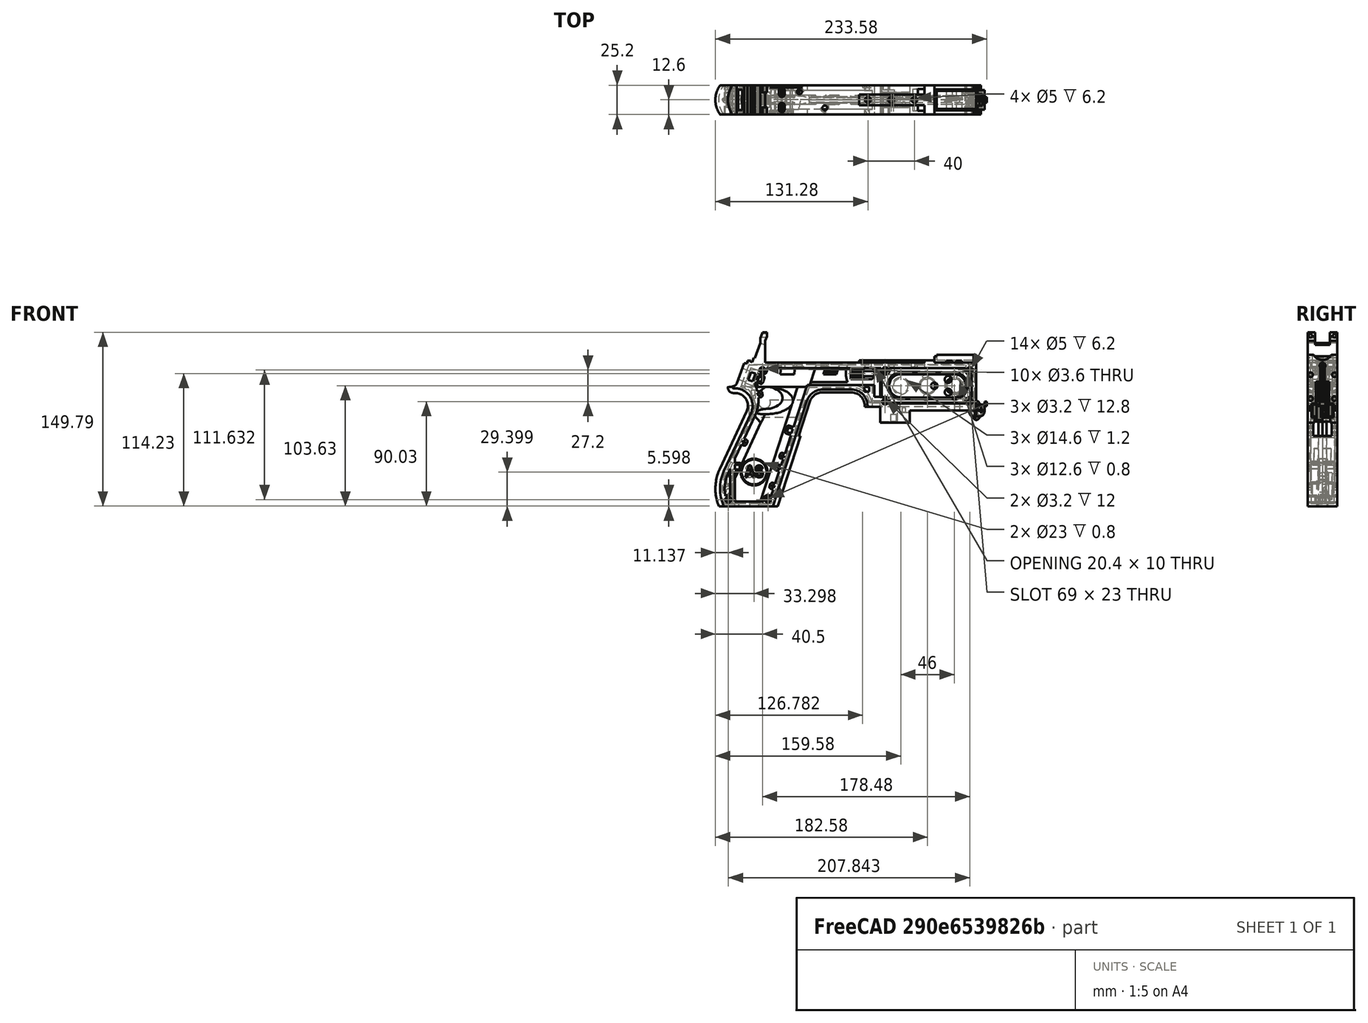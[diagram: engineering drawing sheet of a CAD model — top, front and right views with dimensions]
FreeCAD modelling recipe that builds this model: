
FCSTD DOCUMENT  (FreeCAD 1.0R39319 (Git))
Label: PICON-OF_ver_51
License: All rights reserved
LicenseURL: https://en.wikipedia.org/wiki/All_rights_reserved
objects: Sketcher::SketchObject×123, Part::Extrusion×63, Part::Cut×48, PartDesign::Pad×29, PartDesign::Pocket×20, PartDesign::Chamfer×15, PartDesign::Body×10, PartDesign::Fillet×6, Part::MultiFuse×5, Part::Part2DObjectPython×4, PartDesign::SubtractivePipe×4, PartDesign::SubtractiveLoft×4, PartDesign::Plane×3, PartDesign::SubShapeBinder×2, Part::Sweep×1, PartDesign::ShapeBinder×1, Mesh::Feature×1, PartDesign::Point×1, PartDesign::Groove×1
note: 621 computed .brp shape members not serialized (recipe doc carries the construction recipe); baked Part::Feature solids carry a one-line shape summary decoded from their .brp

FEATURE [Sketcher::SketchObject] Sketch  label="corpo principale"
  ArcFitTolerance = 1e-06
  AttacherType = Attacher::AttachEngine3D
  AttachmentSupport = -> [XZ_Plane]
  FullyConstrained = true
  MakeInternals = false
  MapMode = 5
  Placement = pos=(0,0,0) rot=(1,0,0;1.5708rad)
  sketch-geometry (65):
    g0: LineSegment StartX=0 StartY=0 StartZ=0 EndX=-57.2 EndY=0 EndZ=0
    g1: LineSegment StartX=-57.2 StartY=0 StartZ=0 EndX=-57.2 EndY=-10.4 EndZ=0
    g2: LineSegment StartX=-57.2 StartY=-10.4 StartZ=0 EndX=-82.8 EndY=-10.4 EndZ=0
    g3: LineSegment StartX=-82.8 StartY=-10.4 StartZ=0 EndX=-82.8 EndY=3.2 EndZ=0
    g4: LineSegment StartX=-82.8 StartY=3.2 StartZ=0 EndX=-93.6 EndY=3.2 EndZ=0
    g5: LineSegment StartX=-93.6 StartY=3.2 StartZ=0 EndX=-93.6 EndY=4 EndZ=0
    g6: LineSegment StartX=-107.6 StartY=18 StartZ=0 EndX=-132.428 EndY=18 EndZ=0
    g7: LineSegment StartX=-145.743 StartY=8.32624 StartZ=0 EndX=-175.232 EndY=-82.4316 EndZ=0
    g8: LineSegment StartX=-175.232 StartY=-82.4316 StartZ=0 EndX=-217.232 EndY=-82.4316 EndZ=0
    g9: LineSegment StartX=-217.232 StartY=-52.1862 StartZ=0 EndX=-193.988 EndY=-2.33927 EndZ=0
    g10: LineSegment StartX=-206.196 StartY=23.0857 StartZ=0 EndX=-199.861 EndY=40.4914 EndZ=0
    g11: LineSegment StartX=-199.861 StartY=40.4914 StartZ=0 EndX=-197.061 EndY=40.4914 EndZ=0
    g12: LineSegment StartX=-197.061 StartY=40.4914 StartZ=0 EndX=-197.061 EndY=42.8914 EndZ=0
    g13: LineSegment StartX=-197.061 StartY=42.8914 StartZ=0 EndX=-194.261 EndY=42.8914 EndZ=0
    g14: LineSegment StartX=-194.261 StartY=42.8914 StartZ=0 EndX=-194.535 EndY=42.1397 EndZ=0
    g15: LineSegment StartX=-194.535 StartY=42.1397 StartZ=0 EndX=-193.031 EndY=41.5924 EndZ=0
    g16: LineSegment StartX=-193.031 StartY=41.5924 StartZ=0 EndX=-191.663 EndY=45.3512 EndZ=0
    g17: LineSegment StartX=-191.663 StartY=45.3512 StartZ=0 EndX=-190.536 EndY=44.9408 EndZ=0
    g18: LineSegment StartX=-190.536 StartY=44.9408 StartZ=0 EndX=-185.747 EndY=58.0965 EndZ=0
    g19: LineSegment StartX=-185.747 StartY=58.0965 StartZ=0 EndX=-185.747 EndY=62.0965 EndZ=0
    g20: LineSegment StartX=-185.747 StartY=62.0965 StartZ=0 EndX=-183.832 EndY=67.3588 EndZ=0
    g21: LineSegment StartX=-183.832 StartY=67.3588 StartZ=0 EndX=-180.232 EndY=67.3588 EndZ=0
    g22: LineSegment StartX=-180.232 StartY=67.3588 StartZ=0 EndX=-180.232 EndY=63.7588 EndZ=0
    g23: LineSegment StartX=-180.232 StartY=63.7588 StartZ=0 EndX=-181.6 EndY=60 EndZ=0
    g24: LineSegment StartX=-181.6 StartY=60 StartZ=0 EndX=-181.6 EndY=41.2 EndZ=0
    g25: LineSegment StartX=-181.6 StartY=41.2 StartZ=0 EndX=-100.8 EndY=41.2 EndZ=0
    g26: LineSegment StartX=-36 StartY=43.2 StartZ=0 EndX=-36 EndY=41.2 EndZ=0
    g27: LineSegment StartX=0 StartY=48 StartZ=0 EndX=0 EndY=0 EndZ=0
    g28: LineSegment StartX=-209.901 StartY=19.85 StartZ=0 EndX=-209.901 EndY=20.1 EndZ=0
    g29: LineSegment StartX=-208.001 StartY=22 StartZ=0 EndX=-207.747 EndY=22 EndZ=0
    g30: LineSegment StartX=-207.583 StartY=19 StartZ=0 EndX=-209.051 EndY=19 EndZ=0
    g31: ArcOfCircle CenterX=-208.001 CenterY=20.1 CenterZ=0 NormalX=0 NormalY=0 NormalZ=1 AngleXU=0 Radius=1.9 StartAngle=1.5708 EndAngle=3.14159
    g32: GeomPoint [constr] X=-209.901 Y=22 Z=0
    g33: ArcOfCircle CenterX=-209.051 CenterY=19.85 CenterZ=0 NormalX=0 NormalY=0 NormalZ=1 AngleXU=0 Radius=0.85 StartAngle=3.14159 EndAngle=4.71239
    g34: GeomPoint [constr] X=-209.901 Y=19 Z=0
    g35: ArcOfCircle CenterX=-207.747 CenterY=23.65 CenterZ=0 NormalX=0 NormalY=0 NormalZ=1 AngleXU=0 Radius=1.65 StartAngle=4.71239 EndAngle=5.93412
    g36: GeomPoint [constr] X=-206.591 Y=22 Z=0
    g37: LineSegment StartX=-4 StartY=6 StartZ=0 EndX=-4 EndY=36.4 EndZ=0
    g38: LineSegment StartX=-4 StartY=36.4 StartZ=0 EndX=-185.2 EndY=36.4 EndZ=0
    g39: LineSegment StartX=-185.2 StartY=36.4 StartZ=0 EndX=-190.441 EndY=22 EndZ=0
    g40: LineSegment StartX=-214.575 StartY=-78.4316 StartZ=0 EndX=-178.142 EndY=-78.4316 EndZ=0
    g41: LineSegment StartX=-178.142 StartY=-78.4316 StartZ=0 EndX=-145.51 EndY=22 EndZ=0
    g42: LineSegment StartX=-145.51 StartY=22 StartZ=0 EndX=-87.91 EndY=22 EndZ=0
    g43: LineSegment StartX=-87.91 StartY=22 StartZ=0 EndX=-87.91 EndY=11.6 EndZ=0
    g44: LineSegment StartX=-87.91 StartY=11.6 StartZ=0 EndX=-80.11 EndY=11.6 EndZ=0
    g45: LineSegment StartX=-80.11 StartY=11.6 StartZ=0 EndX=-80.11 EndY=6 EndZ=0
    g46: LineSegment StartX=-80.11 StartY=6 StartZ=0 EndX=-4 EndY=6 EndZ=0
    g47: LineSegment StartX=-190.363 StartY=-4.02975 StartZ=0 EndX=-213.607 EndY=-53.8767 EndZ=0
    g48: ArcOfCircle CenterX=-132.428 CenterY=4 CenterZ=0 NormalX=0 NormalY=0 NormalZ=1 AngleXU=0 Radius=14 StartAngle=1.5708 EndAngle=2.82743
    g49: GeomPoint [constr] X=-142.6 Y=18 Z=0
    g50: ArcOfCircle CenterX=-107.6 CenterY=4 CenterZ=0 NormalX=0 NormalY=0 NormalZ=1 AngleXU=0 Radius=14 StartAngle=0 EndAngle=1.5708
    g51: GeomPoint [constr] X=-93.6 Y=18 Z=0
    g52: ArcOfCircle CenterX=-184.801 CenterY=-67.3089 CenterZ=0 NormalX=0 NormalY=0 NormalZ=1 AngleXU=0 Radius=35.7833 StartAngle=2.70526 EndAngle=3.57792
    g53: ArcOfCircle CenterX=-207.583 CenterY=4 CenterZ=0 NormalX=0 NormalY=0 NormalZ=1 AngleXU=0 Radius=15 StartAngle=5.84685 EndAngle=7.85398
    g54: LineSegment [constr] StartX=-213.607 StartY=-53.8767 StartZ=0 EndX=-217.232 EndY=-52.1862 EndZ=0
    g55: ArcOfCircle CenterX=-184.801 CenterY=-67.3089 CenterZ=0 NormalX=0 NormalY=0 NormalZ=1 AngleXU=0 Radius=31.7833 StartAngle=2.70526 EndAngle=3.49911
    g56: ArcOfCircle CenterX=-218.095 CenterY=8.90192 CenterZ=0 NormalX=0 NormalY=0 NormalZ=1 AngleXU=0 Radius=30.5989 StartAngle=5.84685 EndAngle=6.72553
    g57: LineSegment StartX=-44.6 StartY=43.2 StartZ=0 EndX=-36 EndY=43.2 EndZ=0
    g58: LineSegment StartX=-100.8 StartY=41.2 StartZ=0 EndX=-44.6 EndY=41.2 EndZ=0
    g59: LineSegment StartX=-44.6 StartY=41.2 StartZ=0 EndX=-44.6 EndY=43.2 EndZ=0
    g60: LineSegment StartX=-2.4 StartY=48 StartZ=0 EndX=0 EndY=48 EndZ=0
    g61: LineSegment StartX=-36 StartY=41.2 StartZ=0 EndX=-2.4 EndY=41.2 EndZ=0
    g62: LineSegment StartX=-2.4 StartY=41.2 StartZ=0 EndX=-2.4 EndY=48 EndZ=0
    g63: LineSegment [constr] StartX=-181.6 StartY=36.4 StartZ=0 EndX=-152.209 EndY=36.4 EndZ=0
    g64: LineSegment [constr] StartX=-181.6 StartY=36.4 StartZ=0 EndX=-130.41 EndY=36.4 EndZ=0
  constraints (183):
    c: Coincident(g-1,g0)
    c: PointOnObject(g0,g-1)
    c: Coincident(g0,g1)
    c: Vertical(g1)
    c: Coincident(g1,g2)
    c: Horizontal(g2)
    c: Coincident(g2,g3)
    c: Vertical(g3)
    c: Coincident(g3,g4)
    c: Coincident(g4,g5)
    c: Vertical(g5)
    c: Horizontal(g6)
    c: Coincident(g7,g8)
    c: Horizontal(g8)
    c: Coincident(g10,g11)
    c: Horizontal(g11)
    c: Coincident(g11,g12)
    c: Vertical(g12)
    c: Coincident(g12,g13)
    c: Horizontal(g13)
    c: Coincident(g13,g14)
    c: Coincident(g14,g15)
    c: Coincident(g15,g16)
    c: Coincident(g16,g17)
    c: Coincident(g17,g18)
    c: Coincident(g18,g19)
    c: Vertical(g19)
    c: Coincident(g19,g20)
    c: Coincident(g20,g21)
    c: Horizontal(g21)
    c: Coincident(g21,g22)
    c: Vertical(g22)
    c: Coincident(g22,g23)
    c: Coincident(g23,g24)
    c: Vertical(g24)
    c: Coincident(g24,g25)
    c: Horizontal(g25)
    c: Coincident(g57,g26)
    c: Vertical(g26)
    c: Coincident(g26,g61)
    c: PointOnObject(g60,g-2)
    c: Coincident(g60,g27)
    c: Coincident(g27,g0)
    c: DistanceY(g27,g27) = 48
    c: DistanceY(g1,g1) = 10.4
    c: DistanceX(g0,g0) = 57.2
    c: DistanceX(g2,g2) = 25.6
    c: Horizontal(g4)
    c: DistanceY(g3,g3) = 13.6
    c: DistanceX(g4,g4) = 10.8
    c: DistanceY(g5,g51) = 14.8
    c: DistanceX(g49,g51) = 49
    c: Distance(g7,g49) = 105.6
    c: DistanceX(g61,g60) = 36
    c: DistanceX(g25,g25) = 80.8
    c: DistanceY(g24,g24) = 18.8
    c: DistanceY(g22,g22) = 3.6
    c: Distance(g23) = 4
    c: Angle(g-1,g23) = 1.22173
    c: DistanceX(g21,g21) = 3.6
    c: Distance(g20) = 5.6
    c: Angle(g-1,g20) = 1.22173
    c: DistanceY(g19,g19) = 4
    c: Distance(g18) = 14
    c: Angle(g-1,g18) = 1.22173
    c: Distance(g17) = 1.2
    c: Distance(g16) = 4
    c: Angle(g16) = 1.22173
    c: Perpendicular(g18,g17)
    c: Distance(g15) = 1.6
    c: Perpendicular(g16,g15)
    c: Distance(g14) = 0.8
    c: DistanceX(g13,g13) = 2.8
    c: Perpendicular(g15,g14)
    c: DistanceY(g12,g12) = 2.4
    c: DistanceX(g11,g11) = 2.8
    c: Distance(g9) = 55
    c: Angle(g9,g-1) = 2.00713
    c: Horizontal(g29)
    c: Vertical(g28)
    c: Horizontal(g30)
    c: PointOnObject(g32,g29)
    c: PointOnObject(g32,g28)
    c: Tangent(g29,g31) = 1.5708
    c: Tangent(g28,g31) = 1.5708
    c: PointOnObject(g34,g28)
    c: PointOnObject(g34,g30)
    c: Tangent(g28,g33) = 1.5708
    c: Tangent(g30,g33) = 1.5708
    c: PointOnObject(g36,g29)
    c: PointOnObject(g36,g10)
    c: Tangent(g29,g35) = -1.5708
    c: Tangent(g10,g35) = -1.5708
    c: Angle(g-1,g10) = 1.22173
    c: Radius(g35) = 1.65
    c: Vertical(g37)
    c: Coincident(g37,g38)
    c: Horizontal(g38)
    c: Coincident(g38,g39)
    c: Horizontal(g40)
    c: Coincident(g40,g41)
    c: Coincident(g41,g42)
    c: Horizontal(g42)
    c: Coincident(g42,g43)
    c: Vertical(g43)
    c: Coincident(g43,g44)
    c: Horizontal(g44)
    c: Coincident(g44,g45)
    c: Vertical(g45)
    c: Coincident(g45,g46)
    c: Coincident(g46,g37)
    c: Horizontal(g46)
    c: DistanceY(g0,g37) = 6
    c: DistanceX(g37,g0) = 4
    c: DistanceY(g37,g25) = 4.8
    c: DistanceX(g38,g38) = 181.2
    c: DistanceX(g42,g42) = 57.6
    c: DistanceY(g49,g41) = 4
    c: DistanceX(g41,g49) = 2.91
    c: DistanceY(g43,g43) = 10.4
    c: DistanceX(g44,g44) = 7.8
    c: DistanceY(g7,g40) = 4
    c: Distance(g47) = 55
    c: Angle(g-1,g39) = 1.22173
    c: PointOnObject(g49,g7)
    c: PointOnObject(g49,g6)
    c: Tangent(g7,g48) = -1.5708
    c: Tangent(g6,g48) = -1.5708
    c: PointOnObject(g51,g5)
    c: PointOnObject(g51,g6)
    c: Tangent(g5,g50) = -1.5708
    c: Tangent(g6,g50) = -1.5708
    c: Radius(g50) = 14
    c: Radius(g48) = 14
    c: DistanceX(g8,g8) = 42
    c: Angle(g7,g-1) = 1.88496
    c: Parallel(g41,g7)
    c: Parallel(g47,g9)
    c: Coincident(g52,g8)
    c: Tangent(g52,g9) = 1.5708
    c: DistanceX(g9,g8) = 0
    c: Tangent(g53,g9) = -1.5708
    c: Tangent(g53,g30) = -1.5708
    c: Diameter(g53) = 30
    c: DistanceY(g53,g0) = -4
    c: Coincident(g54,g47)
    c: Distance(g54) = 4
    c: Coincident(g54,g9)
    c: Coincident(g55,g40)
    c: Tangent(g55,g47) = -1.5708
    c: Coincident(g52,g55)
    c: Coincident(g56,g39)
    c: Tangent(g56,g47) = 1.5708
    c: Horizontal(g57)
    c: DistanceX(g57,g57) = 8.6
    c: Coincident(g58,g25)
    c: Horizontal(g58)
    c: Coincident(g59,g58)
    c: Vertical(g59)
    c: DistanceY(g58,g57) = 2
    c: DistanceX(g58,g58) = 56.2
    c: Coincident(g59,g57)
    c: DistanceY(g41,g36) = 0
    c: DistanceY(g36,g39) = 0
    c: DistanceY(g28,g28) = 0.25
    c: DistanceX(g30,g36) = 2.46
    c: DistanceX(g28,g29) = 1.9
    c: Coincident(g62,g60)
    c: Horizontal(g60)
    c: DistanceX(g62,g27) = 2.4
    c: Coincident(g61,g62)
    c: DistanceY(g26,g26) = 2
    c: Vertical(g62)
    c: DistanceY(g61,g60) = 6.8
    c: Horizontal(g61)
    c: Distance(g63) = 29.391
    c: PointOnObject(g63,g38)
    c: PointOnObject(g63,g38)
    c: Distance(g64) = 51.19
    c: PointOnObject(g64,g38)
    c: PointOnObject(g64,g38)
    c: DistanceX(g24,g63) = 0
    c: DistanceX(g24,g64) = 0
FEATURE [Part::Extrusion] Extrude  label="Extrude corpo principale"
  Base = -> Sketch
  Dir = (0,-1,2e-16)
  DirMode = 2
  FaceMakerClass = Part::FaceMakerBullseye
  FaceMakerMode = 3
  LengthFwd = 25.2
  LengthRev = 12.6
  Solid = true
  Symmetric = true
FEATURE [Sketcher::SketchObject] Sketch002  label="scavo grilletto"
  ArcFitTolerance = 1e-06
  AttachmentSupport = -> [XZ_Plane]
  ExternalGeometry = -> [Sketch]
  FullyConstrained = true
  MakeInternals = false
  MapMode = 5
  Placement = pos=(0,0,0) rot=(1,0,0;1.5708rad)
  sketch-geometry (4):
    g0: LineSegment StartX=-89.51 StartY=22 StartZ=0 EndX=-152.71 EndY=22 EndZ=0
    g1: LineSegment StartX=-152.71 StartY=22 StartZ=0 EndX=-167.006 EndY=-22 EndZ=0
    g2: LineSegment StartX=-167.006 StartY=-22 StartZ=0 EndX=-89.51 EndY=-22 EndZ=0
    g3: LineSegment StartX=-89.51 StartY=-22 StartZ=0 EndX=-89.51 EndY=22 EndZ=0
  constraints (12):
    c: Horizontal(g0)
    c: Coincident(g0,g1)
    c: Coincident(g1,g2)
    c: Horizontal(g2)
    c: Coincident(g2,g3)
    c: Coincident(g3,g0)
    c: Vertical(g3)
    c: Angle(g1,g0) = 1.88496
    c: DistanceY(g3,g3) = 44
    c: DistanceX(g0,g0) = 63.2
    c: DistanceX(g0,g-3) = 1.6
    c: DistanceY(g-3,g0) = 0
FEATURE [Sketcher::SketchObject] Sketch004  label="traiettoria arrotondamento impugnatura anteriore"
  ArcFitTolerance = 1e-06
  AttachmentSupport = -> [XZ_Plane]
  ExternalGeometry = -> [Sketch]
  FullyConstrained = true
  MakeInternals = false
  MapMode = 5
  Placement = pos=(0,0,0) rot=(1,0,0;1.5708rad)
  sketch-geometry (13):
    g0: LineSegment StartX=-175.232 StartY=-82.4316 StartZ=0 EndX=-145.743 EndY=8.32624 EndZ=0
    g1: LineSegment StartX=-93.6 StartY=3.2 StartZ=0 EndX=-93.6 EndY=4 EndZ=0
    g2: LineSegment StartX=-132.428 StartY=18 StartZ=0 EndX=-107.6 EndY=18 EndZ=0
    g3: ArcOfCircle CenterX=-132.428 CenterY=4 CenterZ=0 NormalX=0 NormalY=0 NormalZ=1 AngleXU=0 Radius=14 StartAngle=1.5708 EndAngle=2.82743
    g4: ArcOfCircle CenterX=-107.6 CenterY=4 CenterZ=0 NormalX=0 NormalY=0 NormalZ=1 AngleXU=0 Radius=14 StartAngle=0 EndAngle=1.5708
    g5: LineSegment StartX=-175.232 StartY=-82.4316 StartZ=0 EndX=-217.232 EndY=-82.4316 EndZ=0
    g6: LineSegment StartX=-217.232 StartY=-52.1862 StartZ=0 EndX=-193.988 EndY=-2.33927 EndZ=0
    g7: LineSegment StartX=-209.051 StartY=19 StartZ=0 EndX=-207.583 EndY=19 EndZ=0
    g8: LineSegment StartX=-209.901 StartY=20.1 StartZ=0 EndX=-209.901 EndY=19.85 EndZ=0
    g9: ArcOfCircle CenterX=-184.801 CenterY=-67.3089 CenterZ=0 NormalX=0 NormalY=0 NormalZ=1 AngleXU=0 Radius=35.7833 StartAngle=2.70526 EndAngle=3.57792
    g10: ArcOfCircle CenterX=-207.583 CenterY=4 CenterZ=0 NormalX=0 NormalY=0 NormalZ=1 AngleXU=0 Radius=15 StartAngle=5.84685 EndAngle=7.85398
    g11: ArcOfCircle CenterX=-209.051 CenterY=19.85 CenterZ=0 NormalX=0 NormalY=0 NormalZ=1 AngleXU=0 Radius=0.85 StartAngle=3.14159 EndAngle=4.71239
    g12: ArcOfCircle CenterX=-208.001 CenterY=20.1 CenterZ=0 NormalX=0 NormalY=0 NormalZ=1 AngleXU=0 Radius=1.9 StartAngle=1.5708 EndAngle=3.14159
  constraints (26):
    c: Coincident(g0,g-3)
    c: Coincident(g0,g-6)
    c: Coincident(g1,g-8)
    c: Coincident(g1,g-7)
    c: Coincident(g2,g-5)
    c: Coincident(g2,g-4)
    c: Coincident(g3,g2)
    c: Tangent(g3,g0) = 1.5708
    c: Coincident(g4,g1)
    c: Tangent(g4,g2) = 1.5708
    c: Coincident(g5,g0)
    c: Coincident(g5,g-9)
    c: Coincident(g6,g-12)
    c: Coincident(g6,g-11)
    c: Coincident(g7,g-15)
    c: Coincident(g7,g-14)
    c: Coincident(g8,g-16)
    c: Coincident(g8,g-17)
    c: Tangent(g9,g6) = 1.5708
    c: Coincident(g9,g5)
    c: Coincident(g10,g7)
    c: Tangent(g10,g6) = -1.5708
    c: Tangent(g11,g7) = -1.5708
    c: Coincident(g11,g8)
    c: Tangent(g12,g8) = -1.5708
    c: Coincident(g12,g-17)
FEATURE [PartDesign::Plane] DatumPlane  label="Piano per disegno arrotondamento impugnatura"
  AttachmentSupport = -> [Sketch]
  Length = 73.6581
  MapMode = 7
  Placement = pos=(-145.743,1.8e-15,8.32624) rot=(0.154555,0.154555,0.97582;1.59527rad)
  ResizeMode = 0
  Width = 303.511
FEATURE [Sketcher::SketchObject] Sketch005  label="forma arrotondamento impugnatura anteriore"
  ArcFitTolerance = 1e-06
  AttachmentSupport = -> [DatumPlane]
  FullyConstrained = true
  MakeInternals = false
  MapMode = 5
  Placement = pos=(-145.743,1.8e-15,8.32624) rot=(0.154555,0.154555,0.97582;1.59527rad)
  sketch-geometry (5):
    g0: GeomPoint [constr] X=0 Y=-4 Z=0
    g1: GeomPoint [constr] X=-12.6 Y=7.1e-15 Z=0
    g2: GeomPoint [constr] X=12.6 Y=4.97e-14 Z=0
    g3: LineSegment StartX=-12.6 StartY=7.1e-15 StartZ=0 EndX=12.6 EndY=4.97e-14 EndZ=0
    g4: ArcOfCircle CenterX=-3.88e-14 CenterY=17.845 CenterZ=0 NormalX=0 NormalY=0 NormalZ=1 AngleXU=0 Radius=21.845 StartAngle=4.09759 EndAngle=5.32718
  constraints (11):
    c: DistanceY(g0,g-1) = 4
    c: DistanceX(g-1,g0) = 0
    c: DistanceX(g1,g-1) = 12.6
    c: DistanceX(g-1,g2) = 12.6
    c: DistanceY(g-1,g2) = 0
    c: DistanceY(g-1,g1) = 0
    c: Coincident(g3,g1)
    c: Coincident(g3,g2)
    c: Coincident(g4,g1)
    c: Coincident(g4,g2)
    c: PointOnObject(g0,g4)
FEATURE [Part::Sweep] Sweep  label="Sweep impugnatura"
  Frenet = true
  Sections = -> [Sketch005]
  Solid = true
  Spine = -> Sketch [Edge32,Edge33,Edge34,Edge35,Edge36,Edge37,Edge38,Edge39,Edge40,Edge41,Edge42,Edge43,Edge44]
  Transition = 1
FEATURE [Sketcher::SketchObject] Sketch008  label="buchi e pulizie varie"
  ArcFitTolerance = 1e-06
  AttachmentSupport = -> [XZ_Plane]
  ExternalGeometry = -> [Sketch]
  FullyConstrained = true
  MakeInternals = false
  MapMode = 5
  Placement = pos=(0,0,0) rot=(1,0,0;1.5708rad)
  sketch-geometry (26):
    g0: LineSegment StartX=-96.278 StartY=20.155 StartZ=0 EndX=-92.278 EndY=20.155 EndZ=0
    g1: LineSegment StartX=-92.278 StartY=20.155 StartZ=0 EndX=-92.278 EndY=16.155 EndZ=0
    g2: LineSegment StartX=-92.278 StartY=16.155 StartZ=0 EndX=-96.278 EndY=16.155 EndZ=0
    g3: LineSegment StartX=-96.278 StartY=16.155 StartZ=0 EndX=-96.278 EndY=20.155 EndZ=0
    g4: LineSegment StartX=-222.232 StartY=-82.4316 StartZ=0 EndX=-170.232 EndY=-82.4316 EndZ=0
    g5: LineSegment StartX=-170.232 StartY=-82.4316 StartZ=0 EndX=-170.232 EndY=-86.4316 EndZ=0
    g6: LineSegment StartX=-170.232 StartY=-86.4316 StartZ=0 EndX=-222.232 EndY=-86.4316 EndZ=0
    g7: LineSegment StartX=-222.232 StartY=-86.4316 StartZ=0 EndX=-222.232 EndY=-82.4316 EndZ=0
    g8: LineSegment StartX=-213.901 StartY=20.1 StartZ=0 EndX=-213.901 EndY=26 EndZ=0
    g9: LineSegment StartX=-213.901 StartY=26 StartZ=0 EndX=-206.196 EndY=26 EndZ=0
    g10: LineSegment StartX=-17.4 StartY=42.8 StartZ=0 EndX=-12.4 EndY=42.8 EndZ=0
    g11: LineSegment StartX=-12.4 StartY=42.8 StartZ=0 EndX=-12.4 EndY=41.2 EndZ=0
    g12: LineSegment StartX=-12.4 StartY=41.2 StartZ=0 EndX=-17.4 EndY=41.2 EndZ=0
    g13: LineSegment StartX=-17.4 StartY=41.2 StartZ=0 EndX=-17.4 EndY=42.8 EndZ=0
    g14: LineSegment StartX=-25.9 StartY=42.8 StartZ=0 EndX=-20.9 EndY=42.8 EndZ=0
    g15: LineSegment StartX=-20.9 StartY=42.8 StartZ=0 EndX=-20.9 EndY=41.2 EndZ=0
    g16: LineSegment StartX=-20.9 StartY=41.2 StartZ=0 EndX=-25.9 EndY=41.2 EndZ=0
    g17: LineSegment StartX=-25.9 StartY=41.2 StartZ=0 EndX=-25.9 EndY=42.8 EndZ=0
    g18: GeomPoint [constr] X=-206.196 Y=23.0857 Z=0
    g19: GeomPoint [constr] X=-213.901 Y=20.1 Z=0
    g20: BSplineCurve PolesCount=4 KnotsCount=2 Degree=3 IsPeriodic=0
    g21-g24: Circle [constr] x4 (B-spline internal-alignment scaffolding for g20; pole/knot coordinates omitted)
    g25: LineSegment StartX=-206.196 StartY=26 StartZ=0 EndX=-206.196 EndY=23.0857 EndZ=0
  constraints (73):
    c: Horizontal(g0)
    c: Coincident(g1,g0)
    c: Vertical(g1)
    c: Coincident(g2,g1)
    c: Horizontal(g2)
    c: Coincident(g3,g2)
    c: Coincident(g3,g0)
    c: Vertical(g3)
    c: DistanceX(g0,g-4) = 4.368
    c: DistanceY(g0,g-4) = 1.845
    c: DistanceY(g1,g1) = 4
    c: DistanceX(g2,g2) = 4
    c: Horizontal(g4)
    c: Coincident(g5,g4)
    c: Vertical(g5)
    c: Coincident(g6,g5)
    c: Horizontal(g6)
    c: Coincident(g7,g6)
    c: Coincident(g7,g4)
    c: Vertical(g7)
    c: DistanceY(g7,g7) = 4
    c: DistanceX(g4,g-5) = 5
    c: DistanceX(g-5,g4) = 5
    c: DistanceY(g4,g-5) = 0
    c: Coincident(g9,g8)
    c: Parallel(g9,g-6)
    c: DistanceX(g8,g-8) = 4
    c: Horizontal(g10)
    c: Coincident(g11,g10)
    c: Vertical(g11)
    c: Coincident(g12,g11)
    c: Horizontal(g12)
    c: Coincident(g13,g12)
    c: Coincident(g13,g10)
    c: Vertical(g13)
    c: Horizontal(g14)
    c: Coincident(g15,g14)
    c: Vertical(g15)
    c: Coincident(g16,g15)
    c: Horizontal(g16)
    c: Coincident(g17,g16)
    c: Coincident(g17,g14)
    c: Vertical(g17)
    c: DistanceY(g11,g10) = 1.6
    c: DistanceX(g10,g10) = 5
    c: DistanceY(g15,g14) = 1.6
    c: DistanceX(g14,g14) = 5
    c: DistanceX(g15,g12) = 3.5
    c: DistanceX(g11,g-9) = 10
    c: DistanceY(g-9,g11) = 0
    c: DistanceY(g-9,g15) = 0
    c: Perpendicular(g8,g9)
    c: DistanceY(g-7,g9) = 4
    c: DistanceY(g8,g-8) = 0
    c: InternalAlignment(g18,g20)
    c: InternalAlignment(g19,g20)
    c: InternalAlignment(g21,g20)
    c: Weight(g21) = 1
    c: InternalAlignment(g22,g20)
    c: Equal(g22,g21)
    c: InternalAlignment(g23,g20)
    c: Equal(g23,g21)
    c: InternalAlignment(g24,g20)
    c: Equal(g24,g21)
    c: Coincident(g18,g-12)
    c: Coincident(g19,g8)
    c: Coincident(g25,g9)
    c: Coincident(g25,g20)
    c: Vertical(g25)
    c: DistanceY(g20,g23) = 0
    c: DistanceY(g22,g18) = 2.26
    c: DistanceX(g22,g18) = 0.93
    c: DistanceX(g20,g23) = 2.9
FEATURE [Part::Extrusion] Extrude004  label="Extrude Buchi e pulizie varie"
  Base = -> Sketch008
  Dir = (0,-1,2e-16)
  DirMode = 2
  FaceMakerClass = Part::FaceMakerBullseye
  FaceMakerMode = 3
  LengthFwd = 25.2
  LengthRev = 0
  Solid = true
  Symmetric = true
FEATURE [Sketcher::SketchObject] Sketch009  label="rinforzi"
  ArcFitTolerance = 1e-06
  AttachmentSupport = -> [XZ_Plane]
  ExternalGeometry = -> [Sketch]
  FullyConstrained = true
  MakeInternals = false
  MapMode = 5
  Placement = pos=(0,0,0) rot=(1,0,0;1.5708rad)
  sketch-geometry (9):
    g0: LineSegment StartX=-87.91 StartY=22 StartZ=0 EndX=-87.91 EndY=36.4 EndZ=0
    g1: LineSegment StartX=-87.91 StartY=36.4 StartZ=0 EndX=-97.91 EndY=36.4 EndZ=0
    g2: LineSegment StartX=-97.91 StartY=36.4 StartZ=0 EndX=-97.91 EndY=22 EndZ=0
    g3: LineSegment StartX=-97.91 StartY=22 StartZ=0 EndX=-87.91 EndY=22 EndZ=0
    g4: LineSegment StartX=-149.713 StartY=9.06563 StartZ=0 EndX=-154.586 EndY=-5.93437 EndZ=0
    g5: LineSegment StartX=-154.586 StartY=-5.93437 StartZ=0 EndX=-191.863 EndY=-5.93437 EndZ=0
    g6: LineSegment StartX=-191.863 StartY=-5.93437 StartZ=0 EndX=-191.863 EndY=9.06563 EndZ=0
    g7: LineSegment StartX=-191.863 StartY=9.06563 StartZ=0 EndX=-149.713 EndY=9.06563 EndZ=0
    g8: LineSegment [constr] StartX=-145.51 StartY=22 StartZ=0 EndX=-149.713 EndY=9.06563 EndZ=0
  constraints (25):
    c: Vertical(g0)
    c: Coincident(g1,g0)
    c: Horizontal(g1)
    c: Coincident(g2,g1)
    c: Vertical(g2)
    c: Coincident(g3,g2)
    c: Coincident(g3,g0)
    c: Horizontal(g3)
    c: Coincident(g0,g-4)
    c: DistanceX(g3,g3) = 10
    c: DistanceY(g0,g-3) = 0
    c: Coincident(g5,g4)
    c: Horizontal(g5)
    c: Coincident(g6,g5)
    c: Vertical(g6)
    c: Coincident(g7,g6)
    c: Coincident(g7,g4)
    c: Horizontal(g7)
    c: Distance(g8) = 13.6
    c: Parallel(g-6,g8)
    c: Coincident(g-6,g8)
    c: Parallel(g4,g-6)
    c: DistanceY(g4,g4) = 15
    c: Coincident(g4,g8)
    c: DistanceX(g-5,g5) = -1.5
FEATURE [Part::Extrusion] Extrude001  label="Extrude scavo grilletto"
  Base = -> Sketch002
  Dir = (0,-1,2e-16)
  DirMode = 2
  FaceMakerClass = Part::FaceMakerBullseye
  FaceMakerMode = 3
  LengthFwd = 16
  LengthRev = 0
  Solid = true
  Symmetric = true
FEATURE [Part::Extrusion] Extrude005  label="Extrude Rinforzi"
  Base = -> Sketch009
  Dir = (0,-1,2e-16)
  DirMode = 2
  FaceMakerClass = Part::FaceMakerBullseye
  FaceMakerMode = 3
  LengthFwd = 2
  LengthRev = 0
  Placement = pos=(0,12.6,0) rot=(0,0,1;0rad)
  Solid = true
  Symmetric = false
FEATURE [PartDesign::ShapeBinder] CopyCut
  TraceSupport = false
FEATURE [PartDesign::Plane] DatumPlane001
  AttachmentSupport = -> [CopyCut]
  Length = 283.944
  MapMode = 5
  Placement = pos=(0,12.6,0) rot=(0,0.707107,0.707107;3.14159rad)
  ResizeMode = 0
  Width = 188.15
FEATURE [Sketcher::SketchObject] Sketch010  label="buco neopixel"
  ArcFitTolerance = 1e-06
  AttachmentSupport = -> [XZ_Plane]
  ExternalGeometry = -> [Sketch]
  FullyConstrained = true
  MakeInternals = false
  MapMode = 5
  Placement = pos=(0,0,0) rot=(1,0,0;1.5708rad)
  sketch-geometry (5):
    g0: LineSegment [constr] StartX=-199.861 StartY=40.4914 StartZ=0 EndX=-201.368 EndY=36.3521 EndZ=0
    g1: LineSegment StartX=-201.368 StartY=36.3521 StartZ=0 EndX=-204.932 EndY=26.5605 EndZ=0
    g2: LineSegment StartX=-201.368 StartY=36.3521 StartZ=0 EndX=-180.2 EndY=28.6477 EndZ=0
    g3: LineSegment StartX=-180.2 StartY=28.6477 StartZ=0 EndX=-183.764 EndY=18.8561 EndZ=0
    g4: LineSegment StartX=-183.764 StartY=18.8561 StartZ=0 EndX=-204.932 EndY=26.5605 EndZ=0
  constraints (14):
    c: Parallel(g0,g-3)
    c: Distance(g0) = 4.405
    c: Coincident(g0,g-3)
    c: Coincident(g2,g1)
    c: Coincident(g3,g2)
    c: Coincident(g4,g3)
    c: Coincident(g4,g1)
    c: Parallel(g1,g-3)
    c: Distance(g1) = 10.42
    c: Coincident(g1,g0)
    c: Parallel(g2,g4)
    c: Perpendicular(g1,g2)
    c: DistanceX(g-4,g2) = 5
    c: Parallel(g3,g1)
FEATURE [Part::Extrusion] Extrude006  label="Extrude buco neopixel"
  Base = -> Sketch010
  Dir = (0,-1,2e-16)
  DirMode = 2
  FaceMakerClass = Part::FaceMakerBullseye
  FaceMakerMode = 3
  LengthFwd = 17.2
  LengthRev = 0
  Solid = true
  Symmetric = true
FEATURE [Sketcher::SketchObject] Sketch011  label="fermo grilletto"
  ArcFitTolerance = 1e-06
  AttachmentSupport = -> [XZ_Plane]
  ExternalGeometry = -> [Sketch]
  FullyConstrained = true
  MakeInternals = false
  MapMode = 5
  Placement = pos=(0,0,0) rot=(1,0,0;1.5708rad)
  sketch-geometry (18):
    g0: LineSegment [constr] StartX=-145.51 StartY=22 StartZ=0 EndX=-157.347 EndY=-14.4293 EndZ=0
    g1: LineSegment [constr] StartX=-157.347 StartY=-14.4293 StartZ=0 EndX=-157.841 EndY=-15.951 EndZ=0
    g2: LineSegment StartX=-161.151 StartY=-13.1932 StartZ=0 EndX=-155.825 EndY=-14.9237 EndZ=0
    g3: LineSegment StartX=-163.167 StartY=-14.2205 StartZ=0 EndX=-164.403 EndY=-18.0247 EndZ=0
    g4: LineSegment StartX=-163.376 StartY=-20.0408 StartZ=0 EndX=-158.05 EndY=-21.7713 EndZ=0
    g5: LineSegment StartX=-158.05 StartY=-21.7713 StartZ=0 EndX=-155.825 EndY=-14.9237 EndZ=0
    g6: LineSegment StartX=-161.645 StartY=-14.7149 StartZ=0 EndX=-157.841 EndY=-15.951 EndZ=0
    g7: LineSegment StartX=-157.841 StartY=-15.951 StartZ=0 EndX=-159.077 EndY=-19.7552 EndZ=0
    g8: LineSegment StartX=-159.077 StartY=-19.7552 StartZ=0 EndX=-162.881 EndY=-18.5191 EndZ=0
    g9: LineSegment StartX=-162.881 StartY=-18.5191 StartZ=0 EndX=-161.645 EndY=-14.7149 EndZ=0
    g10: LineSegment [constr] StartX=-161.645 StartY=-14.7149 StartZ=0 EndX=-161.151 EndY=-13.1932 EndZ=0
    g11: LineSegment [constr] StartX=-159.077 StartY=-19.7552 StartZ=0 EndX=-157.555 EndY=-20.2496 EndZ=0
    g12: LineSegment [constr] StartX=-159.077 StartY=-19.7552 StartZ=0 EndX=-159.572 EndY=-21.2769 EndZ=0
    g13: LineSegment [constr] StartX=-161.645 StartY=-14.7149 StartZ=0 EndX=-163.167 EndY=-14.2205 EndZ=0
    g14: ArcOfCircle CenterX=-161.645 CenterY=-14.7149 CenterZ=0 NormalX=0 NormalY=0 NormalZ=1 AngleXU=0 Radius=1.6 StartAngle=1.25664 EndAngle=2.82743
    g15: GeomPoint [constr] X=-162.673 Y=-12.6988 Z=0
    g16: ArcOfCircle CenterX=-162.881 CenterY=-18.5191 CenterZ=0 NormalX=0 NormalY=0 NormalZ=1 AngleXU=0 Radius=1.6 StartAngle=2.82743 EndAngle=4.39823
    g17: GeomPoint [constr] X=-164.897 Y=-19.5464 Z=0
  constraints (48):
    c: Parallel(g0,g-3)
    c: Distance(g0) = 38.304
    c: Coincident(g0,g-3)
    c: Parallel(g1,g-3)
    c: Distance(g1) = 1.6
    c: Coincident(g1,g0)
    c: Coincident(g5,g4)
    c: Coincident(g5,g2)
    c: Coincident(g7,g6)
    c: Coincident(g8,g7)
    c: Coincident(g9,g8)
    c: Coincident(g9,g6)
    c: Parallel(g7,g-3)
    c: Parallel(g9,g7)
    c: Perpendicular(g6,g7)
    c: Parallel(g6,g8)
    c: Distance(g6) = 4
    c: Distance(g9) = 4
    c: Parallel(g5,g7)
    c: Parallel(g9,g3)
    c: Parallel(g2,g6)
    c: Parallel(g4,g8)
    c: Parallel(g13,g6)
    c: Parallel(g10,g9)
    c: Parallel(g11,g8)
    c: Parallel(g12,g7)
    c: Distance(g10) = 1.6
    c: Distance(g13) = 1.6
    c: Distance(g12) = 1.6
    c: Distance(g11) = 1.6
    c: Coincident(g10,g6)
    c: Coincident(g13,g6)
    c: Coincident(g12,g7)
    c: Coincident(g11,g7)
    c: Distance(g10,g15) = 1.6
    c: Distance(g15,g13) = 1.6
    c: Distance(g4,g12) = 1.6
    c: Distance(g4,g11) = 1.6
    c: PointOnObject(g15,g2)
    c: Tangent(g3,g14) = -1.5708
    c: Tangent(g2,g14) = 1.5708
    c: PointOnObject(g17,g4)
    c: PointOnObject(g17,g3)
    c: Tangent(g4,g16) = -1.5708
    c: Tangent(g3,g16) = -1.5708
    c: Equal(g16,g14)
    c: Coincident(g16,g8)
    c: Coincident(g6,g1)
FEATURE [Part::Extrusion] Extrude007  label="Extrude fermo grilletto"
  Base = -> Sketch011
  Dir = (0,-1,2e-16)
  DirMode = 2
  FaceMakerClass = Part::FaceMakerBullseye
  FaceMakerMode = 3
  LengthFwd = 25.2
  LengthRev = 0
  Solid = true
  Symmetric = true
FEATURE [Sketcher::SketchObject] Sketch012  label="buco oled"
  ArcFitTolerance = 1e-06
  AttachmentSupport = -> [XZ_Plane]
  ExternalGeometry = -> [Sketch]
  FullyConstrained = true
  MakeInternals = false
  MapMode = 5
  Placement = pos=(0,0,0) rot=(1,0,0;1.5708rad)
  sketch-geometry (4):
    g0: LineSegment StartX=-185.747 StartY=58.0965 StartZ=0 EndX=-180.232 EndY=56.0891 EndZ=0
    g1: LineSegment StartX=-185.747 StartY=58.0965 StartZ=0 EndX=-185.747 EndY=67.3588 EndZ=0
    g2: LineSegment StartX=-185.747 StartY=67.3588 StartZ=0 EndX=-180.232 EndY=67.3588 EndZ=0
    g3: LineSegment StartX=-180.232 StartY=67.3588 StartZ=0 EndX=-180.232 EndY=56.0891 EndZ=0
  constraints (10):
    c: Coincident(g1,g0)
    c: Coincident(g2,g1)
    c: Coincident(g3,g2)
    c: Coincident(g3,g0)
    c: Parallel(g1,g-5)
    c: Perpendicular(g-3,g0)
    c: Parallel(g2,g-6)
    c: Parallel(g3,g-4)
    c: Coincident(g0,g-5)
    c: Coincident(g2,g-6)
FEATURE [Part::Extrusion] Extrude008  label="Extrude buco oled"
  Base = -> Sketch012
  Dir = (0,-1,2e-16)
  DirMode = 2
  FaceMakerClass = Part::FaceMakerBullseye
  FaceMakerMode = 3
  LengthFwd = 12.8
  LengthRev = 0
  Solid = true
  Symmetric = true
FEATURE [Sketcher::SketchObject] Sketch013  label="buco pompa"
  ArcFitTolerance = 1e-06
  AttachmentSupport = -> [XZ_Plane]
  ExternalGeometry = -> [Sketch]
  FullyConstrained = true
  MakeInternals = false
  MapMode = 5
  Placement = pos=(0,0,0) rot=(1,0,0;1.5708rad)
  sketch-geometry (8):
    g0: LineSegment StartX=-82.8 StartY=-10.4 StartZ=0 EndX=-82.8 EndY=-9.6 EndZ=0
    g1: LineSegment StartX=-82.8 StartY=-9.6 StartZ=0 EndX=-67.9 EndY=-9.6 EndZ=0
    g2: LineSegment StartX=-67.9 StartY=-9.6 StartZ=0 EndX=-67.9 EndY=6 EndZ=0
    g3: LineSegment StartX=-67.9 StartY=6 StartZ=0 EndX=-65.9 EndY=6 EndZ=0
    g4: LineSegment StartX=-65.9 StartY=6 StartZ=0 EndX=-65.9 EndY=-1.7 EndZ=0
    g5: LineSegment StartX=-65.9 StartY=-1.7 StartZ=0 EndX=-57.2 EndY=-1.7 EndZ=0
    g6: LineSegment StartX=-57.2 StartY=-1.7 StartZ=0 EndX=-57.2 EndY=-10.4 EndZ=0
    g7: LineSegment StartX=-57.2 StartY=-10.4 StartZ=0 EndX=-82.8 EndY=-10.4 EndZ=0
  constraints (22):
    c: Vertical(g0)
    c: Coincident(g1,g0)
    c: Horizontal(g1)
    c: Coincident(g2,g1)
    c: Vertical(g2)
    c: Coincident(g3,g2)
    c: Horizontal(g3)
    c: Coincident(g4,g3)
    c: Vertical(g4)
    c: Coincident(g5,g4)
    c: Horizontal(g5)
    c: Coincident(g6,g5)
    c: Vertical(g6)
    c: Coincident(g7,g6)
    c: Coincident(g7,g0)
    c: DistanceY(g0,g0) = 0.8
    c: DistanceY(g6,g6) = 8.7
    c: DistanceX(g1,g1) = 14.9
    c: DistanceX(g3,g3) = 2
    c: Coincident(g0,g-4)
    c: DistanceY(g2,g-6) = 0
    c: Coincident(g6,g-5)
FEATURE [Part::Extrusion] Extrude009  label="Extrude buco pompa"
  Base = -> Sketch013
  Dir = (0,-1,2e-16)
  DirMode = 2
  FaceMakerClass = Part::FaceMakerBullseye
  FaceMakerMode = 3
  LengthFwd = 13.2
  LengthRev = 0
  Solid = true
  Symmetric = true
FEATURE [Sketcher::SketchObject] Sketch014  label="buco frontale"
  ArcFitTolerance = 1e-06
  AttachmentSupport = -> [XZ_Plane]
  ExternalGeometry = -> [Sketch]
  FullyConstrained = true
  MakeInternals = false
  MapMode = 5
  Placement = pos=(0,0,0) rot=(1,0,0;1.5708rad)
  sketch-geometry (10):
    g0: LineSegment StartX=0 StartY=0 StartZ=0 EndX=0 EndY=24.671 EndZ=0
    g1: LineSegment StartX=0 StartY=24.671 StartZ=0 EndX=-4 EndY=24.671 EndZ=0
    g2: LineSegment StartX=-4 StartY=24.671 StartZ=0 EndX=-4 EndY=16 EndZ=0
    g3: LineSegment StartX=-4 StartY=16 StartZ=0 EndX=-2.4 EndY=16 EndZ=0
    g4: LineSegment StartX=-2.4 StartY=16 StartZ=0 EndX=-2.4 EndY=10 EndZ=0
    g5: LineSegment StartX=-2.4 StartY=10 StartZ=0 EndX=-12 EndY=10 EndZ=0
    g6: LineSegment StartX=-12 StartY=10 StartZ=0 EndX=-12 EndY=6 EndZ=0
    g7: LineSegment StartX=-12 StartY=6 StartZ=0 EndX=-2.4 EndY=6 EndZ=0
    g8: LineSegment StartX=-2.4 StartY=6 StartZ=0 EndX=-2.4 EndY=0 EndZ=0
    g9: LineSegment StartX=-2.4 StartY=0 StartZ=0 EndX=0 EndY=0 EndZ=0
  constraints (29):
    c: Vertical(g0)
    c: Coincident(g1,g0)
    c: Horizontal(g1)
    c: Coincident(g2,g1)
    c: Vertical(g2)
    c: Coincident(g3,g2)
    c: Horizontal(g3)
    c: Coincident(g4,g3)
    c: Vertical(g4)
    c: Coincident(g5,g4)
    c: Horizontal(g5)
    c: Coincident(g6,g5)
    c: Vertical(g6)
    c: Coincident(g7,g6)
    c: Coincident(g8,g7)
    c: Vertical(g8)
    c: Coincident(g9,g8)
    c: Coincident(g9,g0)
    c: Horizontal(g9)
    c: DistanceY(g0,g0) = 24.671
    c: Horizontal(g7)
    c: DistanceY(g6,g6) = 4
    c: DistanceY(g4,g4) = 6
    c: DistanceX(g9,g9) = 2.4
    c: Coincident(g0,g-1)
    c: DistanceY(g-3,g7) = 0
    c: DistanceX(g8,g4) = 0
    c: DistanceX(g-3,g1) = 0
    c: DistanceX(g6,g-3) = 8
FEATURE [Part::Extrusion] Extrude010  label="Extrude buco frontale"
  Base = -> Sketch014
  Dir = (0,-1,2e-16)
  DirMode = 2
  FaceMakerClass = Part::FaceMakerBullseye
  FaceMakerMode = 3
  LengthFwd = 11.2
  LengthRev = 0
  Solid = true
  Symmetric = true
FEATURE [Sketcher::SketchObject] Sketch015  label="guida rail"
  ArcFitTolerance = 1e-06
  AttachmentSupport = -> [XZ_Plane]
  ExternalGeometry = -> [Sketch]
  FullyConstrained = true
  MakeInternals = false
  MapMode = 5
  Placement = pos=(0,0,0) rot=(1,0,0;1.5708rad)
  sketch-geometry (4):
    g0: LineSegment StartX=-100.8 StartY=43.2 StartZ=0 EndX=-44.6 EndY=43.2 EndZ=0
    g1: LineSegment StartX=-44.6 StartY=43.2 StartZ=0 EndX=-44.6 EndY=41.2 EndZ=0
    g2: LineSegment StartX=-44.6 StartY=41.2 StartZ=0 EndX=-100.8 EndY=41.2 EndZ=0
    g3: LineSegment StartX=-100.8 StartY=41.2 StartZ=0 EndX=-100.8 EndY=43.2 EndZ=0
  constraints (9):
    c: Horizontal(g0)
    c: Coincident(g1,g0)
    c: Coincident(g2,g1)
    c: Coincident(g3,g2)
    c: Coincident(g3,g0)
    c: Vertical(g3)
    c: Coincident(g2,g-3)
    c: Coincident(g1,g-3)
    c: Coincident(g0,g-4)
FEATURE [Part::Extrusion] Extrude011  label="Extrude guida rail"
  Base = -> Sketch015
  Dir = (0,-1,2e-16)
  DirMode = 2
  FaceMakerClass = Part::FaceMakerBullseye
  FaceMakerMode = 3
  LengthFwd = 9
  LengthRev = 0
  Solid = true
  Symmetric = true
FEATURE [Sketcher::SketchObject] Sketch016  label="guide per coperture laterali"
  ArcFitTolerance = 1e-06
  AttachmentSupport = -> [XZ_Plane]
  ExternalGeometry = -> [Sketch]
  FullyConstrained = true
  MakeInternals = false
  MapMode = 5
  Placement = pos=(0,0,0) rot=(1,0,0;1.5708rad)
  sketch-geometry (14):
    g0: Circle CenterX=-5.6 CenterY=7.6 CenterZ=0 NormalX=0 NormalY=0 NormalZ=1 AngleXU=0 Radius=1.6
    g1: Circle CenterX=-5.6 CenterY=7.6 CenterZ=0 NormalX=0 NormalY=0 NormalZ=1 AngleXU=0 Radius=4
    g2: Circle CenterX=-5.6 CenterY=34.8 CenterZ=0 NormalX=0 NormalY=0 NormalZ=1 AngleXU=0 Radius=1.6
    g3: Circle CenterX=-5.6 CenterY=34.8 CenterZ=0 NormalX=0 NormalY=0 NormalZ=1 AngleXU=0 Radius=4
    g4: Circle CenterX=-184.08 CenterY=34.8 CenterZ=0 NormalX=0 NormalY=0 NormalZ=1 AngleXU=0 Radius=1.6
    g5: Circle CenterX=-184.08 CenterY=34.8 CenterZ=0 NormalX=0 NormalY=0 NormalZ=1 AngleXU=0 Radius=4
    g6: Circle CenterX=-179.305 CenterY=-76.8316 CenterZ=0 NormalX=0 NormalY=0 NormalZ=1 AngleXU=0 Radius=1.6
    g7: Circle CenterX=-179.305 CenterY=-76.8316 CenterZ=0 NormalX=0 NormalY=0 NormalZ=1 AngleXU=0 Radius=4
    g8: Circle CenterX=-213.443 CenterY=-76.8316 CenterZ=0 NormalX=0 NormalY=0 NormalZ=1 AngleXU=0 Radius=1.6
    g9: Circle CenterX=-213.443 CenterY=-76.8316 CenterZ=0 NormalX=0 NormalY=0 NormalZ=1 AngleXU=0 Radius=4
    g10: Circle CenterX=-78.51 CenterY=7.6 CenterZ=0 NormalX=0 NormalY=0 NormalZ=1 AngleXU=0 Radius=1.6
    g11: Circle CenterX=-78.51 CenterY=7.6 CenterZ=0 NormalX=0 NormalY=0 NormalZ=1 AngleXU=0 Radius=4
    g12: Circle CenterX=-78.51 CenterY=34.8 CenterZ=0 NormalX=0 NormalY=0 NormalZ=1 AngleXU=0 Radius=1.6
    g13: Circle CenterX=-78.51 CenterY=34.8 CenterZ=0 NormalX=0 NormalY=0 NormalZ=1 AngleXU=0 Radius=4
  constraints (35):
    c: Diameter(g0) = 3.2
    c: Diameter(g1) = 8
    c: Coincident(g0,g1)
    c: Diameter(g2) = 3.2
    c: Diameter(g3) = 8
    c: Coincident(g3,g2)
    c: Tangent(g2,g-7)
    c: Diameter(g4) = 3.2
    c: Diameter(g5) = 8
    c: Coincident(g5,g4)
    c: Tangent(g4,g-7)
    c: Tangent(g4,g-8)
    c: Diameter(g6) = 3.2
    c: Diameter(g7) = 8
    c: Coincident(g7,g6)
    c: Tangent(g6,g-9)
    c: Tangent(g6,g-10)
    c: Diameter(g8) = 3.2
    c: Diameter(g9) = 8
    c: Coincident(g9,g8)
    c: Tangent(g8,g-10)
    c: Tangent(g8,g-11)
    c: Diameter(g10) = 3.2
    c: Diameter(g11) = 8
    c: Diameter(g12) = 3.2
    c: Diameter(g13) = 8
    c: Coincident(g12,g13)
    c: Coincident(g10,g11)
    c: Tangent(g12,g-7)
    c: DistanceX(g12,g10) = 0
    c: Tangent(g2,g-6)
    c: Tangent(g0,g-6)
    c: Tangent(g0,g-3)
    c: Tangent(g10,g-3)
    c: Tangent(g10,g-4)
FEATURE [Part::Extrusion] Extrude012  label="extrude guide per coperture laterali"
  Base = -> Sketch016
  Dir = (0,-1,2e-16)
  DirMode = 2
  FaceMakerClass = Part::FaceMakerBullseye
  FaceMakerMode = 3
  LengthFwd = 25.2
  LengthRev = 0
  Solid = true
  Symmetric = true
FEATURE [Sketcher::SketchObject] Sketch017  label="supporto CAM"
  ArcFitTolerance = 1e-06
  AttachmentSupport = -> [XZ_Plane]
  ExternalGeometry = -> [Sketch]
  FullyConstrained = true
  MakeInternals = false
  MapMode = 5
  Placement = pos=(0,0,0) rot=(1,0,0;1.5708rad)
  sketch-geometry (6):
    g0: LineSegment StartX=-2.4 StartY=48 StartZ=0 EndX=-2.4 EndY=41.2 EndZ=0
    g1: LineSegment StartX=-2.4 StartY=48 StartZ=0 EndX=-34 EndY=48 EndZ=0
    g2: LineSegment StartX=-34 StartY=48 StartZ=0 EndX=-34 EndY=46.72 EndZ=0
    g3: LineSegment StartX=-34 StartY=46.72 StartZ=0 EndX=-36 EndY=46.72 EndZ=0
    g4: LineSegment StartX=-36 StartY=46.72 StartZ=0 EndX=-36 EndY=41.2 EndZ=0
    g5: LineSegment StartX=-36 StartY=41.2 StartZ=0 EndX=-2.4 EndY=41.2 EndZ=0
  constraints (15):
    c: Coincident(g1,g0)
    c: Horizontal(g1)
    c: Coincident(g2,g1)
    c: Vertical(g2)
    c: Coincident(g3,g2)
    c: Horizontal(g3)
    c: Coincident(g4,g3)
    c: Coincident(g5,g4)
    c: DistanceX(g1,g0) = 31.6
    c: Coincident(g5,g0)
    c: Vertical(g4)
    c: DistanceY(g2,g1) = 1.28
    c: Coincident(g0,g-3)
    c: Coincident(g0,g-3)
    c: Coincident(g4,g-4)
FEATURE [Part::Extrusion] Extrude013  label="Extrude supporto CAM"
  Base = -> Sketch017
  Dir = (0,-1,2e-16)
  DirMode = 2
  FaceMakerClass = Part::FaceMakerBullseye
  FaceMakerMode = 3
  LengthFwd = 17.8
  LengthRev = 0
  Solid = true
  Symmetric = true
FEATURE [Sketcher::SketchObject] Sketch018  label="Scavo CAM"
  ArcFitTolerance = 1e-06
  AttachmentSupport = -> [YZ_Plane]
  ExternalGeometry = -> [Sketch]
  FullyConstrained = true
  MakeInternals = false
  MapMode = 5
  Placement = pos=(0,0,0) rot=(0.57735,0.57735,0.57735;2.0944rad)
  sketch-geometry (4):
    g0: LineSegment StartX=-7.73 StartY=48 StartZ=0 EndX=7.73 EndY=48 EndZ=0
    g1: LineSegment [constr] StartX=1.07e-14 StartY=48 StartZ=0 EndX=0 EndY=43.5155 EndZ=0
    g2: ArcOfCircle CenterX=9e-15 CenterY=52.42 CenterZ=0 NormalX=0 NormalY=0 NormalZ=1 AngleXU=0 Radius=8.90445 StartAngle=3.66102 EndAngle=5.76376
    g3: Circle [constr] CenterX=9e-15 CenterY=52.42 CenterZ=0 NormalX=0 NormalY=0 NormalZ=1 AngleXU=0 Radius=8.9
  constraints (13):
    c: Horizontal(g0)
    c: DistanceY(g-3,g0) = 0
    c: DistanceX(g0,g0) = 15.46
    c: DistanceX(g0,g-3) = 7.73
    c: DistanceX(g-3) = 0
    c: Coincident(g1,g-3)
    c: PointOnObject(g1,g-2)
    c: Coincident(g2,g0)
    c: Coincident(g2,g0)
    c: PointOnObject(g1,g2)
    c: Diameter(g3) = 17.8
    c: DistanceY(g1,g3) = 4.42
    c: Coincident(g2,g3)
FEATURE [Part::Extrusion] Extrude014  label="Extrude Scavo CAM"
  Base = -> Sketch018
  Dir = (1,0,0)
  DirMode = 2
  FaceMakerClass = Part::FaceMakerBullseye
  FaceMakerMode = 3
  LengthFwd = -34
  LengthRev = 0
  Solid = true
  Symmetric = false
FEATURE [Sketcher::SketchObject] Sketch019  label="scavo rumble"
  ArcFitTolerance = 1e-06
  AttachmentSupport = -> [XZ_Plane]
  ExternalGeometry = -> [Sketch]
  FullyConstrained = true
  MakeInternals = false
  MapMode = 5
  Placement = pos=(0,0,0) rot=(1,0,0;1.5708rad)
  sketch-geometry (6):
    g0: LineSegment StartX=-163.771 StartY=-21.9058 StartZ=0 EndX=-158.636 EndY=-23.5745 EndZ=0
    g1: LineSegment StartX=-158.636 StartY=-23.5745 StartZ=0 EndX=-165.743 EndY=-45.4488 EndZ=0
    g2: LineSegment StartX=-165.743 StartY=-45.4488 StartZ=0 EndX=-170.879 EndY=-43.7801 EndZ=0
    g3: LineSegment StartX=-170.879 StartY=-43.7801 StartZ=0 EndX=-163.771 EndY=-21.9058 EndZ=0
    g4: LineSegment [constr] StartX=-145.51 StartY=22 StartZ=0 EndX=-160.157 EndY=-23.0801 EndZ=0
    g5: LineSegment [constr] StartX=-158.636 StartY=-23.5745 StartZ=0 EndX=-160.157 EndY=-23.0801 EndZ=0
  constraints (17):
    c: Coincident(g1,g0)
    c: Coincident(g2,g1)
    c: Coincident(g3,g2)
    c: Coincident(g3,g0)
    c: Parallel(g3,g-3)
    c: Parallel(g3,g1)
    c: Perpendicular(g3,g0)
    c: Perpendicular(g2,g3)
    c: Distance(g2,g0) = 23
    c: Parallel(g4,g-3)
    c: Distance(g4) = 47.4
    c: Coincident(g4,g-3)
    c: Parallel(g5,g0)
    c: Distance(g5) = 1.6
    c: Coincident(g5,g0)
    c: Distance(g5,g0) = 3.8
    c: Coincident(g5,g4)
FEATURE [Part::Extrusion] Extrude015  label="scavo rumble001"
  Base = -> Sketch019
  Dir = (0,-1,2e-16)
  DirMode = 2
  FaceMakerClass = Part::FaceMakerBullseye
  FaceMakerMode = 3
  LengthFwd = 21
  LengthRev = 0
  Solid = true
  Symmetric = true
FEATURE [Sketcher::SketchObject] Sketch020  label="fermo rumble"
  ArcFitTolerance = 1e-06
  AttachmentSupport = -> [XZ_Plane]
  ExternalGeometry = -> [Sketch019,Sketch]
  FullyConstrained = true
  MakeInternals = false
  MapMode = 5
  Placement = pos=(0,0,0) rot=(1,0,0;1.5708rad)
  sketch-geometry (16):
    g0: LineSegment [constr] StartX=-165.905 StartY=-40.7697 StartZ=0 EndX=-167.265 EndY=-44.9544 EndZ=0
    g1: LineSegment [constr] StartX=-167.265 StartY=-44.9544 StartZ=0 EndX=-165.743 EndY=-45.4488 EndZ=0
    g2: LineSegment StartX=-167.318 StartY=-37.9976 StartZ=0 EndX=-165.225 EndY=-38.6774 EndZ=0
    g3: LineSegment StartX=-165.225 StartY=-38.6774 StartZ=0 EndX=-165.905 EndY=-40.7697 EndZ=0
    g4: LineSegment StartX=-165.905 StartY=-40.7697 StartZ=0 EndX=-167.997 EndY=-40.0899 EndZ=0
    g5: LineSegment StartX=-167.997 StartY=-40.0899 StartZ=0 EndX=-167.318 EndY=-37.9976 EndZ=0
    g6: LineSegment StartX=-166.823 StartY=-36.4759 StartZ=0 EndX=-163.399 EndY=-37.5883 EndZ=0
    g7: LineSegment StartX=-163.399 StartY=-37.5883 StartZ=0 EndX=-165.006 EndY=-42.5338 EndZ=0
    g8: LineSegment StartX=-165.006 StartY=-42.5338 StartZ=0 EndX=-168.43 EndY=-41.4214 EndZ=0
    g9: LineSegment StartX=-169.457 StartY=-39.4053 StartZ=0 EndX=-168.839 EndY=-37.5031 EndZ=0
    g10: LineSegment [constr] StartX=-168.839 StartY=-37.5031 StartZ=0 EndX=-168.345 EndY=-35.9815 EndZ=0
    g11: LineSegment [constr] StartX=-168.345 StartY=-35.9815 StartZ=0 EndX=-166.823 EndY=-36.4759 EndZ=0
    g12: ArcOfCircle CenterX=-167.936 CenterY=-39.8997 CenterZ=0 NormalX=0 NormalY=0 NormalZ=1 AngleXU=0 Radius=1.6 StartAngle=2.82743 EndAngle=4.39823
    g13: GeomPoint [constr] X=-169.952 Y=-40.9269 Z=0
    g14: ArcOfCircle CenterX=-167.318 CenterY=-37.9976 CenterZ=0 NormalX=0 NormalY=0 NormalZ=1 AngleXU=0 Radius=1.6 StartAngle=1.25664 EndAngle=2.82743
    g15: GeomPoint [constr] X=-168.345 Y=-35.9815 Z=0
  constraints (42):
    c: Parallel(g0,g-4)
    c: Distance(g0) = 4.4
    c: Coincident(g1,g0)
    c: Perpendicular(g0,g1)
    c: Distance(g1) = 1.6
    c: Coincident(g1,g-5)
    c: Coincident(g3,g2)
    c: Coincident(g4,g3)
    c: Coincident(g5,g4)
    c: Coincident(g5,g2)
    c: Parallel(g3,g-4)
    c: Parallel(g3,g5)
    c: Perpendicular(g2,g3)
    c: Parallel(g4,g2)
    c: Distance(g2) = 2.2
    c: Distance(g3) = 2.2
    c: Coincident(g7,g6)
    c: Coincident(g8,g7)
    c: Parallel(g7,g-4)
    c: Parallel(g7,g9)
    c: Perpendicular(g6,g7)
    c: Parallel(g6,g8)
    c: Distance(g6,g15) = 5.2
    c: Distance(g7) = 5.2
    c: Coincident(g11,g10)
    c: Parallel(g10,g9)
    c: Parallel(g11,g6)
    c: Distance(g10) = 1.6
    c: Distance(g11) = 1.6
    c: Coincident(g10,g15)
    c: Distance(g11,g2) = 1.6
    c: Distance(g2,g10) = 1.6
    c: PointOnObject(g13,g8)
    c: PointOnObject(g13,g9)
    c: Tangent(g8,g12) = 1.5708
    c: Tangent(g9,g12) = 1.5708
    c: PointOnObject(g15,g9)
    c: Tangent(g6,g14) = 1.5708
    c: Tangent(g9,g14) = 1.5708
    c: Equal(g12,g14)
    c: Coincident(g6,g11)
    c: Coincident(g3,g0)
FEATURE [Part::Extrusion] Extrude016  label="Extrude fermo rumble"
  Base = -> Sketch020
  Dir = (0,-1,2e-16)
  DirMode = 2
  FaceMakerClass = Part::FaceMakerBullseye
  FaceMakerMode = 3
  LengthFwd = 25.2
  LengthRev = 0
  Solid = true
  Symmetric = true
FEATURE [Sketcher::SketchObject] Sketch021  label="perno fermo rumble001"
  ArcFitTolerance = 1e-06
  AttachmentSupport = -> [XZ_Plane001]
  FullyConstrained = true
  MakeInternals = false
  MapMode = 5
  Placement = pos=(0,0,0) rot=(1,0,0;1.5708rad)
  sketch-geometry (16):
    g0: LineSegment StartX=0 StartY=0.45 StartZ=0 EndX=0 EndY=1.55 EndZ=0
    g1: LineSegment StartX=0.45 StartY=2 StartZ=0 EndX=1.55 EndY=2 EndZ=0
    g2: LineSegment StartX=2 StartY=1.55 StartZ=0 EndX=2 EndY=0.45 EndZ=0
    g3: LineSegment StartX=1.55 StartY=0 StartZ=0 EndX=0.45 EndY=0 EndZ=0
    g4: ArcOfCircle [constr] CenterX=0.45 CenterY=1.55 CenterZ=0 NormalX=0 NormalY=0 NormalZ=1 AngleXU=0 Radius=0.45 StartAngle=1.5708 EndAngle=3.14159
    g5: GeomPoint [constr] X=0 Y=2 Z=0
    g6: LineSegment StartX=0.45 StartY=2 StartZ=0 EndX=0 EndY=1.55 EndZ=0
    g7: ArcOfCircle [constr] CenterX=1.55 CenterY=1.55 CenterZ=0 NormalX=0 NormalY=0 NormalZ=1 AngleXU=0 Radius=0.45 StartAngle=0 EndAngle=1.5708
    g8: GeomPoint [constr] X=2 Y=2 Z=0
    g9: LineSegment StartX=2 StartY=1.55 StartZ=0 EndX=1.55 EndY=2 EndZ=0
    g10: ArcOfCircle [constr] CenterX=1.55 CenterY=0.45 CenterZ=0 NormalX=0 NormalY=0 NormalZ=1 AngleXU=0 Radius=0.45 StartAngle=4.71239 EndAngle=6.28319
    g11: GeomPoint [constr] X=2 Y=0 Z=0
    g12: LineSegment StartX=1.55 StartY=0 StartZ=0 EndX=2 EndY=0.45 EndZ=0
    g13: ArcOfCircle [constr] CenterX=0.45 CenterY=0.45 CenterZ=0 NormalX=0 NormalY=0 NormalZ=1 AngleXU=0 Radius=0.45 StartAngle=3.14159 EndAngle=4.71239
    g14: GeomPoint [constr] X=0 Y=0 Z=0
    g15: LineSegment StartX=0 StartY=0.45 StartZ=0 EndX=0.45 EndY=0 EndZ=0
  constraints (35):
    c: Coincident(g14,g-1)
    c: PointOnObject(g5,g-2)
    c: Horizontal(g1)
    c: Vertical(g2)
    c: Horizontal(g3)
    c: DistanceX(g5,g8) = 2
    c: DistanceY(g11,g8) = 2
    c: PointOnObject(g5,g0)
    c: PointOnObject(g5,g1)
    c: Tangent(g0,g4) = 1.5708
    c: Tangent(g1,g4) = 1.5708
    c: Coincident(g6,g0)
    c: Coincident(g6,g1)
    c: PointOnObject(g8,g2)
    c: PointOnObject(g8,g1)
    c: Tangent(g2,g7) = 1.5708
    c: Tangent(g1,g7) = 1.5708
    c: Coincident(g9,g2)
    c: Coincident(g9,g1)
    c: PointOnObject(g11,g2)
    c: PointOnObject(g11,g3)
    c: Tangent(g2,g10) = 1.5708
    c: Tangent(g3,g10) = 1.5708
    c: Coincident(g12,g2)
    c: Coincident(g12,g3)
    c: PointOnObject(g14,g0)
    c: PointOnObject(g14,g3)
    c: Tangent(g0,g13) = 1.5708
    c: Tangent(g3,g13) = 1.5708
    c: Coincident(g15,g0)
    c: Coincident(g15,g3)
    c: Equal(g6,g9)
    c: Equal(g9,g12)
    c: Equal(g12,g15)
    c: DistanceX(g14,g3) = 0.45
FEATURE [Sketcher::SketchObject] Sketch022  label="fori per M3x5(OD)x6(L)"
  ArcFitTolerance = 1e-06
  AttachmentSupport = -> [XZ_Plane]
  ExternalGeometry = -> [Sketch016]
  FullyConstrained = true
  MakeInternals = false
  MapMode = 5
  Placement = pos=(0,0,0) rot=(1,0,0;1.5708rad)
  sketch-geometry (7):
    g0: Circle CenterX=-5.6 CenterY=34.8 CenterZ=0 NormalX=0 NormalY=0 NormalZ=1 AngleXU=0 Radius=2.5
    g1: Circle CenterX=-5.6 CenterY=7.6 CenterZ=0 NormalX=0 NormalY=0 NormalZ=1 AngleXU=0 Radius=2.5
    g2: Circle CenterX=-78.51 CenterY=34.8 CenterZ=0 NormalX=0 NormalY=0 NormalZ=1 AngleXU=0 Radius=2.5
    g3: Circle CenterX=-78.51 CenterY=7.6 CenterZ=0 NormalX=0 NormalY=0 NormalZ=1 AngleXU=0 Radius=2.5
    g4: Circle CenterX=-184.08 CenterY=34.8 CenterZ=0 NormalX=0 NormalY=0 NormalZ=1 AngleXU=0 Radius=2.5
    g5: Circle CenterX=-179.305 CenterY=-76.8316 CenterZ=0 NormalX=0 NormalY=0 NormalZ=1 AngleXU=0 Radius=2.5
    g6: Circle CenterX=-213.443 CenterY=-76.8316 CenterZ=0 NormalX=0 NormalY=0 NormalZ=1 AngleXU=0 Radius=2.5
  constraints (14):
    c: Diameter(g0) = 5
    c: Diameter(g1) = 5
    c: Diameter(g2) = 5
    c: Diameter(g3) = 5
    c: Diameter(g4) = 5
    c: Diameter(g5) = 5
    c: Diameter(g6) = 5
    c: Coincident(g0,g-8)
    c: Coincident(g1,g-9)
    c: Coincident(g2,g-6)
    c: Coincident(g3,g-7)
    c: Coincident(g4,g-5)
    c: Coincident(g5,g-4)
    c: Coincident(g6,g-3)
FEATURE [Part::Extrusion] Extrude018  label="Extrude fori M3x5x6 - dx"
  Base = -> Sketch022
  Dir = (0,-1,2e-16)
  DirMode = 2
  FaceMakerClass = Part::FaceMakerBullseye
  FaceMakerMode = 3
  LengthFwd = 6.2
  LengthRev = 0
  Placement = pos=(0,-9.5,0) rot=(0,0,1;0rad)
  Solid = true
  Symmetric = true
FEATURE [Part::Extrusion] Extrude019  label="Extrude fori M3x5x6 - sx"
  Base = -> Sketch022
  Dir = (0,-1,2e-16)
  DirMode = 2
  FaceMakerClass = Part::FaceMakerBullseye
  FaceMakerMode = 3
  LengthFwd = 6.2
  LengthRev = 0
  Placement = pos=(0,9.5,0) rot=(0,0,1;0rad)
  Solid = true
  Symmetric = true
FEATURE [Sketcher::SketchObject] Sketch023  label="foro anteriore M3x5x6"
  ArcFitTolerance = 1e-06
  AttachmentSupport = -> [YZ_Plane]
  FullyConstrained = true
  MakeInternals = false
  MapMode = 5
  Placement = pos=(0,0,0) rot=(0.57735,0.57735,0.57735;2.0944rad)
  sketch-geometry (2):
    g0: LineSegment [constr] StartX=0 StartY=0 StartZ=0 EndX=0 EndY=38.6 EndZ=0
    g1: Circle CenterX=0 CenterY=38.6 CenterZ=0 NormalX=0 NormalY=0 NormalZ=1 AngleXU=0 Radius=2.5
  constraints (5):
    c: Coincident(g0,g-1)
    c: PointOnObject(g0,g-2)
    c: DistanceY(g0,g0) = 38.6
    c: Diameter(g1) = 5
    c: Coincident(g1,g0)
FEATURE [Part::Extrusion] Extrude020  label="Extrude foro anteriore M3x5x6"
  Base = -> Sketch023
  Dir = (1,0,0)
  DirMode = 2
  FaceMakerClass = Part::FaceMakerBullseye
  FaceMakerMode = 3
  LengthFwd = -6.2
  LengthRev = 0
  Solid = true
  Symmetric = false
FEATURE [Sketcher::SketchObject] Sketch024  label="fori per viti frontale"
  ArcFitTolerance = 1e-06
  AttachmentSupport = -> [YZ_Plane]
  FullyConstrained = true
  MakeInternals = false
  MapMode = 5
  Placement = pos=(0,0,0) rot=(0.57735,0.57735,0.57735;2.0944rad)
  sketch-geometry (9):
    g0: LineSegment [constr] StartX=-10.3 StartY=30.721 StartZ=0 EndX=10.3 EndY=30.721 EndZ=0
    g1: LineSegment [constr] StartX=10.3 StartY=30.721 StartZ=0 EndX=10.3 EndY=10.121 EndZ=0
    g2: LineSegment [constr] StartX=10.3 StartY=10.121 StartZ=0 EndX=-10.3 EndY=10.121 EndZ=0
    g3: LineSegment [constr] StartX=-10.3 StartY=10.121 StartZ=0 EndX=-10.3 EndY=30.721 EndZ=0
    g4: LineSegment [constr] StartX=0 StartY=0 StartZ=0 EndX=0 EndY=10.121 EndZ=0
    g5: Circle CenterX=-10.3 CenterY=30.721 CenterZ=0 NormalX=0 NormalY=0 NormalZ=1 AngleXU=0 Radius=2
    g6: Circle CenterX=10.3 CenterY=30.721 CenterZ=0 NormalX=0 NormalY=0 NormalZ=1 AngleXU=0 Radius=2
    g7: Circle CenterX=-10.3 CenterY=10.121 CenterZ=0 NormalX=0 NormalY=0 NormalZ=1 AngleXU=0 Radius=2
    g8: Circle CenterX=10.3 CenterY=10.121 CenterZ=0 NormalX=0 NormalY=0 NormalZ=1 AngleXU=0 Radius=2
  constraints (22):
    c: Horizontal(g0)
    c: Coincident(g1,g0)
    c: Vertical(g1)
    c: Coincident(g2,g1)
    c: Horizontal(g2)
    c: Coincident(g3,g2)
    c: Coincident(g3,g0)
    c: Vertical(g3)
    c: DistanceX(g0,g0) = 20.6
    c: DistanceY(g3,g3) = 20.6
    c: Coincident(g4,g-1)
    c: PointOnObject(g4,g-2)
    c: DistanceY(g4,g4) = 10.121
    c: Symmetric(g2,g2,g4)
    c: Diameter(g5) = 4
    c: Diameter(g6) = 4
    c: Diameter(g7) = 4
    c: Diameter(g8) = 4
    c: Coincident(g5,g0)
    c: Coincident(g6,g0)
    c: Coincident(g7,g2)
    c: Coincident(g8,g1)
FEATURE [Part::Extrusion] Extrude021  label="Extrude fori per viti frontale"
  Base = -> Sketch024
  Dir = (1,0,0)
  DirMode = 2
  FaceMakerClass = Part::FaceMakerBullseye
  FaceMakerMode = 3
  LengthFwd = -2.4
  LengthRev = 0
  Solid = true
  Symmetric = false
FEATURE [Sketcher::SketchObject] Sketch025  label="foro per filo CAM"
  ArcFitTolerance = 1e-06
  AttachmentSupport = -> [XZ_Plane]
  ExternalGeometry = -> [Sketch]
  FullyConstrained = true
  MakeInternals = false
  MapMode = 5
  Placement = pos=(0,0,0) rot=(1,0,0;1.5708rad)
  sketch-geometry (4):
    g0: LineSegment StartX=-44.6 StartY=41.2 StartZ=0 EndX=-44.6 EndY=36.4 EndZ=0
    g1: LineSegment StartX=-44.6 StartY=36.4 StartZ=0 EndX=-54.6 EndY=36.4 EndZ=0
    g2: LineSegment StartX=-54.6 StartY=36.4 StartZ=0 EndX=-50.4 EndY=41.2 EndZ=0
    g3: LineSegment StartX=-50.4 StartY=41.2 StartZ=0 EndX=-44.6 EndY=41.2 EndZ=0
  constraints (11):
    c: Vertical(g0)
    c: Coincident(g1,g0)
    c: Horizontal(g1)
    c: Coincident(g2,g1)
    c: Coincident(g3,g2)
    c: Coincident(g3,g0)
    c: Horizontal(g3)
    c: Coincident(g0,g-3)
    c: DistanceY(g0,g-4) = 0
    c: DistanceX(g3,g3) = 5.8
    c: DistanceX(g1,g1) = 10
FEATURE [Part::Extrusion] Extrude022  label="Extrude foro per filo CAM dx"
  Base = -> Sketch025
  Dir = (0,-1,2e-16)
  DirMode = 2
  FaceMakerClass = Part::FaceMakerBullseye
  FaceMakerMode = 3
  LengthFwd = 4.9
  LengthRev = 0
  Placement = pos=(0,6.95,0) rot=(0,0,1;0rad)
  Solid = true
  Symmetric = true
FEATURE [Part::Extrusion] Extrude023  label="Extrude foro per filo CAM sx"
  Base = -> Sketch025
  Dir = (0,-1,2e-16)
  DirMode = 2
  FaceMakerClass = Part::FaceMakerBullseye
  FaceMakerMode = 3
  LengthFwd = 4.9
  LengthRev = 0
  Placement = pos=(0,-6.95,0) rot=(0,0,1;0rad)
  Solid = true
  Symmetric = true
FEATURE [Sketcher::SketchObject] Sketch026  label="foro sotto anteriore M3x5x6"
  ArcFitTolerance = 1e-06
  AttachmentSupport = -> [XY_Plane]
  FullyConstrained = true
  MakeInternals = false
  MapMode = 5
  sketch-geometry (2):
    g0: LineSegment [constr] StartX=0 StartY=0 StartZ=0 EndX=-16.5 EndY=0 EndZ=0
    g1: Circle CenterX=-16.5 CenterY=0 CenterZ=0 NormalX=0 NormalY=0 NormalZ=1 AngleXU=0 Radius=2.5
  constraints (5):
    c: Distance(g0) = 16.5
    c: Coincident(g0,g-1)
    c: PointOnObject(g0,g-1)
    c: Diameter(g1) = 5
    c: Coincident(g0,g1)
FEATURE [Sketcher::SketchObject] Sketch027  label="foro sotto posteriore M3x5x6"
  ArcFitTolerance = 1e-06
  AttachmentSupport = -> [XY_Plane]
  ExternalGeometry = -> [Sketch]
  FullyConstrained = true
  MakeInternals = false
  MapMode = 5
  sketch-geometry (2):
    g0: LineSegment [constr] StartX=-82.8 StartY=2e-16 StartZ=0 EndX=-71.3 EndY=2e-16 EndZ=0
    g1: Circle CenterX=-71.3 CenterY=2e-16 CenterZ=0 NormalX=0 NormalY=0 NormalZ=1 AngleXU=0 Radius=2.5
  constraints (5):
    c: Distance(g0) = 11.5
    c: Coincident(g0,g-3)
    c: PointOnObject(g0,g-3)
    c: Diameter(g1) = 5
    c: Coincident(g1,g0)
FEATURE [Sketcher::SketchObject] Sketch029  label="fori sotto impugnatura"
  ArcFitTolerance = 1e-06
  AttachmentSupport = -> [XY_Plane]
  ExternalGeometry = -> [Sketch]
  FullyConstrained = true
  MakeInternals = false
  MapMode = 5
  sketch-geometry (15):
    g0: LineSegment [constr] StartX=-175.232 StartY=-1.83e-14 StartZ=0 EndX=-191.232 EndY=0 EndZ=0
    g1: Circle CenterX=-191.232 CenterY=0 CenterZ=0 NormalX=0 NormalY=0 NormalZ=1 AngleXU=0 Radius=3.95
    g2: LineSegment [constr] StartX=-175.232 StartY=-1.83e-14 StartZ=0 EndX=-204.275 EndY=0 EndZ=0
    g3: LineSegment StartX=-204.275 StartY=3.525 StartZ=0 EndX=-204.275 EndY=-3.525 EndZ=0
    g4: LineSegment StartX=-205.4 StartY=-4.65 StartZ=0 EndX=-206.65 EndY=-4.65 EndZ=0
    g5: LineSegment StartX=-207.775 StartY=-3.525 StartZ=0 EndX=-207.775 EndY=3.525 EndZ=0
    g6: LineSegment StartX=-206.65 StartY=4.65 StartZ=0 EndX=-205.4 EndY=4.65 EndZ=0
    g7: ArcOfCircle CenterX=-206.65 CenterY=3.525 CenterZ=0 NormalX=0 NormalY=0 NormalZ=1 AngleXU=0 Radius=1.125 StartAngle=1.5708 EndAngle=3.14159
    g8: GeomPoint [constr] X=-207.775 Y=4.65 Z=0
    g9: ArcOfCircle CenterX=-205.4 CenterY=3.525 CenterZ=0 NormalX=0 NormalY=0 NormalZ=1 AngleXU=0 Radius=1.125 StartAngle=0 EndAngle=1.5708
    g10: GeomPoint [constr] X=-204.275 Y=4.65 Z=0
    g11: ArcOfCircle CenterX=-205.4 CenterY=-3.525 CenterZ=0 NormalX=0 NormalY=0 NormalZ=1 AngleXU=0 Radius=1.125 StartAngle=4.71239 EndAngle=6.28319
    g12: GeomPoint [constr] X=-204.275 Y=-4.65 Z=0
    g13: ArcOfCircle CenterX=-206.65 CenterY=-3.525 CenterZ=0 NormalX=0 NormalY=0 NormalZ=1 AngleXU=0 Radius=1.125 StartAngle=3.14159 EndAngle=4.71239
    g14: GeomPoint [constr] X=-207.775 Y=-4.65 Z=0
  constraints (35):
    c: Distance(g0) = 16
    c: Coincident(g0,g-3)
    c: PointOnObject(g0,g-1)
    c: Diameter(g1) = 7.9
    c: Coincident(g1,g0)
    c: Coincident(g2,g0)
    c: PointOnObject(g2,g-1)
    c: Vertical(g3)
    c: Horizontal(g4)
    c: Vertical(g5)
    c: Horizontal(g6)
    c: DistanceY(g12,g10) = 9.3
    c: DistanceX(g8,g10) = 3.5
    c: Symmetric(g10,g12,g2)
    c: PointOnObject(g8,g5)
    c: PointOnObject(g8,g6)
    c: Tangent(g5,g7) = 1.5708
    c: Tangent(g6,g7) = 1.5708
    c: PointOnObject(g10,g3)
    c: PointOnObject(g10,g6)
    c: Tangent(g3,g9) = 1.5708
    c: Tangent(g6,g9) = 1.5708
    c: PointOnObject(g12,g3)
    c: PointOnObject(g12,g4)
    c: Tangent(g3,g11) = 1.5708
    c: Tangent(g4,g11) = 1.5708
    c: PointOnObject(g14,g4)
    c: PointOnObject(g14,g5)
    c: Tangent(g4,g13) = 1.5708
    c: Tangent(g5,g13) = 1.5708
    c: Equal(g7,g9)
    c: Equal(g9,g11)
    c: Equal(g11,g13)
    c: DistanceX(g6,g6) = 1.25
    c: DistanceX(g-5,g5) = 6.8
FEATURE [Sketcher::SketchObject] Sketch030  label="fori superiori per solenoide e oled"
  ArcFitTolerance = 1e-06
  AttachmentSupport = -> [XY_Plane]
  ExternalGeometry = -> [Sketch]
  FullyConstrained = true
  MakeInternals = false
  MapMode = 5
  sketch-geometry (33):
    g0: LineSegment [constr] StartX=-181.6 StartY=1.12e-14 StartZ=0 EndX=-169.91 EndY=0 EndZ=0
    g1: LineSegment [constr] StartX=-169.91 StartY=0 StartZ=0 EndX=-169.91 EndY=-2.6 EndZ=0
    g2: LineSegment [constr] StartX=-169.91 StartY=0 StartZ=0 EndX=-169.91 EndY=2.6 EndZ=0
    g3: LineSegment StartX=-169.91 StartY=4.975 StartZ=0 EndX=-169.91 EndY=8.225 EndZ=0
    g4: LineSegment StartX=-167.535 StartY=10.6 StartZ=0 EndX=-167.285 EndY=10.6 EndZ=0
    g5: LineSegment StartX=-164.91 StartY=8.225 StartZ=0 EndX=-164.91 EndY=4.975 EndZ=0
    g6: LineSegment StartX=-167.285 StartY=2.6 StartZ=0 EndX=-167.535 EndY=2.6 EndZ=0
    g7: LineSegment StartX=-169.91 StartY=-4.975 StartZ=0 EndX=-169.91 EndY=-8.225 EndZ=0
    g8: LineSegment StartX=-167.535 StartY=-10.6 StartZ=0 EndX=-167.285 EndY=-10.6 EndZ=0
    g9: LineSegment StartX=-164.91 StartY=-8.225 StartZ=0 EndX=-164.91 EndY=-4.975 EndZ=0
    g10: LineSegment StartX=-167.285 StartY=-2.6 StartZ=0 EndX=-167.535 EndY=-2.6 EndZ=0
    g11: ArcOfCircle CenterX=-167.535 CenterY=8.225 CenterZ=0 NormalX=0 NormalY=0 NormalZ=1 AngleXU=0 Radius=2.375 StartAngle=1.5708 EndAngle=3.14159
    g12: GeomPoint [constr] X=-169.91 Y=10.6 Z=0
    g13: ArcOfCircle CenterX=-167.285 CenterY=8.225 CenterZ=0 NormalX=0 NormalY=0 NormalZ=1 AngleXU=0 Radius=2.375 StartAngle=0 EndAngle=1.5708
    g14: GeomPoint [constr] X=-164.91 Y=10.6 Z=0
    g15: ArcOfCircle CenterX=-167.285 CenterY=4.975 CenterZ=0 NormalX=0 NormalY=0 NormalZ=1 AngleXU=0 Radius=2.375 StartAngle=4.71239 EndAngle=6.28319
    g16: GeomPoint [constr] X=-164.91 Y=2.6 Z=0
    g17: ArcOfCircle CenterX=-167.535 CenterY=4.975 CenterZ=0 NormalX=0 NormalY=0 NormalZ=1 AngleXU=0 Radius=2.375 StartAngle=3.14159 EndAngle=4.71239
    g18: GeomPoint [constr] X=-169.91 Y=2.6 Z=0
    g19: ArcOfCircle CenterX=-167.535 CenterY=-4.975 CenterZ=0 NormalX=0 NormalY=0 NormalZ=1 AngleXU=0 Radius=2.375 StartAngle=1.5708 EndAngle=3.14159
    g20: GeomPoint [constr] X=-169.91 Y=-2.6 Z=0
    g21: ArcOfCircle CenterX=-167.285 CenterY=-4.975 CenterZ=0 NormalX=0 NormalY=0 NormalZ=1 AngleXU=0 Radius=2.375 StartAngle=0 EndAngle=1.5708
    g22: GeomPoint [constr] X=-164.91 Y=-2.6 Z=0
    g23: ArcOfCircle CenterX=-167.285 CenterY=-8.225 CenterZ=0 NormalX=0 NormalY=0 NormalZ=1 AngleXU=0 Radius=2.375 StartAngle=4.71239 EndAngle=6.28319
    g24: GeomPoint [constr] X=-164.91 Y=-10.6 Z=0
    g25: ArcOfCircle CenterX=-167.535 CenterY=-8.225 CenterZ=0 NormalX=0 NormalY=0 NormalZ=1 AngleXU=0 Radius=2.375 StartAngle=3.14159 EndAngle=4.71239
    g26: GeomPoint [constr] X=-169.91 Y=-10.6 Z=0
    g27: LineSegment [constr] StartX=-181.6 StartY=1.12e-14 StartZ=0 EndX=-152.209 EndY=0 EndZ=0
    g28: LineSegment [constr] StartX=-181.6 StartY=1.12e-14 StartZ=0 EndX=-130.41 EndY=0 EndZ=0
    g29: LineSegment [constr] StartX=-152.209 StartY=0 StartZ=0 EndX=-152.209 EndY=6.95 EndZ=0
    g30: LineSegment [constr] StartX=-130.41 StartY=0 StartZ=0 EndX=-130.41 EndY=-6.95 EndZ=0
    g31: Circle CenterX=-152.209 CenterY=6.95 CenterZ=0 NormalX=0 NormalY=0 NormalZ=1 AngleXU=0 Radius=2.1
    g32: Circle CenterX=-130.41 CenterY=-6.95 CenterZ=0 NormalX=0 NormalY=0 NormalZ=1 AngleXU=0 Radius=2.1
  constraints (79):
    c: Distance(g0) = 11.69
    c: PointOnObject(g0,g-1)
    c: Coincident(g-4,g0)
    c: Distance(g1) = 2.6
    c: Coincident(g1,g0)
    c: Vertical(g1)
    c: Distance(g2) = 2.6
    c: Coincident(g2,g0)
    c: Vertical(g2)
    c: Distance(g18,g12) = 8
    c: Coincident(g18,g2)
    c: Vertical(g3)
    c: Distance(g14,g12) = 5
    c: Horizontal(g4)
    c: Distance(g16,g14) = 8
    c: Vertical(g5)
    c: Distance(g26,g20) = 8
    c: Coincident(g20,g1)
    c: Vertical(g7)
    c: Distance(g26,g24) = 5
    c: Horizontal(g8)
    c: Distance(g24,g22) = 8
    c: Vertical(g9)
    c: PointOnObject(g12,g3)
    c: PointOnObject(g12,g4)
    c: Tangent(g3,g11) = 1.5708
    c: Tangent(g4,g11) = 1.5708
    c: PointOnObject(g14,g5)
    c: PointOnObject(g14,g4)
    c: Tangent(g5,g13) = 1.5708
    c: Tangent(g4,g13) = 1.5708
    c: PointOnObject(g16,g5)
    c: PointOnObject(g16,g6)
    c: Tangent(g5,g15) = 1.5708
    c: Tangent(g6,g15) = 1.5708
    c: PointOnObject(g18,g3)
    c: PointOnObject(g18,g6)
    c: Tangent(g3,g17) = 1.5708
    c: Tangent(g6,g17) = 1.5708
    c: Equal(g11,g13)
    c: Equal(g13,g15)
    c: Equal(g15,g17)
    c: DistanceX(g4,g4) = 0.25
    c: PointOnObject(g20,g7)
    c: PointOnObject(g20,g10)
    c: Tangent(g7,g19) = -1.5708
    c: Tangent(g10,g19) = -1.5708
    c: PointOnObject(g22,g9)
    c: PointOnObject(g22,g10)
    c: Tangent(g9,g21) = -1.5708
    c: Tangent(g10,g21) = -1.5708
    c: PointOnObject(g24,g9)
    c: PointOnObject(g24,g8)
    c: Tangent(g9,g23) = -1.5708
    c: Tangent(g8,g23) = -1.5708
    c: PointOnObject(g26,g8)
    c: PointOnObject(g26,g7)
    c: Tangent(g8,g25) = -1.5708
    c: Tangent(g7,g25) = -1.5708
    c: Equal(g19,g21)
    c: Equal(g21,g23)
    c: Equal(g23,g25)
    c: DistanceX(g10,g10) = 0.25
    c: Distance(g27) = 29.391
    c: Coincident(g27,g0)
    c: PointOnObject(g27,g-1)
    c: Distance(g28) = 51.19
    c: Coincident(g28,g0)
    c: PointOnObject(g28,g-1)
    c: Distance(g29) = 6.95
    c: Coincident(g29,g27)
    c: Vertical(g29)
    c: Distance(g30) = 6.95
    c: Coincident(g30,g28)
    c: Vertical(g30)
    c: Diameter(g31) = 4.2
    c: Diameter(g32) = 4.2
    c: Coincident(g32,g30)
    c: Coincident(g31,g29)
FEATURE [Sketcher::SketchObject] Sketch031  label="fori inferiori switch pompa"
  ArcFitTolerance = 1e-06
  AttachmentSupport = -> [XY_Plane]
  ExternalGeometry = -> [Sketch]
  FullyConstrained = true
  MakeInternals = false
  MapMode = 5
  sketch-geometry (4):
    g0: LineSegment [constr] StartX=-57.2 StartY=1.9e-15 StartZ=0 EndX=-62.45 EndY=1.9e-15 EndZ=0
    g1: LineSegment [constr] StartX=-62.45 StartY=3.25 StartZ=0 EndX=-62.45 EndY=-3.25 EndZ=0
    g2: Circle CenterX=-62.45 CenterY=3.25 CenterZ=0 NormalX=0 NormalY=0 NormalZ=1 AngleXU=0 Radius=1.6
    g3: Circle CenterX=-62.45 CenterY=-3.25 CenterZ=0 NormalX=0 NormalY=0 NormalZ=1 AngleXU=0 Radius=1.6
  constraints (10):
    c: Distance(g0) = 5.25
    c: Coincident(g0,g-3)
    c: PointOnObject(g0,g-3)
    c: Vertical(g1)
    c: DistanceY(g1,g1) = 6.5
    c: Symmetric(g1,g1,g0)
    c: Diameter(g2) = 3.2
    c: Diameter(g3) = 3.2
    c: Coincident(g2,g1)
    c: Coincident(g3,g1)
FEATURE [Sketcher::SketchObject] Sketch032  label="spazio per PILA 18650"
  ArcFitTolerance = 1e-06
  AttachmentSupport = -> [XY_Plane]
  ExternalGeometry = -> [Sketch]
  FullyConstrained = true
  MakeInternals = false
  MapMode = 5
  sketch-geometry (2):
    g0: LineSegment [constr] StartX=-178.142 StartY=-1.74e-14 StartZ=0 EndX=-191.142 EndY=-1.83e-14 EndZ=0
    g1: Circle CenterX=-191.142 CenterY=-1.83e-14 CenterZ=0 NormalX=0 NormalY=0 NormalZ=1 AngleXU=0 Radius=10.5
  constraints (5):
    c: Distance(g0) = 13
    c: Coincident(g0,g-3)
    c: PointOnObject(g0,g-4)
    c: Diameter(g1) = 21
    c: Coincident(g1,g0)
FEATURE [Part::Extrusion] Extrude030  label="Extrude spazio per PILA 18650"
  Base = -> Sketch032
  Dir = (0,0,1)
  DirLink = -> Sketch [Edge45]
  DirMode = 2
  FaceMakerClass = Part::FaceMakerBullseye
  FaceMakerMode = 3
  LengthFwd = 76
  LengthRev = 0
  Placement = pos=(6,0,-72) rot=(0,0,1;0rad)
  Solid = true
  Symmetric = false
FEATURE [Sketcher::SketchObject] Sketch033  label="fermo per scheda micro"
  ArcFitTolerance = 1e-06
  AttachmentSupport = -> [XZ_Plane]
  ExternalGeometry = -> [Sketch]
  FullyConstrained = true
  MakeInternals = false
  MapMode = 5
  Placement = pos=(0,0,0) rot=(1,0,0;1.5708rad)
  sketch-geometry (12):
    g0: LineSegment StartX=-11.6 StartY=6 StartZ=0 EndX=-4 EndY=6 EndZ=0
    g1: LineSegment StartX=-4 StartY=6 StartZ=0 EndX=-4 EndY=36.4 EndZ=0
    g2: LineSegment StartX=-4 StartY=36.4 StartZ=0 EndX=-11.6 EndY=36.4 EndZ=0
    g3: LineSegment StartX=-11.6 StartY=36.4 StartZ=0 EndX=-11.6 EndY=6 EndZ=0
    g4: LineSegment StartX=-80.11 StartY=11.6 StartZ=0 EndX=-70.51 EndY=11.6 EndZ=0
    g5: LineSegment StartX=-70.51 StartY=11.6 StartZ=0 EndX=-70.51 EndY=6 EndZ=0
    g6: LineSegment StartX=-70.51 StartY=6 StartZ=0 EndX=-80.11 EndY=6 EndZ=0
    g7: LineSegment StartX=-80.11 StartY=6 StartZ=0 EndX=-80.11 EndY=11.6 EndZ=0
    g8: LineSegment StartX=-78.51 StartY=36.4 StartZ=0 EndX=-70.51 EndY=36.4 EndZ=0
    g9: LineSegment StartX=-70.51 StartY=36.4 StartZ=0 EndX=-70.51 EndY=30.8 EndZ=0
    g10: LineSegment StartX=-70.51 StartY=30.8 StartZ=0 EndX=-78.51 EndY=30.8 EndZ=0
    g11: LineSegment StartX=-78.51 StartY=30.8 StartZ=0 EndX=-78.51 EndY=36.4 EndZ=0
  constraints (33):
    c: Horizontal(g0)
    c: Coincident(g1,g0)
    c: Coincident(g2,g1)
    c: Horizontal(g2)
    c: Coincident(g3,g2)
    c: Coincident(g3,g0)
    c: Vertical(g3)
    c: DistanceX(g2,g2) = 7.6
    c: Coincident(g1,g-3)
    c: Coincident(g0,g-3)
    c: Horizontal(g4)
    c: Coincident(g5,g4)
    c: Vertical(g5)
    c: Coincident(g6,g5)
    c: Horizontal(g6)
    c: Coincident(g7,g6)
    c: Coincident(g7,g4)
    c: Vertical(g7)
    c: DistanceY(g5,g5) = 5.6
    c: DistanceX(g4,g4) = 9.6
    c: Coincident(g9,g8)
    c: Vertical(g9)
    c: Coincident(g10,g9)
    c: Horizontal(g10)
    c: Coincident(g11,g10)
    c: Coincident(g11,g8)
    c: Vertical(g11)
    c: DistanceY(g9,g9) = 5.6
    c: DistanceX(g10,g10) = 8
    c: Coincident(g4,g-4)
    c: DistanceX(g4,g10) = 1.6
    c: Horizontal(g8)
    c: DistanceY(g8,g1) = 0
FEATURE [Sketcher::SketchObject] Sketch034  label="buchi guida rail"
  ArcFitTolerance = 1e-06
  AttachmentSupport = -> [XY_Plane]
  ExternalGeometry = -> [Sketch]
  FullyConstrained = true
  MakeInternals = false
  MapMode = 5
  sketch-geometry (6):
    g0: LineSegment [constr] StartX=-100.8 StartY=9.1e-15 StartZ=0 EndX=-93.3 EndY=0 EndZ=0
    g1: LineSegment [constr] StartX=-93.3 StartY=0 StartZ=0 EndX=-73.3 EndY=0 EndZ=0
    g2: LineSegment [constr] StartX=-73.3 StartY=0 StartZ=0 EndX=-53.3 EndY=0 EndZ=0
    g3: Circle CenterX=-93.3 CenterY=0 CenterZ=0 NormalX=0 NormalY=0 NormalZ=1 AngleXU=0 Radius=2.5
    g4: Circle CenterX=-73.3 CenterY=0 CenterZ=0 NormalX=0 NormalY=0 NormalZ=1 AngleXU=0 Radius=2.5
    g5: Circle CenterX=-53.3 CenterY=0 CenterZ=0 NormalX=0 NormalY=0 NormalZ=1 AngleXU=0 Radius=2.5
  constraints (15):
    c: Distance(g0) = 7.5
    c: Coincident(g0,g-3)
    c: PointOnObject(g0,g-1)
    c: Distance(g1) = 20
    c: Coincident(g1,g0)
    c: PointOnObject(g1,g-1)
    c: Distance(g2) = 20
    c: Coincident(g2,g1)
    c: PointOnObject(g2,g-1)
    c: Diameter(g3) = 5
    c: Diameter(g4) = 5
    c: Diameter(g5) = 5
    c: Coincident(g3,g0)
    c: Coincident(g4,g1)
    c: Coincident(g5,g2)
FEATURE [Part::Extrusion] Extrude032  label="Extrude buchi guida rail"
  Base = -> Sketch034
  Dir = (0,0,1)
  DirMode = 2
  FaceMakerClass = Part::FaceMakerBullseye
  FaceMakerMode = 3
  LengthFwd = -6.2
  LengthRev = 0
  Placement = pos=(0,0,43.2) rot=(0,0,1;0rad)
  Solid = true
  Symmetric = false
FEATURE [Part::Extrusion] Extrude033  label="Extrude fori superiori per solenoide e oled001"
  Base = -> Sketch030
  Dir = (0,0,1)
  DirMode = 2
  FaceMakerClass = Part::FaceMakerBullseye
  FaceMakerMode = 3
  LengthFwd = -4.8
  LengthRev = 0
  Placement = pos=(0,0,41.2) rot=(0,0,1;0rad)
  Solid = true
  Symmetric = false
FEATURE [Part::Extrusion] Extrude034  label="Extrude fori sotto impugnatura001"
  Base = -> Sketch029
  Dir = (0,0,1)
  DirMode = 2
  FaceMakerClass = Part::FaceMakerBullseye
  FaceMakerMode = 3
  LengthFwd = 5
  LengthRev = 0
  Placement = pos=(0,0,-83) rot=(0,0,1;0rad)
  Solid = true
  Symmetric = false
FEATURE [Part::Extrusion] Extrude035  label="Extrude fori inferiori switch pompa001"
  Base = -> Sketch031
  Dir = (0,0,1)
  DirMode = 2
  FaceMakerClass = Part::FaceMakerBullseye
  FaceMakerMode = 3
  LengthFwd = 4
  LengthRev = 0
  Placement = pos=(0,0,-1.7) rot=(0,0,1;0rad)
  Solid = true
  Symmetric = false
FEATURE [Part::Extrusion] Extrude036  label="Extrude foro sotto posteriore M3x5x007"
  Base = -> Sketch027
  Dir = (0,0,1)
  DirMode = 2
  FaceMakerClass = Part::FaceMakerBullseye
  FaceMakerMode = 3
  LengthFwd = 6.2
  LengthRev = 0
  Placement = pos=(0,0,-9.6) rot=(0,0,1;0rad)
  Solid = true
  Symmetric = false
FEATURE [Part::Extrusion] Extrude037  label="Extrude foro sotto anteriore M3x5x007"
  Base = -> Sketch026
  Dir = (0,0,1)
  DirMode = 2
  FaceMakerClass = Part::FaceMakerBullseye
  FaceMakerMode = 3
  LengthFwd = 6.2
  LengthRev = 0
  Solid = true
  Symmetric = false
FEATURE [Sketcher::SketchObject] Sketch035  label="foro per fissaggio micro"
  ArcFitTolerance = 1e-06
  AttachmentSupport = -> [XZ_Plane]
  ExternalGeometry = -> [Sketch,Sketch033]
  FullyConstrained = true
  MakeInternals = false
  MapMode = 5
  Placement = pos=(0,0,0) rot=(1,0,0;1.5708rad)
  sketch-geometry (3):
    g0: Circle CenterX=-7.8 CenterY=21.2 CenterZ=0 NormalX=0 NormalY=0 NormalZ=1 AngleXU=0 Radius=1.6
    g1: GeomPoint [constr] X=-4 Y=21.2 Z=0
    g2: LineSegment [constr] StartX=-4 StartY=21.2 StartZ=0 EndX=-11.6 EndY=21.2 EndZ=0
  constraints (6):
    c: Diameter(g0) = 3.2
    c: Symmetric(g-3,g-3,g1)
    c: Coincident(g2,g1)
    c: Horizontal(g2)
    c: DistanceX(g-4,g2) = 0
    c: Symmetric(g2,g1,g0)
FEATURE [Part::Extrusion] Extrude038  label="Extrude foro per fissaggio micro"
  Base = -> Sketch035
  Dir = (0,-1,2e-16)
  DirMode = 2
  FaceMakerClass = Part::FaceMakerBullseye
  FaceMakerMode = 3
  LengthFwd = 3
  LengthRev = 0
  Placement = pos=(0,8.6,0) rot=(0,0,1;0rad)
  Solid = true
  Symmetric = false
FEATURE [Sketcher::SketchObject] Sketch036  label="supporto per alimentatore"
  ArcFitTolerance = 1e-06
  AttachmentSupport = -> [XZ_Plane]
  ExternalGeometry = -> [Sketch,Sketch016,Sketch022]
  FullyConstrained = true
  MakeInternals = false
  MapMode = 5
  Placement = pos=(0,0,0) rot=(1,0,0;1.5708rad)
  sketch-geometry (5):
    g0: LineSegment StartX=-211.843 StartY=-50.0944 StartZ=0 EndX=-211.843 EndY=-80.4316 EndZ=0
    g1: LineSegment StartX=-211.843 StartY=-50.0944 StartZ=0 EndX=-207.775 EndY=-41.3701 EndZ=0
    g2: LineSegment [constr] StartX=-209.443 StartY=-50.0944 StartZ=0 EndX=-209.443 EndY=-80.4316 EndZ=0
    g3: LineSegment StartX=-207.775 StartY=-41.3701 StartZ=0 EndX=-207.775 EndY=-80.4316 EndZ=0
    g4: LineSegment StartX=-211.843 StartY=-80.4316 StartZ=0 EndX=-207.775 EndY=-80.4316 EndZ=0
  constraints (15):
    c: Vertical(g0)
    c: Coincident(g1,g0)
    c: Vertical(g2)
    c: Tangent(g2,g-5)
    c: Coincident(g3,g1)
    c: Vertical(g3)
    c: DistanceY(g-3,g3) = -2
    c: Tangent(g1,g-8)
    c: DistanceY(g-3,g0) = -2
    c: Coincident(g4,g0)
    c: Coincident(g4,g3)
    c: Tangent(g0,g-6)
    c: DistanceY(g-3,g2) = -2
    c: DistanceY(g2,g0) = 0
    c: DistanceX(g-3,g3) = 6.8
FEATURE [Part::Extrusion] Extrude039  label="Extrude039 supporto alimentatore"
  Base = -> Sketch036
  Dir = (0,-1,2e-16)
  DirMode = 2
  FaceMakerClass = Part::FaceMakerBullseye
  FaceMakerMode = 3
  LengthFwd = 25.2
  LengthRev = 0
  Solid = true
  Symmetric = true
FEATURE [Sketcher::SketchObject] Sketch037  label="scavo per alimentatore"
  ArcFitTolerance = 1e-06
  AttachmentSupport = -> [XZ_Plane]
  ExternalGeometry = -> [Sketch036]
  FullyConstrained = true
  MakeInternals = false
  MapMode = 5
  Placement = pos=(0,0,0) rot=(1,0,0;1.5708rad)
  sketch-geometry (4):
    g0: LineSegment StartX=-209.575 StartY=-50.4316 StartZ=0 EndX=-209.575 EndY=-80.4316 EndZ=0
    g1: LineSegment StartX=-209.575 StartY=-50.4316 StartZ=0 EndX=-207.775 EndY=-50.4316 EndZ=0
    g2: LineSegment StartX=-207.775 StartY=-50.4316 StartZ=0 EndX=-207.775 EndY=-80.4316 EndZ=0
    g3: LineSegment StartX=-207.775 StartY=-80.4316 StartZ=0 EndX=-209.575 EndY=-80.4316 EndZ=0
  constraints (11):
    c: Vertical(g0)
    c: Coincident(g1,g0)
    c: Horizontal(g1)
    c: Coincident(g2,g1)
    c: Vertical(g2)
    c: Coincident(g3,g2)
    c: Coincident(g3,g0)
    c: Horizontal(g3)
    c: DistanceX(g1,g1) = 1.8
    c: Coincident(g2,g-3)
    c: DistanceY(g2,g2) = 30
FEATURE [Part::Extrusion] Extrude040  label="Extrude040 scavo alimentatore"
  Base = -> Sketch037
  Dir = (0,-1,2e-16)
  DirMode = 2
  FaceMakerClass = Part::FaceMakerBullseye
  FaceMakerMode = 3
  LengthFwd = 19.5
  LengthRev = 0
  Solid = true
  Symmetric = true
FEATURE [Part::Extrusion] Extrude031  label="Extrude fermo per scheda micro"
  Base = -> Sketch033
  Dir = (0,-1,2e-16)
  DirMode = 2
  FaceMakerClass = Part::FaceMakerBullseye
  FaceMakerMode = 3
  LengthFwd = 3
  LengthRev = 0
  Placement = pos=(0,8.6,0) rot=(0,0,1;0rad)
  Solid = true
  Symmetric = false
FEATURE [Sketcher::SketchObject] Sketch038  label="scavo driver solenoide"
  ArcFitTolerance = 1e-06
  AttachmentSupport = -> [XZ_Plane]
  ExternalGeometry = -> [Sketch,Sketch036]
  FullyConstrained = true
  MakeInternals = false
  MapMode = 5
  Placement = pos=(0,0,0) rot=(1,0,0;1.5708rad)
  sketch-geometry (7):
    g0: LineSegment StartX=-192.222 StartY=-8.0175 StartZ=0 EndX=-194.941 EndY=-6.74965 EndZ=0
    g1: LineSegment StartX=-194.941 StartY=-6.74965 StartZ=0 EndX=-212.269 EndY=-43.9083 EndZ=0
    g2: LineSegment StartX=-192.222 StartY=-8.0175 StartZ=0 EndX=-188.779 EndY=-9.62345 EndZ=0
    g3: LineSegment StartX=-188.779 StartY=-9.62345 StartZ=0 EndX=-205.357 EndY=-45.1761 EndZ=0
    g4: LineSegment StartX=-205.357 StartY=-45.1761 StartZ=0 EndX=-209.55 EndY=-45.1761 EndZ=0
    g5: LineSegment [constr] StartX=-212.269 StartY=-43.9083 StartZ=0 EndX=-209.55 EndY=-45.1761 EndZ=0
    g6: LineSegment StartX=-212.269 StartY=-43.9083 StartZ=0 EndX=-209.55 EndY=-45.1761 EndZ=0
  constraints (20):
    c: Coincident(g1,g0)
    c: Coincident(g3,g2)
    c: Coincident(g4,g3)
    c: Distance(g2) = 3.8
    c: Distance(g1) = 41
    c: Coincident(g5,g1)
    c: Distance(g5) = 3
    c: Perpendicular(g5,g-3)
    c: Parallel(g1,g-3)
    c: Perpendicular(g1,g0)
    c: Distance(g0) = 3
    c: Coincident(g6,g1)
    c: Parallel(g3,g-3)
    c: Perpendicular(g2,g3)
    c: Coincident(g2,g0)
    c: Perpendicular(g-4,g4)
    c: PointOnObject(g5,g-3)
    c: Distance(g-3,g5) = 9.6
    c: Coincident(g4,g5)
    c: Coincident(g6,g4)
FEATURE [Part::Extrusion] Extrude041  label="Extrude scavo driver solenoide"
  Base = -> Sketch038
  Dir = (0,-1,2e-16)
  DirMode = 2
  FaceMakerClass = Part::FaceMakerBullseye
  FaceMakerMode = 3
  LengthFwd = 20.6
  LengthRev = 0
  Solid = true
  Symmetric = true
FEATURE [Sketcher::SketchObject] Sketch039  label="scavo per cavo usb per micro"
  ArcFitTolerance = 1e-06
  AttachmentSupport = -> [XZ_Plane]
  ExternalGeometry = -> [Sketch,Sketch016]
  FullyConstrained = true
  MakeInternals = false
  MapMode = 5
  Placement = pos=(0,0,0) rot=(1,0,0;1.5708rad)
  sketch-geometry (4):
    g0: LineSegment StartX=-82.51 StartY=36.4 StartZ=0 EndX=-74.51 EndY=36.4 EndZ=0
    g1: LineSegment StartX=-74.51 StartY=36.4 StartZ=0 EndX=-74.51 EndY=30.8 EndZ=0
    g2: LineSegment StartX=-74.51 StartY=30.8 StartZ=0 EndX=-82.51 EndY=30.8 EndZ=0
    g3: LineSegment StartX=-82.51 StartY=30.8 StartZ=0 EndX=-82.51 EndY=36.4 EndZ=0
  constraints (11):
    c: Coincident(g1,g0)
    c: Vertical(g1)
    c: Coincident(g2,g1)
    c: Horizontal(g2)
    c: Coincident(g3,g2)
    c: Coincident(g3,g0)
    c: Vertical(g3)
    c: Tangent(g0,g-3)
    c: Tangent(g2,g-4)
    c: Tangent(g3,g-4)
    c: Tangent(g1,g-4)
FEATURE [Part::Extrusion] Extrude042  label="Extrude scavo per cavo usb per micro"
  Base = -> Sketch039
  Dir = (0,-1,2e-16)
  DirMode = 2
  FaceMakerClass = Part::FaceMakerBullseye
  FaceMakerMode = 3
  LengthFwd = 11.2
  LengthRev = 0
  Solid = true
  Symmetric = true
FEATURE [Sketcher::SketchObject] Sketch040  label="scavo saldature alimentatore connettore 5v"
  ArcFitTolerance = 1e-06
  AttachmentSupport = -> [XZ_Plane]
  ExternalGeometry = -> [Sketch037]
  FullyConstrained = true
  MakeInternals = false
  MapMode = 5
  Placement = pos=(0,0,0) rot=(1,0,0;1.5708rad)
  sketch-geometry (4):
    g0: LineSegment StartX=-211.175 StartY=-52.4316 StartZ=0 EndX=-211.175 EndY=-56.4316 EndZ=0
    g1: LineSegment StartX=-211.175 StartY=-52.4316 StartZ=0 EndX=-209.575 EndY=-52.4316 EndZ=0
    g2: LineSegment StartX=-209.575 StartY=-52.4316 StartZ=0 EndX=-209.575 EndY=-56.4316 EndZ=0
    g3: LineSegment StartX=-209.575 StartY=-56.4316 StartZ=0 EndX=-211.175 EndY=-56.4316 EndZ=0
  constraints (11):
    c: Vertical(g0)
    c: Coincident(g1,g0)
    c: Horizontal(g1)
    c: Coincident(g2,g1)
    c: Coincident(g3,g2)
    c: Coincident(g3,g0)
    c: Horizontal(g3)
    c: DistanceX(g1,g1) = 1.6
    c: DistanceY(g2,g2) = 4
    c: Tangent(g2,g-3)
    c: DistanceY(g1,g-3) = 2
FEATURE [Part::Extrusion] Extrude043  label="Extrude scavo saldature alimentatore connettore 5v"
  Base = -> Sketch040
  Dir = (0,-1,2e-16)
  DirMode = 2
  FaceMakerClass = Part::FaceMakerBullseye
  FaceMakerMode = 3
  LengthFwd = 8
  LengthRev = 0
  Solid = true
  Symmetric = true
FEATURE [Sketcher::SketchObject] Sketch041  label="scavo saldature alimentatore connettore 5v verticali"
  ArcFitTolerance = 1e-06
  AttachmentSupport = -> [XZ_Plane]
  ExternalGeometry = -> [Sketch037]
  FullyConstrained = true
  MakeInternals = false
  MapMode = 5
  Placement = pos=(0,0,0) rot=(1,0,0;1.5708rad)
  sketch-geometry (4):
    g0: LineSegment StartX=-211.175 StartY=-53.6316 StartZ=0 EndX=-209.575 EndY=-53.6316 EndZ=0
    g1: LineSegment StartX=-209.575 StartY=-53.6316 StartZ=0 EndX=-209.575 EndY=-76.6316 EndZ=0
    g2: LineSegment StartX=-209.575 StartY=-76.6316 StartZ=0 EndX=-211.175 EndY=-76.6316 EndZ=0
    g3: LineSegment StartX=-211.175 StartY=-76.6316 StartZ=0 EndX=-211.175 EndY=-53.6316 EndZ=0
  constraints (11):
    c: Horizontal(g0)
    c: Coincident(g1,g0)
    c: Coincident(g2,g1)
    c: Horizontal(g2)
    c: Coincident(g3,g2)
    c: Coincident(g3,g0)
    c: Vertical(g3)
    c: DistanceY(g3,g3) = 23
    c: DistanceX(g0,g0) = 1.6
    c: Tangent(g1,g-3)
    c: DistanceY(g0,g-3) = 3.2
FEATURE [Part::Extrusion] Extrude044  label="Extrude scavo saldature alimentatore connettore 5v verticali"
  Base = -> Sketch041
  Dir = (0,-1,2e-16)
  DirMode = 2
  FaceMakerClass = Part::FaceMakerBullseye
  FaceMakerMode = 3
  LengthFwd = 3.2
  LengthRev = 0
  Placement = pos=(0,8.3,0) rot=(0,0,1;0rad)
  Solid = true
  Symmetric = false
FEATURE [Sketcher::SketchObject] Sketch042  label="fermi per driver solenoide e alimentatore"
  ArcFitTolerance = 1e-06
  AttachmentSupport = -> [XZ_Plane]
  ExternalGeometry = -> [Sketch036,Sketch037,Sketch,Sketch038]
  FullyConstrained = true
  MakeInternals = false
  MapMode = 5
  Placement = pos=(0,0,0) rot=(1,0,0;1.5708rad)
  sketch-geometry (27):
    g0: LineSegment StartX=-200.506 StartY=-25.7811 StartZ=0 EndX=-201.436 EndY=-27.775 EndZ=0
    g1: LineSegment StartX=-201.436 StartY=-27.775 StartZ=0 EndX=-199.442 EndY=-28.7048 EndZ=0
    g2: LineSegment StartX=-199.442 StartY=-28.7048 StartZ=0 EndX=-198.512 EndY=-26.7109 EndZ=0
    g3: LineSegment StartX=-198.512 StartY=-26.7109 StartZ=0 EndX=-200.506 EndY=-25.7811 EndZ=0
    g4: LineSegment StartX=-201.28 StartY=-23.6549 StartZ=0 EndX=-203.562 EndY=-28.5489 EndZ=0
    g5: LineSegment StartX=-203.562 StartY=-28.5489 StartZ=0 EndX=-200.118 EndY=-30.1549 EndZ=0
    g6: LineSegment StartX=-197.992 StartY=-29.381 StartZ=0 EndX=-197.062 EndY=-27.3871 EndZ=0
    g7: LineSegment StartX=-197.836 StartY=-25.2608 StartZ=0 EndX=-201.28 EndY=-23.6549 EndZ=0
    g8: LineSegment [constr] StartX=-198.668 StartY=-30.8311 StartZ=0 EndX=-197.992 EndY=-29.381 EndZ=0
    g9: LineSegment [constr] StartX=-198.668 StartY=-30.8311 StartZ=0 EndX=-200.118 EndY=-30.1549 EndZ=0
    g10: ArcOfCircle CenterX=-198.512 CenterY=-26.7109 CenterZ=0 NormalX=0 NormalY=0 NormalZ=1 AngleXU=0 Radius=1.6 StartAngle=5.84685 EndAngle=7.41765
    g11: GeomPoint [constr] X=-196.386 Y=-25.937 Z=0
    g12: ArcOfCircle CenterX=-199.442 CenterY=-28.7048 CenterZ=0 NormalX=0 NormalY=0 NormalZ=1 AngleXU=0 Radius=1.6 StartAngle=4.27606 EndAngle=5.84685
    g13: GeomPoint [constr] X=-198.668 Y=-30.8311 Z=0
    g14: LineSegment StartX=-207.775 StartY=-46.8316 StartZ=0 EndX=-207.775 EndY=-50.8316 EndZ=0
    g15: LineSegment StartX=-207.775 StartY=-46.8316 StartZ=0 EndX=-203.775 EndY=-46.8316 EndZ=0
    g16: LineSegment StartX=-203.775 StartY=-46.8316 StartZ=0 EndX=-203.775 EndY=-50.8316 EndZ=0
    g17: LineSegment StartX=-207.775 StartY=-50.8316 StartZ=0 EndX=-203.775 EndY=-50.8316 EndZ=0
    g18: LineSegment StartX=-209.375 StartY=-52.4316 StartZ=0 EndX=-203.775 EndY=-52.4316 EndZ=0
    g19: LineSegment StartX=-202.175 StartY=-50.8316 StartZ=0 EndX=-202.175 EndY=-46.8316 EndZ=0
    g20: LineSegment StartX=-203.775 StartY=-45.2316 StartZ=0 EndX=-209.375 EndY=-45.2316 EndZ=0
    g21: LineSegment StartX=-209.375 StartY=-45.2316 StartZ=0 EndX=-209.375 EndY=-52.4316 EndZ=0
    g22: ArcOfCircle CenterX=-203.775 CenterY=-46.8316 CenterZ=0 NormalX=0 NormalY=0 NormalZ=1 AngleXU=0 Radius=1.6 StartAngle=1.8e-15 EndAngle=1.5708
    g23: GeomPoint [constr] X=-202.175 Y=-45.2316 Z=0
    g24: ArcOfCircle CenterX=-203.775 CenterY=-50.8316 CenterZ=0 NormalX=0 NormalY=0 NormalZ=1 AngleXU=0 Radius=1.6 StartAngle=4.71239 EndAngle=6.28319
    g25: GeomPoint [constr] X=-202.175 Y=-52.4316 Z=0
    g26: LineSegment [constr] StartX=-207.775 StartY=-50.4316 StartZ=0 EndX=-207.775 EndY=-50.8316 EndZ=0
  constraints (69):
    c: Coincident(g1,g0)
    c: Coincident(g2,g1)
    c: Coincident(g3,g2)
    c: Coincident(g3,g0)
    c: Parallel(g0,g2)
    c: Perpendicular(g3,g0)
    c: Perpendicular(g1,g0)
    c: Coincident(g5,g4)
    c: Coincident(g7,g4)
    c: Distance(g3) = 2.2
    c: Distance(g2) = 2.2
    c: Parallel(g6,g2)
    c: Parallel(g6,g4)
    c: Perpendicular(g5,g6)
    c: Perpendicular(g7,g6)
    c: Distance(g13,g11) = 5.4
    c: Distance(g5,g13) = 5.4
    c: Coincident(g9,g8)
    c: Distance(g8) = 1.6
    c: Distance(g9) = 1.6
    c: Perpendicular(g9,g8)
    c: Parallel(g8,g6)
    c: Coincident(g8,g13)
    c: Distance(g8,g1) = 1.6
    c: Distance(g9,g1) = 1.6
    c: Tangent(g0,g-5)
    c: Distance(g0,g-6) = 19.2
    c: PointOnObject(g11,g7)
    c: PointOnObject(g11,g6)
    c: Tangent(g7,g10) = -1.5708
    c: Tangent(g6,g10) = -1.5708
    c: PointOnObject(g13,g5)
    c: Tangent(g5,g12) = -1.5708
    c: Tangent(g6,g12) = -1.5708
    c: Equal(g10,g12)
    c: Coincident(g10,g2)
    c: Vertical(g14)
    c: Coincident(g15,g14)
    c: Horizontal(g15)
    c: Coincident(g16,g15)
    c: Vertical(g16)
    c: Coincident(g17,g14)
    c: Coincident(g17,g16)
    c: Horizontal(g17)
    c: Distance(g16) = 4
    c: Distance(g15) = 4
    c: Horizontal(g18)
    c: Vertical(g19)
    c: Horizontal(g20)
    c: Coincident(g21,g20)
    c: Coincident(g21,g18)
    c: Vertical(g21)
    c: Distance(g20,g23) = 7.2
    c: Distance(g25,g23) = 7.2
    c: DistanceY(g18,g14) = 1.6
    c: DistanceX(g18,g14) = 1.6
    c: PointOnObject(g23,g20)
    c: PointOnObject(g23,g19)
    c: Tangent(g20,g22) = -1.5708
    c: Tangent(g19,g22) = -1.5708
    c: PointOnObject(g25,g19)
    c: Tangent(g18,g24) = -1.5708
    c: Tangent(g19,g24) = -1.5708
    c: Equal(g22,g24)
    c: Coincident(g22,g15)
    c: Vertical(g26)
    c: Distance(g26) = 0.4
    c: Coincident(g26,g-4)
    c: Coincident(g14,g26)
FEATURE [Part::Extrusion] Extrude045  label="Extrude fermi per driver solenoide e alimentatore"
  Base = -> Sketch042
  Dir = (0,-1,2e-16)
  DirMode = 2
  FaceMakerClass = Part::FaceMakerBullseye
  FaceMakerMode = 3
  LengthFwd = 25.2
  LengthRev = 0
  Solid = true
  Symmetric = true
FEATURE [Sketcher::SketchObject] Sketch043  label="scavo pulizia fermo alimentatore"
  ArcFitTolerance = 1e-06
  AttachmentSupport = -> [XZ_Plane]
  ExternalGeometry = -> [Sketch042,Sketch036,Sketch037]
  FullyConstrained = true
  MakeInternals = false
  MapMode = 5
  Placement = pos=(0,0,0) rot=(1,0,0;1.5708rad)
  sketch-geometry (6):
    g0: LineSegment StartX=-209.375 StartY=-52.4316 StartZ=0 EndX=-209.375 EndY=-50.4316 EndZ=0
    g1: LineSegment StartX=-209.375 StartY=-50.4316 StartZ=0 EndX=-207.775 EndY=-50.4316 EndZ=0
    g2: LineSegment StartX=-207.775 StartY=-50.4316 StartZ=0 EndX=-207.775 EndY=-45.2316 EndZ=0
    g3: LineSegment StartX=-207.775 StartY=-45.2316 StartZ=0 EndX=-202.175 EndY=-45.2316 EndZ=0
    g4: LineSegment StartX=-202.175 StartY=-45.2316 StartZ=0 EndX=-202.175 EndY=-52.4316 EndZ=0
    g5: LineSegment StartX=-202.175 StartY=-52.4316 StartZ=0 EndX=-209.375 EndY=-52.4316 EndZ=0
  constraints (13):
    c: Vertical(g0)
    c: Coincident(g1,g0)
    c: Coincident(g2,g1)
    c: Coincident(g3,g2)
    c: Coincident(g4,g3)
    c: Coincident(g5,g4)
    c: Coincident(g5,g0)
    c: Horizontal(g5)
    c: Coincident(g0,g-6)
    c: Tangent(g1,g-8)
    c: Tangent(g2,g-4)
    c: Tangent(g3,g-7)
    c: Tangent(g4,g-3)
FEATURE [Part::Extrusion] Extrude046  label="Extrude scavo pulizia fermo alimentatore"
  Base = -> Sketch043
  Dir = (0,-1,2e-16)
  DirMode = 2
  FaceMakerClass = Part::FaceMakerBullseye
  FaceMakerMode = 3
  LengthFwd = 19.5
  LengthRev = 0
  Solid = true
  Symmetric = true
FEATURE [Sketcher::SketchObject] Sketch044  label="buchini per fissaggio oled"
  ArcFitTolerance = 1e-06
  AttachmentSupport = -> [YZ_Plane]
  ExternalGeometry = -> [Sketch]
  FullyConstrained = true
  MakeInternals = false
  MapMode = 5
  Placement = pos=(0,0,0) rot=(0.57735,0.57735,0.57735;2.0944rad)
  sketch-geometry (5):
    g0: LineSegment [constr] StartX=1.5e-14 StartY=67.3588 StartZ=0 EndX=0 EndY=64.3588 EndZ=0
    g1: LineSegment [constr] StartX=0 StartY=64.3588 StartZ=0 EndX=10.4 EndY=64.3588 EndZ=0
    g2: LineSegment [constr] StartX=0 StartY=64.3588 StartZ=0 EndX=-10.4 EndY=64.3588 EndZ=0
    g3: Circle CenterX=10.4 CenterY=64.3588 CenterZ=0 NormalX=0 NormalY=0 NormalZ=1 AngleXU=0 Radius=1.5
    g4: Circle CenterX=-10.4 CenterY=64.3588 CenterZ=0 NormalX=0 NormalY=0 NormalZ=1 AngleXU=0 Radius=1.5
  constraints (13):
    c: Distance(g0) = 3
    c: PointOnObject(g0,g-2)
    c: Coincident(g1,g0)
    c: Horizontal(g1)
    c: Coincident(g2,g0)
    c: Horizontal(g2)
    c: DistanceX(g1,g1) = 10.4
    c: Coincident(g3,g1)
    c: Diameter(g4) = 3
    c: Coincident(g4,g2)
    c: Coincident(g0,g-7)
    c: Equal(g1,g2)
    c: Equal(g4,g3)
FEATURE [Part::Extrusion] Extrude047  label="Extrude buchini per fissaggio oled"
  Base = -> Sketch044
  Dir = (1,0,0)
  DirMode = 2
  FaceMakerClass = Part::FaceMakerBullseye
  FaceMakerMode = 3
  LengthFwd = 10
  LengthRev = 0
  Placement = pos=(-186,0,0) rot=(0,0,1;0rad)
  Solid = true
  Symmetric = false
FEATURE [Sketcher::SketchObject] Sketch046  label="scavo 5x5 neopixel"
  ArcFitTolerance = 1e-06
  AttachmentSupport = -> [YZ_Plane002]
  FullyConstrained = true
  MakeInternals = false
  MapMode = 5
  Placement = pos=(0,0,0) rot=(0.57735,0.57735,0.57735;2.0944rad)
  sketch-geometry (4):
    g0: LineSegment StartX=-2.7 StartY=2.7 StartZ=0 EndX=2.7 EndY=2.7 EndZ=0
    g1: LineSegment StartX=2.7 StartY=2.7 StartZ=0 EndX=2.7 EndY=-2.7 EndZ=0
    g2: LineSegment StartX=2.7 StartY=-2.7 StartZ=0 EndX=-2.7 EndY=-2.7 EndZ=0
    g3: LineSegment StartX=-2.7 StartY=-2.7 StartZ=0 EndX=-2.7 EndY=2.7 EndZ=0
  constraints (11):
    c: Horizontal(g0)
    c: Coincident(g1,g0)
    c: Vertical(g1)
    c: Coincident(g2,g1)
    c: Horizontal(g2)
    c: Coincident(g3,g2)
    c: Coincident(g3,g0)
    c: Vertical(g3)
    c: DistanceX(g0,g0) = 5.4
    c: DistanceY(g1,g1) = 5.4
    c: Symmetric(g0,g1,g-1)
FEATURE [Sketcher::SketchObject] Sketch047  label="scavo 10x10 neopixel corpo"
  ArcFitTolerance = 1e-06
  AttachmentOffset = pos=(0,0,1) rot=(0,0,1;0rad)
  AttachmentSupport = -> [YZ_Plane002]
  FullyConstrained = true
  MakeInternals = false
  MapMode = 5
  Placement = pos=(1,0,0) rot=(0.57735,0.57735,0.57735;2.0944rad)
  sketch-geometry (4):
    g0: LineSegment StartX=-5 StartY=5.1 StartZ=0 EndX=5 EndY=5.1 EndZ=0
    g1: LineSegment StartX=5 StartY=5.1 StartZ=0 EndX=5 EndY=-5.1 EndZ=0
    g2: LineSegment StartX=5 StartY=-5.1 StartZ=0 EndX=-5 EndY=-5.1 EndZ=0
    g3: LineSegment StartX=-5 StartY=-5.1 StartZ=0 EndX=-5 EndY=5.1 EndZ=0
  constraints (11):
    c: Horizontal(g0)
    c: Coincident(g1,g0)
    c: Vertical(g1)
    c: Coincident(g2,g1)
    c: Horizontal(g2)
    c: Coincident(g3,g2)
    c: Coincident(g3,g0)
    c: Vertical(g3)
    c: DistanceX(g0,g0) = 10
    c: DistanceY(g1,g1) = 10.2
    c: Symmetric(g0,g2,g-1)
FEATURE [Sketcher::SketchObject] Sketch048  label="buco per perno blocco neopixel"
  ArcFitTolerance = 1e-06
  AttachmentSupport = -> [XZ_Plane002]
  FullyConstrained = true
  MakeInternals = false
  MapMode = 5
  Placement = pos=(0,0,0) rot=(1,0,0;1.5708rad)
  sketch-geometry (4):
    g0: LineSegment StartX=3 StartY=1.2 StartZ=0 EndX=3 EndY=-1.2 EndZ=0
    g1: LineSegment StartX=3 StartY=-1.2 StartZ=0 EndX=5.4 EndY=-1.2 EndZ=0
    g2: LineSegment StartX=5.4 StartY=-1.2 StartZ=0 EndX=5.4 EndY=1.2 EndZ=0
    g3: LineSegment StartX=5.4 StartY=1.2 StartZ=0 EndX=3 EndY=1.2 EndZ=0
  constraints (11):
    c: Coincident(g1,g0)
    c: Horizontal(g1)
    c: Coincident(g2,g1)
    c: Vertical(g2)
    c: Coincident(g3,g2)
    c: Coincident(g3,g0)
    c: Horizontal(g3)
    c: DistanceX(g1,g1) = 2.4
    c: DistanceY(g2,g2) = 2.4
    c: Symmetric(g0,g0,g-1)
    c: DistanceX(g-1,g0) = 3
FEATURE [Sketcher::SketchObject] Sketch045  label="blocco principale per neopixel"
  ArcFitTolerance = 1e-06
  AttachmentSupport = -> [XZ_Plane002]
  ExternalGeometry = -> [Sketch048]
  FullyConstrained = true
  MakeInternals = false
  MapMode = 5
  Placement = pos=(0,0,0) rot=(1,0,0;1.5708rad)
  sketch-geometry (6):
    g0: LineSegment StartX=0 StartY=5.1 StartZ=0 EndX=0 EndY=-5.1 EndZ=0
    g1: LineSegment StartX=0 StartY=-5.1 StartZ=0 EndX=3 EndY=-5.1 EndZ=0
    g2: LineSegment StartX=7 StartY=-1.1 StartZ=0 EndX=7 EndY=5.1 EndZ=0
    g3: LineSegment StartX=7 StartY=5.1 StartZ=0 EndX=0 EndY=5.1 EndZ=0
    g4: ArcOfCircle CenterX=3 CenterY=-1.1 CenterZ=0 NormalX=0 NormalY=0 NormalZ=1 AngleXU=0 Radius=4 StartAngle=4.71239 EndAngle=6.28319
    g5: GeomPoint [constr] X=7 Y=-5.1 Z=0
  constraints (15):
    c: Vertical(g0)
    c: Coincident(g1,g0)
    c: Horizontal(g1)
    c: Vertical(g2)
    c: Coincident(g3,g2)
    c: Coincident(g3,g0)
    c: Horizontal(g3)
    c: DistanceY(g0,g0) = 10.2
    c: Symmetric(g0,g0,g-1)
    c: DistanceX(g3,g3) = 7
    c: PointOnObject(g5,g2)
    c: PointOnObject(g5,g1)
    c: Tangent(g2,g4) = -1.5708
    c: Tangent(g1,g4) = -1.5708
    c: DistanceX(g-3,g1) = 0
FEATURE [Sketcher::SketchObject] Sketch049  label="rinforzi esterni per corpo neopoixel"
  ArcFitTolerance = 1e-06
  AttachmentSupport = -> [XZ_Plane002]
  ExternalGeometry = -> [Sketch045]
  FullyConstrained = true
  MakeInternals = false
  MapMode = 5
  Placement = pos=(0,0,0) rot=(1,0,0;1.5708rad)
  sketch-geometry (8):
    g0: LineSegment StartX=1 StartY=-4.1 StartZ=0 EndX=2 EndY=-4.1 EndZ=0
    g1: LineSegment StartX=2 StartY=-4.1 StartZ=0 EndX=2 EndY=-5.1 EndZ=0
    g2: LineSegment StartX=2 StartY=-5.1 StartZ=0 EndX=1 EndY=-5.1 EndZ=0
    g3: LineSegment StartX=1 StartY=-5.1 StartZ=0 EndX=1 EndY=-4.1 EndZ=0
    g4: LineSegment StartX=1 StartY=5.1 StartZ=0 EndX=2 EndY=5.1 EndZ=0
    g5: LineSegment StartX=2 StartY=5.1 StartZ=0 EndX=2 EndY=4.1 EndZ=0
    g6: LineSegment StartX=2 StartY=4.1 StartZ=0 EndX=1 EndY=4.1 EndZ=0
    g7: LineSegment StartX=1 StartY=4.1 StartZ=0 EndX=1 EndY=5.1 EndZ=0
  constraints (24):
    c: Horizontal(g0)
    c: Coincident(g1,g0)
    c: Vertical(g1)
    c: Coincident(g2,g1)
    c: Horizontal(g2)
    c: Coincident(g3,g2)
    c: Coincident(g3,g0)
    c: Vertical(g3)
    c: Horizontal(g4)
    c: Coincident(g5,g4)
    c: Vertical(g5)
    c: Coincident(g6,g5)
    c: Horizontal(g6)
    c: Coincident(g7,g6)
    c: Coincident(g7,g4)
    c: Vertical(g7)
    c: DistanceX(g4,g4) = 1
    c: DistanceY(g5,g5) = 1
    c: DistanceX(g0,g0) = 1
    c: DistanceY(g1,g1) = 1
    c: DistanceX(g-3,g4) = 1
    c: DistanceY(g-3,g4) = 0
    c: DistanceX(g-4,g2) = 1
    c: DistanceY(g2,g-4) = 0
FEATURE [Sketcher::SketchObject] Sketch052  label="scavo saldature driver solenoide"
  ArcFitTolerance = 1e-06
  AttachmentSupport = -> [XZ_Plane]
  ExternalGeometry = -> [Sketch038]
  FullyConstrained = true
  MakeInternals = false
  MapMode = 5
  Placement = pos=(0,0,0) rot=(1,0,0;1.5708rad)
  sketch-geometry (4):
    g0: LineSegment StartX=-195.304 StartY=-6.5806 StartZ=0 EndX=-196.994 EndY=-10.2058 EndZ=0
    g1: LineSegment StartX=-196.994 StartY=-10.2058 StartZ=0 EndX=-196.632 EndY=-10.3749 EndZ=0
    g2: LineSegment StartX=-196.632 StartY=-10.3749 StartZ=0 EndX=-194.941 EndY=-6.74965 EndZ=0
    g3: LineSegment StartX=-194.941 StartY=-6.74965 StartZ=0 EndX=-195.304 EndY=-6.5806 EndZ=0
  constraints (11):
    c: Coincident(g1,g0)
    c: Coincident(g2,g1)
    c: Coincident(g3,g2)
    c: Coincident(g3,g0)
    c: Parallel(g2,g0)
    c: Perpendicular(g2,g3)
    c: Perpendicular(g1,g2,g1) = 1.5708
    c: Parallel(g2,g-3)
    c: Distance(g2) = 4
    c: Distance(g3) = 0.4
    c: Coincident(g2,g-3)
FEATURE [Part::Extrusion] Extrude055  label="Extrude scavo saldature driver solenoide"
  Base = -> Sketch052
  Dir = (0,-1,2e-16)
  DirMode = 2
  FaceMakerClass = Part::FaceMakerBullseye
  FaceMakerMode = 3
  LengthFwd = 6
  LengthRev = 0
  Solid = true
  Symmetric = true
FEATURE [Sketcher::SketchObject] Sketch053  label="scavo saldature rumble"
  ArcFitTolerance = 1e-06
  AttachmentSupport = -> [XZ_Plane]
  ExternalGeometry = -> [Sketch019]
  FullyConstrained = true
  MakeInternals = false
  MapMode = 5
  Placement = pos=(0,0,0) rot=(1,0,0;1.5708rad)
  sketch-geometry (4):
    g0: LineSegment StartX=-164.507 StartY=-41.6446 StartZ=0 EndX=-165.743 EndY=-45.4488 EndZ=0
    g1: LineSegment StartX=-165.743 StartY=-45.4488 StartZ=0 EndX=-164.602 EndY=-45.8196 EndZ=0
    g2: LineSegment StartX=-164.602 StartY=-45.8196 StartZ=0 EndX=-163.366 EndY=-42.0154 EndZ=0
    g3: LineSegment StartX=-163.366 StartY=-42.0154 StartZ=0 EndX=-164.507 EndY=-41.6446 EndZ=0
  constraints (11):
    c: Coincident(g1,g0)
    c: Coincident(g2,g1)
    c: Coincident(g3,g2)
    c: Coincident(g3,g0)
    c: Parallel(g0,g2)
    c: Perpendicular(g3,g0)
    c: Perpendicular(g1,g0)
    c: Parallel(g0,g-3)
    c: Distance(g0) = 4
    c: Distance(g1) = 1.2
    c: Coincident(g0,g-3)
FEATURE [Part::Extrusion] Extrude056  label="Extrude scavo saldature rumble"
  Base = -> Sketch053
  Dir = (0,-1,2e-16)
  DirMode = 2
  FaceMakerClass = Part::FaceMakerBullseye
  FaceMakerMode = 3
  LengthFwd = 8.4
  LengthRev = 0
  Solid = true
  Symmetric = true
FEATURE [Sketcher::SketchObject] Sketch054  label="scavo saldature alimentatore connettore USB"
  ArcFitTolerance = 1e-06
  AttachmentSupport = -> [XZ_Plane]
  ExternalGeometry = -> [Sketch037]
  FullyConstrained = true
  MakeInternals = false
  MapMode = 5
  Placement = pos=(0,0,0) rot=(1,0,0;1.5708rad)
  sketch-geometry (4):
    g0: LineSegment StartX=-209.575 StartY=-80.4316 StartZ=0 EndX=-210.375 EndY=-80.4316 EndZ=0
    g1: LineSegment StartX=-210.375 StartY=-80.4316 StartZ=0 EndX=-210.375 EndY=-72.4316 EndZ=0
    g2: LineSegment StartX=-210.375 StartY=-72.4316 StartZ=0 EndX=-209.575 EndY=-72.4316 EndZ=0
    g3: LineSegment StartX=-209.575 StartY=-72.4316 StartZ=0 EndX=-209.575 EndY=-80.4316 EndZ=0
  constraints (11):
    c: Horizontal(g0)
    c: Coincident(g1,g0)
    c: Vertical(g1)
    c: Coincident(g2,g1)
    c: Horizontal(g2)
    c: Coincident(g3,g2)
    c: Coincident(g3,g0)
    c: Vertical(g3)
    c: DistanceX(g0,g0) = 0.8
    c: DistanceY(g3,g3) = 8
    c: Coincident(g0,g-4)
FEATURE [Part::Extrusion] Extrude057  label="Extrude scavo saldature alimentatore connettore USB"
  Base = -> Sketch054
  Dir = (0,-1,2e-16)
  DirMode = 2
  FaceMakerClass = Part::FaceMakerBullseye
  FaceMakerMode = 3
  LengthFwd = 11
  LengthRev = 0
  Solid = true
  Symmetric = true
FEATURE [Sketcher::SketchObject] Sketch055  label="buco interno per micro switch"
  ArcFitTolerance = 1e-06
  AttachmentSupport = -> [XZ_Plane]
  ExternalGeometry = -> [Sketch]
  FullyConstrained = true
  MakeInternals = false
  MapMode = 5
  Placement = pos=(0,0,0) rot=(1,0,0;1.5708rad)
  sketch-geometry (11):
    g0: LineSegment [constr] StartX=-194.483 StartY=34.2854 StartZ=0 EndX=-196.022 EndY=30.0568 EndZ=0
    g1: LineSegment [constr] StartX=-196.022 StartY=30.0568 StartZ=0 EndX=-197.561 EndY=25.8282 EndZ=0
    g2: LineSegment [constr] StartX=-196.022 StartY=30.0568 StartZ=0 EndX=-194.143 EndY=29.3727 EndZ=0
    g3: LineSegment [constr] StartX=-196.022 StartY=30.0568 StartZ=0 EndX=-197.902 EndY=30.7408 EndZ=0
    g4: LineSegment StartX=-196.362 StartY=34.9694 StartZ=0 EndX=-192.604 EndY=33.6014 EndZ=0
    g5: LineSegment StartX=-199.441 StartY=26.5122 StartZ=0 EndX=-195.682 EndY=25.1441 EndZ=0
    g6: LineSegment StartX=-192.604 StartY=33.6014 StartZ=0 EndX=-195.682 EndY=25.1441 EndZ=0
    g7: LineSegment StartX=-196.362 StartY=34.9694 StartZ=0 EndX=-199.441 EndY=26.5122 EndZ=0
    g8: GeomPoint [constr] X=-187.821 Y=29.2 Z=0
    g9: LineSegment [constr] StartX=-188.505 StartY=27.3206 StartZ=0 EndX=-196.022 EndY=30.0568 EndZ=0
    g10: LineSegment [constr] StartX=-187.821 StartY=29.2 StartZ=0 EndX=-188.505 EndY=27.3206 EndZ=0
  constraints (27):
    c: Coincident(g2,g0)
    c: Parallel(g0,g-3)
    c: Tangent(g1,g0) = -1.5708
    c: Perpendicular(g0,g2)
    c: Tangent(g2,g3)
    c: Distance(g0,g1) = 9
    c: Equal(g0,g1)
    c: Distance(g3,g2) = 4
    c: Equal(g2,g3)
    c: Parallel(g3,g4)
    c: Symmetric(g4,g4,g0)
    c: Parallel(g6,g1)
    c: Parallel(g7,g1)
    c: Symmetric(g6,g6,g2)
    c: Symmetric(g5,g5,g1)
    c: Symmetric(g7,g7,g3)
    c: Coincident(g7,g4)
    c: Coincident(g6,g4)
    c: Coincident(g5,g6)
    c: Symmetric(g-3,g-3,g8)
    c: Perpendicular(g-3,g9)
    c: Distance(g9) = 8
    c: Coincident(g3,g9)
    c: Coincident(g10,g8)
    c: Parallel(g10,g-3)
    c: Distance(g10) = 2
    c: Coincident(g10,g9)
FEATURE [Sketcher::SketchObject] Sketch056  label="buco esterno per micro switch"
  ArcFitTolerance = 1e-06
  AttachmentSupport = -> [XZ_Plane]
  ExternalGeometry = -> [Sketch055]
  FullyConstrained = true
  MakeInternals = false
  MapMode = 5
  Placement = pos=(0,0,0) rot=(1,0,0;1.5708rad)
  sketch-geometry (17):
    g0: GeomPoint [constr] X=-194.143 Y=29.3727 Z=0
    g1: GeomPoint [constr] X=-194.483 Y=34.2854 Z=0
    g2: GeomPoint [constr] X=-197.902 Y=30.7408 Z=0
    g3: GeomPoint [constr] X=-197.561 Y=25.8282 Z=0
    g4: GeomPoint [constr] X=-196.022 Y=30.0568 Z=0
    g5: LineSegment [constr] StartX=-194.483 StartY=34.2854 StartZ=0 EndX=-196.022 EndY=30.0568 EndZ=0
    g6: LineSegment [constr] StartX=-196.022 StartY=30.0568 StartZ=0 EndX=-197.561 EndY=25.8282 EndZ=0
    g7: LineSegment [constr] StartX=-197.902 StartY=30.7408 StartZ=0 EndX=-196.022 EndY=30.0568 EndZ=0
    g8: LineSegment [constr] StartX=-196.022 StartY=30.0568 StartZ=0 EndX=-194.143 EndY=29.3727 EndZ=0
    g9: LineSegment [constr] StartX=-195.338 StartY=31.9362 StartZ=0 EndX=-196.022 EndY=30.0568 EndZ=0
    g10: LineSegment [constr] StartX=-196.022 StartY=30.0568 StartZ=0 EndX=-196.706 EndY=28.1774 EndZ=0
    g11: LineSegment [constr] StartX=-196.022 StartY=30.0568 StartZ=0 EndX=-196.821 EndY=30.3475 EndZ=0
    g12: LineSegment [constr] StartX=-196.022 StartY=30.0568 StartZ=0 EndX=-195.223 EndY=29.7661 EndZ=0
    g13: LineSegment StartX=-194.539 StartY=31.6454 StartZ=0 EndX=-195.907 EndY=27.8867 EndZ=0
    g14: LineSegment StartX=-196.137 StartY=32.2269 StartZ=0 EndX=-197.505 EndY=28.4681 EndZ=0
    g15: LineSegment StartX=-196.137 StartY=32.2269 StartZ=0 EndX=-194.539 EndY=31.6454 EndZ=0
    g16: LineSegment StartX=-197.505 StartY=28.4681 StartZ=0 EndX=-195.907 EndY=27.8867 EndZ=0
  constraints (34):
    c: Symmetric(g-5,g-5,g1)
    c: Symmetric(g-5,g-6,g0)
    c: Symmetric(g-6,g-6,g3)
    c: Symmetric(g-5,g-6,g2)
    c: Coincident(g5,g1)
    c: Coincident(g5,g4)
    c: Coincident(g6,g4)
    c: Coincident(g6,g3)
    c: Equal(g5,g6)
    c: Coincident(g7,g2)
    c: Coincident(g7,g4)
    c: Coincident(g8,g4)
    c: Coincident(g8,g0)
    c: Equal(g7,g8)
    c: Coincident(g11,g9)
    c: Coincident(g12,g9)
    c: Tangent(g10,g9) = -1.5708
    c: Perpendicular(g11,g9)
    c: Parallel(g9,g-4)
    c: Equal(g9,g10)
    c: Parallel(g12,g11)
    c: Equal(g11,g12)
    c: Distance(g11,g12) = 1.7
    c: Distance(g9,g10) = 4
    c: Symmetric(g13,g13,g12)
    c: Parallel(g13,g9)
    c: Symmetric(g14,g14,g11)
    c: Symmetric(g15,g15,g9)
    c: Parallel(g15,g11)
    c: Symmetric(g16,g16,g10)
    c: Coincident(g16,g14)
    c: Coincident(g15,g14)
    c: Coincident(g13,g15)
    c: Coincident(g9,g4)
FEATURE [Sketcher::SketchObject] Sketch057  label="buco interno per SWITCH"
  ArcFitTolerance = 1e-06
  AttachmentSupport = -> [XZ_Plane]
  ExternalGeometry = -> [Sketch]
  FullyConstrained = true
  MakeInternals = false
  MapMode = 5
  Placement = pos=(0,0,0) rot=(1,0,0;1.5708rad)
  sketch-geometry (10):
    g0: GeomPoint [constr] X=-187.821 Y=29.2 Z=0
    g1: LineSegment [constr] StartX=-188.505 StartY=27.3206 StartZ=0 EndX=-193.203 EndY=29.0307 EndZ=0
    g2: LineSegment [constr] StartX=-190.809 StartY=35.6086 StartZ=0 EndX=-195.597 EndY=22.4529 EndZ=0
    g3: GeomPoint [constr] X=-193.203 Y=29.0307 Z=0
    g4: LineSegment [constr] StartX=-196.492 StartY=30.2278 StartZ=0 EndX=-189.914 EndY=27.8336 EndZ=0
    g5: LineSegment StartX=-194.098 StartY=36.8056 StartZ=0 EndX=-187.52 EndY=34.4115 EndZ=0
    g6: LineSegment StartX=-194.098 StartY=36.8056 StartZ=0 EndX=-198.886 EndY=23.6499 EndZ=0
    g7: LineSegment StartX=-187.52 StartY=34.4115 StartZ=0 EndX=-192.308 EndY=21.2558 EndZ=0
    g8: LineSegment StartX=-198.886 StartY=23.6499 StartZ=0 EndX=-192.308 EndY=21.2558 EndZ=0
    g9: LineSegment [constr] StartX=-187.821 StartY=29.2 StartZ=0 EndX=-188.505 EndY=27.3206 EndZ=0
  constraints (23):
    c: Symmetric(g-3,g-3,g0)
    c: Perpendicular(g1,g-3)
    c: Parallel(g2,g-3)
    c: Symmetric(g2,g2,g3)
    c: Perpendicular(g2,g4)
    c: Symmetric(g4,g4,g3)
    c: Distance(g2) = 14
    c: Distance(g4) = 7
    c: Distance(g1) = 5
    c: Parallel(g5,g4)
    c: Parallel(g7,g2)
    c: Symmetric(g5,g5,g2)
    c: Symmetric(g6,g6,g4)
    c: Symmetric(g7,g7,g4)
    c: Symmetric(g8,g8,g2)
    c: Coincident(g6,g5)
    c: Coincident(g7,g5)
    c: Coincident(g8,g7)
    c: Coincident(g3,g1)
    c: Coincident(g9,g0)
    c: Parallel(g9,g-3)
    c: Distance(g9) = 2
    c: Coincident(g1,g9)
FEATURE [Sketcher::SketchObject] Sketch058  label="buco esterno per SWITCH"
  ArcFitTolerance = 1e-06
  AttachmentSupport = -> [XZ_Plane]
  ExternalGeometry = -> [Sketch057]
  FullyConstrained = true
  MakeInternals = false
  MapMode = 5
  Placement = pos=(0,0,0) rot=(1,0,0;1.5708rad)
  sketch-geometry (12):
    g0: GeomPoint [constr] X=-190.809 Y=35.6086 Z=0
    g1: GeomPoint [constr] X=-196.492 Y=30.2278 Z=0
    g2: GeomPoint [constr] X=-189.914 Y=27.8336 Z=0
    g3: GeomPoint [constr] X=-195.597 Y=22.4529 Z=0
    g4: GeomPoint [constr] X=-193.203 Y=29.0307 Z=0
    g5: LineSegment [constr] StartX=-192.006 StartY=32.3196 StartZ=0 EndX=-194.4 EndY=25.7418 EndZ=0
    g6: GeomPoint [constr] X=-193.203 Y=29.0307 Z=0
    g7: LineSegment [constr] StartX=-195.082 StartY=29.7148 StartZ=0 EndX=-191.324 EndY=28.3467 EndZ=0
    g8: LineSegment StartX=-193.885 StartY=33.0037 StartZ=0 EndX=-190.127 EndY=31.6356 EndZ=0
    g9: LineSegment StartX=-190.127 StartY=31.6356 StartZ=0 EndX=-192.521 EndY=25.0578 EndZ=0
    g10: LineSegment StartX=-196.28 StartY=26.4258 StartZ=0 EndX=-192.521 EndY=25.0578 EndZ=0
    g11: LineSegment StartX=-193.885 StartY=33.0037 StartZ=0 EndX=-196.28 EndY=26.4258 EndZ=0
  constraints (21):
    c: Symmetric(g-6,g-6,g3)
    c: Symmetric(g-4,g-6,g2)
    c: Symmetric(g-5,g-4,g0)
    c: Symmetric(g-5,g-6,g1)
    c: Symmetric(g1,g2,g4)
    c: Parallel(g5,g-4)
    c: Symmetric(g5,g5,g6)
    c: Perpendicular(g7,g5)
    c: Symmetric(g7,g7,g6)
    c: Distance(g5) = 7
    c: Distance(g7) = 4
    c: Parallel(g8,g7)
    c: Parallel(g11,g5)
    c: Symmetric(g8,g8,g5)
    c: Symmetric(g9,g9,g7)
    c: Symmetric(g10,g10,g5)
    c: Symmetric(g11,g11,g7)
    c: Coincident(g11,g8)
    c: Coincident(g9,g8)
    c: Coincident(g9,g10)
    c: Coincident(g6,g4)
FEATURE [Part::Extrusion] Extrude060  label="Extrude buco interno per SWITCH destro"
  Base = -> Sketch057
  Dir = (0,-1,2e-16)
  DirMode = 2
  FaceMakerClass = Part::FaceMakerBullseye
  FaceMakerMode = 3
  LengthFwd = 13.2
  LengthRev = 0
  Placement = pos=(0,2.6,0) rot=(0,0,1;0rad)
  Solid = true
  Symmetric = false
FEATURE [Part::Extrusion] Extrude061  label="Extrude buco esterno per SWITCH destro"
  Base = -> Sketch058
  Dir = (0,-1,2e-16)
  DirMode = 2
  FaceMakerClass = Part::FaceMakerBullseye
  FaceMakerMode = 3
  LengthFwd = 2
  LengthRev = 0
  Placement = pos=(0,-10.6,0) rot=(0,0,1;0rad)
  Solid = true
  Symmetric = false
FEATURE [Sketcher::SketchObject] Sketch059  label="buco per spazio introduzione SWITCH"
  ArcFitTolerance = 1e-06
  AttachmentSupport = -> [XZ_Plane]
  ExternalGeometry = -> [Sketch057,Sketch010]
  FullyConstrained = true
  MakeInternals = false
  MapMode = 5
  Placement = pos=(0,0,0) rot=(1,0,0;1.5708rad)
  sketch-geometry (8):
    g0: LineSegment [constr] StartX=-201.368 StartY=36.3521 StartZ=0 EndX=-195.094 EndY=34.0687 EndZ=0
    g1: LineSegment [constr] StartX=-194.098 StartY=36.8056 StartZ=0 EndX=-195.094 EndY=34.0687 EndZ=0
    g2: LineSegment StartX=-198.658 StartY=24.2771 StartZ=0 EndX=-199.654 EndY=21.5401 EndZ=0
    g3: LineSegment StartX=-199.654 StartY=21.5401 StartZ=0 EndX=-181.196 EndY=14.822 EndZ=0
    g4: LineSegment StartX=-181.196 StartY=14.822 StartZ=0 EndX=-180.2 EndY=17.559 EndZ=0
    g5: LineSegment StartX=-180.2 StartY=17.559 StartZ=0 EndX=-198.658 EndY=24.2771 EndZ=0
    g6: LineSegment [constr] StartX=-204.932 StartY=26.5605 StartZ=0 EndX=-198.658 EndY=24.2771 EndZ=0
    g7: LineSegment [constr] StartX=-198.658 StartY=24.2771 StartZ=0 EndX=-199.654 EndY=21.5401 EndZ=0
  constraints (20):
    c: Parallel(g1,g-3)
    c: Parallel(g0,g-4)
    c: Coincident(g0,g-4)
    c: Coincident(g1,g-3)
    c: Coincident(g0,g1)
    c: Coincident(g3,g2)
    c: Coincident(g4,g3)
    c: Coincident(g5,g4)
    c: Coincident(g5,g2)
    c: Parallel(g5,g-5)
    c: Parallel(g3,g-5)
    c: Parallel(g4,g-6)
    c: DistanceX(g-6,g4) = 0
    c: Coincident(g6,g-5)
    c: Equal(g6,g0)
    c: Coincident(g7,g6)
    c: Equal(g7,g1)
    c: Tangent(g7,g-3)
    c: Coincident(g2,g6)
    c: Coincident(g2,g7)
FEATURE [Part::Extrusion] Extrude062  label="Extrude buco per spazio introduzione SWITCH"
  Base = -> Sketch059
  Dir = (0,-1,2e-16)
  DirMode = 2
  FaceMakerClass = Part::FaceMakerBullseye
  FaceMakerMode = 3
  LengthFwd = 13.2
  LengthRev = 0
  Solid = true
  Symmetric = true
FEATURE [Part::Extrusion] Extrude063  label="Extrude buco interno per SWITCH sinistro"
  Base = -> Sketch057
  Dir = (0,-1,2e-16)
  DirMode = 2
  FaceMakerClass = Part::FaceMakerBullseye
  FaceMakerMode = 3
  LengthFwd = 13.2
  LengthRev = 0
  Placement = pos=(0,10.6,0) rot=(0,0,1;0rad)
  Solid = true
  Symmetric = false
FEATURE [Part::Extrusion] Extrude064  label="Extrude buco esterno per SWITCH sinistro"
  Base = -> Sketch058
  Dir = (0,-1,2e-16)
  DirMode = 2
  FaceMakerClass = Part::FaceMakerBullseye
  FaceMakerMode = 3
  LengthFwd = 2
  LengthRev = 0
  Placement = pos=(0,12.6,0) rot=(0,0,1;0rad)
  Solid = true
  Symmetric = false
FEATURE [Sketcher::SketchObject] Sketch061  label="struttura esterna blocco switch"
  ArcFitTolerance = 1e-06
  AttachmentSupport = -> [XZ_Plane003]
  FullyConstrained = true
  MakeInternals = false
  MapMode = 5
  Placement = pos=(0,0,0) rot=(1,0,0;1.5708rad)
  sketch-geometry (5):
    g0: LineSegment StartX=-1 StartY=-5.1 StartZ=0 EndX=1 EndY=-5.1 EndZ=0
    g1: LineSegment StartX=1 StartY=-5.1 StartZ=0 EndX=1 EndY=5.1 EndZ=0
    g2: LineSegment StartX=1 StartY=5.1 StartZ=0 EndX=-1 EndY=5.1 EndZ=0
    g3: LineSegment StartX=-1 StartY=5.1 StartZ=0 EndX=-1 EndY=-5.1 EndZ=0
    g4: GeomPoint [constr] X=0 Y=0 Z=0
  constraints (12):
    c: Coincident(g0,g1)
    c: Coincident(g1,g2)
    c: Coincident(g2,g3)
    c: Coincident(g3,g0)
    c: Horizontal(g0)
    c: Horizontal(g2)
    c: Vertical(g1)
    c: Vertical(g3)
    c: Symmetric(g2,g0,g4)
    c: Distance(g1,g3) = 2
    c: Distance(g0,g2) = 10.2
    c: Coincident(g4,g-1)
FEATURE [Sketcher::SketchObject] Sketch062  label="struttura interna blocco switch"
  ArcFitTolerance = 1e-06
  AttachmentSupport = -> [XZ_Plane003]
  ExternalGeometry = -> [Sketch061]
  FullyConstrained = true
  MakeInternals = false
  MapMode = 5
  Placement = pos=(0,0,0) rot=(1,0,0;1.5708rad)
  sketch-geometry (5):
    g0: LineSegment StartX=-1 StartY=3.1 StartZ=0 EndX=-1 EndY=-3.1 EndZ=0
    g1: LineSegment StartX=-1 StartY=-3.1 StartZ=0 EndX=1 EndY=-3.1 EndZ=0
    g2: LineSegment StartX=1 StartY=-3.1 StartZ=0 EndX=1 EndY=3.1 EndZ=0
    g3: LineSegment StartX=1 StartY=3.1 StartZ=0 EndX=-1 EndY=3.1 EndZ=0
    g4: GeomPoint [constr] X=0 Y=0 Z=0
  constraints (12):
    c: Coincident(g0,g1)
    c: Coincident(g1,g2)
    c: Coincident(g2,g3)
    c: Coincident(g3,g0)
    c: Vertical(g0)
    c: Vertical(g2)
    c: Horizontal(g1)
    c: Horizontal(g3)
    c: Symmetric(g2,g0,g4)
    c: Coincident(g4,g-1)
    c: Distance(g0) = 6.2
    c: Equal(g3,g-3)
FEATURE [Sketcher::SketchObject] Sketch063  label="blocchi tra switch"
  ArcFitTolerance = 1e-06
  AttachmentSupport = -> [XZ_Plane003]
  ExternalGeometry = -> [Sketch061,Sketch062]
  FullyConstrained = true
  MakeInternals = false
  MapMode = 5
  Placement = pos=(0,0,0) rot=(1,0,0;1.5708rad)
  sketch-geometry (8):
    g0: LineSegment StartX=-3 StartY=5.1 StartZ=0 EndX=-1 EndY=5.1 EndZ=0
    g1: LineSegment StartX=-1 StartY=5.1 StartZ=0 EndX=-1 EndY=3.1 EndZ=0
    g2: LineSegment StartX=-1 StartY=3.1 StartZ=0 EndX=-3 EndY=3.1 EndZ=0
    g3: LineSegment StartX=-3 StartY=3.1 StartZ=0 EndX=-3 EndY=5.1 EndZ=0
    g4: LineSegment StartX=-3 StartY=-3.1 StartZ=0 EndX=-1 EndY=-3.1 EndZ=0
    g5: LineSegment StartX=-1 StartY=-3.1 StartZ=0 EndX=-1 EndY=-5.1 EndZ=0
    g6: LineSegment StartX=-1 StartY=-5.1 StartZ=0 EndX=-3 EndY=-5.1 EndZ=0
    g7: LineSegment StartX=-3 StartY=-5.1 StartZ=0 EndX=-3 EndY=-3.1 EndZ=0
  constraints (20):
    c: Horizontal(g0)
    c: Coincident(g1,g0)
    c: Coincident(g2,g1)
    c: Horizontal(g2)
    c: Coincident(g3,g2)
    c: Coincident(g3,g0)
    c: Vertical(g3)
    c: Horizontal(g4)
    c: Coincident(g5,g4)
    c: Coincident(g6,g5)
    c: Horizontal(g6)
    c: Coincident(g7,g6)
    c: Coincident(g7,g4)
    c: Vertical(g7)
    c: Coincident(g0,g-4)
    c: Coincident(g1,g-5)
    c: Coincident(g4,g-6)
    c: Coincident(g5,g-7)
    c: Distance(g0) = 2
    c: Distance(g4) = 2
FEATURE [Sketcher::SketchObject] Sketch066  label="piano per rampino"
  ArcFitTolerance = 1e-06
  AttachmentSupport = -> [XZ_Plane002]
  ExternalGeometry = -> [Sketch045]
  FullyConstrained = true
  MakeInternals = false
  MapMode = 5
  Placement = pos=(0,0,0) rot=(1,0,0;1.5708rad)
  sketch-geometry (4):
    g0: LineSegment StartX=5.4 StartY=5.1 StartZ=0 EndX=5.4 EndY=3.9 EndZ=0
    g1: LineSegment StartX=5.4 StartY=3.9 StartZ=0 EndX=7 EndY=3.9 EndZ=0
    g2: LineSegment StartX=7 StartY=3.9 StartZ=0 EndX=7 EndY=5.1 EndZ=0
    g3: LineSegment StartX=7 StartY=5.1 StartZ=0 EndX=5.4 EndY=5.1 EndZ=0
  constraints (11):
    c: Coincident(g0,g1)
    c: Coincident(g1,g2)
    c: Coincident(g2,g3)
    c: Coincident(g3,g0)
    c: Vertical(g0)
    c: Vertical(g2)
    c: Horizontal(g1)
    c: Horizontal(g3)
    c: Distance(g0,g2) = 1.6
    c: Distance(g1,g3) = 1.2
    c: Coincident(g2,g-3)
FEATURE [Sketcher::SketchObject] Sketch064  label="rampini_per_serraggio_struttura"
  ArcFitTolerance = 1e-06
  AttachmentSupport = -> [XZ_Plane002]
  ExternalGeometry = -> [Sketch066,Sketch045]
  FullyConstrained = true
  MakeInternals = false
  MapMode = 5
  Placement = pos=(0,0,0) rot=(1,0,0;1.5708rad)
  sketch-geometry (7):
    g0: LineSegment StartX=7 StartY=5.1 StartZ=0 EndX=7 EndY=3.9 EndZ=0
    g1: LineSegment StartX=7 StartY=3.9 StartZ=0 EndX=9 EndY=3.9 EndZ=0
    g2: LineSegment StartX=7 StartY=5.1 StartZ=0 EndX=7 EndY=5.1 EndZ=0
    g3: LineSegment StartX=7 StartY=5.1 StartZ=0 EndX=7 EndY=7.5 EndZ=0
    g4: LineSegment StartX=9 StartY=5.1 StartZ=0 EndX=9 EndY=3.9 EndZ=0
    g5: LineSegment StartX=7 StartY=7.5 StartZ=0 EndX=9 EndY=7.5 EndZ=0
    g6: LineSegment StartX=9 StartY=7.5 StartZ=0 EndX=9 EndY=5.1 EndZ=0
  constraints (20):
    c: Vertical(g0)
    c: Coincident(g1,g0)
    c: Horizontal(g1)
    c: Coincident(g2,g0)
    c: Horizontal(g2)
    c: Coincident(g3,g2)
    c: Vertical(g3)
    c: Coincident(g5,g3)
    c: Coincident(g4,g6)
    c: Coincident(g4,g1)
    c: Vertical(g4)
    c: Coincident(g0,g-3)
    c: DistanceY(g-4,g3) = 2.4
    c: DistanceX(g1,g1) = 2
    c: DistanceY(g2,g6) = 0
    c: DistanceX(g2,g2) = 0
    c: DistanceY(g0,g0) = 1.2
    c: Coincident(g5,g6)
    c: Horizontal(g5)
    c: Vertical(g6)
FEATURE [Sketcher::SketchObject] Sketch067  label="perno per blocco switch"
  ArcFitTolerance = 1e-06
  AttachmentSupport = -> [XZ_Plane]
  ExternalGeometry = -> [Sketch,Sketch010]
  FullyConstrained = true
  MakeInternals = false
  MapMode = 5
  Placement = pos=(0,0,0) rot=(1,0,0;1.5708rad)
  sketch-geometry (14):
    g0: LineSegment StartX=-191.073 StartY=24.9429 StartZ=0 EndX=-185.81 EndY=23.0276 EndZ=0
    g1: LineSegment StartX=-183.76 StartY=23.9839 StartZ=0 EndX=-182.392 EndY=27.7427 EndZ=0
    g2: LineSegment StartX=-183.348 StartY=29.7934 StartZ=0 EndX=-188.61 EndY=31.7087 EndZ=0
    g3: LineSegment StartX=-188.61 StartY=31.7087 StartZ=0 EndX=-191.073 EndY=24.9429 EndZ=0
    g4: GeomPoint [constr] X=-186.459 Y=27.0946 Z=0
    g5: LineSegment StartX=-189.022 StartY=25.8992 StartZ=0 EndX=-185.263 EndY=24.5311 EndZ=0
    g6: LineSegment StartX=-185.263 StartY=24.5311 StartZ=0 EndX=-183.895 EndY=28.2899 EndZ=0
    g7: LineSegment StartX=-183.895 StartY=28.2899 StartZ=0 EndX=-187.654 EndY=29.658 EndZ=0
    g8: LineSegment StartX=-187.654 StartY=29.658 StartZ=0 EndX=-189.022 EndY=25.8992 EndZ=0
    g9: GeomPoint [constr] X=-186.459 Y=27.0946 Z=0
    g10: ArcOfCircle CenterX=-185.263 CenterY=24.5311 CenterZ=0 NormalX=0 NormalY=0 NormalZ=1 AngleXU=0 Radius=1.6 StartAngle=4.36332 EndAngle=5.93412
    g11: GeomPoint [constr] X=-184.307 Y=22.4804 Z=0
    g12: ArcOfCircle CenterX=-183.895 CenterY=28.2899 CenterZ=0 NormalX=0 NormalY=0 NormalZ=1 AngleXU=0 Radius=1.6 StartAngle=5.93412 EndAngle=7.50492
    g13: GeomPoint [constr] X=-181.844 Y=29.2462 Z=0
  constraints (30):
    c: Coincident(g2,g3)
    c: Coincident(g3,g0)
    c: Symmetric(g13,g0,g4)
    c: Distance(g11,g3) = 7.2
    c: Distance(g0,g2) = 7.2
    c: Parallel(g3,g1)
    c: Parallel(g2,g0)
    c: Perpendicular(g2,g3)
    c: Coincident(g5,g6)
    c: Coincident(g6,g7)
    c: Coincident(g7,g8)
    c: Coincident(g8,g5)
    c: Symmetric(g7,g5,g9)
    c: Distance(g6,g8) = 4
    c: Distance(g5,g7) = 4
    c: Coincident(g9,g4)
    c: Parallel(g8,g6)
    c: Parallel(g7,g5)
    c: Perpendicular(g7,g8)
    c: Tangent(g8,g-3)
    c: Tangent(g2,g-4)
    c: PointOnObject(g11,g1)
    c: PointOnObject(g11,g0)
    c: Tangent(g1,g10) = -1.5708
    c: Tangent(g0,g10) = -1.5708
    c: PointOnObject(g13,g1)
    c: Tangent(g1,g12) = -1.5708
    c: Tangent(g2,g12) = -1.5708
    c: Equal(g10,g12)
    c: Coincident(g10,g5)
FEATURE [Part::Extrusion] Extrude072  label="Extrude perno per blocco switch"
  Base = -> Sketch067
  Dir = (0,-1,2e-16)
  DirMode = 2
  FaceMakerClass = Part::FaceMakerBullseye
  FaceMakerMode = 3
  LengthFwd = 25.2
  LengthRev = 0
  Solid = true
  Symmetric = true
FEATURE [Part::MultiFuse] Fusion
  Refine = true
  Shapes = -> [Extrude,Sweep,Extrude007,Extrude011,Extrude005,Extrude012,Extrude013,Extrude016,Extrude031,Extrude039,Extrude045,Extrude072]
FEATURE [Part::Cut] Cut
  Base = -> Fusion
  Refine = true
  Tool = -> Extrude001
FEATURE [Part::Cut] Cut001
  Base = -> Cut
  Refine = true
  Tool = -> Extrude004
FEATURE [Part::Cut] Cut002
  Base = -> Cut001
  Refine = true
  Tool = -> Extrude006
FEATURE [Part::Cut] Cut003
  Base = -> Cut002
  Refine = true
  Tool = -> Extrude008
FEATURE [Part::Cut] Cut004
  Base = -> Cut003
  Refine = true
  Tool = -> Extrude009
FEATURE [Part::Cut] Cut005
  Base = -> Cut004
  Refine = true
  Tool = -> Extrude010
FEATURE [Part::Cut] Cut006
  Base = -> Cut005
  Refine = true
  Tool = -> Extrude014
FEATURE [Part::Cut] Cut007
  Base = -> Cut006
  Refine = true
  Tool = -> Extrude015
FEATURE [Part::Cut] Cut008
  Base = -> Cut007
  Refine = true
  Tool = -> Extrude018
FEATURE [Part::Cut] Cut009
  Base = -> Cut008
  Refine = true
  Tool = -> Extrude019
FEATURE [Part::Cut] Cut010
  Base = -> Cut009
  Refine = true
  Tool = -> Extrude020
FEATURE [Part::Cut] Cut011
  Base = -> Cut010
  Refine = true
  Tool = -> Extrude021
FEATURE [Part::Cut] Cut012
  Base = -> Cut011
  Refine = true
  Tool = -> Extrude022
FEATURE [Part::Cut] Cut013
  Base = -> Cut012
  Refine = true
  Tool = -> Extrude023
FEATURE [Part::Cut] Cut014
  Base = -> Cut013
  Refine = true
  Tool = -> Extrude032
FEATURE [Part::Cut] Cut015
  Base = -> Cut014
  Refine = true
  Tool = -> Extrude033
FEATURE [Part::Cut] Cut016
  Base = -> Cut015
  Refine = true
  Tool = -> Extrude034
FEATURE [Part::Cut] Cut017
  Base = -> Cut016
  Refine = true
  Tool = -> Extrude035
FEATURE [Part::Cut] Cut018
  Base = -> Cut017
  Refine = true
  Tool = -> Extrude036
FEATURE [Part::Cut] Cut019
  Base = -> Cut018
  Refine = true
  Tool = -> Extrude037
FEATURE [Part::Cut] Cut020
  Base = -> Cut019
  Refine = true
  Tool = -> Extrude030
FEATURE [Part::Cut] Cut022
  Base = -> Cut020
  Refine = true
  Tool = -> Extrude038
FEATURE [Part::Cut] Cut023
  Base = -> Cut022
  Refine = true
  Tool = -> Extrude041
FEATURE [Part::Cut] Cut024
  Base = -> Cut023
  Refine = true
  Tool = -> Extrude040
FEATURE [Part::Cut] Cut025
  Base = -> Cut024
  Refine = true
  Tool = -> Extrude042
FEATURE [Part::Cut] Cut026
  Base = -> Cut025
  Refine = true
  Tool = -> Extrude043
FEATURE [Part::Cut] Cut027
  Base = -> Cut026
  Refine = true
  Tool = -> Extrude044
FEATURE [Part::Cut] Cut028
  Base = -> Cut027
  Refine = true
  Tool = -> Extrude046
FEATURE [Part::Cut] Cut029
  Base = -> Cut028
  Refine = true
  Tool = -> Extrude047
FEATURE [Part::Cut] Cut033
  Base = -> Cut029
  Refine = true
  Tool = -> Extrude055
FEATURE [Part::Cut] Cut034
  Base = -> Cut033
  Refine = true
  Tool = -> Extrude056
FEATURE [Part::Cut] Cut035
  Base = -> Cut034
  Refine = true
  Tool = -> Extrude057
FEATURE [Part::Cut] Cut037
  Base = -> Cut035
  Refine = true
  Tool = -> Extrude060
FEATURE [Part::Cut] Cut038
  Base = -> Cut037
  Refine = true
  Tool = -> Extrude061
FEATURE [Part::Cut] Cut039
  Base = -> Cut038
  Refine = true
  Tool = -> Extrude063
FEATURE [Part::Cut] Cut040
  Base = -> Cut039
  Refine = true
  Tool = -> Extrude064
FEATURE [Part::Cut] Cut041
  Base = -> Cut040
  Refine = true
  Tool = -> Extrude062
FEATURE [Sketcher::SketchObject] Sketch068  label="base con smusso sopra neopixel"
  ArcFitTolerance = 1e-06
  AttachmentSupport = -> [YZ_Plane002]
  FullyConstrained = true
  MakeInternals = false
  MapMode = 5
  Placement = pos=(0,0,0) rot=(0.57735,0.57735,0.57735;2.0944rad)
  sketch-geometry (5):
    g0: LineSegment StartX=-9.5 StartY=-6.1 StartZ=0 EndX=9.5 EndY=-6.1 EndZ=0
    g1: LineSegment StartX=9.5 StartY=-6.1 StartZ=0 EndX=9.5 EndY=6.1 EndZ=0
    g2: LineSegment StartX=9.5 StartY=6.1 StartZ=0 EndX=-9.5 EndY=6.1 EndZ=0
    g3: LineSegment StartX=-9.5 StartY=6.1 StartZ=0 EndX=-9.5 EndY=-6.1 EndZ=0
    g4: GeomPoint [constr] X=0 Y=0 Z=0
  constraints (12):
    c: Coincident(g0,g1)
    c: Coincident(g1,g2)
    c: Coincident(g2,g3)
    c: Coincident(g3,g0)
    c: Horizontal(g0)
    c: Horizontal(g2)
    c: Vertical(g1)
    c: Vertical(g3)
    c: Symmetric(g2,g0,g4)
    c: Distance(g1,g3) = 19
    c: Distance(g0,g2) = 12.2
    c: Coincident(g4,g-1)
FEATURE [Sketcher::SketchObject] Sketch069  label="cilindro minore"
  ArcFitTolerance = 1e-06
  AttachmentSupport = -> [XZ_Plane004]
  FullyConstrained = true
  MakeInternals = false
  MapMode = 5
  Placement = pos=(0,0,0) rot=(1,0,0;1.5708rad)
  sketch-geometry (1):
    g0: Circle CenterX=0 CenterY=0 CenterZ=0 NormalX=0 NormalY=0 NormalZ=1 AngleXU=0 Radius=5.8
  constraints (2):
    c: Diameter(g0) = 11.6
    c: Coincident(g0,g-1)
FEATURE [Sketcher::SketchObject] Sketch070  label="cilindro maggiore"
  ArcFitTolerance = 1e-06
  AttachmentSupport = -> [XZ_Plane004]
  ExternalGeometry = -> [Sketch069]
  FullyConstrained = true
  MakeInternals = false
  MapMode = 5
  Placement = pos=(0,0,0) rot=(1,0,0;1.5708rad)
  sketch-geometry (1):
    g0: Circle CenterX=0 CenterY=0 CenterZ=0 NormalX=0 NormalY=0 NormalZ=1 AngleXU=0 Radius=6.5
  constraints (2):
    c: Coincident(g0,g-1)
    c: Diameter(g0) = 13
FEATURE [Sketcher::SketchObject] Sketch071  label="buco interno"
  ArcFitTolerance = 1e-06
  AttachmentSupport = -> [XZ_Plane004]
  ExternalGeometry = -> [Sketch069]
  FullyConstrained = true
  MakeInternals = false
  MapMode = 5
  Placement = pos=(0,0,0) rot=(1,0,0;1.5708rad)
  sketch-geometry (1):
    g0: Circle CenterX=0 CenterY=0 CenterZ=0 NormalX=0 NormalY=0 NormalZ=1 AngleXU=0 Radius=5
  constraints (2):
    c: Coincident(g0,g-1)
    c: Diameter(g0) = 10
FEATURE [PartDesign::Pad] Pad
  Direction = (0,-1,2e-16)
  Length = 1.2
  Length2 = 10
  Placement = pos=(0,0,0) rot=(1,0,0;1.5708rad)
  Profile = -> Sketch070
  ReferenceAxis = -> Sketch070 [N_Axis]
  Refine = true
  Suppressed = false
  Type = 0
FEATURE [PartDesign::Pad] Pad001
  BaseFeature = -> Pad
  Direction = (0,-1,2e-16)
  Length = 5.6
  Length2 = 10
  Placement = pos=(0,0,0) rot=(1,0,0;1.5708rad)
  Profile = -> Sketch069
  ReferenceAxis = -> Sketch069 [N_Axis]
  Refine = true
  Suppressed = false
  Type = 0
FEATURE [PartDesign::Pocket] Pocket
  BaseFeature = -> Pad001
  Direction = (0,1,-2e-16)
  Length = 7
  Length2 = 5
  Midplane = true
  Placement = pos=(0,0,0) rot=(1,0,0;1.5708rad)
  Profile = -> Sketch071
  ReferenceAxis = -> Sketch071 [N_Axis]
  Refine = true
  Suppressed = false
  Type = 0
FEATURE [PartDesign::Fillet] Fillet
  Base = -> Pocket [Face7]
  BaseFeature = -> Pocket
  Placement = pos=(0,0,0) rot=(1,0,0;1.5708rad)
  Radius = 1
  Refine = true
  SupportTransform = false
  Suppressed = false
  UseAllEdges = false
FEATURE [PartDesign::Body] Body004  label="pulsanti lato sinistro"
  AllowCompound = false
  Group = -> [Sketch069,Sketch070,Sketch071,Pad,Pad001,Pocket,Fillet]
  Origin = -> Origin004
  Tip = -> Fillet
FEATURE [Sketcher::SketchObject] Sketch072  label="buco per saldature e diodo driver solenoide"
  ArcFitTolerance = 1e-06
  AttachmentSupport = -> [XZ_Plane]
  ExternalGeometry = -> [Sketch038]
  FullyConstrained = true
  MakeInternals = false
  MapMode = 5
  Placement = pos=(0,0,0) rot=(1,0,0;1.5708rad)
  sketch-geometry (4):
    g0: LineSegment StartX=-212.269 StartY=-43.9083 StartZ=0 EndX=-207.197 EndY=-33.0326 EndZ=0
    g1: LineSegment StartX=-207.197 StartY=-33.0326 StartZ=0 EndX=-207.56 EndY=-32.8635 EndZ=0
    g2: LineSegment StartX=-207.56 StartY=-32.8635 StartZ=0 EndX=-212.631 EndY=-43.7392 EndZ=0
    g3: LineSegment StartX=-212.631 StartY=-43.7392 StartZ=0 EndX=-212.269 EndY=-43.9083 EndZ=0
  constraints (11):
    c: Coincident(g1,g0)
    c: Coincident(g2,g1)
    c: Coincident(g3,g2)
    c: Coincident(g3,g0)
    c: Parallel(g-3,g0)
    c: Parallel(g0,g2)
    c: Perpendicular(g0,g3)
    c: Perpendicular(g1,g0)
    c: Distance(g3) = 0.4
    c: Distance(g2) = 12
    c: Coincident(g0,g-3)
FEATURE [Part::Extrusion] Extrude074  label="Extrude buco per saldature e diodo driver solenoide"
  Base = -> Sketch072
  Dir = (0,-1,2e-16)
  DirMode = 2
  FaceMakerClass = Part::FaceMakerBullseye
  FaceMakerMode = 3
  LengthFwd = 14.6
  LengthRev = 0
  Solid = true
  Symmetric = true
FEATURE [Part::Cut] Cut042
  Base = -> Cut041
  Refine = true
  Tool = -> Extrude074
FEATURE [Sketcher::SketchObject] Sketch073  label="fori slargati blocco solenoide"
  ArcFitTolerance = 1e-06
  AttachmentSupport = -> [XY_Plane]
  ExternalGeometry = -> [Sketch030]
  FullyConstrained = true
  MakeInternals = false
  MapMode = 5
  sketch-geometry (2):
    g0: Circle CenterX=-152.209 CenterY=6.95 CenterZ=0 NormalX=0 NormalY=0 NormalZ=1 AngleXU=0 Radius=3.7
    g1: Circle CenterX=-130.41 CenterY=-6.95 CenterZ=0 NormalX=0 NormalY=0 NormalZ=1 AngleXU=0 Radius=3.7
  constraints (4):
    c: Diameter(g0) = 7.4
    c: Coincident(g0,g-3)
    c: Diameter(g1) = 7.4
    c: Coincident(g1,g-4)
FEATURE [Part::Extrusion] Extrude075  label="Extrude fori slargati blocco solenoide"
  Base = -> Sketch073
  Dir = (0,0,1)
  DirMode = 2
  FaceMakerClass = Part::FaceMakerBullseye
  FaceMakerMode = 3
  LengthFwd = 1.5
  LengthRev = 0
  Placement = pos=(0,0,36.4) rot=(0,0,1;0rad)
  Solid = true
  Symmetric = false
FEATURE [Part::Cut] Cut043
  Base = -> Cut042
  Refine = true
  Tool = -> Extrude075
FEATURE [Sketcher::SketchObject] Sketch074  label="lato sx pistola"
  ArcFitTolerance = 1e-06
  AttachmentSupport = -> [XZ_Plane]
  ExternalGeometry = -> [Sketch016,Sketch,Sketch058]
  FullyConstrained = true
  MakeInternals = false
  MapMode = 5
  Placement = pos=(0,0,0) rot=(1,0,0;1.5708rad)
  sketch-geometry (37):
    g0: LineSegment StartX=-82.8 StartY=3.2 StartZ=0 EndX=0 EndY=3.2 EndZ=0
    g1: LineSegment StartX=-82.8 StartY=3.2 StartZ=0 EndX=-82.8 EndY=6.2 EndZ=0
    g2: LineSegment [constr] StartX=-107.6 StartY=18 StartZ=0 EndX=-107.6 EndY=20 EndZ=0
    g3: LineSegment [constr] StartX=-132.428 StartY=18 StartZ=0 EndX=-132.428 EndY=20 EndZ=0
    g4: LineSegment StartX=-132.428 StartY=20 StartZ=0 EndX=-107.6 EndY=20 EndZ=0
    g5: ArcOfCircle CenterX=-107.6 CenterY=4 CenterZ=0 NormalX=0 NormalY=0 NormalZ=1 AngleXU=0 Radius=16 StartAngle=0.137937 EndAngle=1.5708
    g6: LineSegment StartX=-82.8 StartY=6.2 StartZ=0 EndX=-91.752 EndY=6.2 EndZ=0
    g7: LineSegment [constr] StartX=-145.743 StartY=8.32624 StartZ=0 EndX=-147.645 EndY=8.94427 EndZ=0
    g8: ArcOfCircle CenterX=-132.428 CenterY=4 CenterZ=0 NormalX=0 NormalY=0 NormalZ=1 AngleXU=0 Radius=16 StartAngle=1.5708 EndAngle=2.82743
    g9: LineSegment StartX=-215.932 StartY=-80.4316 StartZ=0 EndX=-176.685 EndY=-80.4316 EndZ=0
    g10: LineSegment StartX=-147.645 StartY=8.94427 StartZ=0 EndX=-176.685 EndY=-80.4316 EndZ=0
    g11: LineSegment [constr] StartX=-193.988 StartY=-2.33927 StartZ=0 EndX=-192.176 EndY=-3.18451 EndZ=0
    g12: LineSegment [constr] StartX=-217.232 StartY=-52.1862 StartZ=0 EndX=-215.42 EndY=-53.0314 EndZ=0
    g13: LineSegment StartX=-192.176 StartY=-3.18451 StartZ=0 EndX=-215.42 EndY=-53.0314 EndZ=0
    g14: ArcOfCircle CenterX=-184.801 CenterY=-67.3089 CenterZ=0 NormalX=0 NormalY=0 NormalZ=1 AngleXU=0 Radius=33.7833 StartAngle=2.70526 EndAngle=3.54053
    g15: ArcOfCircle CenterX=-207.583 CenterY=4 CenterZ=0 NormalX=0 NormalY=0 NormalZ=1 AngleXU=0 Radius=17 StartAngle=5.84685 EndAngle=7.56663
    g16: LineSegment StartX=-202.765 StartY=20.303 StartZ=0 EndX=-195.887 EndY=39.2 EndZ=0
    g17: LineSegment [constr] StartX=-193.885 StartY=33.0037 StartZ=0 EndX=-197.644 EndY=34.3718 EndZ=0
    g18: LineSegment StartX=-195.887 StartY=39.2 StartZ=0 EndX=0 EndY=39.2 EndZ=0
    g19: LineSegment StartX=0 StartY=3.2 StartZ=0 EndX=0 EndY=39.2 EndZ=0
    g20: LineSegment StartX=-189.939 StartY=31.5672 StartZ=0 EndX=-192.333 EndY=24.9893 EndZ=0
    g21: LineSegment StartX=-196.467 StartY=26.4942 StartZ=0 EndX=-194.073 EndY=33.0721 EndZ=0
    g22: Circle CenterX=-213.443 CenterY=-76.8316 CenterZ=0 NormalX=0 NormalY=0 NormalZ=1 AngleXU=0 Radius=1.8
    g23: Circle CenterX=-179.305 CenterY=-76.8316 CenterZ=0 NormalX=0 NormalY=0 NormalZ=1 AngleXU=0 Radius=1.8
    g24: Circle CenterX=-184.08 CenterY=34.8 CenterZ=0 NormalX=0 NormalY=0 NormalZ=1 AngleXU=0 Radius=1.8
    g25: Circle CenterX=-78.51 CenterY=34.8 CenterZ=0 NormalX=0 NormalY=0 NormalZ=1 AngleXU=0 Radius=1.8
    g26: Circle CenterX=-78.51 CenterY=7.6 CenterZ=0 NormalX=0 NormalY=0 NormalZ=1 AngleXU=0 Radius=1.8
    g27: Circle CenterX=-5.6 CenterY=34.8 CenterZ=0 NormalX=0 NormalY=0 NormalZ=1 AngleXU=0 Radius=1.8
    g28: Circle CenterX=-5.6 CenterY=7.6 CenterZ=0 NormalX=0 NormalY=0 NormalZ=1 AngleXU=0 Radius=1.8
    g29: LineSegment StartX=-190.127 StartY=31.6356 StartZ=0 EndX=-189.939 EndY=31.5672 EndZ=0
    g30: LineSegment StartX=-194.073 StartY=33.0721 StartZ=0 EndX=-193.885 EndY=33.0037 EndZ=0
    g31: LineSegment StartX=-193.885 StartY=33.0037 StartZ=0 EndX=-190.127 EndY=31.6356 EndZ=0
    g32: LineSegment StartX=-196.467 StartY=26.4942 StartZ=0 EndX=-192.333 EndY=24.9893 EndZ=0
    g33: Circle CenterX=-19 CenterY=21.2 CenterZ=0 NormalX=0 NormalY=0 NormalZ=1 AngleXU=0 Radius=6.3
    g34: Circle CenterX=-42 CenterY=21.2 CenterZ=0 NormalX=0 NormalY=0 NormalZ=1 AngleXU=0 Radius=6.3
    g35: Circle CenterX=-65 CenterY=21.2 CenterZ=0 NormalX=0 NormalY=0 NormalZ=1 AngleXU=0 Radius=6.3
    g36: LineSegment [constr] StartX=-4 StartY=21.2 StartZ=0 EndX=-65 EndY=21.2 EndZ=0
  constraints (96):
    c: Coincident(g0,g-41)
    c: Horizontal(g0)
    c: PointOnObject(g0,g-39)
    c: Coincident(g1,g0)
    c: Vertical(g1)
    c: DistanceY(g1,g1) = 3
    c: Coincident(g2,g-17)
    c: Vertical(g2)
    c: Coincident(g3,g-16)
    c: Vertical(g3)
    c: DistanceY(g2,g2) = 2
    c: DistanceY(g3,g3) = 2
    c: Coincident(g4,g3)
    c: Coincident(g4,g2)
    c: Coincident(g5,g-17)
    c: Coincident(g5,g2)
    c: Coincident(g6,g1)
    c: Horizontal(g6)
    c: Coincident(g6,g5)
    c: Coincident(g7,g-15)
    c: Coincident(g8,g7)
    c: Coincident(g8,g3)
    c: Coincident(g8,g-15)
    c: Horizontal(g9)
    c: DistanceY(g-13,g9) = 2
    c: Coincident(g10,g7)
    c: Parallel(g10,g-14)
    c: Coincident(g9,g10)
    c: Distance(g11) = 2
    c: Coincident(g11,g-11)
    c: Perpendicular(g-11,g11)
    c: Distance(g12) = 2
    c: Coincident(g12,g-12)
    c: Perpendicular(g-11,g12)
    c: Coincident(g13,g11)
    c: Coincident(g13,g12)
    c: Coincident(g14,g-32)
    c: Coincident(g14,g12)
    c: Coincident(g14,g9)
    c: Coincident(g15,g-10)
    c: Coincident(g15,g11)
    c: Parallel(g16,g-22)
    c: Distance(g17) = 4
    c: PointOnObject(g17,g16)
    c: Coincident(g15,g16)
    c: Horizontal(g18)
    c: Coincident(g18,g16)
    c: Coincident(g19,g0)
    c: PointOnObject(g19,g-39)
    c: DistanceY(g19,g-36) = 2
    c: Coincident(g18,g19)
    c: Diameter(g22) = 3.6
    c: Coincident(g22,g-9)
    c: Diameter(g23) = 3.6
    c: Coincident(g23,g-8)
    c: Diameter(g24) = 3.6
    c: Diameter(g25) = 3.6
    c: Diameter(g26) = 3.6
    c: Diameter(g27) = 3.6
    c: Diameter(g28) = 3.6
    c: Coincident(g27,g-4)
    c: Coincident(g28,g-3)
    c: Coincident(g25,g-6)
    c: Coincident(g26,g-5)
    c: Coincident(g24,g-7)
    c: Parallel(g20,g-21)
    c: Equal(g20,g-21)
    c: Parallel(g21,g-19)
    c: Equal(g21,g-19)
    c: Distance(g29) = 0.2
    c: Distance(g30) = 0.2
    c: Parallel(g29,g-20)
    c: Parallel(g31,g-20)
    c: Equal(g31,g-20)
    c: Coincident(g30,g31)
    c: Coincident(g31,g29)
    c: Coincident(g29,g-21)
    c: Parallel(g30,g31)
    c: Coincident(g17,g30)
    c: Coincident(g20,g29)
    c: Coincident(g21,g30)
    c: Perpendicular(g16,g17)
    c: Coincident(g32,g21)
    c: Coincident(g32,g20)
    c: Perpendicular(g10,g7)
    c: Diameter(g33) = 12.6
    c: Diameter(g34) = 12.6
    c: Diameter(g35) = 12.6
    c: Horizontal(g36)
    c: PointOnObject(g33,g36)
    c: PointOnObject(g34,g36)
    c: DistanceX(g34,g33) = 23
    c: DistanceX(g35,g34) = 23
    c: DistanceX(g33,g36) = 15
    c: Symmetric(g-24,g-24,g36)
    c: Coincident(g36,g35)
FEATURE [Sketcher::SketchObject] Sketch075  label="lato dx pistola"
  ArcFitTolerance = 1e-06
  AttachmentSupport = -> [XZ_Plane]
  ExternalGeometry = -> [Sketch016,Sketch,Sketch058,Sketch074]
  FullyConstrained = true
  MakeInternals = false
  MapMode = 5
  Placement = pos=(0,0,0) rot=(1,0,0;1.5708rad)
  sketch-geometry (61):
    g0: LineSegment StartX=-82.8 StartY=3.2 StartZ=0 EndX=0 EndY=3.2 EndZ=0
    g1: LineSegment StartX=-82.8 StartY=3.2 StartZ=0 EndX=-82.8 EndY=6.2 EndZ=0
    g2: LineSegment [constr] StartX=-107.6 StartY=18 StartZ=0 EndX=-107.6 EndY=20 EndZ=0
    g3: LineSegment [constr] StartX=-132.428 StartY=18 StartZ=0 EndX=-132.428 EndY=20 EndZ=0
    g4: LineSegment StartX=-132.428 StartY=20 StartZ=0 EndX=-107.6 EndY=20 EndZ=0
    g5: ArcOfCircle CenterX=-107.6 CenterY=4 CenterZ=0 NormalX=0 NormalY=0 NormalZ=1 AngleXU=0 Radius=16 StartAngle=0.137937 EndAngle=1.5708
    g6: LineSegment StartX=-82.8 StartY=6.2 StartZ=0 EndX=-91.752 EndY=6.2 EndZ=0
    g7: LineSegment [constr] StartX=-145.743 StartY=8.32624 StartZ=0 EndX=-147.645 EndY=8.94427 EndZ=0
    g8: ArcOfCircle CenterX=-132.428 CenterY=4 CenterZ=0 NormalX=0 NormalY=0 NormalZ=1 AngleXU=0 Radius=16 StartAngle=1.5708 EndAngle=2.82743
    g9: LineSegment StartX=-215.932 StartY=-80.4316 StartZ=0 EndX=-176.685 EndY=-80.4316 EndZ=0
    g10: LineSegment StartX=-147.645 StartY=8.94427 StartZ=0 EndX=-176.685 EndY=-80.4316 EndZ=0
    g11: LineSegment [constr] StartX=-193.988 StartY=-2.33927 StartZ=0 EndX=-192.176 EndY=-3.18451 EndZ=0
    g12: LineSegment [constr] StartX=-217.232 StartY=-52.1862 StartZ=0 EndX=-215.42 EndY=-53.0314 EndZ=0
    g13: LineSegment StartX=-192.176 StartY=-3.18451 StartZ=0 EndX=-215.42 EndY=-53.0314 EndZ=0
    g14: ArcOfCircle CenterX=-184.801 CenterY=-67.3089 CenterZ=0 NormalX=0 NormalY=0 NormalZ=1 AngleXU=0 Radius=33.7833 StartAngle=2.70526 EndAngle=3.54053
    g15: ArcOfCircle CenterX=-207.583 CenterY=4 CenterZ=0 NormalX=0 NormalY=0 NormalZ=1 AngleXU=0 Radius=17 StartAngle=5.84685 EndAngle=7.56663
    g16: LineSegment StartX=-202.765 StartY=20.303 StartZ=0 EndX=-195.887 EndY=39.2 EndZ=0
    g17: LineSegment [constr] StartX=-193.885 StartY=33.0037 StartZ=0 EndX=-197.644 EndY=34.3718 EndZ=0
    g18: LineSegment StartX=-195.887 StartY=39.2 StartZ=0 EndX=0 EndY=39.2 EndZ=0
    g19: LineSegment StartX=0 StartY=3.2 StartZ=0 EndX=0 EndY=39.2 EndZ=0
    g20: LineSegment StartX=-189.939 StartY=31.5672 StartZ=0 EndX=-192.333 EndY=24.9893 EndZ=0
    g21: LineSegment StartX=-196.467 StartY=26.4942 StartZ=0 EndX=-194.073 EndY=33.0721 EndZ=0
    g22: Circle CenterX=-213.443 CenterY=-76.8316 CenterZ=0 NormalX=0 NormalY=0 NormalZ=1 AngleXU=0 Radius=1.8
    g23: Circle CenterX=-179.305 CenterY=-76.8316 CenterZ=0 NormalX=0 NormalY=0 NormalZ=1 AngleXU=0 Radius=1.8
    g24: Circle CenterX=-184.08 CenterY=34.8 CenterZ=0 NormalX=0 NormalY=0 NormalZ=1 AngleXU=0 Radius=1.8
    g25: Circle CenterX=-78.51 CenterY=34.8 CenterZ=0 NormalX=0 NormalY=0 NormalZ=1 AngleXU=0 Radius=1.8
    g26: Circle CenterX=-78.51 CenterY=7.6 CenterZ=0 NormalX=0 NormalY=0 NormalZ=1 AngleXU=0 Radius=1.8
    g27: Circle CenterX=-5.6 CenterY=34.8 CenterZ=0 NormalX=0 NormalY=0 NormalZ=1 AngleXU=0 Radius=1.8
    g28: Circle CenterX=-5.6 CenterY=7.6 CenterZ=0 NormalX=0 NormalY=0 NormalZ=1 AngleXU=0 Radius=1.8
    g29: LineSegment StartX=-190.127 StartY=31.6356 StartZ=0 EndX=-189.939 EndY=31.5672 EndZ=0
    g30: LineSegment StartX=-194.073 StartY=33.0721 StartZ=0 EndX=-193.885 EndY=33.0037 EndZ=0
    g31: LineSegment StartX=-193.885 StartY=33.0037 StartZ=0 EndX=-190.127 EndY=31.6356 EndZ=0
    g32: LineSegment StartX=-196.467 StartY=26.4942 StartZ=0 EndX=-192.333 EndY=24.9893 EndZ=0
    g33: LineSegment [constr] StartX=-4 StartY=21.2 StartZ=0 EndX=-87.91 EndY=21.2 EndZ=0
    g34: GeomPoint [constr] X=-4 Y=21.2 Z=0
    g35: LineSegment [constr] StartX=-15.2 StartY=33.7 StartZ=0 EndX=-15.2 EndY=8.7 EndZ=0
    g36: LineSegment [constr] StartX=-15.2 StartY=33.7 StartZ=0 EndX=-56.2 EndY=33.7 EndZ=0
    g37: LineSegment [constr] StartX=-15.2 StartY=8.7 StartZ=0 EndX=-56.2 EndY=8.7 EndZ=0
    g38: LineSegment [constr] StartX=-56.2 StartY=33.7 StartZ=0 EndX=-56.2 EndY=8.7 EndZ=0
    g39: Circle CenterX=-18.6 CenterY=30.3 CenterZ=0 NormalX=0 NormalY=0 NormalZ=1 AngleXU=0 Radius=3.4
    g40: Circle CenterX=-18.6 CenterY=12.1 CenterZ=0 NormalX=0 NormalY=0 NormalZ=1 AngleXU=0 Radius=3.4
    g41: Circle CenterX=-43.2 CenterY=30.3 CenterZ=0 NormalX=0 NormalY=0 NormalZ=1 AngleXU=0 Radius=3.4
    g42: Circle CenterX=-43.2 CenterY=12.1 CenterZ=0 NormalX=0 NormalY=0 NormalZ=1 AngleXU=0 Radius=3.4
    g43: LineSegment [constr] StartX=-4 StartY=21.2 StartZ=0 EndX=-15.2 EndY=21.2 EndZ=0
    g44: LineSegment [constr] StartX=-15.2 StartY=21.2 StartZ=0 EndX=-36.2 EndY=21.2 EndZ=0
    g45: LineSegment [constr] StartX=-41.5 StartY=16.2 StartZ=0 EndX=-30.9 EndY=16.2 EndZ=0
    g46: LineSegment [constr] StartX=-30.9 StartY=16.2 StartZ=0 EndX=-30.9 EndY=26.2 EndZ=0
    g47: LineSegment [constr] StartX=-30.9 StartY=26.2 StartZ=0 EndX=-41.5 EndY=26.2 EndZ=0
    g48: LineSegment [constr] StartX=-41.5 StartY=26.2 StartZ=0 EndX=-41.5 EndY=16.2 EndZ=0
    g49: GeomPoint [constr] X=-36.2 Y=21.2 Z=0
    g50: Circle CenterX=-36.2 CenterY=21.2 CenterZ=0 NormalX=0 NormalY=0 NormalZ=1 AngleXU=0 Radius=2.8
    g51: LineSegment [constr] StartX=-24.2 StartY=26.7 StartZ=0 EndX=-24.2 EndY=15.7 EndZ=0
    g52: Circle CenterX=-24.2 CenterY=26.7 CenterZ=0 NormalX=0 NormalY=0 NormalZ=1 AngleXU=0 Radius=3
    g53: Circle CenterX=-24.2 CenterY=15.7 CenterZ=0 NormalX=0 NormalY=0 NormalZ=1 AngleXU=0 Radius=3
    g54: GeomPoint X=-18.6 Y=30.3 Z=0
    g55: GeomPoint X=-18.6 Y=12.1 Z=0
    g56: GeomPoint X=-43.2 Y=12.1 Z=0
    g57: GeomPoint X=-43.2 Y=30.3 Z=0
    g58: Circle CenterX=-65 CenterY=21.2 CenterZ=0 NormalX=0 NormalY=0 NormalZ=1 AngleXU=0 Radius=1.5
    g59: Circle CenterX=-42 CenterY=21.2 CenterZ=0 NormalX=0 NormalY=0 NormalZ=1 AngleXU=0 Radius=1.5
    g60: Circle CenterX=-19 CenterY=21.2 CenterZ=0 NormalX=0 NormalY=0 NormalZ=1 AngleXU=0 Radius=1.5
  constraints (149):
    c: Coincident(g0,g-41)
    c: Horizontal(g0)
    c: PointOnObject(g0,g-39)
    c: Coincident(g1,g0)
    c: Vertical(g1)
    c: DistanceY(g1,g1) = 3
    c: Coincident(g2,g-17)
    c: Vertical(g2)
    c: Coincident(g3,g-16)
    c: Vertical(g3)
    c: DistanceY(g2,g2) = 2
    c: DistanceY(g3,g3) = 2
    c: Coincident(g4,g3)
    c: Coincident(g4,g2)
    c: Coincident(g5,g-17)
    c: Coincident(g5,g2)
    c: Coincident(g6,g1)
    c: Horizontal(g6)
    c: Coincident(g6,g5)
    c: Coincident(g7,g-15)
    c: Coincident(g8,g7)
    c: Coincident(g8,g3)
    c: Coincident(g8,g-15)
    c: Horizontal(g9)
    c: DistanceY(g-13,g9) = 2
    c: Coincident(g10,g7)
    c: Parallel(g10,g-14)
    c: Coincident(g9,g10)
    c: Distance(g11) = 2
    c: Coincident(g11,g-11)
    c: Perpendicular(g-11,g11)
    c: Distance(g12) = 2
    c: Coincident(g12,g-12)
    c: Perpendicular(g-11,g12)
    c: Coincident(g13,g11)
    c: Coincident(g13,g12)
    c: Coincident(g14,g-32)
    c: Coincident(g14,g12)
    c: Coincident(g14,g9)
    c: Coincident(g15,g-10)
    c: Coincident(g15,g11)
    c: Parallel(g16,g-22)
    c: Distance(g17) = 4
    c: PointOnObject(g17,g16)
    c: Coincident(g15,g16)
    c: Horizontal(g18)
    c: Coincident(g18,g16)
    c: Coincident(g19,g0)
    c: PointOnObject(g19,g-39)
    c: DistanceY(g19,g-36) = 2
    c: Coincident(g18,g19)
    c: Diameter(g22) = 3.6
    c: Coincident(g22,g-9)
    c: Diameter(g23) = 3.6
    c: Coincident(g23,g-8)
    c: Diameter(g24) = 3.6
    c: Diameter(g25) = 3.6
    c: Diameter(g26) = 3.6
    c: Diameter(g27) = 3.6
    c: Diameter(g28) = 3.6
    c: Coincident(g27,g-4)
    c: Coincident(g28,g-3)
    c: Coincident(g25,g-6)
    c: Coincident(g26,g-5)
    c: Coincident(g24,g-7)
    c: Parallel(g20,g-21)
    c: Equal(g20,g-21)
    c: Parallel(g21,g-19)
    c: Equal(g21,g-19)
    c: Distance(g29) = 0.2
    c: Distance(g30) = 0.2
    c: Parallel(g29,g-20)
    c: Parallel(g31,g-20)
    c: Equal(g31,g-20)
    c: Coincident(g30,g31)
    c: Coincident(g31,g29)
    c: Coincident(g29,g-21)
    c: Parallel(g30,g31)
    c: Coincident(g17,g30)
    c: Coincident(g20,g29)
    c: Coincident(g21,g30)
    c: Perpendicular(g16,g17)
    c: Coincident(g32,g21)
    c: Coincident(g32,g20)
    c: Perpendicular(g10,g7)
    c: Horizontal(g33)
    c: Symmetric(g-24,g-24,g33)
    c: PointOnObject(g33,g-28)
    c: Symmetric(g-24,g-24,g34)
    c: DistanceY(g35,g35) = 25
    c: Symmetric(g35,g35,g33)
    c: Distance(g36) = 41
    c: Coincident(g36,g35)
    c: Horizontal(g36)
    c: Coincident(g37,g35)
    c: Horizontal(g37)
    c: Coincident(g38,g36)
    c: Vertical(g38)
    c: Coincident(g37,g38)
    c: Diameter(g39) = 6.8
    c: Diameter(g40) = 6.8
    c: Tangent(g39,g36)
    c: Tangent(g40,g37)
    c: Tangent(g39,g35)
    c: Tangent(g40,g35)
    c: Diameter(g41) = 6.8
    c: Diameter(g42) = 6.8
    c: Tangent(g41,g36)
    c: Tangent(g42,g37)
    c: DistanceX(g41,g39) = 24.6
    c: DistanceX(g42,g40) = 24.6
    c: Distance(g43) = 11.2
    c: Coincident(g43,g33)
    c: PointOnObject(g43,g33)
    c: PointOnObject(g43,g35)
    c: Distance(g44) = 21
    c: Coincident(g44,g43)
    c: PointOnObject(g44,g33)
    c: Coincident(g45,g46)
    c: Coincident(g46,g47)
    c: Coincident(g47,g48)
    c: Coincident(g48,g45)
    c: Horizontal(g45)
    c: Horizontal(g47)
    c: Vertical(g46)
    c: Vertical(g48)
    c: Symmetric(g47,g45,g49)
    c: Distance(g46,g48) = 10.6
    c: Distance(g45,g47) = 10
    c: Coincident(g49,g44)
    c: Diameter(g50) = 5.6
    c: Coincident(g50,g44)
    c: Distance(g51) = 11
    c: Symmetric(g51,g51,g33)
    c: DistanceX(g51,g43) = 9
    c: Diameter(g52) = 6
    c: Coincident(g52,g51)
    c: Diameter(g53) = 6
    c: Coincident(g53,g51)
    c: Coincident(g40,g55)
    c: Coincident(g39,g54)
    c: Coincident(g41,g57)
    c: Coincident(g42,g56)
    c: Diameter(g58) = 3
    c: Diameter(g59) = 3
    c: Diameter(g60) = 3
    c: Coincident(g58,g-44)
    c: Coincident(g59,g-46)
    c: Coincident(g60,g-45)
FEATURE [Sketcher::SketchObject] Sketch078
  ArcFitTolerance = 1e-06
  AttachmentSupport = -> [XZ_Plane005]
  FullyConstrained = true
  MakeInternals = false
  MapMode = 5
  Placement = pos=(0,0,0) rot=(1,0,0;1.5708rad)
  sketch-geometry (5):
    g0: LineSegment [constr] StartX=0 StartY=5.5 StartZ=0 EndX=0 EndY=-5.5 EndZ=0
    g1: ArcOfCircle CenterX=0 CenterY=5.5 CenterZ=0 NormalX=0 NormalY=0 NormalZ=1 AngleXU=0 Radius=2.7 StartAngle=0 EndAngle=3.14159
    g2: ArcOfCircle CenterX=0 CenterY=-5.5 CenterZ=0 NormalX=0 NormalY=0 NormalZ=1 AngleXU=0 Radius=2.7 StartAngle=3.1416 EndAngle=6.28318
    g3: LineSegment StartX=-2.7 StartY=5.5 StartZ=0 EndX=-2.7 EndY=-5.50001 EndZ=0
    g4: LineSegment StartX=2.7 StartY=5.5 StartZ=0 EndX=2.7 EndY=-5.50001 EndZ=0
  constraints (13):
    c: Distance(g0) = 11
    c: Vertical(g0)
    c: Symmetric(g0,g0,g-1)
    c: Radius(g1) = 2.7
    c: Coincident(g1,g0)
    c: Radius(g2) = 2.7
    c: Coincident(g2,g0)
    c: Vertical(g3)
    c: Vertical(g4)
    c: Coincident(g2,g4)
    c: Coincident(g2,g3)
    c: Tangent(g3,g1) = -1.5708
    c: Tangent(g4,g1) = 1.5708
FEATURE [PartDesign::Pad] Pad002
  Direction = (0,-1,2e-16)
  Length = 0.8
  Length2 = 10
  Placement = pos=(0,0,0) rot=(1,0,0;1.5708rad)
  Profile = -> Sketch078
  ReferenceAxis = -> Sketch078 [N_Axis]
  Refine = true
  Suppressed = false
  Type = 0
FEATURE [Sketcher::SketchObject] Sketch079
  ArcFitTolerance = 1e-06
  AttachmentSupport = -> [XZ_Plane005]
  ExternalGeometry = -> [Sketch078]
  FullyConstrained = true
  MakeInternals = false
  MapMode = 5
  Placement = pos=(0,0,0) rot=(1,0,0;1.5708rad)
  sketch-geometry (2):
    g0: Circle CenterX=-1e-16 CenterY=5.5 CenterZ=0 NormalX=0 NormalY=0 NormalZ=1 AngleXU=0 Radius=2.7
    g1: Circle CenterX=0 CenterY=-5.5 CenterZ=0 NormalX=0 NormalY=0 NormalZ=1 AngleXU=0 Radius=2.7
  constraints (4):
    c: Coincident(g0,g-3)
    c: PointOnObject(g-3,g0)
    c: Coincident(g1,g-4)
    c: Equal(g1,g-4)
FEATURE [PartDesign::Pad] Pad003
  BaseFeature = -> Pad002
  Direction = (0,-1,2e-16)
  Length = 5
  Length2 = 10
  Placement = pos=(0,0,0) rot=(1,0,0;1.5708rad)
  Profile = -> Sketch079
  ReferenceAxis = -> Sketch079 [N_Axis]
  Refine = true
  Suppressed = false
  Type = 0
FEATURE [PartDesign::Fillet] Fillet001
  Base = -> Pad003 [Edge16,Edge14]
  BaseFeature = -> Pad003
  Placement = pos=(0,0,0) rot=(1,0,0;1.5708rad)
  Radius = 0.4
  Refine = true
  SupportTransform = false
  Suppressed = false
  UseAllEdges = false
FEATURE [PartDesign::Body] Body005  label="pulsanti lato destro"
  AllowCompound = false
  Group = -> [Sketch078,Pad002,Sketch079,Pad003,Fillet001]
  Origin = -> Origin005
  Tip = -> Fillet001
FEATURE [PartDesign::SubShapeBinder] Binder
  BindCopyOnChange = 0
  BindMode = 0
  ClaimChildren = false
  Context = -> Body006 [Binder.]
  Fuse = false
  MakeFace = true
  OffsetFill = false
  OffsetIntersection = false
  OffsetJoinType = 0
  OffsetOpenResult = false
  PartialLoad = false
  Refine = true
  Relative = true
  Support = -> [Body[Sketch074.]]
  _Version = 2
FEATURE [PartDesign::SubShapeBinder] Binder001
  BindCopyOnChange = 0
  BindMode = 0
  ClaimChildren = false
  Context = -> Body007 [Binder001.]
  Fuse = false
  MakeFace = true
  OffsetFill = false
  OffsetIntersection = false
  OffsetJoinType = 0
  OffsetOpenResult = false
  PartialLoad = false
  Refine = true
  Relative = true
  Support = -> [Body[Sketch075.]]
  _Version = 2
FEATURE [Mesh::Feature] logo_per_PCB_definitivo_positivo
  Placement = pos=(-191,17,-66) rot=(0,1,1;0rad)
FEATURE [Sketcher::SketchObject] Sketch114  label="Sketch114 - base lato DX"
  ArcFitTolerance = 1e-06
  AttachmentSupport = -> [Binder001]
  ExternalGeometry = -> [Binder001]
  FullyConstrained = true
  MakeInternals = false
  MapMode = 5
  Placement = pos=(0,1e-15,0) rot=(0,0.707107,0.707107;3.14159rad)
  sketch-geometry (30):
    g0: Circle CenterX=5.6 CenterY=34.8 CenterZ=0 NormalX=0 NormalY=0 NormalZ=1 AngleXU=0 Radius=1.8
    g1: Circle CenterX=5.6 CenterY=7.6 CenterZ=0 NormalX=0 NormalY=0 NormalZ=1 AngleXU=0 Radius=1.8
    g2: Circle CenterX=24.2 CenterY=26.7 CenterZ=0 NormalX=0 NormalY=0 NormalZ=1 AngleXU=0 Radius=3
    g3: Circle CenterX=24.2 CenterY=15.7 CenterZ=0 NormalX=0 NormalY=0 NormalZ=1 AngleXU=0 Radius=3
    g4: Circle CenterX=36.2 CenterY=21.2 CenterZ=0 NormalX=0 NormalY=0 NormalZ=1 AngleXU=0 Radius=2.8
    g5: Circle CenterX=78.51 CenterY=34.8 CenterZ=0 NormalX=0 NormalY=0 NormalZ=1 AngleXU=0 Radius=1.8
    g6: Circle CenterX=78.51 CenterY=7.6 CenterZ=0 NormalX=0 NormalY=0 NormalZ=1 AngleXU=0 Radius=1.8
    g7: Circle CenterX=184.08 CenterY=34.8 CenterZ=0 NormalX=0 NormalY=0 NormalZ=1 AngleXU=0 Radius=1.8
    g8: Circle CenterX=213.443 CenterY=-76.8316 CenterZ=0 NormalX=0 NormalY=0 NormalZ=1 AngleXU=0 Radius=1.8
    g9: Circle CenterX=179.305 CenterY=-76.8316 CenterZ=0 NormalX=0 NormalY=0 NormalZ=1 AngleXU=0 Radius=1.8
    g10: ArcOfCircle [constr] CenterX=132.428 CenterY=4 CenterZ=0 NormalX=0 NormalY=0 NormalZ=1 AngleXU=0 Radius=16 StartAngle=0.314159 EndAngle=1.5708
    g11: ArcOfCircle CenterX=107.6 CenterY=4 CenterZ=0 NormalX=0 NormalY=0 NormalZ=1 AngleXU=0 Radius=16 StartAngle=1.5708 EndAngle=3.00366
    g12: ArcOfCircle CenterX=207.583 CenterY=4 CenterZ=0 NormalX=0 NormalY=0 NormalZ=1 AngleXU=0 Radius=17 StartAngle=1.85815 EndAngle=3.57792
    g13: ArcOfCircle CenterX=184.801 CenterY=-67.3089 CenterZ=0 NormalX=0 NormalY=0 NormalZ=1 AngleXU=0 Radius=33.7833 StartAngle=5.88425 EndAngle=6.71952
    g14: LineSegment StartX=0 StartY=39.2 StartZ=0 EndX=0 EndY=3.2 EndZ=0
    g15: LineSegment StartX=0 StartY=3.2 StartZ=0 EndX=82.8 EndY=3.2 EndZ=0
    g16: LineSegment StartX=82.8 StartY=3.2 StartZ=0 EndX=82.8 EndY=6.2 EndZ=0
    g17: LineSegment StartX=82.8 StartY=6.2 StartZ=0 EndX=91.752 EndY=6.2 EndZ=0
    g18: LineSegment StartX=107.6 StartY=20 StartZ=0 EndX=132.428 EndY=20 EndZ=0
    g19: LineSegment StartX=147.645 StartY=8.94427 StartZ=0 EndX=176.685 EndY=-80.4316 EndZ=0
    g20: LineSegment StartX=176.685 StartY=-80.4316 StartZ=0 EndX=215.932 EndY=-80.4316 EndZ=0
    g21: LineSegment StartX=215.42 StartY=-53.0314 StartZ=0 EndX=192.176 EndY=-3.18451 EndZ=0
    g22: LineSegment StartX=202.765 StartY=20.303 StartZ=0 EndX=195.887 EndY=39.2 EndZ=0
    g23: LineSegment StartX=195.887 StartY=39.2 StartZ=0 EndX=0 EndY=39.2 EndZ=0
    g24: LineSegment StartX=196.467 StartY=26.4942 StartZ=0 EndX=194.073 EndY=33.0721 EndZ=0
    g25: LineSegment StartX=194.073 StartY=33.0721 StartZ=0 EndX=189.939 EndY=31.5672 EndZ=0
    g26: LineSegment StartX=189.939 StartY=31.5672 StartZ=0 EndX=192.333 EndY=24.9893 EndZ=0
    g27: LineSegment StartX=192.333 StartY=24.9893 StartZ=0 EndX=196.467 EndY=26.4942 EndZ=0
    g28: LineSegment StartX=132.428 StartY=20 StartZ=0 EndX=144.053 EndY=20 EndZ=0
    g29: LineSegment StartX=144.053 StartY=20 StartZ=0 EndX=147.645 EndY=8.94427 EndZ=0
  constraints (65):
    c: Equal(g0,g-25)
    c: Equal(g2,g-29)
    c: Equal(g3,g-30)
    c: Equal(g4,g-28)
    c: Equal(g1,g-26)
    c: Coincident(g0,g-25)
    c: Coincident(g1,g-26)
    c: Coincident(g2,g-29)
    c: Coincident(g3,g-30)
    c: Coincident(g4,g-28)
    c: Equal(g5,g-23)
    c: Equal(g6,g-24)
    c: Coincident(g5,g-23)
    c: Coincident(g6,g-24)
    c: Equal(g7,g-20)
    c: Coincident(g7,g-20)
    c: Equal(g9,g-22)
    c: Coincident(g9,g-22)
    c: Equal(g8,g-21)
    c: Coincident(g8,g-21)
    c: Equal(g13,g-12)
    c: Equal(g12,g-14)
    c: Equal(g10,g-9)
    c: Equal(g11,g-7)
    c: Coincident(g14,g-27)
    c: Coincident(g14,g-27)
    c: Coincident(g15,g14)
    c: Coincident(g15,g-5)
    c: Coincident(g16,g15)
    c: Coincident(g16,g-6)
    c: Coincident(g17,g16)
    c: Coincident(g17,g-7)
    c: Coincident(g11,g17)
    c: Coincident(g11,g-8)
    c: Coincident(g18,g11)
    c: Coincident(g18,g-9)
    c: Coincident(g10,g18)
    c: Coincident(g10,g-10)
    c: Coincident(g19,g10)
    c: Coincident(g19,g-11)
    c: Coincident(g20,g19)
    c: Coincident(g20,g-12)
    c: Coincident(g13,g20)
    c: Coincident(g13,g-13)
    c: Coincident(g21,g13)
    c: Coincident(g21,g-14)
    c: Coincident(g12,g21)
    c: Coincident(g12,g-15)
    c: Coincident(g22,g12)
    c: Coincident(g22,g-15)
    c: Coincident(g23,g22)
    c: Coincident(g23,g14)
    c: Coincident(g24,g-18)
    c: Coincident(g24,g-16)
    c: Coincident(g25,g24)
    c: Coincident(g25,g-19)
    c: Coincident(g26,g25)
    c: Coincident(g26,g-19)
    c: Coincident(g27,g26)
    c: Coincident(g27,g24)
    c: Coincident(g29,g10)
    c: Coincident(g28,g10)
    c: Coincident(g29,g28)
    c: Parallel(g28,g18)
    c: Parallel(g29,g19)
FEATURE [PartDesign::Pad] Pad011
  Direction = (0,1,-2e-16)
  Length = 2
  Length2 = 10
  Profile = -> Sketch114
  ReferenceAxis = -> Sketch114 [N_Axis]
  Refine = true
  Reversed = true
  Suppressed = false
  Type = 0
FEATURE [Sketcher::SketchObject] Sketch115
  ArcFitTolerance = 1e-06
  AttachmentSupport = -> [Pad011]
  ExternalGeometry = -> [Binder001]
  FullyConstrained = true
  MakeInternals = false
  MapMode = 5
  Placement = pos=(0,1.7e-15,0) rot=(0,0.707107,0.707107;3.14159rad)
  sketch-geometry (4):
    g0: ArcOfCircle CenterX=24.2 CenterY=26.7 CenterZ=0 NormalX=0 NormalY=0 NormalZ=1 AngleXU=0 Radius=3 StartAngle=4.48384e-08 EndAngle=3.14159
    g1: ArcOfCircle CenterX=24.2 CenterY=15.7 CenterZ=0 NormalX=0 NormalY=0 NormalZ=1 AngleXU=0 Radius=3 StartAngle=3.14159 EndAngle=6.28318
    g2: LineSegment StartX=21.2 StartY=26.7 StartZ=0 EndX=21.2 EndY=15.7 EndZ=0
    g3: LineSegment StartX=27.2 StartY=26.7 StartZ=0 EndX=27.2 EndY=15.7 EndZ=0
  constraints (12):
    c: Equal(g1,g-4)
    c: Equal(g0,g-3)
    c: Coincident(g0,g-3)
    c: Coincident(g1,g-4)
    c: Vertical(g2)
    c: Vertical(g3)
    c: Tangent(g3,g-3)
    c: Tangent(g2,g-3)
    c: Coincident(g0,g2)
    c: Coincident(g0,g3)
    c: Coincident(g1,g2)
    c: Coincident(g3,g1)
FEATURE [Sketcher::SketchObject] Sketch117  label="Sketch117 - fori per inserto M3 x 3 x 4.5"
  ArcFitTolerance = 1e-06
  AttachmentSupport = -> [Pad011]
  ExternalGeometry = -> [Binder001]
  FullyConstrained = true
  MakeInternals = false
  MapMode = 5
  Placement = pos=(0,1.7e-15,0) rot=(0,0.707107,0.707107;3.14159rad)
  sketch-geometry (4):
    g0: Circle CenterX=43.2 CenterY=30.3 CenterZ=0 NormalX=0 NormalY=0 NormalZ=1 AngleXU=0 Radius=2.25
    g1: Circle CenterX=43.2 CenterY=12.1 CenterZ=0 NormalX=0 NormalY=0 NormalZ=1 AngleXU=0 Radius=2.25
    g2: Circle CenterX=18.6 CenterY=30.3 CenterZ=0 NormalX=0 NormalY=0 NormalZ=1 AngleXU=0 Radius=2.25
    g3: Circle CenterX=18.6 CenterY=12.1 CenterZ=0 NormalX=0 NormalY=0 NormalZ=1 AngleXU=0 Radius=2.25
  constraints (8):
    c: Diameter(g0) = 4.5
    c: Diameter(g1) = 4.5
    c: Diameter(g2) = 4.5
    c: Diameter(g3) = 4.5
    c: Coincident(g2,g-3)
    c: Coincident(g3,g-6)
    c: Coincident(g0,g-4)
    c: Coincident(g1,g-5)
FEATURE [Sketcher::SketchObject] Sketch118
  ArcFitTolerance = 1e-06
  AttachmentSupport = -> [Pad011]
  ExternalGeometry = -> [Binder001]
  FullyConstrained = true
  MakeInternals = false
  MapMode = 5
  Placement = pos=(0,-2,0) rot=(1,0,0;1.5708rad)
  sketch-geometry (12):
    g0: Circle CenterX=-78.51 CenterY=34.8 CenterZ=0 NormalX=0 NormalY=0 NormalZ=1 AngleXU=0 Radius=1.8
    g1: Circle CenterX=-78.51 CenterY=7.6 CenterZ=0 NormalX=0 NormalY=0 NormalZ=1 AngleXU=0 Radius=1.8
    g2: Circle CenterX=-5.6 CenterY=34.8 CenterZ=0 NormalX=0 NormalY=0 NormalZ=1 AngleXU=0 Radius=1.8
    g3: Circle CenterX=-5.6 CenterY=7.6 CenterZ=0 NormalX=0 NormalY=0 NormalZ=1 AngleXU=0 Radius=1.8
    g4: LineSegment StartX=0 StartY=39.2 StartZ=0 EndX=0 EndY=3.2 EndZ=0
    g5: LineSegment StartX=0 StartY=3.2 StartZ=0 EndX=-82.8 EndY=3.2 EndZ=0
    g6: LineSegment StartX=-82.8 StartY=3.2 StartZ=0 EndX=-82.8 EndY=39.2 EndZ=0
    g7: LineSegment StartX=-82.8 StartY=39.2 StartZ=0 EndX=0 EndY=39.2 EndZ=0
    g8: ArcOfCircle CenterX=-65 CenterY=21.2 CenterZ=0 NormalX=0 NormalY=0 NormalZ=1 AngleXU=0 Radius=10 StartAngle=1.5708 EndAngle=4.71239
    g9: ArcOfCircle CenterX=-19 CenterY=21.2 CenterZ=0 NormalX=0 NormalY=0 NormalZ=1 AngleXU=0 Radius=10 StartAngle=4.71239 EndAngle=7.85398
    g10: LineSegment StartX=-65 StartY=31.2 StartZ=0 EndX=-19 EndY=31.2 EndZ=0
    g11: LineSegment StartX=-65 StartY=11.2 StartZ=0 EndX=-19 EndY=11.2 EndZ=0
  constraints (25):
    c: Equal(g2,g-5)
    c: Equal(g3,g-7)
    c: Equal(g1,g-6)
    c: Equal(g0,g-4)
    c: Coincident(g0,g-4)
    c: Coincident(g1,g-6)
    c: Coincident(g3,g-7)
    c: Coincident(g2,g-5)
    c: Coincident(g4,g-8)
    c: Coincident(g4,g-9)
    c: Coincident(g5,g4)
    c: Coincident(g5,g-10)
    c: Coincident(g6,g5)
    c: PointOnObject(g6,g-3)
    c: Vertical(g6)
    c: Coincident(g7,g6)
    c: Coincident(g7,g4)
    c: Tangent(g8,g10) = 1.5708
    c: Tangent(g8,g11) = -1.5708
    c: Tangent(g9,g10) = 1.5708
    c: Tangent(g9,g11) = -1.5708
    c: Equal(g8,g9)
    c: Radius(g8) = 10
    c: Coincident(g8,g-11)
    c: Coincident(g9,g-12)
FEATURE [Sketcher::SketchObject] Sketch120
  ArcFitTolerance = 1e-06
  AttachmentSupport = -> [Pad011]
  ExternalGeometry = -> [Binder001]
  FullyConstrained = true
  MakeInternals = false
  MapMode = 5
  Placement = pos=(0,-2,0) rot=(1,0,0;1.5708rad)
  sketch-geometry (4):
    g0: LineSegment StartX=-137.815 StartY=39.2 StartZ=0 EndX=-142.655 EndY=24.303 EndZ=0
    g1: LineSegment StartX=-137.815 StartY=39.2 StartZ=0 EndX=-110.815 EndY=39.2 EndZ=0
    g2: LineSegment StartX=-142.655 StartY=24.303 StartZ=0 EndX=-110.815 EndY=24.303 EndZ=0
    g3: ArcOfCircle CenterX=-92.2534 CenterY=31.7515 CenterZ=0 NormalX=0 NormalY=0 NormalZ=1 AngleXU=0 Radius=20 StartAngle=2.75997 EndAngle=3.52321
  constraints (12):
    c: PointOnObject(g0,g-3)
    c: Coincident(g1,g0)
    c: PointOnObject(g1,g-3)
    c: Coincident(g2,g0)
    c: Horizontal(g2)
    c: Tangent(g0,g-4)
    c: Vertical(g2,g1)
    c: DistanceX(g1,g1) = 27
    c: DistanceY(g-6,g0) = 4
    c: Radius(g3) = 20
    c: Coincident(g3,g1)
    c: Coincident(g3,g2)
FEATURE [Sketcher::SketchObject] Sketch121
  ArcFitTolerance = 1e-06
  AttachmentSupport = -> [Pad011]
  ExternalGeometry = -> [Binder001]
  FullyConstrained = true
  MakeInternals = false
  MapMode = 5
  Placement = pos=(0,-2,0) rot=(1,0,0;1.5708rad)
  sketch-geometry (15):
    g0: LineSegment StartX=-137.815 StartY=39.2 StartZ=0 EndX=-143.955 EndY=20.303 EndZ=0
    g1: LineSegment StartX=-143.955 StartY=20.303 StartZ=0 EndX=-190.141 EndY=20.303 EndZ=0
    g2: LineSegment StartX=-190.141 StartY=20.303 StartZ=0 EndX=-186.139 EndY=31.3 EndZ=0
    g3: LineSegment StartX=-178.754 StartY=39.2 StartZ=0 EndX=-180.791 EndY=33.6029 EndZ=0
    g4: ArcOfCircle CenterX=-184.08 CenterY=34.8 CenterZ=0 NormalX=0 NormalY=0 NormalZ=1 AngleXU=0 Radius=3.5 StartAngle=4.71239 EndAngle=5.93412
    g5: LineSegment StartX=-184.08 StartY=31.3 StartZ=0 EndX=-186.139 EndY=31.3 EndZ=0
    g6: LineSegment StartX=-137.815 StartY=39.2 StartZ=0 EndX=-156.815 EndY=39.2 EndZ=0
    g7: LineSegment StartX=-168.815 StartY=39.2 StartZ=0 EndX=-178.754 EndY=39.2 EndZ=0
    g8: LineSegment StartX=-157.815 StartY=39.2 StartZ=0 EndX=-167.815 EndY=39.2 EndZ=0
    g9: LineSegment StartX=-168.815 StartY=31.2 StartZ=0 EndX=-156.815 EndY=31.2 EndZ=0
    g10: LineSegment StartX=-167.436 StartY=36.2 StartZ=0 EndX=-157.436 EndY=36.2 EndZ=0
    g11: ArcOfCircle CenterX=-176.411 CenterY=35.2 CenterZ=0 NormalX=0 NormalY=0 NormalZ=1 AngleXU=0 Radius=20 StartAngle=6.08183 EndAngle=6.48454
    g12: ArcOfCircle CenterX=-188.411 CenterY=35.2 CenterZ=0 NormalX=0 NormalY=0 NormalZ=1 AngleXU=0 Radius=20 StartAngle=6.08183 EndAngle=6.48454
    g13: ArcOfCircle CenterX=-177.411 CenterY=35.2 CenterZ=0 NormalX=0 NormalY=0 NormalZ=1 AngleXU=0 Radius=20 StartAngle=0.0500209 EndAngle=0.201358
    g14: ArcOfCircle CenterX=-187.411 CenterY=35.2 CenterZ=0 NormalX=0 NormalY=0 NormalZ=1 AngleXU=0 Radius=20 StartAngle=0.0500209 EndAngle=0.201358
  constraints (46):
    c: PointOnObject(g0,g-3)
    c: Tangent(g0,g-5)
    c: Coincident(g1,g0)
    c: Horizontal(g1)
    c: Coincident(g2,g1)
    c: PointOnObject(g3,g-3)
    c: Parallel(g3,g-6)
    c: Parallel(g2,g-6)
    c: Radius(g4) = 3.5
    c: Coincident(g4,g-7)
    c: Tangent(g3,g4) = 1.5708
    c: Horizontal(g5)
    c: Tangent(g5,g4) = 1.5708
    c: DistanceX(g-8,g5) = 3.8
    c: Coincident(g2,g5)
    c: Coincident(g6,g0)
    c: PointOnObject(g6,g-3)
    c: DistanceX(g6,g6) = 19
    c: PointOnObject(g7,g-3)
    c: DistanceX(g7,g6) = 12
    c: Coincident(g7,g3)
    c: PointOnObject(g8,g-3)
    c: PointOnObject(g8,g-3)
    c: DistanceX(g8,g8) = 10
    c: DistanceX(g8,g6) = 1
    c: Horizontal(g9)
    c: Vertical(g7,g9)
    c: Vertical(g6,g9)
    c: DistanceY(g9,g7) = 8
    c: Horizontal(g10)
    c: Equal(g8,g10)
    c: DistanceY(g10,g8) = 3
    c: Radius(g11) = 20
    c: Coincident(g11,g6)
    c: Coincident(g11,g9)
    c: Radius(g12) = 20
    c: Coincident(g12,g7)
    c: Coincident(g12,g9)
    c: Equal(g13,g11)
    c: Coincident(g13,g8)
    c: Coincident(g13,g10)
    c: Horizontal(g13,g11)
    c: Equal(g14,g12)
    c: Coincident(g14,g8)
    c: Coincident(g14,g10)
    c: Horizontal(g1,g-6)
FEATURE [Sketcher::SketchObject] Sketch122
  ArcFitTolerance = 1e-06
  AttachmentSupport = -> [Pad011]
  ExternalGeometry = -> [Binder001]
  FullyConstrained = true
  MakeInternals = false
  MapMode = 5
  Placement = pos=(0,-2,0) rot=(1,0,0;1.5708rad)
  sketch-geometry (8):
    g0: LineSegment StartX=-202.765 StartY=20.303 StartZ=0 EndX=-143.955 EndY=20.303 EndZ=0
    g1: ArcOfCircle CenterX=-184.801 CenterY=-67.3089 CenterZ=0 NormalX=0 NormalY=0 NormalZ=1 AngleXU=0 Radius=33.7833 StartAngle=2.70526 EndAngle=3.54053
    g2: LineSegment StartX=-176.685 StartY=-80.4316 StartZ=0 EndX=-215.932 EndY=-80.4316 EndZ=0
    g3: LineSegment StartX=-215.42 StartY=-53.0315 StartZ=0 EndX=-192.176 EndY=-3.18454 EndZ=0
    g4: ArcOfCircle CenterX=-207.583 CenterY=4 CenterZ=0 NormalX=0 NormalY=0 NormalZ=1 AngleXU=0 Radius=17 StartAngle=5.84685 EndAngle=7.56663
    g5: Circle CenterX=-213.443 CenterY=-76.8316 CenterZ=0 NormalX=0 NormalY=0 NormalZ=1 AngleXU=0 Radius=3
    g6: Circle CenterX=-179.305 CenterY=-76.8316 CenterZ=0 NormalX=0 NormalY=0 NormalZ=1 AngleXU=0 Radius=3
    g7: LineSegment StartX=-143.955 StartY=20.303 StartZ=0 EndX=-176.685 EndY=-80.4316 EndZ=0
  constraints (18):
    c: Coincident(g0,g-6)
    c: Coincident(g1,g-7)
    c: Coincident(g1,g-8)
    c: Coincident(g2,g1)
    c: Tangent(g3,g-5)
    c: Coincident(g4,g-6)
    c: Coincident(g4,g0)
    c: Coincident(g3,g4)
    c: Coincident(g1,g3)
    c: Diameter(g5) = 6
    c: Diameter(g6) = 6
    c: Coincident(g5,g-9)
    c: Coincident(g6,g-10)
    c: Horizontal(g0)
    c: Horizontal(g2)
    c: Coincident(g7,g0)
    c: Coincident(g7,g2)
    c: Tangent(g7,g-4)
FEATURE [Sketcher::SketchObject] Sketch123
  ArcFitTolerance = 1e-06
  AttachmentSupport = -> [Pad011]
  ExternalGeometry = -> [Binder001]
  FullyConstrained = true
  MakeInternals = false
  MapMode = 5
  Placement = pos=(0,-2,0) rot=(1,0,0;1.5708rad)
  sketch-geometry (4):
    g0: LineSegment StartX=-108 StartY=36.8 StartZ=0 EndX=-90 EndY=36.8 EndZ=0
    g1: LineSegment StartX=-108 StartY=36.8 StartZ=0 EndX=-108 EndY=26.8 EndZ=0
    g2: LineSegment StartX=-108 StartY=26.8 StartZ=0 EndX=-90 EndY=26.8 EndZ=0
    g3: ArcOfCircle CenterX=-94 CenterY=31.8 CenterZ=0 NormalX=0 NormalY=0 NormalZ=1 AngleXU=0 Radius=6.40312 StartAngle=5.38713 EndAngle=7.17924
  constraints (13):
    c: Horizontal(g0)
    c: Coincident(g1,g0)
    c: Vertical(g1)
    c: Coincident(g2,g1)
    c: Horizontal(g2)
    c: DistanceX(g0,g0) = 18
    c: DistanceY(g1,g1) = 10
    c: Equal(g0,g2)
    c: DistanceX(g0,g-3) = 90
    c: DistanceY(g0,g-3) = 2.4
    c: Coincident(g3,g0)
    c: Coincident(g3,g2)
    c: DistanceX(g3,g0) = 4
FEATURE [PartDesign::Chamfer] Chamfer014
  Angle = 45
  Base = -> Pad011 [Edge80,Edge4,Edge7]
  BaseFeature = -> Pad011
  ChamferType = 0
  FlipDirection = false
  Refine = true
  Size = 1.9
  Size2 = 1
  SupportTransform = false
  Suppressed = false
  UseAllEdges = false
FEATURE [PartDesign::Pocket] Pocket006
  BaseFeature = -> Chamfer014
  Direction = (0,-1,2e-16)
  Length = 1.2
  Length2 = 5
  Profile = -> Sketch115
  ReferenceAxis = -> Sketch115 [N_Axis]
  Refine = true
  Suppressed = false
  Type = 0
FEATURE [Sketcher::SketchObject] Sketch116  label="Sketch116 - pieno per inserto M3 x 3 x 4,5"
  ArcFitTolerance = 1e-06
  AttachmentSupport = -> [Pocket006]
  ExternalGeometry = -> [Binder001]
  FullyConstrained = true
  MakeInternals = false
  MapMode = 5
  Placement = pos=(0,1.7e-15,0) rot=(0,0.707107,0.707107;3.14159rad)
  sketch-geometry (4):
    g0: Circle CenterX=43.2 CenterY=30.3 CenterZ=0 NormalX=0 NormalY=0 NormalZ=1 AngleXU=0 Radius=3.4
    g1: Circle CenterX=43.2 CenterY=12.1 CenterZ=0 NormalX=0 NormalY=0 NormalZ=1 AngleXU=0 Radius=3.4
    g2: Circle CenterX=18.6 CenterY=30.3 CenterZ=0 NormalX=0 NormalY=0 NormalZ=1 AngleXU=0 Radius=3.4
    g3: Circle CenterX=18.6 CenterY=12.1 CenterZ=0 NormalX=0 NormalY=0 NormalZ=1 AngleXU=0 Radius=3.4
  constraints (8):
    c: Diameter(g0) = 6.8
    c: Diameter(g1) = 6.8
    c: Diameter(g2) = 6.8
    c: Diameter(g3) = 6.8
    c: Coincident(g2,g-3)
    c: Coincident(g0,g-4)
    c: Coincident(g3,g-6)
    c: Coincident(g1,g-5)
FEATURE [PartDesign::Pad] Pad012
  BaseFeature = -> Pocket006
  Direction = (0,1,-2e-16)
  Length = 2.4
  Length2 = 10
  Profile = -> Sketch116
  ReferenceAxis = -> Sketch116 [N_Axis]
  Refine = true
  Suppressed = false
  Type = 0
FEATURE [PartDesign::Pocket] Pocket007
  BaseFeature = -> Pad012
  Direction = (0,-1,2e-16)
  Length = 0.6
  Length2 = 2.4
  Profile = -> Sketch117
  ReferenceAxis = -> Sketch117 [N_Axis]
  Refine = true
  Suppressed = false
  Type = 4
FEATURE [PartDesign::Pad] Pad013
  BaseFeature = -> Pocket007
  Direction = (0,-1,2e-16)
  Length = 1.6
  Length2 = 10
  Profile = -> Sketch118
  ReferenceAxis = -> Sketch118 [N_Axis]
  Refine = true
  Suppressed = false
  Type = 0
FEATURE [Sketcher::SketchObject] Sketch119
  ArcFitTolerance = 1e-06
  AttachmentSupport = -> [Pad013]
  ExternalGeometry = -> [Binder001]
  FullyConstrained = true
  MakeInternals = false
  MapMode = 5
  Placement = pos=(0,-3.6,0) rot=(1,0,0;1.5708rad)
  sketch-geometry (21):
    g0: LineSegment [constr] StartX=-82.8 StartY=3.2 StartZ=0 EndX=-82.8 EndY=39.2 EndZ=0
    g1: ArcOfCircle CenterX=-78.51 CenterY=34.8 CenterZ=0 NormalX=0 NormalY=0 NormalZ=1 AngleXU=0 Radius=3.5 StartAngle=4.71239 EndAngle=6.28319
    g2: ArcOfCircle CenterX=-78.51 CenterY=7.6 CenterZ=0 NormalX=0 NormalY=0 NormalZ=1 AngleXU=0 Radius=3.5 StartAngle=0 EndAngle=1.5708
    g3: ArcOfCircle CenterX=-5.6 CenterY=34.8 CenterZ=0 NormalX=0 NormalY=0 NormalZ=1 AngleXU=0 Radius=3.5 StartAngle=3.14159 EndAngle=4.71239
    g4: ArcOfCircle CenterX=-5.6 CenterY=7.6 CenterZ=0 NormalX=0 NormalY=0 NormalZ=1 AngleXU=0 Radius=3.5 StartAngle=1.5708 EndAngle=3.14159
    g5: LineSegment StartX=0 StartY=39.2 StartZ=0 EndX=0 EndY=31.3 EndZ=0
    g6: LineSegment StartX=0 StartY=39.2 StartZ=0 EndX=-9.1 EndY=39.2 EndZ=0
    g7: LineSegment StartX=0 StartY=3.2 StartZ=0 EndX=0 EndY=11.1 EndZ=0
    g8: LineSegment StartX=0 StartY=3.2 StartZ=0 EndX=-9.1 EndY=3.2 EndZ=0
    g9: LineSegment StartX=-82.8 StartY=3.2 StartZ=0 EndX=-75.01 EndY=3.2 EndZ=0
    g10: LineSegment StartX=-82.8 StartY=3.2 StartZ=0 EndX=-82.8 EndY=11.1 EndZ=0
    g11: LineSegment StartX=-82.8 StartY=39.2 StartZ=0 EndX=-82.8 EndY=31.3 EndZ=0
    g12: LineSegment StartX=-82.8 StartY=39.2 StartZ=0 EndX=-75.01 EndY=39.2 EndZ=0
    g13: LineSegment StartX=-82.8 StartY=31.3 StartZ=0 EndX=-78.51 EndY=31.3 EndZ=0
    g14: LineSegment StartX=-75.01 StartY=39.2 StartZ=0 EndX=-75.01 EndY=34.8 EndZ=0
    g15: LineSegment StartX=-82.8 StartY=11.1 StartZ=0 EndX=-78.51 EndY=11.1 EndZ=0
    g16: LineSegment StartX=-75.01 StartY=3.2 StartZ=0 EndX=-75.01 EndY=7.6 EndZ=0
    g17: LineSegment StartX=-9.1 StartY=39.2 StartZ=0 EndX=-9.1 EndY=34.8 EndZ=0
    g18: LineSegment StartX=0 StartY=31.3 StartZ=0 EndX=-5.6 EndY=31.3 EndZ=0
    g19: LineSegment StartX=0 StartY=11.1 StartZ=0 EndX=-5.6 EndY=11.1 EndZ=0
    g20: LineSegment StartX=-9.1 StartY=3.2 StartZ=0 EndX=-9.1 EndY=7.6 EndZ=0
  constraints (51):
    c: Coincident(g0,g-10)
    c: PointOnObject(g0,g-8)
    c: Vertical(g0)
    c: Coincident(g1,g-3)
    c: Coincident(g2,g-4)
    c: Coincident(g3,g-5)
    c: Coincident(g4,g-6)
    c: Radius(g4) = 3.5
    c: Radius(g3) = 3.5
    c: Radius(g1) = 3.5
    c: Radius(g2) = 3.5
    c: Coincident(g5,g-9)
    c: PointOnObject(g5,g-9)
    c: Coincident(g6,g5)
    c: PointOnObject(g6,g-8)
    c: Coincident(g7,g-9)
    c: PointOnObject(g7,g-9)
    c: Coincident(g8,g7)
    c: PointOnObject(g8,g-7)
    c: Coincident(g9,g0)
    c: PointOnObject(g9,g-7)
    c: Coincident(g10,g0)
    c: PointOnObject(g10,g0)
    c: Coincident(g11,g0)
    c: PointOnObject(g11,g0)
    c: Coincident(g12,g0)
    c: PointOnObject(g12,g-8)
    c: Coincident(g13,g11)
    c: Horizontal(g13)
    c: Coincident(g14,g12)
    c: Vertical(g14)
    c: Coincident(g15,g10)
    c: Horizontal(g15)
    c: Coincident(g16,g9)
    c: Vertical(g16)
    c: Coincident(g17,g6)
    c: Vertical(g17)
    c: Coincident(g18,g5)
    c: Horizontal(g18)
    c: Coincident(g19,g7)
    c: Horizontal(g19)
    c: Coincident(g20,g8)
    c: Vertical(g20)
    c: Tangent(g20,g4) = 1.5708
    c: Tangent(g4,g19) = -1.5708
    c: Tangent(g18,g3) = 1.5708
    c: Tangent(g3,g17) = -1.5708
    c: Tangent(g13,g1) = -1.5708
    c: Tangent(g1,g14) = 1.5708
    c: Tangent(g16,g2) = -1.5708
    c: Tangent(g2,g15) = 1.5708
FEATURE [PartDesign::Pocket] Pocket008
  BaseFeature = -> Pad013
  Direction = (0,1,-2e-16)
  Length = 1.6
  Length2 = 5
  Profile = -> Sketch119
  ReferenceAxis = -> Sketch119 [N_Axis]
  Refine = true
  Suppressed = false
  Type = 0
FEATURE [PartDesign::Pad] Pad017
  BaseFeature = -> Pocket008
  Direction = (0,-1,2e-16)
  Length = 1.6
  Length2 = 10
  Profile = -> Sketch123
  ReferenceAxis = -> Sketch123 [N_Axis]
  Refine = true
  Suppressed = false
  Type = 0
FEATURE [Sketcher::SketchObject] Sketch125
  ArcFitTolerance = 1e-06
  AttachmentSupport = -> [Pad017]
  ExternalGeometry = -> [Pad017]
  FullyConstrained = true
  MakeInternals = false
  MapMode = 5
  Placement = pos=(0,-3.6,8e-16) rot=(1,0,0;1.5708rad)
  sketch-geometry (20):
    g0: LineSegment StartX=-108 StartY=35.8 StartZ=0 EndX=-108 EndY=35 EndZ=0
    g1: LineSegment StartX=-108 StartY=35 StartZ=0 EndX=-97 EndY=35 EndZ=0
    g2: LineSegment StartX=-97 StartY=35 StartZ=0 EndX=-97 EndY=35.8 EndZ=0
    g3: LineSegment StartX=-97 StartY=35.8 StartZ=0 EndX=-108 EndY=35.8 EndZ=0
    g4: LineSegment StartX=-108 StartY=28.6 StartZ=0 EndX=-108 EndY=27.8 EndZ=0
    g5: LineSegment StartX=-108 StartY=27.8 StartZ=0 EndX=-97 EndY=27.8 EndZ=0
    g6: LineSegment StartX=-97 StartY=27.8 StartZ=0 EndX=-97 EndY=28.6 EndZ=0
    g7: LineSegment StartX=-97 StartY=28.6 StartZ=0 EndX=-108 EndY=28.6 EndZ=0
    g8: LineSegment StartX=-108 StartY=30.4 StartZ=0 EndX=-108 EndY=29.6 EndZ=0
    g9: LineSegment StartX=-108 StartY=29.6 StartZ=0 EndX=-97 EndY=29.6 EndZ=0
    g10: LineSegment StartX=-97 StartY=29.6 StartZ=0 EndX=-97 EndY=30.4 EndZ=0
    g11: LineSegment StartX=-97 StartY=30.4 StartZ=0 EndX=-108 EndY=30.4 EndZ=0
    g12: LineSegment StartX=-108 StartY=32.2 StartZ=0 EndX=-108 EndY=31.4 EndZ=0
    g13: LineSegment StartX=-108 StartY=31.4 StartZ=0 EndX=-97 EndY=31.4 EndZ=0
    g14: LineSegment StartX=-97 StartY=31.4 StartZ=0 EndX=-97 EndY=32.2 EndZ=0
    g15: LineSegment StartX=-97 StartY=32.2 StartZ=0 EndX=-108 EndY=32.2 EndZ=0
    g16: LineSegment StartX=-108 StartY=34 StartZ=0 EndX=-108 EndY=33.2 EndZ=0
    g17: LineSegment StartX=-108 StartY=33.2 StartZ=0 EndX=-97 EndY=33.2 EndZ=0
    g18: LineSegment StartX=-97 StartY=33.2 StartZ=0 EndX=-97 EndY=34 EndZ=0
    g19: LineSegment StartX=-97 StartY=34 StartZ=0 EndX=-108 EndY=34 EndZ=0
  constraints (55):
    c: Coincident(g1,g0)
    c: Horizontal(g1)
    c: Coincident(g2,g1)
    c: Vertical(g2)
    c: Coincident(g3,g2)
    c: Horizontal(g3)
    c: Coincident(g3,g0)
    c: DistanceX(g1,g1) = 11
    c: DistanceY(g2,g2) = 0.8
    c: Coincident(g5,g4)
    c: Horizontal(g5)
    c: Coincident(g6,g5)
    c: Vertical(g6)
    c: Coincident(g7,g6)
    c: Horizontal(g7)
    c: Coincident(g7,g4)
    c: Coincident(g9,g8)
    c: Horizontal(g9)
    c: Coincident(g10,g9)
    c: Vertical(g10)
    c: Coincident(g11,g10)
    c: Horizontal(g11)
    c: Coincident(g11,g8)
    c: Coincident(g13,g12)
    c: Horizontal(g13)
    c: Coincident(g14,g13)
    c: Vertical(g14)
    c: Coincident(g15,g14)
    c: Horizontal(g15)
    c: Coincident(g15,g12)
    c: Coincident(g17,g16)
    c: Horizontal(g17)
    c: Coincident(g18,g17)
    c: Vertical(g18)
    c: Coincident(g19,g18)
    c: Horizontal(g19)
    c: Coincident(g19,g16)
    c: Equal(g3,g19)
    c: Equal(g3,g15)
    c: Equal(g3,g11)
    c: Equal(g3,g7)
    c: Equal(g2,g18)
    c: Equal(g2,g14)
    c: Equal(g2,g10)
    c: Equal(g2,g6)
    c: DistanceY(g-4,g4) = 1
    c: DistanceY(g4,g8) = 1
    c: DistanceY(g8,g12) = 1
    c: DistanceY(g12,g16) = 1
    c: DistanceY(g16,g0) = 1
    c: Tangent(g0,g-5)
    c: Tangent(g16,g-5)
    c: Tangent(g12,g-5)
    c: Tangent(g8,g-5)
    c: Tangent(g4,g-5)
FEATURE [PartDesign::Chamfer] Chamfer009
  Angle = 45
  Base = -> Pad017 [Edge151,Edge154]
  BaseFeature = -> Pad017
  ChamferType = 1
  FlipDirection = false
  Refine = true
  Size = 1.5
  Size2 = 2.8
  SupportTransform = false
  Suppressed = false
  UseAllEdges = false
FEATURE [PartDesign::Pocket] Pocket009
  BaseFeature = -> Chamfer009
  Direction = (0,1,-2e-16)
  Length = 1
  Length2 = 5
  Profile = -> Sketch125
  ReferenceAxis = -> Sketch125 [N_Axis]
  Refine = true
  Suppressed = false
  Type = 0
FEATURE [PartDesign::Pad] Pad014
  BaseFeature = -> Pocket009
  Direction = (0,-1,2e-16)
  Length = 0.8
  Length2 = 10
  Profile = -> Sketch120
  ReferenceAxis = -> Sketch120 [N_Axis]
  Refine = true
  Suppressed = false
  Type = 0
FEATURE [Sketcher::SketchObject] Sketch124
  ArcFitTolerance = 1e-06
  AttachmentSupport = -> [Pad014]
  ExternalGeometry = -> [Binder001]
  FullyConstrained = true
  MakeInternals = false
  MapMode = 5
  Placement = pos=(0,-2.8,6e-16) rot=(1,0,0;1.5708rad)
  sketch-geometry (4):
    g0: LineSegment StartX=-129 StartY=39.2 StartZ=0 EndX=-131.599 EndY=31.2 EndZ=0
    g1: LineSegment StartX=-118 StartY=39.2 StartZ=0 EndX=-120.599 EndY=31.2 EndZ=0
    g2: LineSegment StartX=-129 StartY=39.2 StartZ=0 EndX=-118 EndY=39.2 EndZ=0
    g3: LineSegment StartX=-120.599 StartY=31.2 StartZ=0 EndX=-131.599 EndY=31.2 EndZ=0
  constraints (12):
    c: PointOnObject(g0,g-3)
    c: PointOnObject(g1,g-3)
    c: Parallel(g-4,g0)
    c: Parallel(g-4,g1)
    c: Coincident(g2,g0)
    c: Coincident(g2,g1)
    c: DistanceX(g2,g2) = 11
    c: DistanceY(g1,g1) = 8
    c: Coincident(g3,g1)
    c: Horizontal(g3)
    c: Coincident(g3,g0)
    c: DistanceX(g1,g-3) = 118
FEATURE [PartDesign::Pad] Pad018
  BaseFeature = -> Pad014
  Direction = (0,-1,2e-16)
  Length = 1.2
  Length2 = 10
  Profile = -> Sketch124
  ReferenceAxis = -> Sketch124 [N_Axis]
  Refine = true
  Suppressed = false
  Type = 0
FEATURE [Sketcher::SketchObject] Sketch126
  ArcFitTolerance = 1e-06
  AttachmentSupport = -> [Pad018]
  ExternalGeometry = -> [Pad018]
  FullyConstrained = true
  MakeInternals = false
  MapMode = 5
  Placement = pos=(0,-4,0) rot=(1,0,0;1.5708rad)
  sketch-geometry (8):
    g0: LineSegment StartX=-129.877 StartY=36.5 StartZ=0 EndX=-130.137 EndY=35.7 EndZ=0
    g1: LineSegment StartX=-130.69 StartY=34 StartZ=0 EndX=-130.95 EndY=33.2 EndZ=0
    g2: LineSegment StartX=-129.877 StartY=36.5 StartZ=0 EndX=-118.877 EndY=36.5 EndZ=0
    g3: LineSegment StartX=-130.137 StartY=35.7 StartZ=0 EndX=-119.137 EndY=35.7 EndZ=0
    g4: LineSegment StartX=-130.69 StartY=34 StartZ=0 EndX=-119.69 EndY=34 EndZ=0
    g5: LineSegment StartX=-130.95 StartY=33.2 StartZ=0 EndX=-119.95 EndY=33.2 EndZ=0
    g6: LineSegment StartX=-118.877 StartY=36.5 StartZ=0 EndX=-119.137 EndY=35.7 EndZ=0
    g7: LineSegment StartX=-119.69 StartY=34 StartZ=0 EndX=-119.95 EndY=33.2 EndZ=0
  constraints (20):
    c: Coincident(g2,g0)
    c: Horizontal(g2)
    c: Coincident(g3,g0)
    c: Horizontal(g3)
    c: Coincident(g4,g1)
    c: Horizontal(g4)
    c: Coincident(g5,g1)
    c: Horizontal(g5)
    c: Coincident(g6,g2)
    c: Coincident(g6,g3)
    c: Coincident(g7,g4)
    c: Coincident(g7,g5)
    c: Tangent(g0,g-4)
    c: Tangent(g6,g-5)
    c: Tangent(g1,g-4)
    c: Tangent(g7,g-5)
    c: DistanceY(g3,g2) = 0.8
    c: DistanceY(g5,g4) = 0.8
    c: DistanceY(g-6,g1) = 2
    c: DistanceY(g-6,g0) = 4.5
FEATURE [PartDesign::Chamfer] Chamfer008
  Angle = 45
  Base = -> Pad018 [Edge257]
  BaseFeature = -> Pad018
  ChamferType = 1
  FlipDirection = false
  Refine = true
  Size = 1
  Size2 = 6
  SupportTransform = false
  Suppressed = false
  UseAllEdges = false
FEATURE [PartDesign::Pocket] Pocket010
  BaseFeature = -> Chamfer008
  Direction = (0,1,-2e-16)
  Length = 1
  Length2 = 5
  Profile = -> Sketch126
  ReferenceAxis = -> Sketch126 [N_Axis]
  Refine = true
  Suppressed = false
  Type = 0
FEATURE [PartDesign::Pad] Pad015
  BaseFeature = -> Pocket010
  Direction = (0,-1,2e-16)
  Length = 2
  Length2 = 10
  Profile = -> Sketch121
  ReferenceAxis = -> Sketch121 [N_Axis]
  Refine = true
  Suppressed = false
  Type = 0
FEATURE [PartDesign::Pad] Pad016
  BaseFeature = -> Pad015
  Direction = (0,-1,2e-16)
  Length = 1.6
  Length2 = 10
  Profile = -> Sketch122
  ReferenceAxis = -> Sketch122 [N_Axis]
  Refine = true
  Suppressed = false
  Type = 0
FEATURE [Sketcher::SketchObject] Sketch129
  ArcFitTolerance = 1e-06
  AttachmentSupport = -> [Pad016]
  ExternalGeometry = -> [Binder001]
  FullyConstrained = true
  MakeInternals = false
  MapMode = 5
  Placement = pos=(0,-3.6,0) rot=(1,0,0;1.5708rad)
  sketch-geometry (12):
    g0: LineSegment [constr] StartX=-192.176 StartY=-3.18451 StartZ=0 EndX=-181.223 EndY=20.303 EndZ=0
    g1: LineSegment [constr] StartX=-202.765 StartY=20.303 StartZ=0 EndX=-181.223 EndY=20.303 EndZ=0
    g2: LineSegment StartX=-202.765 StartY=20.303 StartZ=0 EndX=-181.223 EndY=20.303 EndZ=0
    g3: LineSegment StartX=-192.176 StartY=-3.18451 StartZ=0 EndX=-196.804 EndY=-13.1107 EndZ=0
    g4: ArcOfCircle CenterX=-207.583 CenterY=4 CenterZ=0 NormalX=0 NormalY=0 NormalZ=1 AngleXU=0 Radius=17 StartAngle=5.84685 EndAngle=7.56663
    g5: ArcOfEllipse CenterX=-181.223 CenterY=8.55923 CenterZ=0 NormalX=0 NormalY=0 NormalZ=1 MajorRadius=23.4779 MinorRadius=11.7437 AngleXU=2e-16 StartAngle=4.71239 EndAngle=7.85398
    g6: LineSegment [constr] StartX=-157.745 StartY=8.55923 StartZ=0 EndX=-204.701 EndY=8.55923 EndZ=0
    g7: LineSegment [constr] StartX=-181.223 StartY=20.303 StartZ=0 EndX=-181.223 EndY=-3.18451 EndZ=0
    g8: GeomPoint [constr] X=-160.894 Y=8.55923 Z=0
    g9: GeomPoint [constr] X=-201.553 Y=8.55923 Z=0
    g10: ArcOfCircle CenterX=-181.223 CenterY=-20.3763 CenterZ=0 NormalX=0 NormalY=0 NormalZ=1 AngleXU=0 Radius=17.1918 StartAngle=1.57079 EndAngle=2.70526
    g11: GeomPoint [constr] X=-181.223 Y=-3.18451 Z=0
  constraints (23):
    c: Coincident(g0,g-5)
    c: Coincident(g1,g-6)
    c: Horizontal(g1)
    c: Coincident(g1,g0)
    c: Parallel(g0,g-4)
    c: Coincident(g2,g1)
    c: Coincident(g2,g0)
    c: Coincident(g3,g0)
    c: Equal(g4,g-5)
    c: Coincident(g4,g1)
    c: Coincident(g4,g0)
    c: InternalAlignment(g6-g9 -> g5) x4
    c: Vertical(g5,g0)
    c: Horizontal(g6)
    c: Coincident(g5,g0)
    c: DistanceX(g6,g-3) = 10.1
    c: Tangent(g10,g3) = -1.5708
    c: PointOnObject(g11,g10)
    c: Tangent(g5,g10,g11) = 1.5708
    c: Coincident(g10,g5)
    c: Coincident(g11,g7)
    c: Parallel(g3,g-4)
    c: Horizontal(g5,g0)
FEATURE [Sketcher::SketchObject] Sketch130
  ArcFitTolerance = 1e-06
  AttachmentOffset = pos=(0,0,-1.6) rot=(0,0,1;0rad)
  AttachmentSupport = -> [Pad016]
  ExternalGeometry = -> [Binder001]
  FullyConstrained = true
  MakeInternals = false
  MapMode = 5
  Placement = pos=(0,-2,-4e-16) rot=(1,0,0;1.5708rad)
  sketch-geometry (12):
    g0: LineSegment [constr] StartX=-192.176 StartY=-3.18451 StartZ=0 EndX=-181.223 EndY=20.303 EndZ=0
    g1: LineSegment [constr] StartX=-202.765 StartY=20.303 StartZ=0 EndX=-181.223 EndY=20.303 EndZ=0
    g2: LineSegment StartX=-202.765 StartY=20.303 StartZ=0 EndX=-181.223 EndY=20.303 EndZ=0
    g3: LineSegment StartX=-192.176 StartY=-3.18451 StartZ=0 EndX=-193.827 EndY=-6.72678 EndZ=0
    g4: ArcOfCircle CenterX=-207.583 CenterY=4 CenterZ=0 NormalX=0 NormalY=0 NormalZ=1 AngleXU=0 Radius=17 StartAngle=5.84685 EndAngle=7.56663
    g5: ArcOfEllipse CenterX=-181.223 CenterY=10.803 CenterZ=0 NormalX=0 NormalY=0 NormalZ=1 MajorRadius=14.4779 MinorRadius=9.5 AngleXU=0 StartAngle=4.71239 EndAngle=7.85398
    g6: LineSegment [constr] StartX=-166.745 StartY=10.803 StartZ=0 EndX=-195.701 EndY=10.803 EndZ=0
    g7: LineSegment [constr] StartX=-181.223 StartY=20.303 StartZ=0 EndX=-181.223 EndY=1.30297 EndZ=0
    g8: GeomPoint [constr] X=-170.298 Y=10.803 Z=0
    g9: GeomPoint [constr] X=-192.148 Y=10.803 Z=0
    g10: ArcOfCircle CenterX=-181.223 CenterY=-12.6042 CenterZ=0 NormalX=0 NormalY=0 NormalZ=1 AngleXU=0 Radius=13.9072 StartAngle=1.5708 EndAngle=2.70526
    g11: GeomPoint [constr] X=-181.223 Y=1.30297 Z=0
  constraints (23):
    c: Coincident(g0,g-5)
    c: Coincident(g1,g-6)
    c: Horizontal(g1)
    c: Coincident(g1,g0)
    c: Parallel(g0,g-4)
    c: Coincident(g2,g1)
    c: Coincident(g2,g0)
    c: Coincident(g3,g0)
    c: Equal(g4,g-5)
    c: Coincident(g4,g1)
    c: Coincident(g4,g0)
    c: InternalAlignment(g6-g9 -> g5) x4
    c: Vertical(g5,g0)
    c: Horizontal(g6)
    c: Coincident(g5,g0)
    c: DistanceX(g6,g-3) = 19.1
    c: Tangent(g10,g3) = -1.5708
    c: PointOnObject(g11,g10)
    c: Tangent(g5,g10,g11) = 1.5708
    c: Coincident(g10,g5)
    c: Coincident(g11,g7)
    c: Parallel(g3,g-4)
    c: DistanceY(g5,g0) = 19
FEATURE [Part::Part2DObjectPython] Clone2D001  label="Sketch130 (2D)"  # Draft 2D object (typed FeaturePython)
  Fuse = false
  Objects = -> [Sketch130]
  Placement = pos=(0,-2,-4e-16) rot=(1,0,0;1.5708rad)
  Scale = (1,1,1)
FEATURE [Sketcher::SketchObject] Sketch131
  ArcFitTolerance = 1e-06
  AttachmentOffset = pos=(0,0,-3.5) rot=(0,0,1;0rad)
  AttachmentSupport = -> [Pad016]
  ExternalGeometry = -> [Binder001]
  FullyConstrained = true
  MakeInternals = false
  MapMode = 5
  Placement = pos=(0,-0.1,-8e-16) rot=(1,0,0;1.5708rad)
  sketch-geometry (1):
    g0: GeomPoint X=-197.47 Y=8.55923 Z=0
  constraints (1):
    c: Symmetric(g-6,g-4,g0)
FEATURE [Sketcher::SketchObject] Sketch132
  ArcFitTolerance = 1e-06
  AttachmentSupport = -> [Pad016]
  ExternalGeometry = -> [Binder001]
  FullyConstrained = true
  MakeInternals = false
  MapMode = 5
  Placement = pos=(0,-3.6,0) rot=(1,0,0;1.5708rad)
  sketch-geometry (3):
    g0: LineSegment [constr] StartX=-215.42 StartY=-53.0314 StartZ=0 EndX=-167.782 EndY=-53.0314 EndZ=0
    g1: Circle CenterX=-191.282 CenterY=-53.0314 CenterZ=0 NormalX=0 NormalY=0 NormalZ=1 AngleXU=0 Radius=11.5
    g2: Circle CenterX=-191.282 CenterY=-53.0314 CenterZ=0 NormalX=0 NormalY=0 NormalZ=1 AngleXU=0 Radius=10.7
  constraints (8):
    c: Coincident(g0,g-3)
    c: PointOnObject(g0,g-4)
    c: Horizontal(g0)
    c: Diameter(g1) = 23
    c: PointOnObject(g1,g0)
    c: DistanceX(g1,g0) = 23.5
    c: Diameter(g2) = 21.4
    c: Coincident(g2,g1)
FEATURE [Part::Part2DObjectPython] ShapeString  # Draft 2D object (typed FeaturePython)
  FontFile = <path>
  Fuse = false
  Justification = 6
  JustificationReference = 0
  KeepLeftMargin = false
  MakeFace = true
  ObliqueAngle = 0
  Placement = pos=(-199,-3.6,-57.5) rot=(1,0,0;1.5708rad)
  ScaleToSize = true
  Size = 10
  String = AS
  Tracking = 0
FEATURE [Sketcher::SketchObject] Sketch133
  ArcFitTolerance = 1e-06
  AttachmentSupport = -> [Binder]
  ExternalGeometry = -> [Binder]
  FullyConstrained = true
  MakeInternals = false
  MapMode = 5
  Placement = pos=(0,9e-16,0) rot=(0,0.707107,0.707107;3.14159rad)
  sketch-geometry (30):
    g0: LineSegment StartX=0 StartY=39.2 StartZ=0 EndX=0 EndY=3.2 EndZ=0
    g1: LineSegment StartX=0 StartY=3.2 StartZ=0 EndX=82.8 EndY=3.2 EndZ=0
    g2: LineSegment StartX=82.8 StartY=3.2 StartZ=0 EndX=82.8 EndY=6.2 EndZ=0
    g3: LineSegment StartX=82.8 StartY=6.2 StartZ=0 EndX=91.752 EndY=6.2 EndZ=0
    g4: LineSegment StartX=0 StartY=39.2 StartZ=0 EndX=195.887 EndY=39.2 EndZ=0
    g5: LineSegment StartX=195.887 StartY=39.2 StartZ=0 EndX=202.765 EndY=20.303 EndZ=0
    g6: LineSegment StartX=192.333 StartY=24.9893 StartZ=0 EndX=196.467 EndY=26.4942 EndZ=0
    g7: LineSegment StartX=196.467 StartY=26.4942 StartZ=0 EndX=194.073 EndY=33.0721 EndZ=0
    g8: LineSegment StartX=194.073 StartY=33.0721 StartZ=0 EndX=189.939 EndY=31.5672 EndZ=0
    g9: LineSegment StartX=189.939 StartY=31.5672 StartZ=0 EndX=192.333 EndY=24.9893 EndZ=0
    g10: ArcOfCircle CenterX=107.6 CenterY=4 CenterZ=0 NormalX=0 NormalY=0 NormalZ=1 AngleXU=0 Radius=16 StartAngle=1.5708 EndAngle=3.00366
    g11: LineSegment StartX=107.6 StartY=20 StartZ=0 EndX=132.428 EndY=20 EndZ=0
    g12: ArcOfCircle [constr] CenterX=132.428 CenterY=4 CenterZ=0 NormalX=0 NormalY=0 NormalZ=1 AngleXU=0 Radius=16 StartAngle=0.314159 EndAngle=1.5708
    g13: LineSegment StartX=147.645 StartY=8.94427 StartZ=0 EndX=176.685 EndY=-80.4316 EndZ=0
    g14: LineSegment StartX=176.685 StartY=-80.4316 StartZ=0 EndX=215.932 EndY=-80.4316 EndZ=0
    g15: ArcOfCircle CenterX=207.583 CenterY=4 CenterZ=0 NormalX=0 NormalY=0 NormalZ=1 AngleXU=0 Radius=17 StartAngle=1.85815 EndAngle=3.57792
    g16: ArcOfCircle CenterX=184.801 CenterY=-67.3089 CenterZ=0 NormalX=0 NormalY=0 NormalZ=1 AngleXU=0 Radius=33.7833 StartAngle=5.88425 EndAngle=6.71952
    g17: LineSegment StartX=192.176 StartY=-3.18451 StartZ=0 EndX=215.42 EndY=-53.0314 EndZ=0
    g18: Circle CenterX=5.6 CenterY=34.8 CenterZ=0 NormalX=0 NormalY=0 NormalZ=1 AngleXU=0 Radius=1.8
    g19: Circle CenterX=5.6 CenterY=7.6 CenterZ=0 NormalX=0 NormalY=0 NormalZ=1 AngleXU=0 Radius=1.8
    g20: Circle CenterX=78.51 CenterY=34.8 CenterZ=0 NormalX=0 NormalY=0 NormalZ=1 AngleXU=0 Radius=1.8
    g21: Circle CenterX=78.51 CenterY=7.6 CenterZ=0 NormalX=0 NormalY=0 NormalZ=1 AngleXU=0 Radius=1.8
    g22: Circle CenterX=184.08 CenterY=34.8 CenterZ=0 NormalX=0 NormalY=0 NormalZ=1 AngleXU=0 Radius=1.8
    g23: Circle CenterX=179.305 CenterY=-76.8316 CenterZ=0 NormalX=0 NormalY=0 NormalZ=1 AngleXU=0 Radius=1.8
    g24: Circle CenterX=213.443 CenterY=-76.8316 CenterZ=0 NormalX=0 NormalY=0 NormalZ=1 AngleXU=0 Radius=1.8
    g25: Circle CenterX=19 CenterY=21.2 CenterZ=0 NormalX=0 NormalY=0 NormalZ=1 AngleXU=0 Radius=6.3
    g26: Circle CenterX=42 CenterY=21.2 CenterZ=0 NormalX=0 NormalY=0 NormalZ=1 AngleXU=0 Radius=6.3
    g27: Circle CenterX=65 CenterY=21.2 CenterZ=0 NormalX=0 NormalY=0 NormalZ=1 AngleXU=0 Radius=6.3
    g28: LineSegment StartX=132.428 StartY=20 StartZ=0 EndX=144.053 EndY=20 EndZ=0
    g29: LineSegment StartX=147.645 StartY=8.94427 StartZ=0 EndX=144.053 EndY=20 EndZ=0
  constraints (65):
    c: Coincident(g0,g-4)
    c: Coincident(g0,g-5)
    c: Coincident(g1,g0)
    c: Coincident(g1,g-6)
    c: Coincident(g2,g1)
    c: Coincident(g2,g-7)
    c: Coincident(g3,g2)
    c: Coincident(g3,g-8)
    c: Coincident(g4,g0)
    c: Coincident(g4,g-16)
    c: Coincident(g5,g4)
    c: Coincident(g5,g-16)
    c: Coincident(g6,g-20)
    c: Coincident(g6,g-21)
    c: Coincident(g7,g6)
    c: Coincident(g7,g-23)
    c: Coincident(g8,g7)
    c: Coincident(g8,g-22)
    c: Coincident(g9,g8)
    c: Coincident(g9,g6)
    c: Equal(g10,g-8)
    c: Coincident(g10,g3)
    c: Coincident(g10,g-9)
    c: Coincident(g11,g10)
    c: Coincident(g11,g-10)
    c: Equal(g12,g-10)
    c: Coincident(g12,g11)
    c: Coincident(g12,g-11)
    c: Coincident(g13,g12)
    c: Coincident(g13,g-12)
    c: Coincident(g14,g13)
    c: Coincident(g14,g-13)
    c: Equal(g15,g-15)
    c: Coincident(g15,g5)
    c: Coincident(g15,g-15)
    c: Equal(g16,g-13)
    c: Coincident(g16,g14)
    c: Coincident(g16,g-14)
    c: Coincident(g17,g15)
    c: Coincident(g17,g16)
    c: Equal(g18,g-28)
    c: Equal(g19,g-29)
    c: Equal(g20,g-26)
    c: Equal(g21,g-27)
    c: Equal(g22,g-17)
    c: Equal(g24,g-25)
    c: Equal(g23,g-24)
    c: Coincident(g23,g-24)
    c: Coincident(g24,g-25)
    c: Coincident(g22,g-17)
    c: Coincident(g20,g-26)
    c: Coincident(g21,g-27)
    c: Coincident(g18,g-28)
    c: Coincident(g19,g-29)
    c: Equal(g25,g-30)
    c: Equal(g26,g-31)
    c: Equal(g27,g-32)
    c: Coincident(g25,g-30)
    c: Coincident(g26,g-31)
    c: Coincident(g27,g-32)
    c: Parallel(g28,g11)
    c: Parallel(g29,g13)
    c: Coincident(g28,g11)
    c: Coincident(g29,g12)
    c: Coincident(g29,g28)
FEATURE [PartDesign::Pad] Pad019
  Direction = (0,1,-2e-16)
  Length = 2
  Length2 = 10
  Profile = -> Sketch133
  ReferenceAxis = -> Sketch133 [N_Axis]
  Refine = true
  Suppressed = false
  Type = 0
FEATURE [Sketcher::SketchObject] Sketch091  label="Sketch091 - forma anteriore"
  ArcFitTolerance = 1e-06
  AttachmentSupport = -> [Pad019]
  ExternalGeometry = -> [Binder]
  FullyConstrained = true
  MakeInternals = false
  MapMode = 5
  Placement = pos=(0,2,0) rot=(0,0.707107,0.707107;3.14159rad)
  sketch-geometry (12):
    g0: Circle CenterX=5.6 CenterY=34.8 CenterZ=0 NormalX=0 NormalY=0 NormalZ=1 AngleXU=0 Radius=1.8
    g1: Circle CenterX=5.6 CenterY=7.6 CenterZ=0 NormalX=0 NormalY=0 NormalZ=1 AngleXU=0 Radius=1.8
    g2: Circle CenterX=78.51 CenterY=34.8 CenterZ=0 NormalX=0 NormalY=0 NormalZ=1 AngleXU=0 Radius=1.8
    g3: Circle CenterX=78.51 CenterY=7.6 CenterZ=0 NormalX=0 NormalY=0 NormalZ=1 AngleXU=0 Radius=1.8
    g4: LineSegment StartX=0 StartY=39.2 StartZ=0 EndX=0 EndY=3.2 EndZ=0
    g5: LineSegment StartX=0 StartY=3.2 StartZ=0 EndX=82.8 EndY=3.2 EndZ=0
    g6: LineSegment StartX=82.8 StartY=3.2 StartZ=0 EndX=82.8 EndY=39.2 EndZ=0
    g7: LineSegment StartX=82.8 StartY=39.2 StartZ=0 EndX=0 EndY=39.2 EndZ=0
    g8: ArcOfCircle CenterX=19 CenterY=21.2 CenterZ=0 NormalX=0 NormalY=0 NormalZ=1 AngleXU=0 Radius=10 StartAngle=1.5708 EndAngle=4.71239
    g9: ArcOfCircle CenterX=65 CenterY=21.2 CenterZ=0 NormalX=0 NormalY=0 NormalZ=1 AngleXU=0 Radius=10 StartAngle=4.71239 EndAngle=7.85398
    g10: LineSegment StartX=19 StartY=31.2 StartZ=0 EndX=65 EndY=31.2 EndZ=0
    g11: LineSegment StartX=19 StartY=11.2 StartZ=0 EndX=65 EndY=11.2 EndZ=0
  constraints (25):
    c: Equal(g2,g-7)
    c: Equal(g3,g-8)
    c: Equal(g1,g-13)
    c: Equal(g0,g-12)
    c: Coincident(g0,g-12)
    c: Coincident(g1,g-13)
    c: Coincident(g3,g-8)
    c: Coincident(g2,g-7)
    c: Coincident(g4,g-4)
    c: Coincident(g4,g-5)
    c: Coincident(g5,g4)
    c: Coincident(g5,g-6)
    c: Coincident(g6,g5)
    c: PointOnObject(g6,g-3)
    c: Vertical(g6)
    c: Coincident(g7,g6)
    c: Coincident(g7,g4)
    c: Tangent(g8,g10) = 1.5708
    c: Tangent(g8,g11) = -1.5708
    c: Tangent(g9,g10) = 1.5708
    c: Tangent(g9,g11) = -1.5708
    c: Equal(g8,g9)
    c: Radius(g8) = 10
    c: Coincident(g8,g-11)
    c: Coincident(g9,g-9)
FEATURE [Sketcher::SketchObject] Sketch093  label="Sketch093 - scavi interni pulsanti"
  ArcFitTolerance = 1e-06
  AttachmentSupport = -> [Pad019]
  ExternalGeometry = -> [Binder]
  FullyConstrained = true
  MakeInternals = false
  MapMode = 5
  Placement = pos=(0,1.8e-15,0) rot=(1,0,0;1.5708rad)
  sketch-geometry (3):
    g0: Circle CenterX=-65 CenterY=21.2 CenterZ=0 NormalX=0 NormalY=0 NormalZ=1 AngleXU=0 Radius=7.3
    g1: Circle CenterX=-42 CenterY=21.2 CenterZ=0 NormalX=0 NormalY=0 NormalZ=1 AngleXU=0 Radius=7.3
    g2: Circle CenterX=-19 CenterY=21.2 CenterZ=0 NormalX=0 NormalY=0 NormalZ=1 AngleXU=0 Radius=7.3
  constraints (6):
    c: Coincident(g0,g-3)
    c: Coincident(g1,g-4)
    c: Coincident(g2,g-5)
    c: Diameter(g0) = 14.6
    c: Diameter(g1) = 14.6
    c: Diameter(g2) = 14.6
FEATURE [Sketcher::SketchObject] Sketch094  label="Sketch094 - forma centrale"
  ArcFitTolerance = 1e-06
  AttachmentSupport = -> [Pad019]
  ExternalGeometry = -> [Binder]
  FullyConstrained = true
  MakeInternals = false
  MapMode = 5
  Placement = pos=(0,2,0) rot=(0,0.707107,0.707107;3.14159rad)
  sketch-geometry (4):
    g0: LineSegment StartX=137.815 StartY=39.2 StartZ=0 EndX=142.655 EndY=24.303 EndZ=0
    g1: LineSegment StartX=110.815 StartY=24.303 StartZ=0 EndX=142.655 EndY=24.303 EndZ=0
    g2: LineSegment StartX=137.815 StartY=39.2 StartZ=0 EndX=110.815 EndY=39.2 EndZ=0
    g3: ArcOfCircle CenterX=92.2534 CenterY=31.7515 CenterZ=0 NormalX=0 NormalY=0 NormalZ=1 AngleXU=0 Radius=20 StartAngle=5.90156 EndAngle=6.66481
  constraints (12):
    c: PointOnObject(g0,g-3)
    c: Tangent(g0,g-5)
    c: Horizontal(g1)
    c: Coincident(g1,g0)
    c: Coincident(g2,g0)
    c: PointOnObject(g2,g-3)
    c: DistanceX(g2,g2) = 27
    c: Vertical(g1,g2)
    c: Coincident(g3,g2)
    c: Radius(g3) = 20
    c: Coincident(g3,g1)
    c: DistanceY(g-6,g0) = 4
FEATURE [Sketcher::SketchObject] Sketch095  label="Sketch095 - forma posteriore"
  ArcFitTolerance = 1e-06
  AttachmentSupport = -> [Pad019]
  ExternalGeometry = -> [Binder]
  FullyConstrained = true
  MakeInternals = false
  MapMode = 5
  Placement = pos=(0,2,0) rot=(0,0.707107,0.707107;3.14159rad)
  sketch-geometry (15):
    g0: LineSegment StartX=137.815 StartY=39.2 StartZ=0 EndX=143.955 EndY=20.303 EndZ=0
    g1: LineSegment StartX=143.955 StartY=20.303 StartZ=0 EndX=190.141 EndY=20.303 EndZ=0
    g2: ArcOfCircle CenterX=184.08 CenterY=34.8 CenterZ=0 NormalX=0 NormalY=0 NormalZ=1 AngleXU=0 Radius=3.5 StartAngle=3.49066 EndAngle=4.71239
    g3: LineSegment StartX=180.791 StartY=33.6029 StartZ=0 EndX=178.754 EndY=39.2 EndZ=0
    g4: LineSegment StartX=184.08 StartY=31.3 StartZ=0 EndX=186.139 EndY=31.3 EndZ=0
    g5: LineSegment StartX=190.141 StartY=20.303 StartZ=0 EndX=186.139 EndY=31.3 EndZ=0
    g6: LineSegment StartX=137.815 StartY=39.2 StartZ=0 EndX=156.815 EndY=39.2 EndZ=0
    g7: LineSegment StartX=178.754 StartY=39.2 StartZ=0 EndX=168.815 EndY=39.2 EndZ=0
    g8: LineSegment StartX=156.815 StartY=31.2 StartZ=0 EndX=168.815 EndY=31.2 EndZ=0
    g9: ArcOfCircle CenterX=176.411 CenterY=35.2 CenterZ=0 NormalX=0 NormalY=0 NormalZ=1 AngleXU=0 Radius=20 StartAngle=2.94023 EndAngle=3.34295
    g10: ArcOfCircle CenterX=188.411 CenterY=35.2 CenterZ=0 NormalX=0 NormalY=0 NormalZ=1 AngleXU=0 Radius=20 StartAngle=2.94023 EndAngle=3.34295
    g11: LineSegment StartX=157.815 StartY=39.2 StartZ=0 EndX=167.815 EndY=39.2 EndZ=0
    g12: LineSegment StartX=157.436 StartY=36.2 StartZ=0 EndX=167.436 EndY=36.2 EndZ=0
    g13: ArcOfCircle CenterX=177.411 CenterY=35.2 CenterZ=0 NormalX=0 NormalY=0 NormalZ=1 AngleXU=0 Radius=20 StartAngle=2.94023 EndAngle=3.09157
    g14: ArcOfCircle CenterX=187.411 CenterY=35.2 CenterZ=0 NormalX=0 NormalY=0 NormalZ=1 AngleXU=0 Radius=20 StartAngle=2.94023 EndAngle=3.09157
  constraints (46):
    c: PointOnObject(g0,g-3)
    c: Tangent(g0,g-6)
    c: Coincident(g1,g0)
    c: Horizontal(g1)
    c: Radius(g2) = 3.5
    c: Coincident(g2,g-5)
    c: PointOnObject(g3,g-3)
    c: Parallel(g3,g-4)
    c: Tangent(g3,g2) = 1.5708
    c: Horizontal(g4)
    c: Tangent(g4,g2) = -1.5708
    c: Coincident(g5,g1)
    c: Parallel(g5,g-4)
    c: Coincident(g5,g4)
    c: DistanceX(g4,g-8) = 3.8
    c: Coincident(g6,g0)
    c: PointOnObject(g6,g-3)
    c: Coincident(g7,g3)
    c: PointOnObject(g7,g-3)
    c: Horizontal(g8)
    c: DistanceX(g6,g7) = 12
    c: Vertical(g8,g6)
    c: Vertical(g7,g8)
    c: DistanceY(g8,g6) = 8
    c: Coincident(g9,g8)
    c: Coincident(g9,g6)
    c: Coincident(g10,g7)
    c: Coincident(g10,g8)
    c: Radius(g9) = 20
    c: Radius(g10) = 20
    c: PointOnObject(g11,g-3)
    c: PointOnObject(g11,g-3)
    c: DistanceX(g11,g11) = 10
    c: DistanceX(g6,g11) = 1
    c: Horizontal(g12)
    c: Equal(g12,g11)
    c: DistanceY(g12,g11) = 3
    c: Coincident(g13,g11)
    c: Coincident(g13,g12)
    c: Radius(g13) = 20
    c: Coincident(g14,g11)
    c: Coincident(g14,g12)
    c: Radius(g14) = 20
    c: DistanceX(g0,g6) = 19
    c: Horizontal(g9,g13)
    c: Horizontal(g0,g-4)
FEATURE [Sketcher::SketchObject] Sketch096  label="Sketch096 - forma impugnatura"
  ArcFitTolerance = 1e-06
  AttachmentSupport = -> [Pad019]
  ExternalGeometry = -> [Binder]
  FullyConstrained = true
  MakeInternals = false
  MapMode = 5
  Placement = pos=(0,2,0) rot=(0,0.707107,0.707107;3.14159rad)
  sketch-geometry (8):
    g0: LineSegment StartX=176.685 StartY=-80.4316 StartZ=0 EndX=143.955 EndY=20.303 EndZ=0
    g1: LineSegment StartX=176.685 StartY=-80.4316 StartZ=0 EndX=215.932 EndY=-80.4316 EndZ=0
    g2: Circle CenterX=179.305 CenterY=-76.8316 CenterZ=0 NormalX=0 NormalY=0 NormalZ=1 AngleXU=0 Radius=3
    g3: Circle CenterX=213.443 CenterY=-76.8316 CenterZ=0 NormalX=0 NormalY=0 NormalZ=1 AngleXU=0 Radius=3
    g4: LineSegment StartX=143.955 StartY=20.303 StartZ=0 EndX=202.765 EndY=20.303 EndZ=0
    g5: LineSegment StartX=215.42 StartY=-53.0314 StartZ=0 EndX=192.176 EndY=-3.18451 EndZ=0
    g6: ArcOfCircle CenterX=184.801 CenterY=-67.3089 CenterZ=0 NormalX=0 NormalY=0 NormalZ=1 AngleXU=0 Radius=33.7833 StartAngle=5.88425 EndAngle=6.71952
    g7: ArcOfCircle CenterX=207.583 CenterY=4 CenterZ=0 NormalX=0 NormalY=0 NormalZ=1 AngleXU=0 Radius=17 StartAngle=1.85815 EndAngle=3.57792
  constraints (19):
    c: Coincident(g0,g-4)
    c: PointOnObject(g0,g-3)
    c: Horizontal(g0,g-7)
    c: Coincident(g1,g0)
    c: Coincident(g1,g-5)
    c: Diameter(g2) = 6
    c: Diameter(g3) = 6
    c: Coincident(g2,g-9)
    c: Coincident(g3,g-10)
    c: Coincident(g4,g0)
    c: Coincident(g5,g-6)
    c: Coincident(g6,g1)
    c: Coincident(g6,g5)
    c: Equal(g-5,g6)
    c: Coincident(g5,g-7)
    c: Coincident(g4,g-7)
    c: Tangent(g7,g-7)
    c: Coincident(g7,g4)
    c: Coincident(g7,g5)
FEATURE [Sketcher::SketchObject] Sketch097
  ArcFitTolerance = 1e-06
  AttachmentSupport = -> [Pad019]
  ExternalGeometry = -> [Binder]
  FullyConstrained = true
  MakeInternals = false
  MapMode = 5
  Placement = pos=(0,2,0) rot=(0,0.707107,0.707107;3.14159rad)
  sketch-geometry (4):
    g0: LineSegment StartX=90 StartY=36.8 StartZ=0 EndX=108 EndY=36.8 EndZ=0
    g1: LineSegment StartX=108 StartY=36.8 StartZ=0 EndX=108 EndY=26.8 EndZ=0
    g2: LineSegment StartX=108 StartY=26.8 StartZ=0 EndX=90 EndY=26.8 EndZ=0
    g3: ArcOfCircle CenterX=94 CenterY=31.8 CenterZ=0 NormalX=0 NormalY=0 NormalZ=1 AngleXU=0 Radius=6.40312 StartAngle=2.24554 EndAngle=4.03765
  constraints (13):
    c: Horizontal(g0)
    c: Coincident(g1,g0)
    c: Vertical(g1)
    c: DistanceX(g0,g0) = 18
    c: DistanceY(g1,g1) = 10
    c: Coincident(g2,g1)
    c: Horizontal(g2)
    c: Equal(g2,g0)
    c: DistanceY(g0,g-3) = 2.4
    c: Coincident(g3,g0)
    c: Coincident(g3,g2)
    c: DistanceX(g2,g3) = 4
    c: DistanceX(g-3,g0) = 90
FEATURE [PartDesign::Chamfer] Chamfer015
  Angle = 45
  Base = -> Pad019 [Edge19,Edge22,Edge79]
  BaseFeature = -> Pad019
  ChamferType = 0
  FlipDirection = false
  Refine = true
  Size = 1.9
  Size2 = 1
  SupportTransform = false
  Suppressed = false
  UseAllEdges = false
FEATURE [PartDesign::Pocket] Pocket002
  BaseFeature = -> Chamfer015
  Direction = (0,1,-2e-16)
  Length = 1.2
  Length2 = 5
  Profile = -> Sketch093
  ReferenceAxis = -> Sketch093 [N_Axis]
  Refine = true
  Suppressed = false
  Type = 0
FEATURE [PartDesign::Pad] Pad005
  BaseFeature = -> Pocket002
  Direction = (0,1,-2e-16)
  Length = 1.6
  Length2 = 10
  Profile = -> Sketch091
  ReferenceAxis = -> Sketch091 [N_Axis]
  Refine = true
  Suppressed = false
  Type = 0
FEATURE [Sketcher::SketchObject] Sketch092  label="Sketch092 - scavi per viti anteriori"
  ArcFitTolerance = 1e-06
  AttachmentSupport = -> [Pad005]
  ExternalGeometry = -> [Binder]
  FullyConstrained = true
  MakeInternals = false
  MapMode = 5
  Placement = pos=(0,3.6,0) rot=(0,0.707107,0.707107;3.14159rad)
  sketch-geometry (20):
    g0: ArcOfCircle CenterX=5.6 CenterY=7.6 CenterZ=0 NormalX=0 NormalY=0 NormalZ=1 AngleXU=0 Radius=3.5 StartAngle=0 EndAngle=1.5708
    g1: ArcOfCircle CenterX=5.6 CenterY=34.8 CenterZ=0 NormalX=0 NormalY=0 NormalZ=1 AngleXU=0 Radius=3.5 StartAngle=4.71239 EndAngle=6.28319
    g2: ArcOfCircle CenterX=78.51 CenterY=34.8 CenterZ=0 NormalX=0 NormalY=0 NormalZ=1 AngleXU=0 Radius=3.5 StartAngle=3.14159 EndAngle=4.71239
    g3: ArcOfCircle CenterX=78.51 CenterY=7.6 CenterZ=0 NormalX=0 NormalY=0 NormalZ=1 AngleXU=0 Radius=3.5 StartAngle=1.5708 EndAngle=3.14159
    g4: LineSegment StartX=0 StartY=3.2 StartZ=0 EndX=0 EndY=11.1 EndZ=0
    g5: LineSegment StartX=0 StartY=11.1 StartZ=0 EndX=5.6 EndY=11.1 EndZ=0
    g6: LineSegment StartX=0 StartY=3.2 StartZ=0 EndX=9.1 EndY=3.2 EndZ=0
    g7: LineSegment StartX=9.1 StartY=3.2 StartZ=0 EndX=9.1 EndY=7.6 EndZ=0
    g8: LineSegment StartX=0 StartY=39.2 StartZ=0 EndX=0 EndY=31.3 EndZ=0
    g9: LineSegment StartX=0 StartY=31.3 StartZ=0 EndX=5.6 EndY=31.3 EndZ=0
    g10: LineSegment StartX=0 StartY=39.2 StartZ=0 EndX=9.1 EndY=39.2 EndZ=0
    g11: LineSegment StartX=9.1 StartY=39.2 StartZ=0 EndX=9.1 EndY=34.8 EndZ=0
    g12: LineSegment StartX=82.8 StartY=39.2 StartZ=0 EndX=75.01 EndY=39.2 EndZ=0
    g13: LineSegment StartX=82.8 StartY=39.2 StartZ=0 EndX=82.8 EndY=31.3 EndZ=0
    g14: LineSegment StartX=82.8 StartY=31.3 StartZ=0 EndX=78.51 EndY=31.3 EndZ=0
    g15: LineSegment StartX=82.8 StartY=3.2 StartZ=0 EndX=75.01 EndY=3.2 EndZ=0
    g16: LineSegment StartX=75.01 StartY=3.2 StartZ=0 EndX=75.01 EndY=7.6 EndZ=0
    g17: LineSegment StartX=82.8 StartY=3.2 StartZ=0 EndX=82.8 EndY=11.1 EndZ=0
    g18: LineSegment StartX=82.8 StartY=11.1 StartZ=0 EndX=78.51 EndY=11.1 EndZ=0
    g19: LineSegment StartX=75.01 StartY=39.2 StartZ=0 EndX=75.01 EndY=34.8 EndZ=0
  constraints (48):
    c: Radius(g0) = 3.5
    c: Coincident(g0,g-10)
    c: Radius(g1) = 3.5
    c: Coincident(g1,g-9)
    c: Radius(g2) = 3.5
    c: Coincident(g2,g-8)
    c: Radius(g3) = 3.5
    c: Coincident(g3,g-7)
    c: Coincident(g4,g-5)
    c: PointOnObject(g4,g-4)
    c: Coincident(g5,g4)
    c: Horizontal(g5)
    c: Coincident(g6,g4)
    c: PointOnObject(g6,g-5)
    c: Coincident(g7,g6)
    c: Vertical(g7)
    c: Coincident(g8,g-4)
    c: PointOnObject(g8,g-4)
    c: Coincident(g9,g8)
    c: Horizontal(g9)
    c: Coincident(g10,g8)
    c: PointOnObject(g10,g-3)
    c: Coincident(g11,g10)
    c: Vertical(g11)
    c: PointOnObject(g12,g-3)
    c: PointOnObject(g12,g-3)
    c: Coincident(g13,g12)
    c: Vertical(g13)
    c: Coincident(g14,g13)
    c: Horizontal(g14)
    c: Coincident(g15,g-6)
    c: PointOnObject(g15,g-5)
    c: Coincident(g16,g15)
    c: Vertical(g16)
    c: Coincident(g17,g15)
    c: Coincident(g18,g17)
    c: Horizontal(g18)
    c: Tangent(g3,g18) = -1.5708
    c: Tangent(g16,g3) = 1.5708
    c: Coincident(g19,g12)
    c: Vertical(g19)
    c: Tangent(g2,g19) = -1.5708
    c: Tangent(g2,g14) = 1.5708
    c: Tangent(g0,g7) = -1.5708
    c: Tangent(g0,g5) = 1.5708
    c: Tangent(g9,g1) = -1.5708
    c: Tangent(g1,g11) = 1.5708
    c: Tangent(g17,g13)
FEATURE [PartDesign::Pocket] Pocket001
  BaseFeature = -> Pad005
  Direction = (0,-1,2e-16)
  Length = 1.6
  Length2 = 5
  Profile = -> Sketch092
  ReferenceAxis = -> Sketch092 [N_Axis]
  Refine = true
  Suppressed = false
  Type = 0
FEATURE [PartDesign::Pad] Pad006
  BaseFeature = -> Pocket001
  Direction = (0,1,-2e-16)
  Length = 0.8
  Length2 = 10
  Profile = -> Sketch094
  ReferenceAxis = -> Sketch094 [N_Axis]
  Refine = true
  Suppressed = false
  Type = 0
FEATURE [PartDesign::Pad] Pad007
  BaseFeature = -> Pad006
  Direction = (0,1,-2e-16)
  Length = 2
  Length2 = 10
  Profile = -> Sketch095
  ReferenceAxis = -> Sketch095 [N_Axis]
  Refine = true
  Suppressed = false
  Type = 0
FEATURE [PartDesign::Pad] Pad008  label="Pad008 - forma impugnatura"
  BaseFeature = -> Pad007
  Direction = (0,1,-2e-16)
  Length = 1.6
  Length2 = 10
  Profile = -> Sketch096
  ReferenceAxis = -> Sketch096 [N_Axis]
  Refine = true
  Suppressed = false
  Type = 0
FEATURE [PartDesign::Pad] Pad009
  BaseFeature = -> Pad008
  Direction = (0,1,-2e-16)
  Length = 1.6
  Length2 = 10
  Profile = -> Sketch097
  ReferenceAxis = -> Sketch097 [N_Axis]
  Refine = true
  Suppressed = false
  Type = 0
FEATURE [Sketcher::SketchObject] Sketch098
  ArcFitTolerance = 1e-06
  AttachmentSupport = -> [Pad006]
  ExternalGeometry = -> [Binder]
  FullyConstrained = true
  MakeInternals = false
  MapMode = 5
  Placement = pos=(0,2.8,-7e-16) rot=(0,0.707107,0.707107;3.14159rad)
  sketch-geometry (4):
    g0: LineSegment StartX=118 StartY=39.2 StartZ=0 EndX=129 EndY=39.2 EndZ=0
    g1: LineSegment StartX=120.599 StartY=31.2 StartZ=0 EndX=131.599 EndY=31.2 EndZ=0
    g2: LineSegment StartX=129 StartY=39.2 StartZ=0 EndX=131.599 EndY=31.2 EndZ=0
    g3: LineSegment StartX=118 StartY=39.2 StartZ=0 EndX=120.599 EndY=31.2 EndZ=0
  constraints (12):
    c: PointOnObject(g0,g-3)
    c: PointOnObject(g0,g-3)
    c: DistanceX(g0,g0) = 11
    c: Horizontal(g1)
    c: Equal(g1,g0)
    c: Coincident(g2,g0)
    c: Coincident(g3,g0)
    c: Parallel(g-4,g2)
    c: Coincident(g1,g2)
    c: Coincident(g1,g3)
    c: DistanceY(g1,g0) = 8
    c: DistanceX(g-3,g0) = 118
FEATURE [Sketcher::SketchObject] Sketch099
  ArcFitTolerance = 1e-06
  AttachmentSupport = -> [Pad008]
  ExternalGeometry = -> [Binder]
  FullyConstrained = true
  MakeInternals = false
  MapMode = 5
  Placement = pos=(0,3.6,0) rot=(0,0.707107,0.707107;3.14159rad)
  sketch-geometry (13):
    g0: LineSegment StartX=192.176 StartY=-3.18451 StartZ=0 EndX=196.804 EndY=-13.1108 EndZ=0
    g1: LineSegment [constr] StartX=202.765 StartY=20.303 StartZ=0 EndX=181.223 EndY=20.303 EndZ=0
    g2: LineSegment [constr] StartX=181.223 StartY=20.303 StartZ=0 EndX=181.223 EndY=-3.18451 EndZ=0
    g3: ArcOfCircle CenterX=181.223 CenterY=-20.3764 CenterZ=0 NormalX=0 NormalY=0 NormalZ=1 AngleXU=0 Radius=17.1918 StartAngle=0.436332 EndAngle=1.57079
    g4: ArcOfEllipse CenterX=181.223 CenterY=8.55923 CenterZ=0 NormalX=0 NormalY=0 NormalZ=1 MajorRadius=23.4779 MinorRadius=11.7437 AngleXU=0 StartAngle=1.5708 EndAngle=4.71239
    g5: LineSegment [constr] StartX=204.701 StartY=8.55923 StartZ=0 EndX=157.745 EndY=8.55923 EndZ=0
    g6: LineSegment [constr] StartX=181.223 StartY=20.303 StartZ=0 EndX=181.223 EndY=-3.18451 EndZ=0
    g7: GeomPoint [constr] X=201.553 Y=8.55923 Z=0
    g8: GeomPoint [constr] X=160.894 Y=8.55923 Z=0
    g9: GeomPoint [constr] X=181.223 Y=-3.18451 Z=0
    g10: LineSegment StartX=181.223 StartY=20.303 StartZ=0 EndX=202.765 EndY=20.303 EndZ=0
    g11: ArcOfCircle CenterX=207.583 CenterY=4 CenterZ=0 NormalX=0 NormalY=0 NormalZ=1 AngleXU=0 Radius=17 StartAngle=1.85815 EndAngle=3.57792
    g12: LineSegment [constr] StartX=172.411 StartY=39.2 StartZ=0 EndX=192.176 EndY=-3.18451 EndZ=0
  constraints (27):
    c: Coincident(g1,g-7)
    c: Horizontal(g1)
    c: Coincident(g2,g1)
    c: Vertical(g2)
    c: Horizontal(g2,g0)
    c: Coincident(g3,g0)
    c: Coincident(g3,g2)
    c: InternalAlignment(g5-g8 -> g4) x4
    c: Horizontal(g5)
    c: PointOnObject(g4,g2)
    c: Coincident(g4,g1)
    c: DistanceX(g-3,g5) = 10.1
    c: Coincident(g4,g2)
    c: Tangent(g3,g-5)
    c: PointOnObject(g9,g4)
    c: PointOnObject(g9,g3)
    c: Tangent(g4,g3,g9) = 1.5708
    c: Coincident(g10,g1)
    c: Coincident(g10,g1)
    c: Equal(g11,g-4)
    c: Coincident(g11,g1)
    c: Coincident(g11,g0)
    c: PointOnObject(g12,g-6)
    c: PointOnObject(g1,g12)
    c: Tangent(g12,g-5) = -1.5708
    c: Tangent(g0,g-5) = -1.5708
    c: Horizontal(g9,g12)
FEATURE [Sketcher::SketchObject] Sketch106  label="Sketch106 - smusso impuniatura interno"
  ArcFitTolerance = 1e-06
  AttachmentSupport = -> [Pad008]
  ExternalGeometry = -> [Pad008]
  FullyConstrained = true
  MakeInternals = false
  MapMode = 5
  Placement = pos=(0,-1.586e-13,-80.4316) rot=(1,0,0;3.14159rad)
  sketch-geometry (9):
    g0: LineSegment StartX=-176.685 StartY=-3.6 StartZ=0 EndX=-176.685 EndY=3.277e-13 EndZ=0
    g1: LineSegment [constr] StartX=-176.685 StartY=-7.37e-14 StartZ=0 EndX=-176.685 EndY=3.279e-13 EndZ=0
    g2: LineSegment [constr] StartX=-186.685 StartY=-3.6 StartZ=0 EndX=-186.685 EndY=3.277e-13 EndZ=0
    g3: ArcOfEllipse CenterX=-186.685 CenterY=3.279e-13 CenterZ=0 NormalX=0 NormalY=0 NormalZ=1 MajorRadius=10 MinorRadius=3.6 AngleXU=-3.14159 StartAngle=1.5708 EndAngle=3.14159
    g4: LineSegment [constr] StartX=-196.685 StartY=-5.9e-15 StartZ=0 EndX=-176.685 EndY=-5.9e-15 EndZ=0
    g5: LineSegment [constr] StartX=-186.685 StartY=-3.6 StartZ=0 EndX=-186.685 EndY=3.6 EndZ=0
    g6: GeomPoint [constr] X=-196.015 Y=-1.19e-14 Z=0
    g7: GeomPoint [constr] X=-177.356 Y=-4.9e-15 Z=0
    g8: LineSegment StartX=-176.685 StartY=-3.6 StartZ=0 EndX=-186.685 EndY=-3.6 EndZ=0
  constraints (15):
    c: PointOnObject(g2,g-3)
    c: Coincident(g1,g-5)
    c: DistanceY(g1,g1) = 0
    c: Coincident(g0,g1)
    c: DistanceX(g2,g-5) = 10
    c: Vertical(g2)
    c: Horizontal(g2,g0)
    c: InternalAlignment(g4-g7 -> g3) x4
    c: Coincident(g3,g2)
    c: Horizontal(g4)
    c: Coincident(g3,g0)
    c: Tangent(g0,g-5) = 1.5708
    c: Coincident(g3,g2)
    c: Coincident(g8,g0)
    c: Coincident(g8,g2)
FEATURE [Sketcher::SketchObject] Sketch107  label="Sketch107 - smusso impugnatura esterno"
  ArcFitTolerance = 1e-06
  AttachmentSupport = -> [Pad008]
  ExternalGeometry = -> [Pad008]
  FullyConstrained = true
  MakeInternals = false
  MapMode = 5
  Placement = pos=(0,-1.586e-13,-80.4316) rot=(1,0,0;3.14159rad)
  sketch-geometry (9):
    g0: LineSegment [constr] StartX=-215.932 StartY=-1.416e-13 StartZ=0 EndX=-215.932 EndY=-4.13e-14 EndZ=0
    g1: LineSegment StartX=-215.932 StartY=-3.6 StartZ=0 EndX=-215.932 EndY=-4.13e-14 EndZ=0
    g2: LineSegment StartX=-215.932 StartY=-3.6 StartZ=0 EndX=-205.932 EndY=-3.6 EndZ=0
    g3: LineSegment [constr] StartX=-205.932 StartY=-3.6 StartZ=0 EndX=-205.932 EndY=-4.13e-14 EndZ=0
    g4: ArcOfEllipse CenterX=-205.932 CenterY=-4.13e-14 CenterZ=0 NormalX=0 NormalY=0 NormalZ=1 MajorRadius=10 MinorRadius=3.6 AngleXU=-3.14159 StartAngle=-2.66e-14 EndAngle=1.5708
    g5: LineSegment [constr] StartX=-215.932 StartY=-1.416e-13 StartZ=0 EndX=-195.932 EndY=-1.416e-13 EndZ=0
    g6: LineSegment [constr] StartX=-205.932 StartY=-3.6 StartZ=0 EndX=-205.932 EndY=3.6 EndZ=0
    g7: GeomPoint [constr] X=-215.262 Y=-1.309e-13 Z=0
    g8: GeomPoint [constr] X=-196.602 Y=-1.551e-13 Z=0
  constraints (16):
    c: Coincident(g0,g-6)
    c: PointOnObject(g0,g-6)
    c: DistanceY(g0,g0) = 0
    c: Coincident(g1,g-6)
    c: Coincident(g1,g0)
    c: Tangent(g2,g-3)
    c: DistanceX(g2,g2) = 10
    c: Coincident(g3,g2)
    c: Vertical(g3)
    c: Horizontal(g3,g0)
    c: InternalAlignment(g5-g8 -> g4) x4
    c: Coincident(g4,g3)
    c: Horizontal(g5)
    c: Coincident(g4,g0)
    c: Coincident(g4,g2)
    c: PointOnObject(g2,g1)
FEATURE [Sketcher::SketchObject] Sketch108
  ArcFitTolerance = 1e-06
  AttachmentOffset = pos=(0,0,-1.6) rot=(0,0,1;0rad)
  AttachmentSupport = -> [Pad008]
  ExternalGeometry = -> [Binder]
  FullyConstrained = true
  MakeInternals = false
  MapMode = 5
  Placement = pos=(0,2,4e-16) rot=(0,0.707107,0.707107;3.14159rad)
  sketch-geometry (14):
    g0: LineSegment StartX=192.176 StartY=-3.18451 StartZ=0 EndX=193.827 EndY=-6.72678 EndZ=0
    g1: LineSegment [constr] StartX=202.765 StartY=20.303 StartZ=0 EndX=181.223 EndY=20.303 EndZ=0
    g2: LineSegment [constr] StartX=181.223 StartY=20.303 StartZ=0 EndX=181.223 EndY=1.30297 EndZ=0
    g3: ArcOfCircle CenterX=181.223 CenterY=-12.6042 CenterZ=0 NormalX=0 NormalY=0 NormalZ=1 AngleXU=0 Radius=13.9072 StartAngle=0.436332 EndAngle=1.5708
    g4: ArcOfEllipse CenterX=181.223 CenterY=10.803 CenterZ=0 NormalX=0 NormalY=0 NormalZ=1 MajorRadius=14.4779 MinorRadius=9.5 AngleXU=0 StartAngle=1.5708 EndAngle=4.71239
    g5: LineSegment [constr] StartX=195.701 StartY=10.803 StartZ=0 EndX=166.745 EndY=10.803 EndZ=0
    g6: LineSegment [constr] StartX=181.223 StartY=20.303 StartZ=0 EndX=181.223 EndY=1.30297 EndZ=0
    g7: GeomPoint [constr] X=192.148 Y=10.803 Z=0
    g8: GeomPoint [constr] X=170.298 Y=10.803 Z=0
    g9: LineSegment StartX=181.223 StartY=20.303 StartZ=0 EndX=202.765 EndY=20.303 EndZ=0
    g10: ArcOfCircle CenterX=207.583 CenterY=4 CenterZ=0 NormalX=0 NormalY=0 NormalZ=1 AngleXU=0 Radius=17 StartAngle=1.85815 EndAngle=3.57792
    g11: LineSegment [constr] StartX=172.411 StartY=39.2 StartZ=0 EndX=192.176 EndY=-3.18451 EndZ=0
    g12: GeomPoint [constr] X=181.223 Y=1.30297 Z=0
    g13: GeomPoint [constr] X=181.223 Y=1.30297 Z=0
  constraints (28):
    c: Coincident(g1,g-7)
    c: Horizontal(g1)
    c: Coincident(g2,g1)
    c: Vertical(g2)
    c: Coincident(g3,g2)
    c: InternalAlignment(g5-g8 -> g4) x4
    c: Horizontal(g5)
    c: PointOnObject(g4,g2)
    c: Coincident(g4,g1)
    c: DistanceX(g-3,g5) = 19.1
    c: Coincident(g4,g2)
    c: Coincident(g9,g1)
    c: Coincident(g9,g1)
    c: Coincident(g10,g1)
    c: Coincident(g10,g0)
    c: PointOnObject(g11,g-6)
    c: PointOnObject(g1,g11)
    c: DistanceY(g2,g1) = 19
    c: Coincident(g10,g-4)
    c: PointOnObject(g12,g4)
    c: PointOnObject(g12,g3)
    c: Tangent(g11,g-5) = -1.5708
    c: Tangent(g0,g-5) = -1.5708
    c: Tangent(g3,g0) = 1.5708
    c: PointOnObject(g13,g4)
    c: PointOnObject(g13,g3)
    c: Tangent(g4,g3,g13) = 1.5708
    c: Horizontal(g11,g0)
FEATURE [Part::Part2DObjectPython] Clone2D  label="Sketch108 (2D)"  # Draft 2D object (typed FeaturePython)
  Fuse = false
  Objects = -> [Sketch108]
  Placement = pos=(0,2,4e-16) rot=(0,0.707107,0.707107;3.14159rad)
  Scale = (1,1,1)
FEATURE [Sketcher::SketchObject] Sketch109
  ArcFitTolerance = 1e-06
  AttachmentOffset = pos=(0,0,-3.5) rot=(0,0,1;0rad)
  AttachmentSupport = -> [Pad008]
  ExternalGeometry = -> [Binder]
  FullyConstrained = true
  MakeInternals = false
  MapMode = 5
  Placement = pos=(0,0.1,8e-16) rot=(0,0.707107,0.707107;3.14159rad)
  sketch-geometry (1):
    g0: GeomPoint X=197.47 Y=8.55923 Z=0
  constraints (1):
    c: Symmetric(g-7,g-5,g0)
FEATURE [PartDesign::Chamfer] Chamfer005
  Angle = 45
  Base = -> Pad009 [Edge215,Edge212]
  BaseFeature = -> Pad009
  ChamferType = 1
  FlipDirection = false
  Refine = true
  Size = 1.5
  Size2 = 2.8
  SupportTransform = false
  Suppressed = false
  UseAllEdges = false
FEATURE [Sketcher::SketchObject] Sketch111
  ArcFitTolerance = 1e-06
  AttachmentSupport = -> [Pad009]
  ExternalGeometry = -> [Pad009]
  FullyConstrained = true
  MakeInternals = false
  MapMode = 5
  Placement = pos=(0,3.6,-8e-16) rot=(0,0.707107,0.707107;3.14159rad)
  sketch-geometry (21):
    g0: LineSegment [constr] StartX=97 StartY=36.8 StartZ=0 EndX=97 EndY=26.8 EndZ=0
    g1: LineSegment StartX=97 StartY=28.6 StartZ=0 EndX=97 EndY=27.8 EndZ=0
    g2: LineSegment StartX=97 StartY=27.8 StartZ=0 EndX=108 EndY=27.8 EndZ=0
    g3: LineSegment StartX=108 StartY=27.8 StartZ=0 EndX=108 EndY=28.6 EndZ=0
    g4: LineSegment StartX=108 StartY=28.6 StartZ=0 EndX=97 EndY=28.6 EndZ=0
    g5: LineSegment StartX=97 StartY=35.8 StartZ=0 EndX=97 EndY=35 EndZ=0
    g6: LineSegment StartX=97 StartY=35 StartZ=0 EndX=108 EndY=35 EndZ=0
    g7: LineSegment StartX=108 StartY=35 StartZ=0 EndX=108 EndY=35.8 EndZ=0
    g8: LineSegment StartX=108 StartY=35.8 StartZ=0 EndX=97 EndY=35.8 EndZ=0
    g9: LineSegment StartX=97 StartY=30.4 StartZ=0 EndX=97 EndY=29.6 EndZ=0
    g10: LineSegment StartX=97 StartY=29.6 StartZ=0 EndX=108 EndY=29.6 EndZ=0
    g11: LineSegment StartX=108 StartY=29.6 StartZ=0 EndX=108 EndY=30.4 EndZ=0
    g12: LineSegment StartX=108 StartY=30.4 StartZ=0 EndX=97 EndY=30.4 EndZ=0
    g13: LineSegment StartX=97 StartY=34 StartZ=0 EndX=97 EndY=33.2 EndZ=0
    g14: LineSegment StartX=97 StartY=33.2 StartZ=0 EndX=108 EndY=33.2 EndZ=0
    g15: LineSegment StartX=108 StartY=33.2 StartZ=0 EndX=108 EndY=34 EndZ=0
    g16: LineSegment StartX=108 StartY=34 StartZ=0 EndX=97 EndY=34 EndZ=0
    g17: LineSegment StartX=97 StartY=32.2 StartZ=0 EndX=97 EndY=31.4 EndZ=0
    g18: LineSegment StartX=97 StartY=31.4 StartZ=0 EndX=108 EndY=31.4 EndZ=0
    g19: LineSegment StartX=108 StartY=31.4 StartZ=0 EndX=108 EndY=32.2 EndZ=0
    g20: LineSegment StartX=108 StartY=32.2 StartZ=0 EndX=97 EndY=32.2 EndZ=0
  constraints (54):
    c: Vertical(g0)
    c: PointOnObject(g0,g-3)
    c: PointOnObject(g0,g-4)
    c: DistanceX(g0,g-5) = 11
    c: Coincident(g1,g2)
    c: Coincident(g2,g3)
    c: Coincident(g3,g4)
    c: Coincident(g4,g1)
    c: Horizontal(g2)
    c: Horizontal(g4)
    c: Tangent(g1,g0)
    c: Tangent(g3,g-5)
    c: DistanceY(g2,g3) = 0.8
    c: Coincident(g5,g6)
    c: Coincident(g6,g7)
    c: Coincident(g7,g8)
    c: Coincident(g8,g5)
    c: Horizontal(g6)
    c: Horizontal(g8)
    c: DistanceY(g6,g7) = 0.8
    c: Coincident(g9,g10)
    c: Coincident(g10,g11)
    c: Coincident(g11,g12)
    c: Coincident(g12,g9)
    c: Horizontal(g10)
    c: Horizontal(g12)
    c: DistanceY(g10,g11) = 0.8
    c: Tangent(g5,g0)
    c: Tangent(g7,g-5)
    c: Tangent(g9,g0)
    c: Tangent(g11,g-5)
    c: Coincident(g13,g14)
    c: Coincident(g14,g15)
    c: Coincident(g15,g16)
    c: Coincident(g16,g13)
    c: Horizontal(g14)
    c: Horizontal(g16)
    c: DistanceY(g14,g15) = 0.8
    c: Tangent(g13,g0)
    c: Tangent(g15,g-5)
    c: Coincident(g17,g18)
    c: Coincident(g18,g19)
    c: Coincident(g19,g20)
    c: Coincident(g20,g17)
    c: Horizontal(g18)
    c: Horizontal(g20)
    c: DistanceY(g18,g19) = 0.8
    c: Tangent(g17,g0)
    c: Tangent(g19,g-5)
    c: DistanceY(g1,g9) = 1
    c: DistanceY(g9,g17) = 1
    c: DistanceY(g17,g13) = 1
    c: DistanceY(g13,g5) = 1
    c: DistanceY(g0,g1) = 1
FEATURE [PartDesign::Pocket] Pocket004
  BaseFeature = -> Chamfer005
  Direction = (0,-1,2e-16)
  Length = 1
  Length2 = 5
  Profile = -> Sketch111
  ReferenceAxis = -> Sketch111 [N_Axis]
  Refine = true
  Suppressed = false
  Type = 0
FEATURE [PartDesign::Pad] Pad010
  BaseFeature = -> Pocket004
  Direction = (0,1,-2e-16)
  Length = 1.2
  Length2 = 10
  Profile = -> Sketch098
  ReferenceAxis = -> Sketch098 [N_Axis]
  Refine = true
  Suppressed = false
  Type = 0
FEATURE [PartDesign::Chamfer] Chamfer006
  Angle = 45
  Base = -> Pad010 [Edge291]
  BaseFeature = -> Pad010
  ChamferType = 1
  FlipDirection = false
  Refine = true
  Size = 1
  Size2 = 6
  SupportTransform = false
  Suppressed = false
  UseAllEdges = false
FEATURE [Sketcher::SketchObject] Sketch110
  ArcFitTolerance = 1e-06
  AttachmentSupport = -> [Pad010]
  ExternalGeometry = -> [Sketch098]
  FullyConstrained = true
  MakeInternals = false
  MapMode = 5
  Placement = pos=(0,4,-9e-16) rot=(0,0.707107,0.707107;3.14159rad)
  sketch-geometry (8):
    g0: LineSegment StartX=119.69 StartY=34 StartZ=0 EndX=130.69 EndY=34 EndZ=0
    g1: LineSegment StartX=119.95 StartY=33.2 StartZ=0 EndX=130.95 EndY=33.2 EndZ=0
    g2: LineSegment StartX=119.137 StartY=35.7 StartZ=0 EndX=130.137 EndY=35.7 EndZ=0
    g3: LineSegment StartX=118.877 StartY=36.5 StartZ=0 EndX=129.877 EndY=36.5 EndZ=0
    g4: LineSegment StartX=118.877 StartY=36.5 StartZ=0 EndX=119.137 EndY=35.7 EndZ=0
    g5: LineSegment StartX=129.877 StartY=36.5 StartZ=0 EndX=130.137 EndY=35.7 EndZ=0
    g6: LineSegment StartX=119.69 StartY=34 StartZ=0 EndX=119.95 EndY=33.2 EndZ=0
    g7: LineSegment StartX=130.69 StartY=34 StartZ=0 EndX=130.95 EndY=33.2 EndZ=0
  constraints (24):
    c: Horizontal(g0)
    c: Horizontal(g1)
    c: Horizontal(g2)
    c: Horizontal(g3)
    c: Equal(g1,g-5)
    c: Equal(g0,g-5)
    c: Equal(g2,g-5)
    c: Equal(g3,g-5)
    c: PointOnObject(g0,g-3)
    c: PointOnObject(g1,g-3)
    c: PointOnObject(g2,g-3)
    c: PointOnObject(g3,g-3)
    c: Coincident(g4,g3)
    c: Coincident(g4,g2)
    c: Coincident(g5,g3)
    c: Coincident(g5,g2)
    c: Coincident(g6,g0)
    c: Coincident(g6,g1)
    c: Coincident(g7,g0)
    c: Coincident(g7,g1)
    c: DistanceY(g1,g0) = 0.8
    c: DistanceY(g2,g3) = 0.8
    c: DistanceY(g-5,g1) = 2
    c: DistanceY(g-5,g2) = 4.5
FEATURE [PartDesign::Pocket] Pocket003
  BaseFeature = -> Chamfer006
  Direction = (0,-1,2e-16)
  Length = 1
  Length2 = 5
  Profile = -> Sketch110
  ReferenceAxis = -> Sketch110 [N_Axis]
  Refine = true
  Suppressed = false
  Type = 0
FEATURE [PartDesign::SubtractivePipe] SubtractivePipe
  AuxilleryCurvelinear = true
  AuxillerySpineTangent = false
  BaseFeature = -> Pocket003
  Binormal = (0,0,0)
  Mode = 0
  Profile = -> Sketch106
  Refine = true
  Spine = -> Pad008 [Edge215]
  SpineTangent = false
  Suppressed = false
  Transformation = 0
  Transition = 0
FEATURE [PartDesign::SubtractivePipe] SubtractivePipe001
  AuxilleryCurvelinear = true
  AuxillerySpineTangent = false
  BaseFeature = -> SubtractivePipe
  Binormal = (0,0,0)
  Mode = 0
  Profile = -> Sketch107
  Refine = true
  Spine = -> Pad008 [Edge213,Edge216,Edge210]
  SpineTangent = false
  Suppressed = false
  Transformation = 0
  Transition = 0
FEATURE [PartDesign::SubtractiveLoft] SubtractiveLoft
  BaseFeature = -> SubtractivePipe001
  Closed = false
  Profile = -> Sketch099
  Refine = true
  Ruled = false
  Sections = -> [Sketch108]
  Suppressed = false
FEATURE [PartDesign::SubtractiveLoft] SubtractiveLoft001
  BaseFeature = -> SubtractiveLoft
  Closed = false
  Profile = -> Clone2D
  Refine = true
  Ruled = false
  Sections = -> [Sketch109]
  Suppressed = false
FEATURE [Sketcher::SketchObject] Sketch112
  ArcFitTolerance = 1e-06
  AttachmentSupport = -> [Pad008]
  ExternalGeometry = -> [Binder]
  FullyConstrained = true
  MakeInternals = false
  MapMode = 5
  Placement = pos=(0,3.6,0) rot=(0,0.707107,0.707107;3.14159rad)
  sketch-geometry (4):
    g0: LineSegment [constr] StartX=167.782 StartY=-53.0314 StartZ=0 EndX=215.42 EndY=-53.0314 EndZ=0
    g1: GeomPoint [constr] X=191.282 Y=-53.0314 Z=0
    g2: Circle CenterX=191.282 CenterY=-53.0314 CenterZ=0 NormalX=0 NormalY=0 NormalZ=1 AngleXU=0 Radius=11.5
    g3: Circle CenterX=191.282 CenterY=-53.0314 CenterZ=0 NormalX=0 NormalY=0 NormalZ=1 AngleXU=0 Radius=10.7
  constraints (9):
    c: Horizontal(g0)
    c: PointOnObject(g0,g-3)
    c: Diameter(g2) = 23
    c: Coincident(g2,g1)
    c: Diameter(g3) = 21.4
    c: Coincident(g3,g1)
    c: DistanceX(g0,g1) = 23.5
    c: PointOnObject(g1,g0)
    c: Coincident(g0,g-4)
FEATURE [PartDesign::Chamfer] Chamfer016
  Angle = 45
  Base = -> SubtractiveLoft001 [Edge118,Edge117,Edge119,Edge120,Edge109]
  BaseFeature = -> SubtractiveLoft001
  ChamferType = 0
  FlipDirection = false
  Refine = true
  Size = 1.5
  Size2 = 1
  SupportTransform = false
  Suppressed = false
  UseAllEdges = false
FEATURE [PartDesign::Chamfer] Chamfer017
  Angle = 45
  Base = -> Chamfer016 [Edge15]
  BaseFeature = -> Chamfer016
  ChamferType = 0
  FlipDirection = false
  Refine = true
  Size = 1.6
  Size2 = 1
  SupportTransform = false
  Suppressed = false
  UseAllEdges = false
FEATURE [PartDesign::Chamfer] Chamfer018
  Angle = 45
  Base = -> Chamfer017 [Edge10]
  BaseFeature = -> Chamfer017
  ChamferType = 0
  FlipDirection = false
  Refine = true
  Size = 3.5
  Size2 = 1
  SupportTransform = false
  Suppressed = false
  UseAllEdges = false
FEATURE [PartDesign::Chamfer] Chamfer019
  Angle = 45
  Base = -> Chamfer018 [Edge94]
  BaseFeature = -> Chamfer018
  ChamferType = 0
  FlipDirection = false
  Refine = true
  Size = 1.9
  Size2 = 1
  SupportTransform = false
  Suppressed = false
  UseAllEdges = false
FEATURE [PartDesign::Fillet] Fillet009
  Base = -> Chamfer019 [Edge83]
  BaseFeature = -> Chamfer019
  Radius = 1.1
  Refine = true
  SupportTransform = false
  Suppressed = false
  UseAllEdges = false
FEATURE [PartDesign::Fillet] Fillet010
  Base = -> Fillet009 [Edge76]
  BaseFeature = -> Fillet009
  Radius = 1.9
  Refine = true
  SupportTransform = false
  Suppressed = false
  UseAllEdges = false
FEATURE [PartDesign::Pocket] Pocket005
  BaseFeature = -> Fillet010
  Direction = (0,-1,2e-16)
  Length = 0.8
  Length2 = 5
  Profile = -> Sketch112
  ReferenceAxis = -> Sketch112 [N_Axis]
  Refine = true
  Suppressed = false
  Type = 0
FEATURE [Part::Part2DObjectPython] ShapeString001  # Draft 2D object (typed FeaturePython)
  FontFile = <path>
  Fuse = false
  Justification = 6
  JustificationReference = 0
  KeepLeftMargin = false
  MakeFace = true
  ObliqueAngle = 0
  Placement = pos=(-183.5,3.6,-57.5) rot=(0,0.707107,0.707107;3.14159rad)
  ScaleToSize = true
  Size = 10
  String = AS
  Tracking = 0
FEATURE [PartDesign::Pocket] Pocket013
  BaseFeature = -> Pocket005
  Direction = (-1e-16,-1,2e-16)
  Length = 1
  Length2 = 5
  Profile = -> ShapeString001
  ReferenceAxis = -> ShapeString001 [N_Axis]
  Refine = true
  Suppressed = false
  Type = 0
FEATURE [PartDesign::Pad] Pad020
  Direction = (0,-1,2e-16)
  Length = 25.2
  Length2 = 10
  Midplane = true
  Placement = pos=(0,0,0) rot=(1,0,0;1.5708rad)
  Profile = -> Sketch021
  ReferenceAxis = -> Sketch021 [N_Axis]
  Refine = true
  Suppressed = false
  Type = 0
FEATURE [PartDesign::Body] Body001  label="perno fermo rumble e driver solenoide"
  AllowCompound = false
  Group = -> [Sketch021,Pad020]
  Origin = -> Origin001
  Tip = -> Pad020
FEATURE [PartDesign::Pad] Pad021
  Direction = (0,-1,2e-16)
  Length = 16.8
  Length2 = 10
  Midplane = true
  Placement = pos=(0,0,0) rot=(1,0,0;1.5708rad)
  Profile = -> Sketch061
  ReferenceAxis = -> Sketch061 [N_Axis]
  Refine = true
  Suppressed = false
  Type = 0
FEATURE [PartDesign::Pocket] Pocket014
  BaseFeature = -> Pad021
  Direction = (0,1,-2e-16)
  Length = 12.8
  Length2 = 5
  Midplane = true
  Placement = pos=(0,0,0) rot=(1,0,0;1.5708rad)
  Profile = -> Sketch062
  ReferenceAxis = -> Sketch062 [N_Axis]
  Refine = true
  Suppressed = false
  Type = 0
FEATURE [PartDesign::Pad] Pad022
  BaseFeature = -> Pocket014
  Direction = (0,-1,2e-16)
  Length = 7.6
  Length2 = 10
  Midplane = true
  Placement = pos=(0,0,0) rot=(1,0,0;1.5708rad)
  Profile = -> Sketch063
  ReferenceAxis = -> Sketch063 [N_Axis]
  Refine = true
  Suppressed = false
  Type = 0
FEATURE [PartDesign::Body] Body003  label="blocco switch"
  AllowCompound = false
  Group = -> [Sketch061,Sketch062,Sketch063,Pad021,Pocket014,Pad022]
  Origin = -> Origin003
  Tip = -> Pad022
FEATURE [PartDesign::Pad] Pad024
  Direction = (0,-1,2e-16)
  Length = 17
  Length2 = 10
  Midplane = true
  Placement = pos=(0,0,0) rot=(1,0,0;1.5708rad)
  Profile = -> Sketch045
  ReferenceAxis = -> Sketch045 [N_Axis]
  Refine = true
  Suppressed = false
  Type = 0
FEATURE [PartDesign::Pocket] Pocket015
  BaseFeature = -> Pad024
  Direction = (-1,0,0)
  Length = 8
  Length2 = 5
  Placement = pos=(0,0,0) rot=(1,0,0;1.5708rad)
  Profile = -> Sketch047
  ReferenceAxis = -> Sketch047 [N_Axis]
  Refine = true
  Reversed = true
  Suppressed = false
  Type = 0
FEATURE [PartDesign::Pocket] Pocket016
  BaseFeature = -> Pocket015
  Direction = (-1,0,0)
  Length = 1
  Length2 = 5
  Placement = pos=(0,0,0) rot=(1,0,0;1.5708rad)
  Profile = -> Sketch046
  ReferenceAxis = -> Sketch046 [N_Axis]
  Refine = true
  Reversed = true
  Suppressed = false
  Type = 0
FEATURE [PartDesign::Pocket] Pocket017
  BaseFeature = -> Pocket016
  Direction = (0,1,-2e-16)
  Length = 17
  Length2 = 5
  Midplane = true
  Placement = pos=(0,0,0) rot=(1,0,0;1.5708rad)
  Profile = -> Sketch048
  ReferenceAxis = -> Sketch048 [N_Axis]
  Refine = true
  Suppressed = false
  Type = 0
FEATURE [PartDesign::Pad] Pad025
  BaseFeature = -> Pocket017
  Direction = (0,-1,2e-16)
  Length = 17
  Length2 = 10
  Midplane = true
  Placement = pos=(0,0,0) rot=(1,0,0;1.5708rad)
  Profile = -> Sketch049
  ReferenceAxis = -> Sketch049 [N_Axis]
  Refine = true
  Suppressed = false
  Type = 0
FEATURE [PartDesign::Pad] Pad026
  BaseFeature = -> Pad025
  Direction = (0,-1,2e-16)
  Length = 17
  Length2 = 10
  Midplane = true
  Placement = pos=(0,0,0) rot=(1,0,0;1.5708rad)
  Profile = -> Sketch066
  ReferenceAxis = -> Sketch066 [N_Axis]
  Refine = true
  Suppressed = false
  Type = 0
FEATURE [PartDesign::Pad] Pad027
  BaseFeature = -> Pad026
  Direction = (0,-1,2e-16)
  Length = 5
  Length2 = 10
  Midplane = true
  Placement = pos=(0,0,0) rot=(1,0,0;1.5708rad)
  Profile = -> Sketch064
  ReferenceAxis = -> Sketch064 [N_Axis]
  Refine = true
  Suppressed = false
  Type = 0
FEATURE [PartDesign::Pad] Pad028
  BaseFeature = -> Pad027
  Direction = (1,0,0)
  Length = 1
  Length2 = 10
  Placement = pos=(0,0,0) rot=(1,0,0;1.5708rad)
  Profile = -> Sketch068
  ReferenceAxis = -> Sketch068 [N_Axis]
  Refine = true
  Reversed = true
  Suppressed = false
  Type = 0
FEATURE [PartDesign::Chamfer] Chamfer020
  Angle = 45
  Base = -> Pad028 [Edge73,Edge75,Edge78,Edge77]
  BaseFeature = -> Pad028
  ChamferType = 0
  FlipDirection = false
  Placement = pos=(0,0,0) rot=(1,0,0;1.5708rad)
  Refine = true
  Size = 0.5
  Size2 = 1
  SupportTransform = false
  Suppressed = false
  UseAllEdges = false
FEATURE [PartDesign::Body] Body002  label="supporto per neopixel"
  AllowCompound = false
  Group = -> [Sketch045,Sketch047,Sketch046,Sketch048,Sketch049,Sketch066,Sketch064,Sketch068,Pad024,Pocket015,Pocket016,Pocket017,Pad025,Pad026,Pad027,Pad028,Chamfer020]
  Origin = -> Origin002
  Tip = -> Chamfer020
FEATURE [Sketcher::SketchObject] Sketch134  label="perno fermo rumble002"
  ArcFitTolerance = 1e-06
  AttachmentSupport = -> [XZ_Plane008]
  FullyConstrained = true
  MakeInternals = false
  MapMode = 5
  Placement = pos=(0,0,0) rot=(1,0,0;1.5708rad)
  sketch-geometry (16):
    g0: LineSegment StartX=0 StartY=0.45 StartZ=0 EndX=0 EndY=1.55 EndZ=0
    g1: LineSegment StartX=0.45 StartY=2 StartZ=0 EndX=1.55 EndY=2 EndZ=0
    g2: LineSegment StartX=2 StartY=1.55 StartZ=0 EndX=2 EndY=0.45 EndZ=0
    g3: LineSegment StartX=1.55 StartY=0 StartZ=0 EndX=0.45 EndY=0 EndZ=0
    g4: ArcOfCircle [constr] CenterX=0.45 CenterY=1.55 CenterZ=0 NormalX=0 NormalY=0 NormalZ=1 AngleXU=0 Radius=0.45 StartAngle=1.5708 EndAngle=3.14159
    g5: GeomPoint [constr] X=0 Y=2 Z=0
    g6: LineSegment StartX=0.45 StartY=2 StartZ=0 EndX=0 EndY=1.55 EndZ=0
    g7: ArcOfCircle [constr] CenterX=1.55 CenterY=1.55 CenterZ=0 NormalX=0 NormalY=0 NormalZ=1 AngleXU=0 Radius=0.45 StartAngle=0 EndAngle=1.5708
    g8: GeomPoint [constr] X=2 Y=2 Z=0
    g9: LineSegment StartX=2 StartY=1.55 StartZ=0 EndX=1.55 EndY=2 EndZ=0
    g10: ArcOfCircle [constr] CenterX=1.55 CenterY=0.45 CenterZ=0 NormalX=0 NormalY=0 NormalZ=1 AngleXU=0 Radius=0.45 StartAngle=4.71239 EndAngle=6.28319
    g11: GeomPoint [constr] X=2 Y=0 Z=0
    g12: LineSegment StartX=1.55 StartY=0 StartZ=0 EndX=2 EndY=0.45 EndZ=0
    g13: ArcOfCircle [constr] CenterX=0.45 CenterY=0.45 CenterZ=0 NormalX=0 NormalY=0 NormalZ=1 AngleXU=0 Radius=0.45 StartAngle=3.14159 EndAngle=4.71239
    g14: GeomPoint [constr] X=0 Y=0 Z=0
    g15: LineSegment StartX=0 StartY=0.45 StartZ=0 EndX=0.45 EndY=0 EndZ=0
  constraints (35):
    c: Coincident(g14,g-1)
    c: PointOnObject(g5,g-2)
    c: Horizontal(g1)
    c: Vertical(g2)
    c: Horizontal(g3)
    c: DistanceX(g5,g8) = 2
    c: DistanceY(g11,g8) = 2
    c: PointOnObject(g5,g0)
    c: PointOnObject(g5,g1)
    c: Tangent(g0,g4) = 1.5708
    c: Tangent(g1,g4) = 1.5708
    c: Coincident(g6,g0)
    c: Coincident(g6,g1)
    c: PointOnObject(g8,g2)
    c: PointOnObject(g8,g1)
    c: Tangent(g2,g7) = 1.5708
    c: Tangent(g1,g7) = 1.5708
    c: Coincident(g9,g2)
    c: Coincident(g9,g1)
    c: PointOnObject(g11,g2)
    c: PointOnObject(g11,g3)
    c: Tangent(g2,g10) = 1.5708
    c: Tangent(g3,g10) = 1.5708
    c: Coincident(g12,g2)
    c: Coincident(g12,g3)
    c: PointOnObject(g14,g0)
    c: PointOnObject(g14,g3)
    c: Tangent(g0,g13) = 1.5708
    c: Tangent(g3,g13) = 1.5708
    c: Coincident(g15,g0)
    c: Coincident(g15,g3)
    c: Equal(g6,g9)
    c: Equal(g9,g12)
    c: Equal(g12,g15)
    c: DistanceX(g14,g3) = 0.45
FEATURE [PartDesign::Pad] Pad029
  Direction = (0,-1,2e-16)
  Length = 17
  Length2 = 10
  Midplane = true
  Placement = pos=(0,0,0) rot=(1,0,0;1.5708rad)
  Profile = -> Sketch134
  ReferenceAxis = -> Sketch134 [N_Axis]
  Refine = true
  Suppressed = false
  Type = 0
FEATURE [PartDesign::Body] Body008  label="perno fermo neopixel"
  AllowCompound = false
  Group = -> [Sketch134,Pad029]
  Origin = -> Origin008
  Tip = -> Pad029
FEATURE [Sketcher::SketchObject] Sketch135  label="perno fermo rumble003"
  ArcFitTolerance = 1e-06
  AttachmentSupport = -> [XZ_Plane009]
  FullyConstrained = true
  MakeInternals = false
  MapMode = 5
  Placement = pos=(0,0,0) rot=(1,0,0;1.5708rad)
  sketch-geometry (16):
    g0: LineSegment StartX=4.69e-14 StartY=0.8 StartZ=0 EndX=-3.04e-14 EndY=3.1 EndZ=0
    g1: LineSegment StartX=0.8 StartY=3.9 StartZ=0 EndX=3.1 EndY=3.9 EndZ=0
    g2: LineSegment StartX=3.9 StartY=3.1 StartZ=0 EndX=3.9 EndY=0.8 EndZ=0
    g3: LineSegment StartX=3.1 StartY=0 StartZ=0 EndX=0.8 EndY=0 EndZ=0
    g4: ArcOfCircle [constr] CenterX=0.8 CenterY=3.1 CenterZ=0 NormalX=0 NormalY=0 NormalZ=1 AngleXU=0 Radius=0.8 StartAngle=1.5708 EndAngle=3.14159
    g5: GeomPoint [constr] X=0 Y=3.9 Z=0
    g6: LineSegment StartX=0.8 StartY=3.9 StartZ=0 EndX=-3.04e-14 EndY=3.1 EndZ=0
    g7: ArcOfCircle [constr] CenterX=3.1 CenterY=3.1 CenterZ=0 NormalX=0 NormalY=0 NormalZ=1 AngleXU=0 Radius=0.8 StartAngle=-2.4e-14 EndAngle=1.5708
    g8: GeomPoint [constr] X=3.9 Y=3.9 Z=0
    g9: LineSegment StartX=3.9 StartY=3.1 StartZ=0 EndX=3.1 EndY=3.9 EndZ=0
    g10: ArcOfCircle [constr] CenterX=3.1 CenterY=0.8 CenterZ=0 NormalX=0 NormalY=0 NormalZ=1 AngleXU=0 Radius=0.8 StartAngle=4.71239 EndAngle=6.28319
    g11: GeomPoint [constr] X=3.9 Y=0 Z=0
    g12: LineSegment StartX=3.1 StartY=0 StartZ=0 EndX=3.9 EndY=0.8 EndZ=0
    g13: ArcOfCircle [constr] CenterX=0.8 CenterY=0.8 CenterZ=0 NormalX=0 NormalY=0 NormalZ=1 AngleXU=0 Radius=0.8 StartAngle=3.14159 EndAngle=4.71239
    g14: GeomPoint [constr] X=0 Y=0 Z=0
    g15: LineSegment StartX=4.69e-14 StartY=0.8 StartZ=0 EndX=0.8 EndY=0 EndZ=0
  constraints (35):
    c: Coincident(g14,g-1)
    c: PointOnObject(g5,g-2)
    c: Horizontal(g1)
    c: Vertical(g2)
    c: Horizontal(g3)
    c: DistanceX(g5,g8) = 3.9
    c: DistanceY(g11,g8) = 3.9
    c: PointOnObject(g5,g0)
    c: PointOnObject(g5,g1)
    c: Tangent(g0,g4) = 1.5708
    c: Tangent(g1,g4) = 1.5708
    c: Coincident(g6,g0)
    c: Coincident(g6,g1)
    c: PointOnObject(g8,g2)
    c: PointOnObject(g8,g1)
    c: Tangent(g2,g7) = 1.5708
    c: Tangent(g1,g7) = 1.5708
    c: Coincident(g9,g2)
    c: Coincident(g9,g1)
    c: PointOnObject(g11,g2)
    c: PointOnObject(g11,g3)
    c: Tangent(g2,g10) = 1.5708
    c: Tangent(g3,g10) = 1.5708
    c: Coincident(g12,g2)
    c: Coincident(g12,g3)
    c: PointOnObject(g14,g0)
    c: PointOnObject(g14,g3)
    c: Tangent(g0,g13) = 1.5708
    c: Tangent(g3,g13) = 1.5708
    c: Coincident(g15,g0)
    c: Coincident(g15,g3)
    c: Equal(g6,g9)
    c: Equal(g9,g12)
    c: Equal(g12,g15)
    c: DistanceX(g14,g3) = 0.8
FEATURE [PartDesign::Pad] Pad030
  Direction = (0,-1,2e-16)
  Length = 25.2
  Length2 = 10
  Midplane = true
  Placement = pos=(0,0,0) rot=(1,0,0;1.5708rad)
  Profile = -> Sketch135
  ReferenceAxis = -> Sketch135 [N_Axis]
  Refine = true
  Suppressed = false
  Type = 0
FEATURE [PartDesign::Body] Body009  label="perno fermo switch - caricabatterie - grilletto"
  AllowCompound = false
  Group = -> [Sketch135,Pad030]
  Origin = -> Origin009
  Tip = -> Pad030
FEATURE [Sketcher::SketchObject] Sketch136  label="scavo_rele"
  ArcFitTolerance = 1e-06
  AttachmentSupport = -> [XZ_Plane]
  ExternalGeometry = -> [Sketch]
  FullyConstrained = true
  MakeInternals = false
  MapMode = 5
  Placement = pos=(0,0,0) rot=(1,0,0;1.5708rad)
  sketch-geometry (7):
    g0: LineSegment [constr] StartX=-173.013 StartY=-62.644 StartZ=0 EndX=-176.535 EndY=-73.4861 EndZ=0
    g1: LineSegment [constr] StartX=-173.013 StartY=-62.644 StartZ=0 EndX=-170.35 EndY=-63.5093 EndZ=0
    g2: LineSegment [constr] StartX=-173.013 StartY=-62.644 StartZ=0 EndX=-176.627 EndY=-61.4698 EndZ=0
    g3: LineSegment StartX=-176.627 StartY=-61.4698 StartZ=0 EndX=-170.35 EndY=-63.5093 EndZ=0
    g4: LineSegment StartX=-176.627 StartY=-61.4698 StartZ=0 EndX=-180.149 EndY=-72.3118 EndZ=0
    g5: LineSegment StartX=-170.35 StartY=-63.5093 StartZ=0 EndX=-173.872 EndY=-74.3513 EndZ=0
    g6: LineSegment StartX=-180.149 StartY=-72.3118 StartZ=0 EndX=-173.872 EndY=-74.3513 EndZ=0
  constraints (19):
    c: Tangent(g0,g-3)
    c: Distance(g0,g-3) = 89
    c: Distance(g0,g0) = 11.4
    c: Coincident(g1,g0)
    c: Coincident(g2,g0)
    c: Distance(g2) = 3.8
    c: Distance(g1) = 2.8
    c: Perpendicular(g0,g1)
    c: Perpendicular(g0,g2)
    c: Coincident(g3,g2)
    c: Coincident(g3,g1)
    c: Equal(g4,g0)
    c: Equal(g5,g0)
    c: Parallel(g4,g0)
    c: Parallel(g5,g0)
    c: Coincident(g4,g2)
    c: Coincident(g5,g1)
    c: Coincident(g6,g4)
    c: Coincident(g6,g5)
FEATURE [Part::Extrusion] Extrude076  label="Extrude076 - scavo_rele"
  Base = -> Sketch136
  Dir = (0,-1,2e-16)
  DirMode = 2
  FaceMakerClass = Part::FaceMakerBullseye
  FaceMakerMode = 3
  LengthFwd = 17.8
  LengthRev = 0
  Solid = true
  Symmetric = true
FEATURE [Sketcher::SketchObject] Sketch137  label="scavo_nuovo_driver"
  ArcFitTolerance = 1e-06
  AttachmentSupport = -> [XZ_Plane]
  ExternalGeometry = -> [Sketch]
  FullyConstrained = true
  MakeInternals = false
  MapMode = 5
  Placement = pos=(0,0,0) rot=(1,0,0;1.5708rad)
  sketch-geometry (7):
    g0: LineSegment [constr] StartX=-167.759 StartY=-46.4761 StartZ=0 EndX=-172.58 EndY=-61.3126 EndZ=0
    g1: LineSegment [constr] StartX=-167.759 StartY=-46.4761 StartZ=0 EndX=-165.477 EndY=-47.2177 EndZ=0
    g2: LineSegment [constr] StartX=-167.759 StartY=-46.4761 StartZ=0 EndX=-171.373 EndY=-45.3018 EndZ=0
    g3: LineSegment StartX=-171.373 StartY=-45.3018 StartZ=0 EndX=-165.477 EndY=-47.2177 EndZ=0
    g4: LineSegment StartX=-171.373 StartY=-45.3018 StartZ=0 EndX=-176.194 EndY=-60.1383 EndZ=0
    g5: LineSegment StartX=-165.477 StartY=-47.2177 StartZ=0 EndX=-170.297 EndY=-62.0542 EndZ=0
    g6: LineSegment StartX=-176.194 StartY=-60.1383 StartZ=0 EndX=-170.297 EndY=-62.0542 EndZ=0
  constraints (19):
    c: Distance(g0,g-3) = 72
    c: Distance(g0) = 15.6
    c: Tangent(g0,g-3)
    c: Coincident(g1,g0)
    c: Coincident(g2,g0)
    c: Distance(g1) = 2.4
    c: Distance(g2) = 3.8
    c: Perpendicular(g0,g1)
    c: Perpendicular(g0,g2)
    c: Coincident(g3,g2)
    c: Coincident(g3,g1)
    c: Equal(g4,g0)
    c: Equal(g5,g0)
    c: Parallel(g4,g0)
    c: Parallel(g5,g0)
    c: Coincident(g4,g2)
    c: Coincident(g5,g1)
    c: Coincident(g6,g4)
    c: Coincident(g6,g5)
FEATURE [Part::Extrusion] Extrude077  label="Extrude077 - scavo_nuovo_driver"
  Base = -> Sketch137
  Dir = (0,-1,2e-16)
  DirMode = 2
  FaceMakerClass = Part::FaceMakerBullseye
  FaceMakerMode = 3
  LengthFwd = 20.8
  LengthRev = 0
  Solid = true
  Symmetric = true
FEATURE [Sketcher::SketchObject] Sketch138  label="scavo_nuovo_driver_alto"
  ArcFitTolerance = 1e-06
  AttachmentSupport = -> [XZ_Plane]
  ExternalGeometry = -> [Sketch]
  FullyConstrained = true
  MakeInternals = false
  MapMode = 5
  Placement = pos=(0,0,0) rot=(1,0,0;1.5708rad)
  sketch-geometry (7):
    g0: LineSegment [constr] StartX=-188.796 StartY=17.7274 StartZ=0 EndX=-187.75 EndY=4.97025 EndZ=0
    g1: LineSegment StartX=-187.75 StartY=4.97025 StartZ=0 EndX=-189.743 EndY=4.8067 EndZ=0
    g2: LineSegment StartX=-187.75 StartY=4.97025 StartZ=0 EndX=-182.766 EndY=5.37913 EndZ=0
    g3: LineSegment StartX=-190.79 StartY=17.5638 StartZ=0 EndX=-189.743 EndY=4.8067 EndZ=0
    g4: LineSegment StartX=-183.813 StartY=18.1363 StartZ=0 EndX=-182.766 EndY=5.37913 EndZ=0
    g5: LineSegment StartX=-190.79 StartY=17.5638 StartZ=0 EndX=-188.796 EndY=17.7274 EndZ=0
    g6: LineSegment StartX=-188.796 StartY=17.7274 StartZ=0 EndX=-183.813 EndY=18.1363 EndZ=0
  constraints (20):
    c: Distance(g0) = 12.8
    c: DistanceY(g-3,g0) = 9
    c: PointOnObject(g0,g-4)
    c: PointOnObject(g0,g-4)
    c: Coincident(g1,g0)
    c: Coincident(g2,g0)
    c: Distance(g1) = 2
    c: Distance(g2) = 5
    c: Perpendicular(g0,g1)
    c: Perpendicular(g0,g2)
    c: Equal(g3,g0)
    c: Parallel(g3,g0)
    c: Coincident(g3,g1)
    c: Equal(g4,g0)
    c: Parallel(g4,g0)
    c: Coincident(g4,g2)
    c: Coincident(g5,g3)
    c: Coincident(g5,g0)
    c: Coincident(g6,g0)
    c: Coincident(g6,g4)
FEATURE [Part::Extrusion] Extrude078  label="Extrude078 - scavo_nuovo_driver_alto"
  Base = -> Sketch138
  Dir = (0,-1,2e-16)
  DirMode = 2
  FaceMakerClass = Part::FaceMakerBullseye
  FaceMakerMode = 3
  LengthFwd = 16.6
  LengthRev = 0
  Solid = true
  Symmetric = true
FEATURE [Sketcher::SketchObject] Sketch139  label="fermi_nuovo_driver_alto"
  ArcFitTolerance = 1e-06
  AttachmentSupport = -> [XZ_Plane]
  ExternalGeometry = -> [Sketch138,Sketch]
  FullyConstrained = true
  MakeInternals = false
  MapMode = 5
  Placement = pos=(0,0,0) rot=(1,0,0;1.5708rad)
  sketch-geometry (17):
    g0: LineSegment [constr] StartX=-188.314 StartY=16.4295 StartZ=0 EndX=-187.885 EndY=13.7638 EndZ=0
    g1: LineSegment [constr] StartX=-187.885 StartY=13.7638 StartZ=0 EndX=-187.456 EndY=11.0981 EndZ=0
    g2: LineSegment StartX=-187.885 StartY=13.7638 StartZ=0 EndX=-187.71 EndY=12.6778 EndZ=0
    g3: LineSegment StartX=-187.885 StartY=13.7638 StartZ=0 EndX=-188.06 EndY=14.8499 EndZ=0
    g4: LineSegment StartX=-187.71 StartY=12.6778 StartZ=0 EndX=-185.538 EndY=13.0274 EndZ=0
    g5: LineSegment StartX=-188.06 StartY=14.8499 StartZ=0 EndX=-185.888 EndY=15.1994 EndZ=0
    g6: LineSegment StartX=-185.888 StartY=15.1994 StartZ=0 EndX=-185.538 EndY=13.0274 EndZ=0
    g7: LineSegment StartX=-187.456 StartY=11.0981 StartZ=0 EndX=-189.035 EndY=10.8439 EndZ=0
    g8: LineSegment StartX=-188.314 StartY=16.4295 StartZ=0 EndX=-189.893 EndY=16.1753 EndZ=0
    g9: LineSegment StartX=-189.893 StartY=16.1753 StartZ=0 EndX=-189.035 EndY=10.8439 EndZ=0
    g10: LineSegment StartX=-187.456 StartY=11.0981 StartZ=0 EndX=-185.284 EndY=11.4477 EndZ=0
    g11: LineSegment StartX=-188.314 StartY=16.4295 StartZ=0 EndX=-186.142 EndY=16.7791 EndZ=0
    g12: LineSegment StartX=-184.308 StartY=15.4537 StartZ=0 EndX=-183.958 EndY=13.2816 EndZ=0
    g13: ArcOfCircle CenterX=-185.888 CenterY=15.1994 CenterZ=0 NormalX=0 NormalY=0 NormalZ=1 AngleXU=0 Radius=1.6 StartAngle=0.15957 EndAngle=1.73037
    g14: GeomPoint [constr] X=-184.562 Y=17.0333 Z=0
    g15: ArcOfCircle CenterX=-185.538 CenterY=13.0274 CenterZ=0 NormalX=0 NormalY=0 NormalZ=1 AngleXU=0 Radius=1.6 StartAngle=4.87196 EndAngle=6.44276
    g16: GeomPoint [constr] X=-183.704 Y=11.7019 Z=0
  constraints (43):
    c: Tangent(g1,g0) = -1.5708
    c: Distance(g0) = 2.7
    c: Equal(g1,g0)
    c: Tangent(g1,g-5)
    c: Coincident(g2,g0)
    c: Coincident(g3,g0)
    c: Distance(g2) = 1.1
    c: Equal(g3,g2)
    c: PointOnObject(g3,g2)
    c: Coincident(g4,g2)
    c: Coincident(g5,g3)
    c: Distance(g4) = 2.2
    c: Equal(g4,g5)
    c: Perpendicular(g1,g4)
    c: Perpendicular(g0,g5)
    c: Coincident(g6,g5)
    c: Coincident(g6,g4)
    c: Coincident(g7,g1)
    c: Coincident(g8,g0)
    c: Distance(g7) = 1.6
    c: Equal(g7,g8)
    c: Perpendicular(g1,g7)
    c: Perpendicular(g8,g0)
    c: Coincident(g9,g8)
    c: Coincident(g9,g7)
    c: Coincident(g10,g1)
    c: Coincident(g11,g0)
    c: Distance(g10,g16) = 3.8
    c: Perpendicular(g1,g10)
    c: Perpendicular(g1,g11)
    c: DistanceY(g0,g-4) = 3.8
    c: PointOnObject(g14,g12)
    c: PointOnObject(g14,g11)
    c: Tangent(g12,g13) = 1.5708
    c: Tangent(g11,g13) = 1.5708
    c: PointOnObject(g16,g12)
    c: PointOnObject(g16,g10)
    c: Tangent(g12,g15) = 1.5708
    c: Tangent(g10,g15) = -1.5708
    c: Equal(g13,g15)
    c: Coincident(g13,g5)
    c: Parallel(g2,g0)
    c: PointOnObject(g0,g-5)
FEATURE [Part::Extrusion] Extrude079  label="Extrude079 - fermi_nuovo_driver_alto"
  Base = -> Sketch139
  Dir = (0,-1,2e-16)
  DirMode = 2
  FaceMakerClass = Part::FaceMakerBullseye
  FaceMakerMode = 3
  LengthFwd = 25.2
  LengthRev = 0
  Solid = true
  Symmetric = true
FEATURE [Sketcher::SketchObject] Sketch140  label="scavo_diodo_nuovo_driver_alto"
  ArcFitTolerance = 1e-06
  AttachmentSupport = -> [XZ_Plane]
  ExternalGeometry = -> [Sketch138]
  FullyConstrained = true
  MakeInternals = false
  MapMode = 5
  Placement = pos=(0,0,0) rot=(1,0,0;1.5708rad)
  sketch-geometry (4):
    g0: LineSegment StartX=-190.79 StartY=17.5638 StartZ=0 EndX=-189.743 EndY=4.8067 EndZ=0
    g1: LineSegment StartX=-193.78 StartY=17.3185 StartZ=0 EndX=-192.733 EndY=4.56137 EndZ=0
    g2: LineSegment StartX=-190.79 StartY=17.5638 StartZ=0 EndX=-193.78 EndY=17.3185 EndZ=0
    g3: LineSegment StartX=-192.733 StartY=4.56137 StartZ=0 EndX=-189.743 EndY=4.8067 EndZ=0
  constraints (11):
    c: Equal(g0,g-3)
    c: Parallel(g0,g-3)
    c: Equal(g1,g-3)
    c: Parallel(g1,g-3)
    c: Coincident(g2,g0)
    c: Distance(g2) = 3
    c: Perpendicular(g0,g2)
    c: Coincident(g1,g2)
    c: Coincident(g3,g1)
    c: Coincident(g3,g0)
    c: Coincident(g0,g-3)
FEATURE [Part::Extrusion] Extrude080  label="Extrude080 - scavo_diodo_nuovo_driver_alto"
  Base = -> Sketch140
  Dir = (0,-1,2e-16)
  DirMode = 2
  FaceMakerClass = Part::FaceMakerBullseye
  FaceMakerMode = 3
  LengthFwd = 4
  LengthRev = 0
  Placement = pos=(0,7.8,0) rot=(0,0,1;0rad)
  Solid = true
  Symmetric = false
FEATURE [Part::MultiFuse] Fusion001
  Refine = true
  Shapes = -> [Cut043,Extrude079]
FEATURE [Part::Cut] Cut044
  Base = -> Fusion001
  Refine = true
  Tool = -> Extrude078
FEATURE [Part::Cut] Cut045
  Base = -> Cut044
  Refine = true
  Tool = -> Extrude080
FEATURE [Sketcher::SketchObject] Sketch141  label="fermi_nuovo_driver"
  ArcFitTolerance = 1e-06
  AttachmentSupport = -> [XZ_Plane]
  ExternalGeometry = -> [Sketch,Sketch137]
  FullyConstrained = true
  MakeInternals = false
  MapMode = 5
  Placement = pos=(0,0,0) rot=(1,0,0;1.5708rad)
  sketch-geometry (16):
    g0: LineSegment [constr] StartX=-165.477 StartY=-47.2177 StartZ=0 EndX=-167.759 EndY=-46.4761 EndZ=0
    g1: LineSegment [constr] StartX=-167.759 StartY=-46.4761 StartZ=0 EndX=-168.006 EndY=-47.2369 EndZ=0
    g2: LineSegment [constr] StartX=-168.006 StartY=-47.2369 StartZ=0 EndX=-169.675 EndY=-52.3726 EndZ=0
    g3: LineSegment StartX=-169.675 StartY=-52.3726 StartZ=0 EndX=-171.767 EndY=-51.6928 EndZ=0
    g4: LineSegment StartX=-172.795 StartY=-49.6767 StartZ=0 EndX=-172.115 EndY=-47.5843 EndZ=0
    g5: LineSegment StartX=-170.099 StartY=-46.5571 StartZ=0 EndX=-166.485 EndY=-47.7313 EndZ=0
    g6: LineSegment StartX=-166.485 StartY=-47.7313 StartZ=0 EndX=-168.153 EndY=-52.867 EndZ=0
    g7: LineSegment StartX=-169.675 StartY=-52.3726 StartZ=0 EndX=-168.153 EndY=-52.867 EndZ=0
    g8: LineSegment StartX=-170.593 StartY=-48.0788 StartZ=0 EndX=-171.273 EndY=-50.1711 EndZ=0
    g9: LineSegment StartX=-171.273 StartY=-50.1711 StartZ=0 EndX=-169.181 EndY=-50.8509 EndZ=0
    g10: LineSegment StartX=-169.181 StartY=-50.8509 StartZ=0 EndX=-168.501 EndY=-48.7586 EndZ=0
    g11: LineSegment StartX=-168.501 StartY=-48.7586 StartZ=0 EndX=-170.593 EndY=-48.0788 EndZ=0
    g12: ArcOfCircle CenterX=-170.593 CenterY=-48.0788 CenterZ=0 NormalX=0 NormalY=0 NormalZ=1 AngleXU=0 Radius=1.6 StartAngle=1.25664 EndAngle=2.82743
    g13: GeomPoint [constr] X=-171.62 Y=-46.0626 Z=0
    g14: ArcOfCircle CenterX=-171.273 CenterY=-50.1711 CenterZ=0 NormalX=0 NormalY=0 NormalZ=1 AngleXU=0 Radius=1.6 StartAngle=2.82743 EndAngle=4.39823
    g15: GeomPoint [constr] X=-173.289 Y=-51.1984 Z=0
  constraints (41):
    c: Coincident(g0,g-4)
    c: PointOnObject(g0,g-3)
    c: Parallel(g0,g-4)
    c: Coincident(g1,g0)
    c: Parallel(g1,g-3)
    c: Distance(g1) = 0.8
    c: Coincident(g2,g1)
    c: Distance(g2) = 5.4
    c: Coincident(g3,g2)
    c: Parallel(g2,g-3)
    c: Distance(g15,g13) = 5.4
    c: Perpendicular(g3,g2)
    c: Parallel(g4,g2)
    c: Distance(g5,g13) = 5.4
    c: Distance(g3,g15) = 3.8
    c: Perpendicular(g4,g5)
    c: Coincident(g6,g5)
    c: Distance(g6) = 5.4
    c: Parallel(g6,g4)
    c: Coincident(g7,g2)
    c: Coincident(g7,g6)
    c: Coincident(g8,g9)
    c: Coincident(g9,g10)
    c: Coincident(g10,g11)
    c: Coincident(g11,g8)
    c: Distance(g8,g10) = 2.2
    c: Distance(g9,g11) = 2.2
    c: Perpendicular(g11,g8)
    c: Equal(g8,g10)
    c: Equal(g11,g9)
    c: Tangent(g10,g2)
    c: Distance(g10,g1) = 1.6
    c: PointOnObject(g13,g4)
    c: PointOnObject(g13,g5)
    c: Tangent(g4,g12) = 1.5708
    c: Tangent(g5,g12) = 1.5708
    c: PointOnObject(g15,g4)
    c: Tangent(g4,g14) = 1.5708
    c: Tangent(g3,g14) = 1.5708
    c: Equal(g14,g12)
    c: Coincident(g12,g8)
FEATURE [Part::Extrusion] Extrude081  label="Extrude081 - fermi_nuovo_driver"
  Base = -> Sketch141
  Dir = (0,-1,2e-16)
  DirMode = 2
  FaceMakerClass = Part::FaceMakerBullseye
  FaceMakerMode = 3
  LengthFwd = 25.2
  LengthRev = 0
  Solid = true
  Symmetric = true
FEATURE [Part::MultiFuse] Fusion002
  Refine = true
  Shapes = -> [Cut045,Extrude081]
FEATURE [Part::Cut] Cut046
  Base = -> Fusion002
  Refine = true
  Tool = -> Extrude077
FEATURE [Sketcher::SketchObject] Sketch142  label="fermi_rele"
  ArcFitTolerance = 1e-06
  AttachmentSupport = -> [XZ_Plane]
  ExternalGeometry = -> [Sketch,Sketch136]
  FullyConstrained = true
  MakeInternals = false
  MapMode = 5
  Placement = pos=(0,0,0) rot=(1,0,0;1.5708rad)
  sketch-geometry (15):
    g0: LineSegment StartX=-177.245 StartY=-63.3719 StartZ=0 EndX=-177.924 EndY=-65.4642 EndZ=0
    g1: LineSegment StartX=-175.228 StartY=-62.3446 StartZ=0 EndX=-171.614 EndY=-63.5189 EndZ=0
    g2: LineSegment StartX=-171.614 StartY=-63.5189 StartZ=0 EndX=-173.283 EndY=-68.6546 EndZ=0
    g3: LineSegment StartX=-176.897 StartY=-67.4803 StartZ=0 EndX=-173.283 EndY=-68.6546 EndZ=0
    g4: LineSegment StartX=-175.723 StartY=-63.8663 StartZ=0 EndX=-173.631 EndY=-64.5461 EndZ=0
    g5: LineSegment StartX=-175.723 StartY=-63.8663 StartZ=0 EndX=-176.403 EndY=-65.9586 EndZ=0
    g6: LineSegment StartX=-173.631 StartY=-64.5461 StartZ=0 EndX=-174.31 EndY=-66.6385 EndZ=0
    g7: LineSegment StartX=-176.403 StartY=-65.9586 StartZ=0 EndX=-174.31 EndY=-66.6385 EndZ=0
    g8: LineSegment [constr] StartX=-173.631 StartY=-64.5461 StartZ=0 EndX=-173.136 EndY=-63.0245 EndZ=0
    g9: LineSegment [constr] StartX=-173.631 StartY=-64.5461 StartZ=0 EndX=-172.109 EndY=-65.0406 EndZ=0
    g10: LineSegment [constr] StartX=-170.35 StartY=-63.5093 StartZ=0 EndX=-173.013 EndY=-62.644 EndZ=0
    g11: ArcOfCircle CenterX=-175.723 CenterY=-63.8663 CenterZ=0 NormalX=0 NormalY=0 NormalZ=1 AngleXU=0 Radius=1.6 StartAngle=1.25664 EndAngle=2.82743
    g12: GeomPoint [constr] X=-176.75 Y=-61.8502 Z=0
    g13: ArcOfCircle CenterX=-176.403 CenterY=-65.9586 CenterZ=0 NormalX=0 NormalY=0 NormalZ=1 AngleXU=0 Radius=1.6 StartAngle=2.82743 EndAngle=4.39823
    g14: GeomPoint [constr] X=-178.419 Y=-66.9859 Z=0
  constraints (39):
    c: Distance(g14,g12) = 5.4
    c: Distance(g1,g12) = 5.4
    c: Perpendicular(g1,g0)
    c: Coincident(g2,g1)
    c: Parallel(g2,g0)
    c: Coincident(g3,g2)
    c: Parallel(g2,g-3)
    c: Coincident(g5,g4)
    c: Distance(g5) = 2.2
    c: Distance(g4) = 2.2
    c: Perpendicular(g4,g5)
    c: Coincident(g6,g4)
    c: Equal(g6,g5)
    c: Parallel(g6,g5)
    c: Coincident(g7,g5)
    c: Coincident(g7,g6)
    c: Coincident(g8,g4)
    c: Coincident(g9,g4)
    c: Distance(g8) = 1.6
    c: Distance(g9) = 1.6
    c: Parallel(g8,g6)
    c: Parallel(g9,g4)
    c: PointOnObject(g8,g1)
    c: PointOnObject(g9,g2)
    c: Coincident(g10,g-4)
    c: Parallel(g10,g-4)
    c: PointOnObject(g10,g-3)
    c: Tangent(g6,g-3) = 1.5708
    c: Distance(g4,g10) = 2
    c: PointOnObject(g12,g1)
    c: Tangent(g1,g11) = 1.5708
    c: Tangent(g0,g11) = -1.5708
    c: PointOnObject(g14,g3)
    c: PointOnObject(g14,g0)
    c: Tangent(g3,g13) = -1.5708
    c: Tangent(g0,g13) = -1.5708
    c: Equal(g11,g13)
    c: Coincident(g11,g4)
    c: Parallel(g3,g1)
FEATURE [Part::Extrusion] Extrude082  label="Extrude082 - fermi_rele"
  Base = -> Sketch142
  Dir = (0,-1,2e-16)
  DirMode = 2
  FaceMakerClass = Part::FaceMakerBullseye
  FaceMakerMode = 3
  LengthFwd = 25.2
  LengthRev = 0
  Solid = true
  Symmetric = true
FEATURE [Part::MultiFuse] Fusion003
  Refine = true
  Shapes = -> [Cut046,Extrude082]
FEATURE [Part::Cut] Cut047
  Base = -> Fusion003
  Refine = true
  Tool = -> Extrude076
FEATURE [Sketcher::SketchObject] Sketch143  label="foro_passaggio_cavi_led_batteria"
  ArcFitTolerance = 1e-06
  AttachmentSupport = -> [XZ_Plane]
  ExternalGeometry = -> [Sketch,Sketch042,Sketch036]
  FullyConstrained = true
  MakeInternals = false
  MapMode = 5
  Placement = pos=(0,0,0) rot=(1,0,0;1.5708rad)
  sketch-geometry (4):
    g0: LineSegment StartX=-207.775 StartY=-41.3701 StartZ=0 EndX=-213.607 EndY=-53.8767 EndZ=0
    g1: LineSegment StartX=-213.607 StartY=-53.8767 StartZ=0 EndX=-211.843 EndY=-59.5559 EndZ=0
    g2: LineSegment StartX=-207.775 StartY=-41.3701 StartZ=0 EndX=-207.775 EndY=-50.8316 EndZ=0
    g3: LineSegment StartX=-207.775 StartY=-50.8316 StartZ=0 EndX=-211.843 EndY=-59.5559 EndZ=0
  constraints (9):
    c: Coincident(g0,g-3)
    c: PointOnObject(g1,g-6)
    c: Coincident(g1,g0)
    c: Coincident(g2,g0)
    c: Coincident(g2,g-7)
    c: Coincident(g3,g2)
    c: Parallel(g3,g0)
    c: Coincident(g3,g1)
    c: Coincident(g0,g-5)
FEATURE [Part::Extrusion] Extrude083  label="Extrude083 - foro_passaggio_cavi_led_batteria"
  Base = -> Sketch143
  Dir = (0,-1,2e-16)
  DirMode = 2
  FaceMakerClass = Part::FaceMakerBullseye
  FaceMakerMode = 3
  LengthFwd = 6
  LengthRev = 0
  Solid = true
  Symmetric = true
FEATURE [Part::Cut] Cut048
  Base = -> Cut047
  Refine = true
  Tool = -> Extrude083
FEATURE [Sketcher::SketchObject] Sketch144  label="foro_areazione_alimentatore"
  ArcFitTolerance = 1e-06
  AttachmentSupport = -> [XZ_Plane]
  ExternalGeometry = -> [Sketch036]
  FullyConstrained = true
  MakeInternals = false
  MapMode = 5
  Placement = pos=(0,0,0) rot=(1,0,0;1.5708rad)
  sketch-geometry (4):
    g0: LineSegment StartX=-211.843 StartY=-60.3701 StartZ=0 EndX=-207.775 EndY=-60.3701 EndZ=0
    g1: LineSegment StartX=-207.775 StartY=-60.3701 StartZ=0 EndX=-207.775 EndY=-70.3701 EndZ=0
    g2: LineSegment StartX=-211.843 StartY=-60.3701 StartZ=0 EndX=-211.843 EndY=-70.3701 EndZ=0
    g3: LineSegment StartX=-207.775 StartY=-70.3701 StartZ=0 EndX=-211.843 EndY=-70.3701 EndZ=0
  constraints (11):
    c: Horizontal(g0)
    c: Distance(g1) = 10
    c: Coincident(g1,g0)
    c: Tangent(g1,g-3)
    c: PointOnObject(g0,g-4)
    c: Coincident(g2,g0)
    c: PointOnObject(g2,g-4)
    c: Coincident(g3,g1)
    c: Horizontal(g3)
    c: Coincident(g3,g2)
    c: DistanceY(g0,g-3) = 19
FEATURE [Part::Extrusion] Extrude084  label="Extrude084 - foro_areazione_alimentatore"
  Base = -> Sketch144
  Dir = (0,-1,2e-16)
  DirMode = 2
  FaceMakerClass = Part::FaceMakerBullseye
  FaceMakerMode = 3
  LengthFwd = 10
  LengthRev = 0
  Solid = true
  Symmetric = true
FEATURE [Part::Cut] Cut049
  Base = -> Cut048
  Refine = true
  Tool = -> Extrude084
FEATURE [Sketcher::SketchObject] Sketch145  label="foro_per_condesatore"
  ArcFitTolerance = 1e-06
  AttachmentSupport = -> [XZ_Plane]
  ExternalGeometry = -> [Sketch,Sketch139]
  FullyConstrained = true
  MakeInternals = false
  MapMode = 5
  Placement = pos=(0,0,0) rot=(1,0,0;1.5708rad)
  sketch-geometry (1):
    g0: Circle CenterX=-182.345 CenterY=7.02342 CenterZ=0 NormalX=0 NormalY=0 NormalZ=1 AngleXU=0 Radius=5.2
  constraints (3):
    c: Diameter(g0) = 10.4
    c: Tangent(g0,g-3)
    c: Tangent(g0,g-4)
FEATURE [Part::Extrusion] Extrude085  label="Extrude085 - foro_per_condesatore"
  Base = -> Sketch145
  Dir = (0,-1,2e-16)
  DirMode = 2
  FaceMakerClass = Part::FaceMakerBullseye
  FaceMakerMode = 3
  LengthFwd = 25.2
  LengthRev = 0
  Solid = true
  Symmetric = true
FEATURE [Part::Cut] Cut050
  Base = -> Cut049
  Refine = true
  Tool = -> Extrude085
FEATURE [Sketcher::SketchObject] Sketch146  label="scavo_pulsante_6x6_per_led_batteria"
  ArcFitTolerance = 1e-06
  AttachmentSupport = -> [XZ_Plane]
  ExternalGeometry = -> [Sketch016]
  FullyConstrained = true
  MakeInternals = false
  MapMode = 5
  Placement = pos=(0,0,0) rot=(1,0,0;1.5708rad)
  sketch-geometry (5):
    g0: LineSegment StartX=-216.643 StartY=-65.8316 StartZ=0 EndX=-216.643 EndY=-72.8316 EndZ=0
    g1: LineSegment StartX=-216.643 StartY=-72.8316 StartZ=0 EndX=-210.243 EndY=-72.8316 EndZ=0
    g2: LineSegment StartX=-210.243 StartY=-72.8316 StartZ=0 EndX=-210.243 EndY=-65.8316 EndZ=0
    g3: LineSegment StartX=-210.243 StartY=-65.8316 StartZ=0 EndX=-216.643 EndY=-65.8316 EndZ=0
    g4: GeomPoint [constr] X=-213.443 Y=-69.3316 Z=0
  constraints (13):
    c: Coincident(g0,g1)
    c: Coincident(g1,g2)
    c: Coincident(g2,g3)
    c: Coincident(g3,g0)
    c: Vertical(g0)
    c: Vertical(g2)
    c: Horizontal(g1)
    c: Horizontal(g3)
    c: Distance(g0,g2) = 6.4
    c: Distance(g1,g3) = 7
    c: Tangent(g1,g-3)
    c: Symmetric(g0,g2,g4)
    c: Vertical(g-3,g4)
FEATURE [Part::Extrusion] Extrude086  label="Extrude086 - scavo_pulsante_6x6_per_led_batteria"
  Base = -> Sketch146
  Dir = (0,-1,2e-16)
  DirMode = 2
  FaceMakerClass = Part::FaceMakerBullseye
  FaceMakerMode = 3
  LengthFwd = 4
  LengthRev = 0
  Placement = pos=(0,12.6,0) rot=(0,0,1;0rad)
  Solid = true
  Symmetric = false
FEATURE [Sketcher::SketchObject] Sketch147  label="scavo_led_stato_batteria"
  ArcFitTolerance = 1e-06
  AttachmentSupport = -> [XZ_Plane]
  ExternalGeometry = -> [Sketch016]
  FullyConstrained = true
  MakeInternals = false
  MapMode = 5
  Placement = pos=(0,0,0) rot=(1,0,0;1.5708rad)
  sketch-geometry (5):
    g0: LineSegment StartX=-215.843 StartY=-56.2316 StartZ=0 EndX=-215.843 EndY=-65.4316 EndZ=0
    g1: LineSegment StartX=-215.843 StartY=-65.4316 StartZ=0 EndX=-211.043 EndY=-65.4316 EndZ=0
    g2: LineSegment StartX=-211.043 StartY=-65.4316 StartZ=0 EndX=-211.043 EndY=-56.2316 EndZ=0
    g3: LineSegment StartX=-211.043 StartY=-56.2316 StartZ=0 EndX=-215.843 EndY=-56.2316 EndZ=0
    g4: GeomPoint [constr] X=-213.443 Y=-60.8316 Z=0
  constraints (13):
    c: Coincident(g0,g1)
    c: Coincident(g1,g2)
    c: Coincident(g2,g3)
    c: Coincident(g3,g0)
    c: Distance(g0,g2) = 4.8
    c: Distance(g1,g3) = 9.2
    c: Equal(g0,g2)
    c: Equal(g1,g3)
    c: Perpendicular(g3,g0)
    c: DistanceY(g-3,g0) = 11.4
    c: Vertical(g2)
    c: Symmetric(g0,g2,g4)
    c: Vertical(g4,g-3)
FEATURE [Part::Extrusion] Extrude087  label="Extrude087 - scavo_led_stato_batteria"
  Base = -> Sketch147
  Dir = (0,-1,2e-16)
  DirMode = 2
  FaceMakerClass = Part::FaceMakerBullseye
  FaceMakerMode = 3
  LengthFwd = 2.2
  LengthRev = 0
  Placement = pos=(0,12.6,0) rot=(0,0,1;0rad)
  Solid = true
  Symmetric = false
FEATURE [Sketcher::SketchObject] Sketch148
  ArcFitTolerance = 1e-06
  AttachmentSupport = -> [Pad016]
  ExternalGeometry = -> [Pad016]
  FullyConstrained = true
  MakeInternals = false
  MapMode = 5
  Placement = pos=(0,0,-80.4316) rot=(1,0,0;3.14159rad)
  sketch-geometry (8):
    g0: LineSegment StartX=-176.685 StartY=3.6 StartZ=0 EndX=-186.685 EndY=3.6 EndZ=0
    g1: LineSegment StartX=-176.685 StartY=3.6 StartZ=0 EndX=-176.685 EndY=-9e-16 EndZ=0
    g2: LineSegment [constr] StartX=-186.685 StartY=3.6 StartZ=0 EndX=-186.685 EndY=-9e-16 EndZ=0
    g3: ArcOfEllipse CenterX=-186.685 CenterY=-1e-15 CenterZ=0 NormalX=0 NormalY=0 NormalZ=1 MajorRadius=10 MinorRadius=3.6 AngleXU=0 StartAngle=0 EndAngle=1.5708
    g4: LineSegment [constr] StartX=-176.685 StartY=-1e-15 StartZ=0 EndX=-196.685 EndY=-1e-15 EndZ=0
    g5: LineSegment [constr] StartX=-186.685 StartY=3.6 StartZ=0 EndX=-186.685 EndY=-3.6 EndZ=0
    g6: GeomPoint [constr] X=-177.356 Y=-1e-15 Z=0
    g7: GeomPoint [constr] X=-196.015 Y=-1e-15 Z=0
  constraints (13):
    c: Distance(g0) = 10
    c: Coincident(g0,g-5)
    c: PointOnObject(g0,g-3)
    c: Coincident(g1,g0)
    c: Coincident(g1,g-5)
    c: Coincident(g2,g0)
    c: Vertical(g2)
    c: PointOnObject(g2,g-4)
    c: InternalAlignment(g4-g7 -> g3) x4
    c: Coincident(g3,g2)
    c: Coincident(g3,g0)
    c: Coincident(g3,g1)
    c: Horizontal(g4)
FEATURE [PartDesign::SubtractivePipe] SubtractivePipe004
  AuxilleryCurvelinear = true
  AuxillerySpineTangent = false
  BaseFeature = -> Pad016
  Binormal = (0,0,0)
  Mode = 0
  Profile = -> Sketch148
  Refine = true
  Spine = -> Pad016 [Edge254]
  SpineTangent = false
  Suppressed = false
  Transformation = 0
  Transition = 0
FEATURE [Sketcher::SketchObject] Sketch149
  ArcFitTolerance = 1e-06
  AttachmentSupport = -> [Pad016]
  ExternalGeometry = -> [Pad016]
  FullyConstrained = true
  MakeInternals = false
  MapMode = 5
  Placement = pos=(0,0,-80.4316) rot=(1,0,0;3.14159rad)
  sketch-geometry (8):
    g0: LineSegment StartX=-215.932 StartY=3.6 StartZ=0 EndX=-205.932 EndY=3.6 EndZ=0
    g1: LineSegment StartX=-215.932 StartY=3.6 StartZ=0 EndX=-215.932 EndY=-4e-16 EndZ=0
    g2: LineSegment [constr] StartX=-205.932 StartY=3.6 StartZ=0 EndX=-205.932 EndY=-9e-16 EndZ=0
    g3: ArcOfEllipse CenterX=-205.932 CenterY=-1e-15 CenterZ=0 NormalX=0 NormalY=0 NormalZ=1 MajorRadius=10 MinorRadius=3.6 AngleXU=-3.14159 StartAngle=4.71239 EndAngle=6.28319
    g4: LineSegment [constr] StartX=-215.932 StartY=-1e-15 StartZ=0 EndX=-195.932 EndY=-1e-15 EndZ=0
    g5: LineSegment [constr] StartX=-205.932 StartY=-3.6 StartZ=0 EndX=-205.932 EndY=3.6 EndZ=0
    g6: GeomPoint [constr] X=-215.262 Y=-1.1e-15 Z=0
    g7: GeomPoint [constr] X=-196.602 Y=-9e-16 Z=0
  constraints (13):
    c: Distance(g0) = 10
    c: Coincident(g0,g-5)
    c: PointOnObject(g0,g-5)
    c: Coincident(g1,g0)
    c: Coincident(g1,g-4)
    c: Coincident(g2,g0)
    c: Vertical(g2)
    c: PointOnObject(g2,g-3)
    c: InternalAlignment(g4-g7 -> g3) x4
    c: Coincident(g3,g2)
    c: Coincident(g3,g0)
    c: Coincident(g3,g1)
    c: Horizontal(g4)
FEATURE [PartDesign::SubtractivePipe] SubtractivePipe005
  AuxilleryCurvelinear = true
  AuxillerySpineTangent = false
  BaseFeature = -> SubtractivePipe004
  Binormal = (0,0,0)
  Mode = 0
  Profile = -> Sketch149
  Refine = true
  Spine = -> Pad016 [Edge256,Edge251,Edge252]
  SpineTangent = false
  Suppressed = false
  Transformation = 0
  Transition = 0
FEATURE [PartDesign::SubtractiveLoft] SubtractiveLoft002
  BaseFeature = -> SubtractivePipe005
  Closed = false
  Profile = -> Sketch129
  Refine = true
  Ruled = false
  Sections = -> [Sketch130]
  Suppressed = false
FEATURE [PartDesign::SubtractiveLoft] SubtractiveLoft003
  BaseFeature = -> SubtractiveLoft002
  Closed = false
  Profile = -> Clone2D001
  Refine = true
  Ruled = false
  Sections = -> [Sketch131]
  Suppressed = false
FEATURE [PartDesign::Chamfer] Chamfer010
  Angle = 45
  Base = -> SubtractiveLoft003 [Edge203,Edge204,Edge202,Edge201,Edge195]
  BaseFeature = -> SubtractiveLoft003
  ChamferType = 0
  FlipDirection = false
  Refine = true
  Size = 1.5
  Size2 = 1
  SupportTransform = false
  Suppressed = false
  UseAllEdges = false
FEATURE [PartDesign::Chamfer] Chamfer011
  Angle = 45
  Base = -> Chamfer010 [Edge15]
  BaseFeature = -> Chamfer010
  ChamferType = 0
  FlipDirection = false
  Refine = true
  Size = 1.6
  Size2 = 1
  SupportTransform = false
  Suppressed = false
  UseAllEdges = false
FEATURE [PartDesign::Chamfer] Chamfer012
  Angle = 45
  Base = -> Chamfer011 [Edge10]
  BaseFeature = -> Chamfer011
  ChamferType = 0
  FlipDirection = false
  Refine = true
  Size = 3.5
  Size2 = 1
  SupportTransform = false
  Suppressed = false
  UseAllEdges = false
FEATURE [PartDesign::Chamfer] Chamfer013
  Angle = 45
  Base = -> Chamfer012 [Edge94]
  BaseFeature = -> Chamfer012
  ChamferType = 0
  FlipDirection = false
  Refine = true
  Size = 1.9
  Size2 = 1
  SupportTransform = false
  Suppressed = false
  UseAllEdges = false
FEATURE [PartDesign::Fillet] Fillet007
  Base = -> Chamfer013 [Edge83]
  BaseFeature = -> Chamfer013
  Radius = 1.1
  Refine = true
  SupportTransform = false
  Suppressed = false
  UseAllEdges = false
FEATURE [PartDesign::Fillet] Fillet008
  Base = -> Fillet007 [Edge75]
  BaseFeature = -> Fillet007
  Radius = 1.9
  Refine = true
  SupportTransform = false
  Suppressed = false
  UseAllEdges = false
FEATURE [PartDesign::Pocket] Pocket011
  BaseFeature = -> Fillet008
  Direction = (0,1,-2e-16)
  Length = 0.8
  Length2 = 5
  Profile = -> Sketch132
  ReferenceAxis = -> Sketch132 [N_Axis]
  Refine = true
  Suppressed = false
  Type = 0
FEATURE [PartDesign::Pocket] Pocket012
  BaseFeature = -> Pocket011
  Direction = (0,1,0)
  Length = 1
  Length2 = 5
  Profile = -> ShapeString
  ReferenceAxis = -> ShapeString [N_Axis]
  Refine = true
  Suppressed = false
  Type = 0
FEATURE [PartDesign::Body] Body007  label="lato DX"
  AllowCompound = false
  Group = -> [Binder001,Sketch114,Pad011,Chamfer014,Sketch115,Pocket006,Sketch116,Pad012,Sketch117,Pocket007,Sketch118,Pad013,Sketch119,Pocket008,Pad017,Chamfer009,Pocket009,Sketch123,Sketch120,Pad014,Pad018,Chamfer008,Pocket010,Sketch121,Pad015,Sketch122,Pad016,SubtractivePipe004,SubtractivePipe005,Sketch149,Sketch148,Sketch124,Sketch125,Sketch126,Sketch129,Sketch130,Clone2D001,Sketch131,SubtractiveLoft002,+11 more]
  Origin = -> Origin007
  Tip = -> Pocket012
FEATURE [Sketcher::SketchObject] Sketch150
  ArcFitTolerance = 1e-06
  AttachmentSupport = -> [Pad008]
  ExternalGeometry = -> [Pad008]
  FullyConstrained = true
  MakeInternals = false
  MapMode = 5
  Placement = pos=(0,3.6,0) rot=(0,0.707107,0.707107;3.14159rad)
  sketch-geometry (7):
    g0: LineSegment [constr] StartX=210.343 StartY=-66.0316 StartZ=0 EndX=210.343 EndY=-72.8316 EndZ=0
    g1: LineSegment [constr] StartX=210.343 StartY=-72.8316 StartZ=0 EndX=216.543 EndY=-72.8316 EndZ=0
    g2: LineSegment [constr] StartX=216.543 StartY=-72.8316 StartZ=0 EndX=216.543 EndY=-66.0316 EndZ=0
    g3: LineSegment [constr] StartX=216.543 StartY=-66.0316 StartZ=0 EndX=210.343 EndY=-66.0316 EndZ=0
    g4: LineSegment [constr] StartX=210.343 StartY=-72.8316 StartZ=0 EndX=216.543 EndY=-66.0316 EndZ=0
    g5: LineSegment [constr] StartX=210.343 StartY=-66.0316 StartZ=0 EndX=213.443 EndY=-69.4316 EndZ=0
    g6: Circle CenterX=213.443 CenterY=-69.4316 CenterZ=0 NormalX=0 NormalY=0 NormalZ=1 AngleXU=0 Radius=2
  constraints (18):
    c: Coincident(g0,g1)
    c: Coincident(g1,g2)
    c: Coincident(g2,g3)
    c: Coincident(g3,g0)
    c: Vertical(g0)
    c: Vertical(g2)
    c: Horizontal(g1)
    c: Horizontal(g3)
    c: Distance(g0,g2) = 6.2
    c: Distance(g1,g3) = 6.8
    c: DistanceY(g-3,g1) = 4
    c: Coincident(g4,g0)
    c: Coincident(g4,g2)
    c: Coincident(g5,g0)
    c: Symmetric(g0,g2,g5)
    c: Diameter(g6) = 4
    c: Coincident(g6,g5)
    c: Vertical(g5,g-3)
FEATURE [Sketcher::SketchObject] Sketch151
  ArcFitTolerance = 1e-06
  AttachmentSupport = -> [Pad008]
  ExternalGeometry = -> [Pad008]
  FullyConstrained = true
  MakeInternals = false
  MapMode = 5
  Placement = pos=(0,3.6,0) rot=(0,0.707107,0.707107;3.14159rad)
  sketch-geometry (10):
    g0: LineSegment [constr] StartX=211.143 StartY=-56.2316 StartZ=0 EndX=211.143 EndY=-65.4316 EndZ=0
    g1: LineSegment [constr] StartX=211.143 StartY=-65.4316 StartZ=0 EndX=215.743 EndY=-65.4316 EndZ=0
    g2: LineSegment [constr] StartX=215.743 StartY=-65.4316 StartZ=0 EndX=215.743 EndY=-56.2316 EndZ=0
    g3: LineSegment [constr] StartX=215.743 StartY=-56.2316 StartZ=0 EndX=211.143 EndY=-56.2316 EndZ=0
    g4: LineSegment StartX=212.243 StartY=-63.8316 StartZ=0 EndX=214.643 EndY=-63.8316 EndZ=0
    g5: LineSegment StartX=214.643 StartY=-63.8316 StartZ=0 EndX=214.643 EndY=-57.0316 EndZ=0
    g6: LineSegment StartX=214.643 StartY=-57.0316 StartZ=0 EndX=212.243 EndY=-57.0316 EndZ=0
    g7: LineSegment StartX=212.243 StartY=-57.0316 StartZ=0 EndX=212.243 EndY=-63.8316 EndZ=0
    g8: GeomPoint [constr] X=213.443 Y=-60.4316 Z=0
    g9: GeomPoint [constr] X=213.443 Y=-60.8316 Z=0
  constraints (26):
    c: Coincident(g0,g1)
    c: Coincident(g1,g2)
    c: Coincident(g2,g3)
    c: Coincident(g3,g0)
    c: Vertical(g0)
    c: Vertical(g2)
    c: Horizontal(g1)
    c: Horizontal(g3)
    c: Distance(g0,g2) = 4.6
    c: Distance(g1,g3) = 9.2
    c: DistanceY(g-3,g1) = 11.4
    c: Coincident(g4,g5)
    c: Coincident(g5,g6)
    c: Coincident(g6,g7)
    c: Coincident(g7,g4)
    c: Horizontal(g4)
    c: Horizontal(g6)
    c: Vertical(g5)
    c: Vertical(g7)
    c: Symmetric(g6,g4,g8)
    c: Distance(g5,g7) = 2.4
    c: Distance(g4,g6) = 6.8
    c: Symmetric(g2,g0,g9)
    c: Vertical(g8,g9)
    c: DistanceY(g1,g4) = 1.6
    c: Vertical(g9,g-3)
FEATURE [PartDesign::Pocket] Pocket019
  BaseFeature = -> Pocket013
  Direction = (0,-1,2e-16)
  Length = 3.6
  Length2 = 5
  Profile = -> Sketch151
  ReferenceAxis = -> Sketch151 [N_Axis]
  Refine = true
  Suppressed = false
  Type = 0
FEATURE [PartDesign::Pocket] Pocket018
  BaseFeature = -> Pocket019
  Direction = (0,-1,2e-16)
  Length = 3.6
  Length2 = 5
  Profile = -> Sketch150
  ReferenceAxis = -> Sketch150 [N_Axis]
  Refine = true
  Suppressed = false
  Type = 0
FEATURE [PartDesign::Point] DatumPoint
  AttacherType = Attacher::AttachEnginePoint
  AttachmentSupport = -> [Sketch150]
  MapMode = 36
  Placement = pos=(-213.443,3.6,-69.4316) rot=(0,1,0;3.14159rad)
FEATURE [PartDesign::Plane] DatumPlane002
  AttachmentSupport = -> [DatumPoint]
  Length = 260.281
  MapMode = 1
  Placement = pos=(-213.443,3.6,-69.4316) rot=(0,0,1;0rad)
  ResizeMode = 0
  Width = 71.8377
FEATURE [Sketcher::SketchObject] Sketch152
  ArcFitTolerance = 1e-06
  AttachmentSupport = -> [DatumPlane002]
  ExternalGeometry = -> [Sketch150]
  FullyConstrained = true
  MakeInternals = false
  MapMode = 5
  Placement = pos=(-213.443,3.6,-69.4316) rot=(0,0,1;0rad)
  sketch-geometry (7):
    g0: LineSegment StartX=0 StartY=0 StartZ=0 EndX=-4 EndY=3.8e-15 EndZ=0
    g1: ArcOfEllipse CenterX=0 CenterY=0 CenterZ=0 NormalX=0 NormalY=0 NormalZ=1 MajorRadius=4 MinorRadius=3.6 AngleXU=3.14159 StartAngle=2e-16 EndAngle=1.5708
    g2: LineSegment [constr] StartX=-4 StartY=9e-16 StartZ=0 EndX=4 EndY=-9e-16 EndZ=0
    g3: LineSegment [constr] StartX=0 StartY=-3.6 StartZ=0 EndX=0 EndY=3.6 EndZ=0
    g4: GeomPoint [constr] X=-1.74356 Y=2e-15 Z=0
    g5: GeomPoint [constr] X=1.74356 Y=-2e-15 Z=0
    g6: LineSegment StartX=0 StartY=0 StartZ=0 EndX=-4.4e-15 EndY=-3.6 EndZ=0
  constraints (11):
    c: PointOnObject(g1,g-2)
    c: Distance(g0) = 4
    c: PointOnObject(g0,g-1)
    c: InternalAlignment(g2-g5 -> g1) x4
    c: Coincident(g1,g0)
    c: Vertical(g3)
    c: Coincident(g1,g-1)
    c: Distance(g6) = 3.6
    c: Coincident(g6,g1)
    c: Coincident(g1,g6)
    c: Coincident(g0,g1)
FEATURE [PartDesign::Groove] Groove
  Angle = 360
  Angle2 = 60
  Axis = (0,1,0)
  Base = (-213.443,3.6,-69.4316)
  BaseFeature = -> Pocket018
  Profile = -> Sketch152
  ReferenceAxis = -> Sketch152 [V_Axis]
  Refine = true
  Reversed = true
  Suppressed = false
  Type = 0
FEATURE [PartDesign::Body] Body006  label="lato SX"
  AllowCompound = false
  Group = -> [Binder,Pad019,Chamfer015,Pocket002,Sketch133,Sketch091,Pad005,Sketch092,Pocket001,Sketch093,Sketch094,Pad006,Sketch095,Pad007,Sketch096,Pad008,Sketch097,Pad009,Chamfer005,Pocket004,Sketch098,Pad010,Chamfer006,Pocket003,SubtractivePipe,SubtractivePipe001,Sketch099,Sketch106,Sketch107,Sketch108,Clone2D,Sketch109,SubtractiveLoft,SubtractiveLoft001,Sketch110,Sketch111,Sketch112,Chamfer016,Chamfer017,+15 more]
  Origin = -> Origin006
  Tip = -> Groove
FEATURE [Sketcher::SketchObject] Sketch153  label="ripieno_per_sostegno_led_batteria"
  ArcFitTolerance = 1e-06
  AttachmentSupport = -> [XZ_Plane]
  ExternalGeometry = -> [Sketch036]
  FullyConstrained = true
  MakeInternals = false
  MapMode = 5
  Placement = pos=(0,0,0) rot=(1,0,0;1.5708rad)
  sketch-geometry (4):
    g0: LineSegment StartX=-217.343 StartY=-54.5944 StartZ=0 EndX=-217.343 EndY=-63.1944 EndZ=0
    g1: LineSegment StartX=-217.343 StartY=-63.1944 StartZ=0 EndX=-211.843 EndY=-63.1944 EndZ=0
    g2: LineSegment StartX=-211.843 StartY=-63.1944 StartZ=0 EndX=-211.843 EndY=-54.5944 EndZ=0
    g3: LineSegment StartX=-211.843 StartY=-54.5944 StartZ=0 EndX=-217.343 EndY=-54.5944 EndZ=0
  constraints (11):
    c: Coincident(g0,g1)
    c: Coincident(g1,g2)
    c: Coincident(g2,g3)
    c: Coincident(g3,g0)
    c: Vertical(g0)
    c: Horizontal(g1)
    c: Horizontal(g3)
    c: Tangent(g2,g-3)
    c: DistanceY(g2,g-3) = 4.5
    c: DistanceX(g3,g3) = 5.5
    c: DistanceY(g0,g0) = 8.6
FEATURE [PartDesign::Body] Body  label="Struttura pistola"
  AllowCompound = false
  Group = -> [Sketch,Sketch002,Sketch004,DatumPlane,Sketch005,DatumPlane001,CopyCut,Sketch008,Sketch009,Sketch010,Sketch011,Sketch012,Sketch013,Sketch014,Sketch015,Sketch016,Sketch017,Sketch018,Sketch019,Sketch020,Sketch022,Sketch023,Sketch024,Sketch025,Sketch026,Sketch027,Sketch029,Sketch030,Sketch031,Sketch032,Sketch033,Sketch034,Sketch035,Sketch036,Sketch037,Sketch038,Sketch039,Sketch040,Sketch041,Sketch042,+28 more]
  Origin = -> Origin
FEATURE [Part::Extrusion] Extrude088  label="Extrude088 - ripieno_per_sostegno_led_batteria"
  Base = -> Sketch153
  Dir = (0,-1,2e-16)
  DirMode = 2
  FaceMakerClass = Part::FaceMakerBullseye
  FaceMakerMode = 3
  LengthFwd = 4
  LengthRev = 0
  Placement = pos=(0,12.6,0) rot=(0,0,1;0rad)
  Solid = true
  Symmetric = false
FEATURE [Part::MultiFuse] Fusion004
  Refine = true
  Shapes = -> [Cut050,Extrude088]
FEATURE [Part::Cut] Cut051
  Base = -> Fusion004
  Refine = true
  Tool = -> Extrude087
FEATURE [Part::Cut] Cut052
  Base = -> Cut051
  Refine = true
  Tool = -> Extrude086
note: 2 file-system paths scrubbed to <path> (originals preserved in the JSON sidecar)
